# Revit family: QMXVP_with_1X2_Mixing_Box_Ends
name_source: partatom
category: Mechanical Equipment
units: mm (PartAtom-declared; Revit-internal decimal feet)

## family parameters
Always vertical = Yes
Cut with Voids When Loaded = No
Part Type = Normal
Room Calculation Point = No
Round Connector Dimension = Use Diameter
Shared = No
Work Plane-Based = No

## types (224) — shared parameters
0 = 0"
1" = 1"
1.5 = 1 1/2"
1/4 = 1/4"
135 = 135.00°
2" = 2"
2' = 24"
3" = 3"
3.125" = 3 1/8"
4" = 4"
5" = 5"
6" = 6"
Manufacturer = Loren Cook Company
ONE EIGTH = 1/8"
URL = www.lorencook.com

## per-type parameters (varying)
- 90_QMXVP-9L-1X2_Mixing_Box_Ends: (A/2)+.25"=14 1/4"; (A/2)+.5"=-14 1/2"; (A/2)-.5"=-13 1/2"; (A/2)-2"=12"; (NOZZLE_HEIGHT-(NOZZLE_HEIGHT/8*2))/2=10 1/2"; (NOZZLE_WB_OD-NOZZLE_TOP_OD)/2=2 3/8"; -A=-28"; A=28"; A+.5=28 1/2"; A/2=14"; B=65"; B/2=32 1/2"; C=30"; C/2=15"; DUAL_F=64"; DUAL_F+1"=65"; DUAL_G=63 5/16"; E=27 3/16"; GA=3/32"; LONG_RO=57 1/16"; LONG_RO/2=28 17/32"; MB_A=34"; MB_HT=29 3/16"; MB_HT+.25"=29 7/16"; MB_HT-2.75"=26 7/16"; MB_HT/2=14 19/32"; Model=QMXVP-1X2_Mixing Box_Sides; NOZZLE_BOTTOM_ID=12 13/16"; NOZZLE_BOTTOM_RAD=6 13/32"; NOZZLE_HEIGHT=28"; NOZZLE_HEIGHT/7*2=7"; NOZZLE_SIZE=108"; NOZZLE_TOP_OD=13 1/2"; NOZZLE_TOP_RAD=6 3/4"; NOZZLE_WB/4=4 19/32"; NOZZLE_WB_OD=23"; NOZZLE_WB_RAD=11 1/2"; NOZZLE_WB_RAD-2"=9 1/2"; RO=21"; RO/2=10 1/2"; RO2/2=10 1/2"; TRANSITION_TOP=37 1/16"; TYPE=0"; Type Comments=Vari-Plume Laboratory Exhaust Mixed-Flow Inline Belt Drive With 1X2 Mixing Box With Weather Hoods On Sides; UNIT_HEIGHT=19 7/8"; UNIT_HEIGHT*.75=14 29/32"; UNIT_OD=12 13/16"; UNIT_RAD+((A/2)+.25")=20 21/32"; UNIT_RAD+((A/2)+.25")+4"=24 21/32"; UNIT_RADIUS=6 13/32"; UNIT_RADIUS*.6=5 25/32"; UNIT_RADIUS+4"=10 13/32"
- 490_QMXVP-49H-1X2_Mixing_Box_Ends: (A/2)+.25"=40 1/4"; (A/2)+.5"=-40 1/2"; (A/2)-.5"=-39 1/2"; (A/2)-2"=38"; (NOZZLE_HEIGHT-(NOZZLE_HEIGHT/8*2))/2=41 1/4"; (NOZZLE_WB_OD-NOZZLE_TOP_OD)/2=6 1/4"; -A=-80"; A=80"; A+.5=80 1/2"; A/2=40"; B=219"; B/2=109 1/2"; C=103"; C/2=51 1/2"; DUAL_F=192"; DUAL_F+1"=193"; DUAL_G=191"; E=78 1/2"; GA=1/8"; LONG_RO=184 3/4"; LONG_RO/2=92 3/8"; MB_A=113"; MB_HT=86 15/16"; MB_HT+.25"=87 3/16"; MB_HT-2.75"=84 3/16"; MB_HT/2=43 15/32"; Model=QMXVP-1X2_Mixing Box_Sides; NOZZLE_BOTTOM_ID=69 3/8"; NOZZLE_BOTTOM_RAD=34 11/16"; NOZZLE_HEIGHT=110"; NOZZLE_HEIGHT/7*2=27 1/2"; NOZZLE_SIZE=588"; NOZZLE_TOP_OD=76"; NOZZLE_TOP_RAD=38"; NOZZLE_WB/4=20 3/16"; NOZZLE_WB_OD=101"; NOZZLE_WB_RAD=50 1/2"; NOZZLE_WB_RAD-2"=48 1/2"; RO=72 1/4"; RO/2=36 1/8"; RO2/2=36 1/8"; TRANSITION_TOP=96 3/4"; TYPE=0"; Type Comments=Vari-Plume Laboratory Exhaust Mixed-Flow Inline Belt Drive With 1X2 Mixing Box With Weather Hoods On Sides; UNIT_HEIGHT=80 1/2"; UNIT_HEIGHT*.75=60 3/8"; UNIT_OD=69 3/8"; UNIT_RAD+((A/2)+.25")=74 15/16"; UNIT_RAD+((A/2)+.25")+4"=78 15/16"; UNIT_RADIUS=34 11/16"; UNIT_RADIUS*.6=31 7/32"; UNIT_RADIUS+4"=38 11/16"
- 90_QMXVP-9H-1X2_Mixing_Box_Ends: (A/2)+.25"=14 1/4"; (A/2)+.5"=-14 1/2"; (A/2)-.5"=-13 1/2"; (A/2)-2"=12"; (NOZZLE_HEIGHT-(NOZZLE_HEIGHT/8*2))/2=10 1/2"; (NOZZLE_WB_OD-NOZZLE_TOP_OD)/2=2 3/8"; -A=-28"; A=28"; A+.5=28 1/2"; A/2=14"; B=65"; B/2=32 1/2"; C=30"; C/2=15"; DUAL_F=64"; DUAL_F+1"=65"; DUAL_G=63 5/16"; E=27 3/16"; GA=3/32"; LONG_RO=57 1/16"; LONG_RO/2=28 17/32"; MB_A=34"; MB_HT=29 3/16"; MB_HT+.25"=29 7/16"; MB_HT-2.75"=26 7/16"; MB_HT/2=14 19/32"; Model=QMXVP-1X2_Mixing Box_Sides; NOZZLE_BOTTOM_ID=12 13/16"; NOZZLE_BOTTOM_RAD=6 13/32"; NOZZLE_HEIGHT=28"; NOZZLE_HEIGHT/7*2=7"; NOZZLE_SIZE=108"; NOZZLE_TOP_OD=13 1/2"; NOZZLE_TOP_RAD=6 3/4"; NOZZLE_WB/4=4 19/32"; NOZZLE_WB_OD=23"; NOZZLE_WB_RAD=11 1/2"; NOZZLE_WB_RAD-2"=9 1/2"; RO=21"; RO/2=10 1/2"; RO2/2=10 1/2"; TRANSITION_TOP=37 1/16"; TYPE=0"; Type Comments=Vari-Plume Laboratory Exhaust Mixed-Flow Inline Belt Drive With 1X2 Mixing Box With Weather Hoods On Sides; UNIT_HEIGHT=19 7/8"; UNIT_HEIGHT*.75=14 29/32"; UNIT_OD=12 13/16"; UNIT_RAD+((A/2)+.25")=20 21/32"; UNIT_RAD+((A/2)+.25")+4"=24 21/32"; UNIT_RADIUS=6 13/32"; UNIT_RADIUS*.6=5 25/32"; UNIT_RADIUS+4"=10 13/32"
- 120_QMXVP-9L-1X2_Mixing_Box_Ends: (A/2)+.25"=14 1/4"; (A/2)+.5"=-14 1/2"; (A/2)-.5"=-13 1/2"; (A/2)-2"=12"; (NOZZLE_HEIGHT-(NOZZLE_HEIGHT/8*2))/2=10 1/2"; (NOZZLE_WB_OD-NOZZLE_TOP_OD)/2=2 3/8"; -A=-28"; A=28"; A+.5=28 1/2"; A/2=14"; B=71"; B/2=35 1/2"; C=37"; C/2=18 1/2"; DUAL_F=64"; DUAL_F+1"=65"; DUAL_G=63 5/16"; E=27 3/16"; GA=3/32"; LONG_RO=57 1/16"; LONG_RO/2=28 17/32"; MB_A=35"; MB_HT=31 7/16"; MB_HT+.25"=31 11/16"; MB_HT-2.75"=28 11/16"; MB_HT/2=15 23/32"; Model=QMXVP-1X2_Mixing Box_Sides; NOZZLE_BOTTOM_ID=12 13/16"; NOZZLE_BOTTOM_RAD=6 13/32"; NOZZLE_HEIGHT=28"; NOZZLE_HEIGHT/7*2=7"; NOZZLE_SIZE=108"; NOZZLE_TOP_OD=13 1/2"; NOZZLE_TOP_RAD=6 3/4"; NOZZLE_WB/4=4 19/32"; NOZZLE_WB_OD=23"; NOZZLE_WB_RAD=11 1/2"; NOZZLE_WB_RAD-2"=9 1/2"; RO=21"; RO/2=10 1/2"; RO2/2=10 1/2"; TRANSITION_TOP=43 3/16"; TYPE=0"; Type Comments=Vari-Plume Laboratory Exhaust Mixed-Flow Inline Belt Drive With 1X2 Mixing Box With Weather Hoods On Sides; UNIT_HEIGHT=19 7/8"; UNIT_HEIGHT*.75=14 29/32"; UNIT_OD=17 1/16"; UNIT_RAD+((A/2)+.25")=22 25/32"; UNIT_RAD+((A/2)+.25")+4"=26 25/32"; UNIT_RADIUS=8 17/32"; UNIT_RADIUS*.6=7 11/16"; UNIT_RADIUS+4"=12 17/32"
- 120_QMXVP-9H-1X2_Mixing_Box_Ends: (A/2)+.25"=14 1/4"; (A/2)+.5"=-14 1/2"; (A/2)-.5"=-13 1/2"; (A/2)-2"=12"; (NOZZLE_HEIGHT-(NOZZLE_HEIGHT/8*2))/2=10 1/2"; (NOZZLE_WB_OD-NOZZLE_TOP_OD)/2=2 3/8"; -A=-28"; A=28"; A+.5=28 1/2"; A/2=14"; B=71"; B/2=35 1/2"; C=37"; C/2=18 1/2"; DUAL_F=64"; DUAL_F+1"=65"; DUAL_G=63 5/16"; E=27 3/16"; GA=3/32"; LONG_RO=57 1/16"; LONG_RO/2=28 17/32"; MB_A=35"; MB_HT=31 7/16"; MB_HT+.25"=31 11/16"; MB_HT-2.75"=28 11/16"; MB_HT/2=15 23/32"; Model=QMXVP-1X2_Mixing Box_Sides; NOZZLE_BOTTOM_ID=12 13/16"; NOZZLE_BOTTOM_RAD=6 13/32"; NOZZLE_HEIGHT=28"; NOZZLE_HEIGHT/7*2=7"; NOZZLE_SIZE=108"; NOZZLE_TOP_OD=13 1/2"; NOZZLE_TOP_RAD=6 3/4"; NOZZLE_WB/4=4 19/32"; NOZZLE_WB_OD=23"; NOZZLE_WB_RAD=11 1/2"; NOZZLE_WB_RAD-2"=9 1/2"; RO=21"; RO/2=10 1/2"; RO2/2=10 1/2"; TRANSITION_TOP=43 3/16"; TYPE=0"; Type Comments=Vari-Plume Laboratory Exhaust Mixed-Flow Inline Belt Drive With 1X2 Mixing Box With Weather Hoods On Sides; UNIT_HEIGHT=19 7/8"; UNIT_HEIGHT*.75=14 29/32"; UNIT_OD=17 1/16"; UNIT_RAD+((A/2)+.25")=22 25/32"; UNIT_RAD+((A/2)+.25")+4"=26 25/32"; UNIT_RADIUS=8 17/32"; UNIT_RADIUS*.6=7 11/16"; UNIT_RADIUS+4"=12 17/32"
- 120_QMXVP-12L-1X2_Mixing_Box_Ends: (A/2)+.25"=14 1/4"; (A/2)+.5"=-14 1/2"; (A/2)-.5"=-13 1/2"; (A/2)-2"=12"; (NOZZLE_HEIGHT-(NOZZLE_HEIGHT/8*2))/2=12"; (NOZZLE_WB_OD-NOZZLE_TOP_OD)/2=2 1/8"; -A=-28"; A=28"; A+.5=28 1/2"; A/2=14"; B=71"; B/2=35 1/2"; C=37"; C/2=18 1/2"; DUAL_F=64"; DUAL_F+1"=65"; DUAL_G=63 5/16"; E=27 3/16"; GA=3/32"; LONG_RO=57 1/16"; LONG_RO/2=28 17/32"; MB_A=35"; MB_HT=31 7/16"; MB_HT+.25"=31 11/16"; MB_HT-2.75"=28 11/16"; MB_HT/2=15 23/32"; Model=QMXVP-1X2_Mixing Box_Sides; NOZZLE_BOTTOM_ID=17 1/16"; NOZZLE_BOTTOM_RAD=8 17/32"; NOZZLE_HEIGHT=32"; NOZZLE_HEIGHT/7*2=8"; NOZZLE_SIZE=144"; NOZZLE_TOP_OD=19 1/2"; NOZZLE_TOP_RAD=9 3/4"; NOZZLE_WB/4=5 19/32"; NOZZLE_WB_OD=28"; NOZZLE_WB_RAD=14"; NOZZLE_WB_RAD-2"=12"; RO=21"; RO/2=10 1/2"; RO2/2=10 1/2"; TRANSITION_TOP=39 7/16"; TYPE=0"; Type Comments=Vari-Plume Laboratory Exhaust Mixed-Flow Inline Belt Drive With 1X2 Mixing Box With Weather Hoods On Sides; UNIT_HEIGHT=19 7/8"; UNIT_HEIGHT*.75=14 29/32"; UNIT_OD=17 1/16"; UNIT_RAD+((A/2)+.25")=22 25/32"; UNIT_RAD+((A/2)+.25")+4"=26 25/32"; UNIT_RADIUS=8 17/32"; UNIT_RADIUS*.6=7 11/16"; UNIT_RADIUS+4"=12 17/32"
- 120_QMXVP-12H-1X2_Mixing_Box_Ends: (A/2)+.25"=14 1/4"; (A/2)+.5"=-14 1/2"; (A/2)-.5"=-13 1/2"; (A/2)-2"=12"; (NOZZLE_HEIGHT-(NOZZLE_HEIGHT/8*2))/2=12"; (NOZZLE_WB_OD-NOZZLE_TOP_OD)/2=2 1/8"; -A=-28"; A=28"; A+.5=28 1/2"; A/2=14"; B=71"; B/2=35 1/2"; C=37"; C/2=18 1/2"; DUAL_F=64"; DUAL_F+1"=65"; DUAL_G=63 5/16"; E=27 3/16"; GA=3/32"; LONG_RO=57 1/16"; LONG_RO/2=28 17/32"; MB_A=35"; MB_HT=31 7/16"; MB_HT+.25"=31 11/16"; MB_HT-2.75"=28 11/16"; MB_HT/2=15 23/32"; Model=QMXVP-1X2_Mixing Box_Sides; NOZZLE_BOTTOM_ID=17 1/16"; NOZZLE_BOTTOM_RAD=8 17/32"; NOZZLE_HEIGHT=32"; NOZZLE_HEIGHT/7*2=8"; NOZZLE_SIZE=144"; NOZZLE_TOP_OD=19 1/2"; NOZZLE_TOP_RAD=9 3/4"; NOZZLE_WB/4=5 19/32"; NOZZLE_WB_OD=28"; NOZZLE_WB_RAD=14"; NOZZLE_WB_RAD-2"=12"; RO=21"; RO/2=10 1/2"; RO2/2=10 1/2"; TRANSITION_TOP=39 7/16"; TYPE=0"; Type Comments=Vari-Plume Laboratory Exhaust Mixed-Flow Inline Belt Drive With 1X2 Mixing Box With Weather Hoods On Sides; UNIT_HEIGHT=19 7/8"; UNIT_HEIGHT*.75=14 29/32"; UNIT_OD=17 1/16"; UNIT_RAD+((A/2)+.25")=22 25/32"; UNIT_RAD+((A/2)+.25")+4"=26 25/32"; UNIT_RADIUS=8 17/32"; UNIT_RADIUS*.6=7 11/16"; UNIT_RADIUS+4"=12 17/32"
- 135_QMXVP-9L-1X2_Mixing_Box_Ends: (A/2)+.25"=14 1/4"; (A/2)+.5"=-14 1/2"; (A/2)-.5"=-13 1/2"; (A/2)-2"=12"; (NOZZLE_HEIGHT-(NOZZLE_HEIGHT/8*2))/2=10 1/2"; (NOZZLE_WB_OD-NOZZLE_TOP_OD)/2=2 3/8"; -A=-28"; A=28"; A+.5=28 1/2"; A/2=14"; B=77"; B/2=38 1/2"; C=39"; C/2=19 1/2"; DUAL_F=64"; DUAL_F+1"=65"; DUAL_G=63 5/16"; E=27 1/8"; GA=3/32"; LONG_RO=57 1/16"; LONG_RO/2=28 17/32"; MB_A=36"; MB_HT=33 7/16"; MB_HT+.25"=33 11/16"; MB_HT-2.75"=30 11/16"; MB_HT/2=16 23/32"; Model=QMXVP-1X2_Mixing Box_Sides; NOZZLE_BOTTOM_ID=12 13/16"; NOZZLE_BOTTOM_RAD=6 13/32"; NOZZLE_HEIGHT=28"; NOZZLE_HEIGHT/7*2=7"; NOZZLE_SIZE=108"; NOZZLE_TOP_OD=13 1/2"; NOZZLE_TOP_RAD=6 3/4"; NOZZLE_WB/4=4 19/32"; NOZZLE_WB_OD=23"; NOZZLE_WB_RAD=11 1/2"; NOZZLE_WB_RAD-2"=9 1/2"; RO=20 15/16"; RO/2=10 15/32"; RO2/2=10 15/32"; TRANSITION_TOP=48 11/16"; TYPE=0"; Type Comments=Vari-Plume Laboratory Exhaust Mixed-Flow Inline Belt Drive With 1X2 Mixing Box With Weather Hoods On Sides; UNIT_HEIGHT=27"; UNIT_HEIGHT*.75=20 1/4"; UNIT_OD=19 1/4"; UNIT_RAD+((A/2)+.25")=23 7/8"; UNIT_RAD+((A/2)+.25")+4"=27 7/8"; UNIT_RADIUS=9 5/8"; UNIT_RADIUS*.6=8 21/32"; UNIT_RADIUS+4"=13 5/8"
- 135_QMXVP-9H-1X2_Mixing_Box_Ends: (A/2)+.25"=14 1/4"; (A/2)+.5"=-14 1/2"; (A/2)-.5"=-13 1/2"; (A/2)-2"=12"; (NOZZLE_HEIGHT-(NOZZLE_HEIGHT/8*2))/2=10 1/2"; (NOZZLE_WB_OD-NOZZLE_TOP_OD)/2=2 3/8"; -A=-28"; A=28"; A+.5=28 1/2"; A/2=14"; B=77"; B/2=38 1/2"; C=39"; C/2=19 1/2"; DUAL_F=64"; DUAL_F+1"=65"; DUAL_G=63 5/16"; E=27 1/8"; GA=3/32"; LONG_RO=57 1/16"; LONG_RO/2=28 17/32"; MB_A=36"; MB_HT=33 7/16"; MB_HT+.25"=33 11/16"; MB_HT-2.75"=30 11/16"; MB_HT/2=16 23/32"; Model=QMXVP-1X2_Mixing Box_Sides; NOZZLE_BOTTOM_ID=12 13/16"; NOZZLE_BOTTOM_RAD=6 13/32"; NOZZLE_HEIGHT=28"; NOZZLE_HEIGHT/7*2=7"; NOZZLE_SIZE=108"; NOZZLE_TOP_OD=13 1/2"; NOZZLE_TOP_RAD=6 3/4"; NOZZLE_WB/4=4 19/32"; NOZZLE_WB_OD=23"; NOZZLE_WB_RAD=11 1/2"; NOZZLE_WB_RAD-2"=9 1/2"; RO=20 15/16"; RO/2=10 15/32"; RO2/2=10 15/32"; TRANSITION_TOP=48 11/16"; TYPE=0"; Type Comments=Vari-Plume Laboratory Exhaust Mixed-Flow Inline Belt Drive With 1X2 Mixing Box With Weather Hoods On Sides; UNIT_HEIGHT=27"; UNIT_HEIGHT*.75=20 1/4"; UNIT_OD=19 1/4"; UNIT_RAD+((A/2)+.25")=23 7/8"; UNIT_RAD+((A/2)+.25")+4"=27 7/8"; UNIT_RADIUS=9 5/8"; UNIT_RADIUS*.6=8 21/32"; UNIT_RADIUS+4"=13 5/8"
- 150_QMXVP-9L-1X2_Mixing_Box_Ends: (A/2)+.25"=15 1/4"; (A/2)+.5"=-15 1/2"; (A/2)-.5"=-14 1/2"; (A/2)-2"=13"; (NOZZLE_HEIGHT-(NOZZLE_HEIGHT/8*2))/2=10 1/2"; (NOZZLE_WB_OD-NOZZLE_TOP_OD)/2=2 3/8"; -A=-30"; A=30"; A+.5=30 1/2"; A/2=15"; B=87"; B/2=43 1/2"; C=42"; C/2=21"; DUAL_F=68"; DUAL_F+1"=69"; DUAL_G=67 5/16"; E=29 1/8"; GA=3/32"; LONG_RO=61 1/16"; LONG_RO/2=30 17/32"; MB_A=38"; MB_HT=35 3/16"; MB_HT+.25"=35 7/16"; MB_HT-2.75"=32 7/16"; MB_HT/2=17 19/32"; Model=QMXVP-1X2_Mixing Box_Sides; NOZZLE_BOTTOM_ID=12 13/16"; NOZZLE_BOTTOM_RAD=6 13/32"; NOZZLE_HEIGHT=28"; NOZZLE_HEIGHT/7*2=7"; NOZZLE_SIZE=108"; NOZZLE_TOP_OD=13 1/2"; NOZZLE_TOP_RAD=6 3/4"; NOZZLE_WB/4=4 19/32"; NOZZLE_WB_OD=23"; NOZZLE_WB_RAD=11 1/2"; NOZZLE_WB_RAD-2"=9 1/2"; RO=22 15/16"; RO/2=11 15/32"; RO2/2=11 15/32"; TRANSITION_TOP=54 1/4"; TYPE=0"; Type Comments=Vari-Plume Laboratory Exhaust Mixed-Flow Inline Belt Drive With 1X2 Mixing Box With Weather Hoods On Sides; UNIT_HEIGHT=30"; UNIT_HEIGHT*.75=22 1/2"; UNIT_OD=21 3/8"; UNIT_RAD+((A/2)+.25")=25 15/16"; UNIT_RAD+((A/2)+.25")+4"=29 15/16"; UNIT_RADIUS=10 11/16"; UNIT_RADIUS*.6=9 5/8"; UNIT_RADIUS+4"=14 11/16"
- 135_QMXVP-12L-1X2_Mixing_Box_Ends: (A/2)+.25"=14 1/4"; (A/2)+.5"=-14 1/2"; (A/2)-.5"=-13 1/2"; (A/2)-2"=12"; (NOZZLE_HEIGHT-(NOZZLE_HEIGHT/8*2))/2=12"; (NOZZLE_WB_OD-NOZZLE_TOP_OD)/2=2 1/8"; -A=-28"; A=28"; A+.5=28 1/2"; A/2=14"; B=77"; B/2=38 1/2"; C=39"; C/2=19 1/2"; DUAL_F=64"; DUAL_F+1"=65"; DUAL_G=63 5/16"; E=27 1/8"; GA=3/32"; LONG_RO=57 1/16"; LONG_RO/2=28 17/32"; MB_A=36"; MB_HT=33 7/16"; MB_HT+.25"=33 11/16"; MB_HT-2.75"=30 11/16"; MB_HT/2=16 23/32"; Model=QMXVP-1X2_Mixing Box_Sides; NOZZLE_BOTTOM_ID=17 1/16"; NOZZLE_BOTTOM_RAD=8 17/32"; NOZZLE_HEIGHT=32"; NOZZLE_HEIGHT/7*2=8"; NOZZLE_SIZE=144"; NOZZLE_TOP_OD=19 1/2"; NOZZLE_TOP_RAD=9 3/4"; NOZZLE_WB/4=5 19/32"; NOZZLE_WB_OD=28"; NOZZLE_WB_RAD=14"; NOZZLE_WB_RAD-2"=12"; RO=20 15/16"; RO/2=10 15/32"; RO2/2=10 15/32"; TRANSITION_TOP=40 11/16"; TYPE=0"; Type Comments=Vari-Plume Laboratory Exhaust Mixed-Flow Inline Belt Drive With 1X2 Mixing Box With Weather Hoods On Sides; UNIT_HEIGHT=27"; UNIT_HEIGHT*.75=20 1/4"; UNIT_OD=19 1/4"; UNIT_RAD+((A/2)+.25")=23 7/8"; UNIT_RAD+((A/2)+.25")+4"=27 7/8"; UNIT_RADIUS=9 5/8"; UNIT_RADIUS*.6=8 21/32"; UNIT_RADIUS+4"=13 5/8"
- 135_QMXVP-12H-1X2_Mixing_Box_Ends: (A/2)+.25"=14 1/4"; (A/2)+.5"=-14 1/2"; (A/2)-.5"=-13 1/2"; (A/2)-2"=12"; (NOZZLE_HEIGHT-(NOZZLE_HEIGHT/8*2))/2=12"; (NOZZLE_WB_OD-NOZZLE_TOP_OD)/2=2 1/8"; -A=-28"; A=28"; A+.5=28 1/2"; A/2=14"; B=77"; B/2=38 1/2"; C=39"; C/2=19 1/2"; DUAL_F=64"; DUAL_F+1"=65"; DUAL_G=63 5/16"; E=27 1/8"; GA=3/32"; LONG_RO=57 1/16"; LONG_RO/2=28 17/32"; MB_A=36"; MB_HT=33 7/16"; MB_HT+.25"=33 11/16"; MB_HT-2.75"=30 11/16"; MB_HT/2=16 23/32"; Model=QMXVP-1X2_Mixing Box_Sides; NOZZLE_BOTTOM_ID=17 1/16"; NOZZLE_BOTTOM_RAD=8 17/32"; NOZZLE_HEIGHT=32"; NOZZLE_HEIGHT/7*2=8"; NOZZLE_SIZE=144"; NOZZLE_TOP_OD=19 1/2"; NOZZLE_TOP_RAD=9 3/4"; NOZZLE_WB/4=5 19/32"; NOZZLE_WB_OD=28"; NOZZLE_WB_RAD=14"; NOZZLE_WB_RAD-2"=12"; RO=20 15/16"; RO/2=10 15/32"; RO2/2=10 15/32"; TRANSITION_TOP=40 11/16"; TYPE=0"; Type Comments=Vari-Plume Laboratory Exhaust Mixed-Flow Inline Belt Drive With 1X2 Mixing Box With Weather Hoods On Sides; UNIT_HEIGHT=27"; UNIT_HEIGHT*.75=20 1/4"; UNIT_OD=19 1/4"; UNIT_RAD+((A/2)+.25")=23 7/8"; UNIT_RAD+((A/2)+.25")+4"=27 7/8"; UNIT_RADIUS=9 5/8"; UNIT_RADIUS*.6=8 21/32"; UNIT_RADIUS+4"=13 5/8"
- 150_QMXVP-9H-1X2_Mixing_Box_Ends: (A/2)+.25"=15 1/4"; (A/2)+.5"=-15 1/2"; (A/2)-.5"=-14 1/2"; (A/2)-2"=13"; (NOZZLE_HEIGHT-(NOZZLE_HEIGHT/8*2))/2=10 1/2"; (NOZZLE_WB_OD-NOZZLE_TOP_OD)/2=2 3/8"; -A=-30"; A=30"; A+.5=30 1/2"; A/2=15"; B=87"; B/2=43 1/2"; C=42"; C/2=21"; DUAL_F=68"; DUAL_F+1"=69"; DUAL_G=67 5/16"; E=29 1/8"; GA=3/32"; LONG_RO=61 1/16"; LONG_RO/2=30 17/32"; MB_A=38"; MB_HT=35 3/16"; MB_HT+.25"=35 7/16"; MB_HT-2.75"=32 7/16"; MB_HT/2=17 19/32"; Model=QMXVP-1X2_Mixing Box_Sides; NOZZLE_BOTTOM_ID=12 13/16"; NOZZLE_BOTTOM_RAD=6 13/32"; NOZZLE_HEIGHT=28"; NOZZLE_HEIGHT/7*2=7"; NOZZLE_SIZE=108"; NOZZLE_TOP_OD=13 1/2"; NOZZLE_TOP_RAD=6 3/4"; NOZZLE_WB/4=4 19/32"; NOZZLE_WB_OD=23"; NOZZLE_WB_RAD=11 1/2"; NOZZLE_WB_RAD-2"=9 1/2"; RO=22 15/16"; RO/2=11 15/32"; RO2/2=11 15/32"; TRANSITION_TOP=54 1/4"; TYPE=0"; Type Comments=Vari-Plume Laboratory Exhaust Mixed-Flow Inline Belt Drive With 1X2 Mixing Box With Weather Hoods On Sides; UNIT_HEIGHT=30"; UNIT_HEIGHT*.75=22 1/2"; UNIT_OD=21 3/8"; UNIT_RAD+((A/2)+.25")=25 15/16"; UNIT_RAD+((A/2)+.25")+4"=29 15/16"; UNIT_RADIUS=10 11/16"; UNIT_RADIUS*.6=9 5/8"; UNIT_RADIUS+4"=14 11/16"
- 150_QMXVP-12L-1X2_Mixing_Box_Ends: (A/2)+.25"=15 1/4"; (A/2)+.5"=-15 1/2"; (A/2)-.5"=-14 1/2"; (A/2)-2"=13"; (NOZZLE_HEIGHT-(NOZZLE_HEIGHT/8*2))/2=12"; (NOZZLE_WB_OD-NOZZLE_TOP_OD)/2=2 1/8"; -A=-30"; A=30"; A+.5=30 1/2"; A/2=15"; B=87"; B/2=43 1/2"; C=42"; C/2=21"; DUAL_F=68"; DUAL_F+1"=69"; DUAL_G=67 5/16"; E=29 1/8"; GA=3/32"; LONG_RO=61 1/16"; LONG_RO/2=30 17/32"; MB_A=38"; MB_HT=35 3/16"; MB_HT+.25"=35 7/16"; MB_HT-2.75"=32 7/16"; MB_HT/2=17 19/32"; Model=QMXVP-1X2_Mixing Box_Sides; NOZZLE_BOTTOM_ID=17 1/16"; NOZZLE_BOTTOM_RAD=8 17/32"; NOZZLE_HEIGHT=32"; NOZZLE_HEIGHT/7*2=8"; NOZZLE_SIZE=144"; NOZZLE_TOP_OD=19 1/2"; NOZZLE_TOP_RAD=9 3/4"; NOZZLE_WB/4=5 19/32"; NOZZLE_WB_OD=28"; NOZZLE_WB_RAD=14"; NOZZLE_WB_RAD-2"=12"; RO=22 15/16"; RO/2=11 15/32"; RO2/2=11 15/32"; TRANSITION_TOP=46 1/4"; TYPE=0"; Type Comments=Vari-Plume Laboratory Exhaust Mixed-Flow Inline Belt Drive With 1X2 Mixing Box With Weather Hoods On Sides; UNIT_HEIGHT=30"; UNIT_HEIGHT*.75=22 1/2"; UNIT_OD=21 3/8"; UNIT_RAD+((A/2)+.25")=25 15/16"; UNIT_RAD+((A/2)+.25")+4"=29 15/16"; UNIT_RADIUS=10 11/16"; UNIT_RADIUS*.6=9 5/8"; UNIT_RADIUS+4"=14 11/16"
- 150_QMXVP-12H-1X2_Mixing_Box_Ends: (A/2)+.25"=15 1/4"; (A/2)+.5"=-15 1/2"; (A/2)-.5"=-14 1/2"; (A/2)-2"=13"; (NOZZLE_HEIGHT-(NOZZLE_HEIGHT/8*2))/2=12"; (NOZZLE_WB_OD-NOZZLE_TOP_OD)/2=2 1/8"; -A=-30"; A=30"; A+.5=30 1/2"; A/2=15"; B=87"; B/2=43 1/2"; C=42"; C/2=21"; DUAL_F=68"; DUAL_F+1"=69"; DUAL_G=67 5/16"; E=29 1/8"; GA=3/32"; LONG_RO=61 1/16"; LONG_RO/2=30 17/32"; MB_A=38"; MB_HT=35 3/16"; MB_HT+.25"=35 7/16"; MB_HT-2.75"=32 7/16"; MB_HT/2=17 19/32"; Model=QMXVP-1X2_Mixing Box_Sides; NOZZLE_BOTTOM_ID=17 1/16"; NOZZLE_BOTTOM_RAD=8 17/32"; NOZZLE_HEIGHT=32"; NOZZLE_HEIGHT/7*2=8"; NOZZLE_SIZE=144"; NOZZLE_TOP_OD=19 1/2"; NOZZLE_TOP_RAD=9 3/4"; NOZZLE_WB/4=5 19/32"; NOZZLE_WB_OD=28"; NOZZLE_WB_RAD=14"; NOZZLE_WB_RAD-2"=12"; RO=22 15/16"; RO/2=11 15/32"; RO2/2=11 15/32"; TRANSITION_TOP=46 1/4"; TYPE=0"; Type Comments=Vari-Plume Laboratory Exhaust Mixed-Flow Inline Belt Drive With 1X2 Mixing Box With Weather Hoods On Sides; UNIT_HEIGHT=30"; UNIT_HEIGHT*.75=22 1/2"; UNIT_OD=21 3/8"; UNIT_RAD+((A/2)+.25")=25 15/16"; UNIT_RAD+((A/2)+.25")+4"=29 15/16"; UNIT_RADIUS=10 11/16"; UNIT_RADIUS*.6=9 5/8"; UNIT_RADIUS+4"=14 11/16"
- 150_QMXVP-15L-1X2_Mixing_Box_Ends: (A/2)+.25"=15 1/4"; (A/2)+.5"=-15 1/2"; (A/2)-.5"=-14 1/2"; (A/2)-2"=13"; (NOZZLE_HEIGHT-(NOZZLE_HEIGHT/8*2))/2=16 1/8"; (NOZZLE_WB_OD-NOZZLE_TOP_OD)/2=3 1/4"; -A=-30"; A=30"; A+.5=30 1/2"; A/2=15"; B=87"; B/2=43 1/2"; C=42"; C/2=21"; DUAL_F=68"; DUAL_F+1"=69"; DUAL_G=67 5/16"; E=29 1/8"; GA=3/32"; LONG_RO=61 1/16"; LONG_RO/2=30 17/32"; MB_A=38"; MB_HT=35 3/16"; MB_HT+.25"=35 7/16"; MB_HT-2.75"=32 7/16"; MB_HT/2=17 19/32"; Model=QMXVP-1X2_Mixing Box_Sides; NOZZLE_BOTTOM_ID=21 3/8"; NOZZLE_BOTTOM_RAD=10 11/16"; NOZZLE_HEIGHT=43"; NOZZLE_HEIGHT/7*2=10 3/4"; NOZZLE_SIZE=180"; NOZZLE_TOP_OD=23"; NOZZLE_TOP_RAD=11 1/2"; NOZZLE_WB/4=7 3/16"; NOZZLE_WB_OD=36"; NOZZLE_WB_RAD=18"; NOZZLE_WB_RAD-2"=16"; RO=22 15/16"; RO/2=11 15/32"; RO2/2=11 15/32"; TRANSITION_TOP=43 5/16"; TYPE=0"; Type Comments=Vari-Plume Laboratory Exhaust Mixed-Flow Inline Belt Drive With 1X2 Mixing Box With Weather Hoods On Sides; UNIT_HEIGHT=30"; UNIT_HEIGHT*.75=22 1/2"; UNIT_OD=21 3/8"; UNIT_RAD+((A/2)+.25")=25 15/16"; UNIT_RAD+((A/2)+.25")+4"=29 15/16"; UNIT_RADIUS=10 11/16"; UNIT_RADIUS*.6=9 5/8"; UNIT_RADIUS+4"=14 11/16"
- 150_QMXVP-15H-1X2_Mixing_Box_Ends: (A/2)+.25"=15 1/4"; (A/2)+.5"=-15 1/2"; (A/2)-.5"=-14 1/2"; (A/2)-2"=13"; (NOZZLE_HEIGHT-(NOZZLE_HEIGHT/8*2))/2=16 1/8"; (NOZZLE_WB_OD-NOZZLE_TOP_OD)/2=3 1/4"; -A=-30"; A=30"; A+.5=30 1/2"; A/2=15"; B=87"; B/2=43 1/2"; C=42"; C/2=21"; DUAL_F=68"; DUAL_F+1"=69"; DUAL_G=67 5/16"; E=29 1/8"; GA=3/32"; LONG_RO=61 1/16"; LONG_RO/2=30 17/32"; MB_A=38"; MB_HT=35 3/16"; MB_HT+.25"=35 7/16"; MB_HT-2.75"=32 7/16"; MB_HT/2=17 19/32"; Model=QMXVP-1X2_Mixing Box_Sides; NOZZLE_BOTTOM_ID=21 3/8"; NOZZLE_BOTTOM_RAD=10 11/16"; NOZZLE_HEIGHT=43"; NOZZLE_HEIGHT/7*2=10 3/4"; NOZZLE_SIZE=180"; NOZZLE_TOP_OD=23"; NOZZLE_TOP_RAD=11 1/2"; NOZZLE_WB/4=7 3/16"; NOZZLE_WB_OD=36"; NOZZLE_WB_RAD=18"; NOZZLE_WB_RAD-2"=16"; RO=22 15/16"; RO/2=11 15/32"; RO2/2=11 15/32"; TRANSITION_TOP=43 5/16"; TYPE=0"; Type Comments=Vari-Plume Laboratory Exhaust Mixed-Flow Inline Belt Drive With 1X2 Mixing Box With Weather Hoods On Sides; UNIT_HEIGHT=30"; UNIT_HEIGHT*.75=22 1/2"; UNIT_OD=21 3/8"; UNIT_RAD+((A/2)+.25")=25 15/16"; UNIT_RAD+((A/2)+.25")+4"=29 15/16"; UNIT_RADIUS=10 11/16"; UNIT_RADIUS*.6=9 5/8"; UNIT_RADIUS+4"=14 11/16"
- 165_QMXVP-9L-1X2_Mixing_Box_Ends: (A/2)+.25"=16 1/4"; (A/2)+.5"=-16 1/2"; (A/2)-.5"=-15 1/2"; (A/2)-2"=14"; (NOZZLE_HEIGHT-(NOZZLE_HEIGHT/8*2))/2=10 1/2"; (NOZZLE_WB_OD-NOZZLE_TOP_OD)/2=2 3/8"; -A=-32"; A=32"; A+.5=32 1/2"; A/2=16"; B=89"; B/2=44 1/2"; C=44"; C/2=22"; DUAL_F=72"; DUAL_F+1"=73"; DUAL_G=71 5/16"; E=31 1/8"; GA=3/32"; LONG_RO=65 1/16"; LONG_RO/2=32 17/32"; MB_A=41"; MB_HT=36 15/16"; MB_HT+.25"=37 3/16"; MB_HT-2.75"=34 3/16"; MB_HT/2=18 15/32"; Model=QMXVP-1X2_Mixing Box_Sides; NOZZLE_BOTTOM_ID=12 13/16"; NOZZLE_BOTTOM_RAD=6 13/32"; NOZZLE_HEIGHT=28"; NOZZLE_HEIGHT/7*2=7"; NOZZLE_SIZE=108"; NOZZLE_TOP_OD=13 1/2"; NOZZLE_TOP_RAD=6 3/4"; NOZZLE_WB/4=4 19/32"; NOZZLE_WB_OD=23"; NOZZLE_WB_RAD=11 1/2"; NOZZLE_WB_RAD-2"=9 1/2"; RO=24 15/16"; RO/2=12 15/32"; RO2/2=12 15/32"; TRANSITION_TOP=61 1/4"; TYPE=0"; Type Comments=Vari-Plume Laboratory Exhaust Mixed-Flow Inline Belt Drive With 1X2 Mixing Box With Weather Hoods On Sides; UNIT_HEIGHT=33"; UNIT_HEIGHT*.75=24 3/4"; UNIT_OD=23 1/2"; UNIT_RAD+((A/2)+.25")=28"; UNIT_RAD+((A/2)+.25")+4"=32"; UNIT_RADIUS=11 3/4"; UNIT_RADIUS*.6=10 9/16"; UNIT_RADIUS+4"=15 3/4"
- 165_QMXVP-9H-1X2_Mixing_Box_Ends: (A/2)+.25"=16 1/4"; (A/2)+.5"=-16 1/2"; (A/2)-.5"=-15 1/2"; (A/2)-2"=14"; (NOZZLE_HEIGHT-(NOZZLE_HEIGHT/8*2))/2=10 1/2"; (NOZZLE_WB_OD-NOZZLE_TOP_OD)/2=2 3/8"; -A=-32"; A=32"; A+.5=32 1/2"; A/2=16"; B=89"; B/2=44 1/2"; C=44"; C/2=22"; DUAL_F=72"; DUAL_F+1"=73"; DUAL_G=71 5/16"; E=31 1/8"; GA=3/32"; LONG_RO=65 1/16"; LONG_RO/2=32 17/32"; MB_A=41"; MB_HT=36 15/16"; MB_HT+.25"=37 3/16"; MB_HT-2.75"=34 3/16"; MB_HT/2=18 15/32"; Model=QMXVP-1X2_Mixing Box_Sides; NOZZLE_BOTTOM_ID=12 13/16"; NOZZLE_BOTTOM_RAD=6 13/32"; NOZZLE_HEIGHT=28"; NOZZLE_HEIGHT/7*2=7"; NOZZLE_SIZE=108"; NOZZLE_TOP_OD=13 1/2"; NOZZLE_TOP_RAD=6 3/4"; NOZZLE_WB/4=4 19/32"; NOZZLE_WB_OD=23"; NOZZLE_WB_RAD=11 1/2"; NOZZLE_WB_RAD-2"=9 1/2"; RO=24 15/16"; RO/2=12 15/32"; RO2/2=12 15/32"; TRANSITION_TOP=61 1/4"; TYPE=0"; Type Comments=Vari-Plume Laboratory Exhaust Mixed-Flow Inline Belt Drive With 1X2 Mixing Box With Weather Hoods On Sides; UNIT_HEIGHT=33"; UNIT_HEIGHT*.75=24 3/4"; UNIT_OD=23 1/2"; UNIT_RAD+((A/2)+.25")=28"; UNIT_RAD+((A/2)+.25")+4"=32"; UNIT_RADIUS=11 3/4"; UNIT_RADIUS*.6=10 9/16"; UNIT_RADIUS+4"=15 3/4"
- 165_QMXVP-12L-1X2_Mixing_Box_Ends: (A/2)+.25"=16 1/4"; (A/2)+.5"=-16 1/2"; (A/2)-.5"=-15 1/2"; (A/2)-2"=14"; (NOZZLE_HEIGHT-(NOZZLE_HEIGHT/8*2))/2=12"; (NOZZLE_WB_OD-NOZZLE_TOP_OD)/2=2 1/8"; -A=-32"; A=32"; A+.5=32 1/2"; A/2=16"; B=89"; B/2=44 1/2"; C=44"; C/2=22"; DUAL_F=72"; DUAL_F+1"=73"; DUAL_G=71 5/16"; E=31 1/8"; GA=3/32"; LONG_RO=65 1/16"; LONG_RO/2=32 17/32"; MB_A=41"; MB_HT=36 15/16"; MB_HT+.25"=37 3/16"; MB_HT-2.75"=34 3/16"; MB_HT/2=18 15/32"; Model=QMXVP-1X2_Mixing Box_Sides; NOZZLE_BOTTOM_ID=17 1/16"; NOZZLE_BOTTOM_RAD=8 17/32"; NOZZLE_HEIGHT=32"; NOZZLE_HEIGHT/7*2=8"; NOZZLE_SIZE=144"; NOZZLE_TOP_OD=19 1/2"; NOZZLE_TOP_RAD=9 3/4"; NOZZLE_WB/4=5 19/32"; NOZZLE_WB_OD=28"; NOZZLE_WB_RAD=14"; NOZZLE_WB_RAD-2"=12"; RO=24 15/16"; RO/2=12 15/32"; RO2/2=12 15/32"; TRANSITION_TOP=53 1/4"; TYPE=0"; Type Comments=Vari-Plume Laboratory Exhaust Mixed-Flow Inline Belt Drive With 1X2 Mixing Box With Weather Hoods On Sides; UNIT_HEIGHT=33"; UNIT_HEIGHT*.75=24 3/4"; UNIT_OD=23 1/2"; UNIT_RAD+((A/2)+.25")=28"; UNIT_RAD+((A/2)+.25")+4"=32"; UNIT_RADIUS=11 3/4"; UNIT_RADIUS*.6=10 9/16"; UNIT_RADIUS+4"=15 3/4"
- 165_QMXVP-12H-1X2_Mixing_Box_Ends: (A/2)+.25"=16 1/4"; (A/2)+.5"=-16 1/2"; (A/2)-.5"=-15 1/2"; (A/2)-2"=14"; (NOZZLE_HEIGHT-(NOZZLE_HEIGHT/8*2))/2=12"; (NOZZLE_WB_OD-NOZZLE_TOP_OD)/2=2 1/8"; -A=-32"; A=32"; A+.5=32 1/2"; A/2=16"; B=89"; B/2=44 1/2"; C=44"; C/2=22"; DUAL_F=72"; DUAL_F+1"=73"; DUAL_G=71 5/16"; E=31 1/8"; GA=3/32"; LONG_RO=65 1/16"; LONG_RO/2=32 17/32"; MB_A=41"; MB_HT=36 15/16"; MB_HT+.25"=37 3/16"; MB_HT-2.75"=34 3/16"; MB_HT/2=18 15/32"; Model=QMXVP-1X2_Mixing Box_Sides; NOZZLE_BOTTOM_ID=17 1/16"; NOZZLE_BOTTOM_RAD=8 17/32"; NOZZLE_HEIGHT=32"; NOZZLE_HEIGHT/7*2=8"; NOZZLE_SIZE=144"; NOZZLE_TOP_OD=19 1/2"; NOZZLE_TOP_RAD=9 3/4"; NOZZLE_WB/4=5 19/32"; NOZZLE_WB_OD=28"; NOZZLE_WB_RAD=14"; NOZZLE_WB_RAD-2"=12"; RO=24 15/16"; RO/2=12 15/32"; RO2/2=12 15/32"; TRANSITION_TOP=53 1/4"; TYPE=0"; Type Comments=Vari-Plume Laboratory Exhaust Mixed-Flow Inline Belt Drive With 1X2 Mixing Box With Weather Hoods On Sides; UNIT_HEIGHT=33"; UNIT_HEIGHT*.75=24 3/4"; UNIT_OD=23 1/2"; UNIT_RAD+((A/2)+.25")=28"; UNIT_RAD+((A/2)+.25")+4"=32"; UNIT_RADIUS=11 3/4"; UNIT_RADIUS*.6=10 9/16"; UNIT_RADIUS+4"=15 3/4"
- 165_QMXVP-15L-1X2_Mixing_Box_Ends: (A/2)+.25"=16 1/4"; (A/2)+.5"=-16 1/2"; (A/2)-.5"=-15 1/2"; (A/2)-2"=14"; (NOZZLE_HEIGHT-(NOZZLE_HEIGHT/8*2))/2=16 1/8"; (NOZZLE_WB_OD-NOZZLE_TOP_OD)/2=3 1/4"; -A=-32"; A=32"; A+.5=32 1/2"; A/2=16"; B=89"; B/2=44 1/2"; C=44"; C/2=22"; DUAL_F=72"; DUAL_F+1"=73"; DUAL_G=71 5/16"; E=31 1/8"; GA=3/32"; LONG_RO=65 1/16"; LONG_RO/2=32 17/32"; MB_A=41"; MB_HT=36 15/16"; MB_HT+.25"=37 3/16"; MB_HT-2.75"=34 3/16"; MB_HT/2=18 15/32"; Model=QMXVP-1X2_Mixing Box_Sides; NOZZLE_BOTTOM_ID=21 3/8"; NOZZLE_BOTTOM_RAD=10 11/16"; NOZZLE_HEIGHT=43"; NOZZLE_HEIGHT/7*2=10 3/4"; NOZZLE_SIZE=180"; NOZZLE_TOP_OD=23"; NOZZLE_TOP_RAD=11 1/2"; NOZZLE_WB/4=7 3/16"; NOZZLE_WB_OD=36"; NOZZLE_WB_RAD=18"; NOZZLE_WB_RAD-2"=16"; RO=24 15/16"; RO/2=12 15/32"; RO2/2=12 15/32"; TRANSITION_TOP=45 5/16"; TYPE=0"; Type Comments=Vari-Plume Laboratory Exhaust Mixed-Flow Inline Belt Drive With 1X2 Mixing Box With Weather Hoods On Sides; UNIT_HEIGHT=33"; UNIT_HEIGHT*.75=24 3/4"; UNIT_OD=23 1/2"; UNIT_RAD+((A/2)+.25")=28"; UNIT_RAD+((A/2)+.25")+4"=32"; UNIT_RADIUS=11 3/4"; UNIT_RADIUS*.6=10 9/16"; UNIT_RADIUS+4"=15 3/4"
- 165_QMXVP-15H-1X2_Mixing_Box_Ends: (A/2)+.25"=16 1/4"; (A/2)+.5"=-16 1/2"; (A/2)-.5"=-15 1/2"; (A/2)-2"=14"; (NOZZLE_HEIGHT-(NOZZLE_HEIGHT/8*2))/2=16 1/8"; (NOZZLE_WB_OD-NOZZLE_TOP_OD)/2=3 1/4"; -A=-32"; A=32"; A+.5=32 1/2"; A/2=16"; B=89"; B/2=44 1/2"; C=44"; C/2=22"; DUAL_F=72"; DUAL_F+1"=73"; DUAL_G=71 5/16"; E=31 1/8"; GA=3/32"; LONG_RO=65 1/16"; LONG_RO/2=32 17/32"; MB_A=41"; MB_HT=36 15/16"; MB_HT+.25"=37 3/16"; MB_HT-2.75"=34 3/16"; MB_HT/2=18 15/32"; Model=QMXVP-1X2_Mixing Box_Sides; NOZZLE_BOTTOM_ID=21 3/8"; NOZZLE_BOTTOM_RAD=10 11/16"; NOZZLE_HEIGHT=43"; NOZZLE_HEIGHT/7*2=10 3/4"; NOZZLE_SIZE=180"; NOZZLE_TOP_OD=23"; NOZZLE_TOP_RAD=11 1/2"; NOZZLE_WB/4=7 3/16"; NOZZLE_WB_OD=36"; NOZZLE_WB_RAD=18"; NOZZLE_WB_RAD-2"=16"; RO=24 15/16"; RO/2=12 15/32"; RO2/2=12 15/32"; TRANSITION_TOP=45 5/16"; TYPE=0"; Type Comments=Vari-Plume Laboratory Exhaust Mixed-Flow Inline Belt Drive With 1X2 Mixing Box With Weather Hoods On Sides; UNIT_HEIGHT=33"; UNIT_HEIGHT*.75=24 3/4"; UNIT_OD=23 1/2"; UNIT_RAD+((A/2)+.25")=28"; UNIT_RAD+((A/2)+.25")+4"=32"; UNIT_RADIUS=11 3/4"; UNIT_RADIUS*.6=10 9/16"; UNIT_RADIUS+4"=15 3/4"
- 180_QMXVP-12L-1X2_Mixing_Box_Ends: (A/2)+.25"=17 1/4"; (A/2)+.5"=-17 1/2"; (A/2)-.5"=-16 1/2"; (A/2)-2"=15"; (NOZZLE_HEIGHT-(NOZZLE_HEIGHT/8*2))/2=12"; (NOZZLE_WB_OD-NOZZLE_TOP_OD)/2=2 1/8"; -A=-34"; A=34"; A+.5=34 1/2"; A/2=17"; B=98"; B/2=49"; C=46"; C/2=23"; DUAL_F=84"; DUAL_F+1"=85"; DUAL_G=83 5/16"; E=33 1/8"; GA=3/32"; LONG_RO=77 1/16"; LONG_RO/2=38 17/32"; MB_A=44"; MB_HT=37 11/16"; MB_HT+.25"=37 15/16"; MB_HT-2.75"=34 15/16"; MB_HT/2=18 27/32"; Model=QMXVP-1X2_Mixing Box_Sides; NOZZLE_BOTTOM_ID=17 1/16"; NOZZLE_BOTTOM_RAD=8 17/32"; NOZZLE_HEIGHT=32"; NOZZLE_HEIGHT/7*2=8"; NOZZLE_SIZE=144"; NOZZLE_TOP_OD=19 1/2"; NOZZLE_TOP_RAD=9 3/4"; NOZZLE_WB/4=5 19/32"; NOZZLE_WB_OD=28"; NOZZLE_WB_RAD=14"; NOZZLE_WB_RAD-2"=12"; RO=26 15/16"; RO/2=13 15/32"; RO2/2=13 15/32"; TRANSITION_TOP=59 1/16"; TYPE=0"; Type Comments=Vari-Plume Laboratory Exhaust Mixed-Flow Inline Belt Drive With 1X2 Mixing Box With Weather Hoods On Sides; UNIT_HEIGHT=35"; UNIT_HEIGHT*.75=26 1/4"; UNIT_OD=25 5/8"; UNIT_RAD+((A/2)+.25")=30 1/16"; UNIT_RAD+((A/2)+.25")+4"=34 1/16"; UNIT_RADIUS=12 13/16"; UNIT_RADIUS*.6=11 17/32"; UNIT_RADIUS+4"=16 13/16"
- 180_QMXVP-12H-1X2_Mixing_Box_Ends: (A/2)+.25"=17 1/4"; (A/2)+.5"=-17 1/2"; (A/2)-.5"=-16 1/2"; (A/2)-2"=15"; (NOZZLE_HEIGHT-(NOZZLE_HEIGHT/8*2))/2=12"; (NOZZLE_WB_OD-NOZZLE_TOP_OD)/2=2 1/8"; -A=-34"; A=34"; A+.5=34 1/2"; A/2=17"; B=98"; B/2=49"; C=46"; C/2=23"; DUAL_F=84"; DUAL_F+1"=85"; DUAL_G=83 5/16"; E=33 1/8"; GA=3/32"; LONG_RO=77 1/16"; LONG_RO/2=38 17/32"; MB_A=44"; MB_HT=37 11/16"; MB_HT+.25"=37 15/16"; MB_HT-2.75"=34 15/16"; MB_HT/2=18 27/32"; Model=QMXVP-1X2_Mixing Box_Sides; NOZZLE_BOTTOM_ID=17 1/16"; NOZZLE_BOTTOM_RAD=8 17/32"; NOZZLE_HEIGHT=32"; NOZZLE_HEIGHT/7*2=8"; NOZZLE_SIZE=144"; NOZZLE_TOP_OD=19 1/2"; NOZZLE_TOP_RAD=9 3/4"; NOZZLE_WB/4=5 19/32"; NOZZLE_WB_OD=28"; NOZZLE_WB_RAD=14"; NOZZLE_WB_RAD-2"=12"; RO=26 15/16"; RO/2=13 15/32"; RO2/2=13 15/32"; TRANSITION_TOP=59 1/16"; TYPE=0"; Type Comments=Vari-Plume Laboratory Exhaust Mixed-Flow Inline Belt Drive With 1X2 Mixing Box With Weather Hoods On Sides; UNIT_HEIGHT=35"; UNIT_HEIGHT*.75=26 1/4"; UNIT_OD=25 5/8"; UNIT_RAD+((A/2)+.25")=30 1/16"; UNIT_RAD+((A/2)+.25")+4"=34 1/16"; UNIT_RADIUS=12 13/16"; UNIT_RADIUS*.6=11 17/32"; UNIT_RADIUS+4"=16 13/16"
- 180_QMXVP-15L-1X2_Mixing_Box_Ends: (A/2)+.25"=17 1/4"; (A/2)+.5"=-17 1/2"; (A/2)-.5"=-16 1/2"; (A/2)-2"=15"; (NOZZLE_HEIGHT-(NOZZLE_HEIGHT/8*2))/2=16 1/8"; (NOZZLE_WB_OD-NOZZLE_TOP_OD)/2=3 1/4"; -A=-34"; A=34"; A+.5=34 1/2"; A/2=17"; B=98"; B/2=49"; C=46"; C/2=23"; DUAL_F=84"; DUAL_F+1"=85"; DUAL_G=83 5/16"; E=33 1/8"; GA=3/32"; LONG_RO=77 1/16"; LONG_RO/2=38 17/32"; MB_A=44"; MB_HT=37 11/16"; MB_HT+.25"=37 15/16"; MB_HT-2.75"=34 15/16"; MB_HT/2=18 27/32"; Model=QMXVP-1X2_Mixing Box_Sides; NOZZLE_BOTTOM_ID=21 3/8"; NOZZLE_BOTTOM_RAD=10 11/16"; NOZZLE_HEIGHT=43"; NOZZLE_HEIGHT/7*2=10 3/4"; NOZZLE_SIZE=180"; NOZZLE_TOP_OD=23"; NOZZLE_TOP_RAD=11 1/2"; NOZZLE_WB/4=7 3/16"; NOZZLE_WB_OD=36"; NOZZLE_WB_RAD=18"; NOZZLE_WB_RAD-2"=16"; RO=26 15/16"; RO/2=13 15/32"; RO2/2=13 15/32"; TRANSITION_TOP=51 1/8"; TYPE=0"; Type Comments=Vari-Plume Laboratory Exhaust Mixed-Flow Inline Belt Drive With 1X2 Mixing Box With Weather Hoods On Sides; UNIT_HEIGHT=35"; UNIT_HEIGHT*.75=26 1/4"; UNIT_OD=25 5/8"; UNIT_RAD+((A/2)+.25")=30 1/16"; UNIT_RAD+((A/2)+.25")+4"=34 1/16"; UNIT_RADIUS=12 13/16"; UNIT_RADIUS*.6=11 17/32"; UNIT_RADIUS+4"=16 13/16"
- 180_QMXVP-15H-1X2_Mixing_Box_Ends: (A/2)+.25"=17 1/4"; (A/2)+.5"=-17 1/2"; (A/2)-.5"=-16 1/2"; (A/2)-2"=15"; (NOZZLE_HEIGHT-(NOZZLE_HEIGHT/8*2))/2=16 1/8"; (NOZZLE_WB_OD-NOZZLE_TOP_OD)/2=3 1/4"; -A=-34"; A=34"; A+.5=34 1/2"; A/2=17"; B=98"; B/2=49"; C=46"; C/2=23"; DUAL_F=84"; DUAL_F+1"=85"; DUAL_G=83 5/16"; E=33 1/8"; GA=3/32"; LONG_RO=77 1/16"; LONG_RO/2=38 17/32"; MB_A=44"; MB_HT=37 11/16"; MB_HT+.25"=37 15/16"; MB_HT-2.75"=34 15/16"; MB_HT/2=18 27/32"; Model=QMXVP-1X2_Mixing Box_Sides; NOZZLE_BOTTOM_ID=21 3/8"; NOZZLE_BOTTOM_RAD=10 11/16"; NOZZLE_HEIGHT=43"; NOZZLE_HEIGHT/7*2=10 3/4"; NOZZLE_SIZE=180"; NOZZLE_TOP_OD=23"; NOZZLE_TOP_RAD=11 1/2"; NOZZLE_WB/4=7 3/16"; NOZZLE_WB_OD=36"; NOZZLE_WB_RAD=18"; NOZZLE_WB_RAD-2"=16"; RO=26 15/16"; RO/2=13 15/32"; RO2/2=13 15/32"; TRANSITION_TOP=51 1/8"; TYPE=0"; Type Comments=Vari-Plume Laboratory Exhaust Mixed-Flow Inline Belt Drive With 1X2 Mixing Box With Weather Hoods On Sides; UNIT_HEIGHT=35"; UNIT_HEIGHT*.75=26 1/4"; UNIT_OD=25 5/8"; UNIT_RAD+((A/2)+.25")=30 1/16"; UNIT_RAD+((A/2)+.25")+4"=34 1/16"; UNIT_RADIUS=12 13/16"; UNIT_RADIUS*.6=11 17/32"; UNIT_RADIUS+4"=16 13/16"
- 180_QMXVP-18L-1X2_Mixing_Box_Ends: (A/2)+.25"=17 1/4"; (A/2)+.5"=-17 1/2"; (A/2)-.5"=-16 1/2"; (A/2)-2"=15"; (NOZZLE_HEIGHT-(NOZZLE_HEIGHT/8*2))/2=18"; (NOZZLE_WB_OD-NOZZLE_TOP_OD)/2=3 7/8"; -A=-34"; A=34"; A+.5=34 1/2"; A/2=17"; B=98"; B/2=49"; C=46"; C/2=23"; DUAL_F=84"; DUAL_F+1"=85"; DUAL_G=83 5/16"; E=33 1/8"; GA=3/32"; LONG_RO=77 1/16"; LONG_RO/2=38 17/32"; MB_A=44"; MB_HT=37 11/16"; MB_HT+.25"=37 15/16"; MB_HT-2.75"=34 15/16"; MB_HT/2=18 27/32"; Model=QMXVP-1X2_Mixing Box_Sides; NOZZLE_BOTTOM_ID=25 5/8"; NOZZLE_BOTTOM_RAD=12 13/16"; NOZZLE_HEIGHT=48"; NOZZLE_HEIGHT/7*2=12"; NOZZLE_SIZE=216"; NOZZLE_TOP_OD=27 1/2"; NOZZLE_TOP_RAD=13 3/4"; NOZZLE_WB/4=8 19/32"; NOZZLE_WB_OD=43"; NOZZLE_WB_RAD=21 1/2"; NOZZLE_WB_RAD-2"=19 1/2"; RO=26 15/16"; RO/2=13 15/32"; RO2/2=13 15/32"; TRANSITION_TOP=48 1/2"; TYPE=0"; Type Comments=Vari-Plume Laboratory Exhaust Mixed-Flow Inline Belt Drive With 1X2 Mixing Box With Weather Hoods On Sides; UNIT_HEIGHT=35"; UNIT_HEIGHT*.75=26 1/4"; UNIT_OD=25 5/8"; UNIT_RAD+((A/2)+.25")=30 1/16"; UNIT_RAD+((A/2)+.25")+4"=34 1/16"; UNIT_RADIUS=12 13/16"; UNIT_RADIUS*.6=11 17/32"; UNIT_RADIUS+4"=16 13/16"
- 180_QMXVP-18H-1X2_Mixing_Box_Ends: (A/2)+.25"=17 1/4"; (A/2)+.5"=-17 1/2"; (A/2)-.5"=-16 1/2"; (A/2)-2"=15"; (NOZZLE_HEIGHT-(NOZZLE_HEIGHT/8*2))/2=18"; (NOZZLE_WB_OD-NOZZLE_TOP_OD)/2=3 7/8"; -A=-34"; A=34"; A+.5=34 1/2"; A/2=17"; B=98"; B/2=49"; C=46"; C/2=23"; DUAL_F=84"; DUAL_F+1"=85"; DUAL_G=83 5/16"; E=33 1/8"; GA=3/32"; LONG_RO=77 1/16"; LONG_RO/2=38 17/32"; MB_A=44"; MB_HT=37 11/16"; MB_HT+.25"=37 15/16"; MB_HT-2.75"=34 15/16"; MB_HT/2=18 27/32"; Model=QMXVP-1X2_Mixing Box_Sides; NOZZLE_BOTTOM_ID=25 5/8"; NOZZLE_BOTTOM_RAD=12 13/16"; NOZZLE_HEIGHT=48"; NOZZLE_HEIGHT/7*2=12"; NOZZLE_SIZE=216"; NOZZLE_TOP_OD=27 1/2"; NOZZLE_TOP_RAD=13 3/4"; NOZZLE_WB/4=8 19/32"; NOZZLE_WB_OD=43"; NOZZLE_WB_RAD=21 1/2"; NOZZLE_WB_RAD-2"=19 1/2"; RO=26 15/16"; RO/2=13 15/32"; RO2/2=13 15/32"; TRANSITION_TOP=48 1/2"; TYPE=0"; Type Comments=Vari-Plume Laboratory Exhaust Mixed-Flow Inline Belt Drive With 1X2 Mixing Box With Weather Hoods On Sides; UNIT_HEIGHT=35"; UNIT_HEIGHT*.75=26 1/4"; UNIT_OD=25 5/8"; UNIT_RAD+((A/2)+.25")=30 1/16"; UNIT_RAD+((A/2)+.25")+4"=34 1/16"; UNIT_RADIUS=12 13/16"; UNIT_RADIUS*.6=11 17/32"; UNIT_RADIUS+4"=16 13/16"
- 202_QMXVP-12L-1X2_Mixing_Box_Ends: (A/2)+.25"=19 1/4"; (A/2)+.5"=-19 1/2"; (A/2)-.5"=-18 1/2"; (A/2)-2"=17"; (NOZZLE_HEIGHT-(NOZZLE_HEIGHT/8*2))/2=12"; (NOZZLE_WB_OD-NOZZLE_TOP_OD)/2=2 1/8"; -A=-38"; A=38"; A+.5=38 1/2"; A/2=19"; B=104"; B/2=52"; C=50"; C/2=25"; DUAL_F=90"; DUAL_F+1"=91"; DUAL_G=89 1/8"; E=36 15/16"; GA=3/32"; LONG_RO=82 7/8"; LONG_RO/2=41 7/16"; MB_A=49"; MB_HT=41 3/16"; MB_HT+.25"=41 7/16"; MB_HT-2.75"=38 7/16"; MB_HT/2=20 19/32"; Model=QMXVP-1X2_Mixing Box_Sides; NOZZLE_BOTTOM_ID=17 1/16"; NOZZLE_BOTTOM_RAD=8 17/32"; NOZZLE_HEIGHT=32"; NOZZLE_HEIGHT/7*2=8"; NOZZLE_SIZE=144"; NOZZLE_TOP_OD=19 1/2"; NOZZLE_TOP_RAD=9 3/4"; NOZZLE_WB/4=5 19/32"; NOZZLE_WB_OD=28"; NOZZLE_WB_RAD=14"; NOZZLE_WB_RAD-2"=12"; RO=30 3/4"; RO/2=15 3/8"; RO2/2=15 3/8"; TRANSITION_TOP=67 9/16"; TYPE=0"; Type Comments=Vari-Plume Laboratory Exhaust Mixed-Flow Inline Belt Drive With 1X2 Mixing Box With Weather Hoods On Sides; UNIT_HEIGHT=37 1/2"; UNIT_HEIGHT*.75=28 1/8"; UNIT_OD=28 3/4"; UNIT_RAD+((A/2)+.25")=33 5/8"; UNIT_RAD+((A/2)+.25")+4"=37 5/8"; UNIT_RADIUS=14 3/8"; UNIT_RADIUS*.6=12 15/16"; UNIT_RADIUS+4"=18 3/8"
- 202_QMXVP-12H-1X2_Mixing_Box_Ends: (A/2)+.25"=19 1/4"; (A/2)+.5"=-19 1/2"; (A/2)-.5"=-18 1/2"; (A/2)-2"=17"; (NOZZLE_HEIGHT-(NOZZLE_HEIGHT/8*2))/2=12"; (NOZZLE_WB_OD-NOZZLE_TOP_OD)/2=2 1/8"; -A=-38"; A=38"; A+.5=38 1/2"; A/2=19"; B=104"; B/2=52"; C=50"; C/2=25"; DUAL_F=90"; DUAL_F+1"=91"; DUAL_G=89 1/8"; E=36 15/16"; GA=3/32"; LONG_RO=82 7/8"; LONG_RO/2=41 7/16"; MB_A=49"; MB_HT=41 3/16"; MB_HT+.25"=41 7/16"; MB_HT-2.75"=38 7/16"; MB_HT/2=20 19/32"; Model=QMXVP-1X2_Mixing Box_Sides; NOZZLE_BOTTOM_ID=17 1/16"; NOZZLE_BOTTOM_RAD=8 17/32"; NOZZLE_HEIGHT=32"; NOZZLE_HEIGHT/7*2=8"; NOZZLE_SIZE=144"; NOZZLE_TOP_OD=19 1/2"; NOZZLE_TOP_RAD=9 3/4"; NOZZLE_WB/4=5 19/32"; NOZZLE_WB_OD=28"; NOZZLE_WB_RAD=14"; NOZZLE_WB_RAD-2"=12"; RO=30 3/4"; RO/2=15 3/8"; RO2/2=15 3/8"; TRANSITION_TOP=67 9/16"; TYPE=0"; Type Comments=Vari-Plume Laboratory Exhaust Mixed-Flow Inline Belt Drive With 1X2 Mixing Box With Weather Hoods On Sides; UNIT_HEIGHT=37 1/2"; UNIT_HEIGHT*.75=28 1/8"; UNIT_OD=28 3/4"; UNIT_RAD+((A/2)+.25")=33 5/8"; UNIT_RAD+((A/2)+.25")+4"=37 5/8"; UNIT_RADIUS=14 3/8"; UNIT_RADIUS*.6=12 15/16"; UNIT_RADIUS+4"=18 3/8"
- 202_QMXVP-15L-1X2_Mixing_Box_Ends: (A/2)+.25"=19 1/4"; (A/2)+.5"=-19 1/2"; (A/2)-.5"=-18 1/2"; (A/2)-2"=17"; (NOZZLE_HEIGHT-(NOZZLE_HEIGHT/8*2))/2=16 1/8"; (NOZZLE_WB_OD-NOZZLE_TOP_OD)/2=3 1/4"; -A=-38"; A=38"; A+.5=38 1/2"; A/2=19"; B=104"; B/2=52"; C=50"; C/2=25"; DUAL_F=90"; DUAL_F+1"=91"; DUAL_G=89 1/8"; E=36 15/16"; GA=3/32"; LONG_RO=82 7/8"; LONG_RO/2=41 7/16"; MB_A=49"; MB_HT=41 3/16"; MB_HT+.25"=41 7/16"; MB_HT-2.75"=38 7/16"; MB_HT/2=20 19/32"; Model=QMXVP-1X2_Mixing Box_Sides; NOZZLE_BOTTOM_ID=21 3/8"; NOZZLE_BOTTOM_RAD=10 11/16"; NOZZLE_HEIGHT=43"; NOZZLE_HEIGHT/7*2=10 3/4"; NOZZLE_SIZE=180"; NOZZLE_TOP_OD=23"; NOZZLE_TOP_RAD=11 1/2"; NOZZLE_WB/4=7 3/16"; NOZZLE_WB_OD=36"; NOZZLE_WB_RAD=18"; NOZZLE_WB_RAD-2"=16"; RO=30 3/4"; RO/2=15 3/8"; RO2/2=15 3/8"; TRANSITION_TOP=59 5/8"; TYPE=0"; Type Comments=Vari-Plume Laboratory Exhaust Mixed-Flow Inline Belt Drive With 1X2 Mixing Box With Weather Hoods On Sides; UNIT_HEIGHT=37 1/2"; UNIT_HEIGHT*.75=28 1/8"; UNIT_OD=28 3/4"; UNIT_RAD+((A/2)+.25")=33 5/8"; UNIT_RAD+((A/2)+.25")+4"=37 5/8"; UNIT_RADIUS=14 3/8"; UNIT_RADIUS*.6=12 15/16"; UNIT_RADIUS+4"=18 3/8"
- 202_QMXVP-15H-1X2_Mixing_Box_Ends: (A/2)+.25"=19 1/4"; (A/2)+.5"=-19 1/2"; (A/2)-.5"=-18 1/2"; (A/2)-2"=17"; (NOZZLE_HEIGHT-(NOZZLE_HEIGHT/8*2))/2=16 1/8"; (NOZZLE_WB_OD-NOZZLE_TOP_OD)/2=3 1/4"; -A=-38"; A=38"; A+.5=38 1/2"; A/2=19"; B=104"; B/2=52"; C=50"; C/2=25"; DUAL_F=90"; DUAL_F+1"=91"; DUAL_G=89 1/8"; E=36 15/16"; GA=3/32"; LONG_RO=82 7/8"; LONG_RO/2=41 7/16"; MB_A=49"; MB_HT=41 3/16"; MB_HT+.25"=41 7/16"; MB_HT-2.75"=38 7/16"; MB_HT/2=20 19/32"; Model=QMXVP-1X2_Mixing Box_Sides; NOZZLE_BOTTOM_ID=21 3/8"; NOZZLE_BOTTOM_RAD=10 11/16"; NOZZLE_HEIGHT=43"; NOZZLE_HEIGHT/7*2=10 3/4"; NOZZLE_SIZE=180"; NOZZLE_TOP_OD=23"; NOZZLE_TOP_RAD=11 1/2"; NOZZLE_WB/4=7 3/16"; NOZZLE_WB_OD=36"; NOZZLE_WB_RAD=18"; NOZZLE_WB_RAD-2"=16"; RO=30 3/4"; RO/2=15 3/8"; RO2/2=15 3/8"; TRANSITION_TOP=59 5/8"; TYPE=0"; Type Comments=Vari-Plume Laboratory Exhaust Mixed-Flow Inline Belt Drive With 1X2 Mixing Box With Weather Hoods On Sides; UNIT_HEIGHT=37 1/2"; UNIT_HEIGHT*.75=28 1/8"; UNIT_OD=28 3/4"; UNIT_RAD+((A/2)+.25")=33 5/8"; UNIT_RAD+((A/2)+.25")+4"=37 5/8"; UNIT_RADIUS=14 3/8"; UNIT_RADIUS*.6=12 15/16"; UNIT_RADIUS+4"=18 3/8"
- 202_QMXVP-18L-1X2_Mixing_Box_Ends: (A/2)+.25"=19 1/4"; (A/2)+.5"=-19 1/2"; (A/2)-.5"=-18 1/2"; (A/2)-2"=17"; (NOZZLE_HEIGHT-(NOZZLE_HEIGHT/8*2))/2=18"; (NOZZLE_WB_OD-NOZZLE_TOP_OD)/2=3 7/8"; -A=-38"; A=38"; A+.5=38 1/2"; A/2=19"; B=104"; B/2=52"; C=50"; C/2=25"; DUAL_F=90"; DUAL_F+1"=91"; DUAL_G=89 1/8"; E=36 15/16"; GA=3/32"; LONG_RO=82 7/8"; LONG_RO/2=41 7/16"; MB_A=49"; MB_HT=41 3/16"; MB_HT+.25"=41 7/16"; MB_HT-2.75"=38 7/16"; MB_HT/2=20 19/32"; Model=QMXVP-1X2_Mixing Box_Sides; NOZZLE_BOTTOM_ID=25 5/8"; NOZZLE_BOTTOM_RAD=12 13/16"; NOZZLE_HEIGHT=48"; NOZZLE_HEIGHT/7*2=12"; NOZZLE_SIZE=216"; NOZZLE_TOP_OD=27 1/2"; NOZZLE_TOP_RAD=13 3/4"; NOZZLE_WB/4=8 19/32"; NOZZLE_WB_OD=43"; NOZZLE_WB_RAD=21 1/2"; NOZZLE_WB_RAD-2"=19 1/2"; RO=30 3/4"; RO/2=15 3/8"; RO2/2=15 3/8"; TRANSITION_TOP=51 5/8"; TYPE=0"; Type Comments=Vari-Plume Laboratory Exhaust Mixed-Flow Inline Belt Drive With 1X2 Mixing Box With Weather Hoods On Sides; UNIT_HEIGHT=37 1/2"; UNIT_HEIGHT*.75=28 1/8"; UNIT_OD=28 3/4"; UNIT_RAD+((A/2)+.25")=33 5/8"; UNIT_RAD+((A/2)+.25")+4"=37 5/8"; UNIT_RADIUS=14 3/8"; UNIT_RADIUS*.6=12 15/16"; UNIT_RADIUS+4"=18 3/8"
- 202_QMXVP-18H-1X2_Mixing_Box_Ends: (A/2)+.25"=19 1/4"; (A/2)+.5"=-19 1/2"; (A/2)-.5"=-18 1/2"; (A/2)-2"=17"; (NOZZLE_HEIGHT-(NOZZLE_HEIGHT/8*2))/2=18"; (NOZZLE_WB_OD-NOZZLE_TOP_OD)/2=3 7/8"; -A=-38"; A=38"; A+.5=38 1/2"; A/2=19"; B=104"; B/2=52"; C=50"; C/2=25"; DUAL_F=90"; DUAL_F+1"=91"; DUAL_G=89 1/8"; E=36 15/16"; GA=3/32"; LONG_RO=82 7/8"; LONG_RO/2=41 7/16"; MB_A=49"; MB_HT=41 3/16"; MB_HT+.25"=41 7/16"; MB_HT-2.75"=38 7/16"; MB_HT/2=20 19/32"; Model=QMXVP-1X2_Mixing Box_Sides; NOZZLE_BOTTOM_ID=25 5/8"; NOZZLE_BOTTOM_RAD=12 13/16"; NOZZLE_HEIGHT=48"; NOZZLE_HEIGHT/7*2=12"; NOZZLE_SIZE=216"; NOZZLE_TOP_OD=27 1/2"; NOZZLE_TOP_RAD=13 3/4"; NOZZLE_WB/4=8 19/32"; NOZZLE_WB_OD=43"; NOZZLE_WB_RAD=21 1/2"; NOZZLE_WB_RAD-2"=19 1/2"; RO=30 3/4"; RO/2=15 3/8"; RO2/2=15 3/8"; TRANSITION_TOP=51 5/8"; TYPE=0"; Type Comments=Vari-Plume Laboratory Exhaust Mixed-Flow Inline Belt Drive With 1X2 Mixing Box With Weather Hoods On Sides; UNIT_HEIGHT=37 1/2"; UNIT_HEIGHT*.75=28 1/8"; UNIT_OD=28 3/4"; UNIT_RAD+((A/2)+.25")=33 5/8"; UNIT_RAD+((A/2)+.25")+4"=37 5/8"; UNIT_RADIUS=14 3/8"; UNIT_RADIUS*.6=12 15/16"; UNIT_RADIUS+4"=18 3/8"
- 225_QMXVP-12L-1X2_Mixing_Box_Ends: (A/2)+.25"=21 1/4"; (A/2)+.5"=-21 1/2"; (A/2)-.5"=-20 1/2"; (A/2)-2"=19"; (NOZZLE_HEIGHT-(NOZZLE_HEIGHT/8*2))/2=12"; (NOZZLE_WB_OD-NOZZLE_TOP_OD)/2=2 1/8"; -A=-42"; A=42"; A+.5=42 1/2"; A/2=21"; B=113"; B/2=56 1/2"; C=56"; C/2=28"; DUAL_F=93"; DUAL_F+1"=94"; DUAL_G=92 1/8"; E=40 15/16"; GA=3/32"; LONG_RO=85 7/8"; LONG_RO/2=42 15/16"; MB_A=54"; MB_HT=43 3/16"; MB_HT+.25"=43 7/16"; MB_HT-2.75"=40 7/16"; MB_HT/2=21 19/32"; Model=QMXVP-1X2_Mixing Box_Sides; NOZZLE_BOTTOM_ID=17 1/16"; NOZZLE_BOTTOM_RAD=8 17/32"; NOZZLE_HEIGHT=32"; NOZZLE_HEIGHT/7*2=8"; NOZZLE_SIZE=144"; NOZZLE_TOP_OD=19 1/2"; NOZZLE_TOP_RAD=9 3/4"; NOZZLE_WB/4=5 19/32"; NOZZLE_WB_OD=28"; NOZZLE_WB_RAD=14"; NOZZLE_WB_RAD-2"=12"; RO=34 3/4"; RO/2=17 3/8"; RO2/2=17 3/8"; TRANSITION_TOP=77 1/16"; TYPE=0"; Type Comments=Vari-Plume Laboratory Exhaust Mixed-Flow Inline Belt Drive With 1X2 Mixing Box With Weather Hoods On Sides; UNIT_HEIGHT=41"; UNIT_HEIGHT*.75=30 3/4"; UNIT_OD=31 15/16"; UNIT_RAD+((A/2)+.25")=37 7/32"; UNIT_RAD+((A/2)+.25")+4"=41 7/32"; UNIT_RADIUS=15 31/32"; UNIT_RADIUS*.6=14 3/8"; UNIT_RADIUS+4"=19 31/32"
- 225_QMXVP-12H-1X2_Mixing_Box_Ends: (A/2)+.25"=21 1/4"; (A/2)+.5"=-21 1/2"; (A/2)-.5"=-20 1/2"; (A/2)-2"=19"; (NOZZLE_HEIGHT-(NOZZLE_HEIGHT/8*2))/2=12"; (NOZZLE_WB_OD-NOZZLE_TOP_OD)/2=2 1/8"; -A=-42"; A=42"; A+.5=42 1/2"; A/2=21"; B=113"; B/2=56 1/2"; C=56"; C/2=28"; DUAL_F=93"; DUAL_F+1"=94"; DUAL_G=92 1/8"; E=40 15/16"; GA=3/32"; LONG_RO=85 7/8"; LONG_RO/2=42 15/16"; MB_A=54"; MB_HT=43 3/16"; MB_HT+.25"=43 7/16"; MB_HT-2.75"=40 7/16"; MB_HT/2=21 19/32"; Model=QMXVP-1X2_Mixing Box_Sides; NOZZLE_BOTTOM_ID=17 1/16"; NOZZLE_BOTTOM_RAD=8 17/32"; NOZZLE_HEIGHT=32"; NOZZLE_HEIGHT/7*2=8"; NOZZLE_SIZE=144"; NOZZLE_TOP_OD=19 1/2"; NOZZLE_TOP_RAD=9 3/4"; NOZZLE_WB/4=5 19/32"; NOZZLE_WB_OD=28"; NOZZLE_WB_RAD=14"; NOZZLE_WB_RAD-2"=12"; RO=34 3/4"; RO/2=17 3/8"; RO2/2=17 3/8"; TRANSITION_TOP=77 1/16"; TYPE=0"; Type Comments=Vari-Plume Laboratory Exhaust Mixed-Flow Inline Belt Drive With 1X2 Mixing Box With Weather Hoods On Sides; UNIT_HEIGHT=41"; UNIT_HEIGHT*.75=30 3/4"; UNIT_OD=31 15/16"; UNIT_RAD+((A/2)+.25")=37 7/32"; UNIT_RAD+((A/2)+.25")+4"=41 7/32"; UNIT_RADIUS=15 31/32"; UNIT_RADIUS*.6=14 3/8"; UNIT_RADIUS+4"=19 31/32"
- 225_QMXVP-15L-1X2_Mixing_Box_Ends: (A/2)+.25"=21 1/4"; (A/2)+.5"=-21 1/2"; (A/2)-.5"=-20 1/2"; (A/2)-2"=19"; (NOZZLE_HEIGHT-(NOZZLE_HEIGHT/8*2))/2=16 1/8"; (NOZZLE_WB_OD-NOZZLE_TOP_OD)/2=3 1/4"; -A=-42"; A=42"; A+.5=42 1/2"; A/2=21"; B=113"; B/2=56 1/2"; C=56"; C/2=28"; DUAL_F=93"; DUAL_F+1"=94"; DUAL_G=92 1/8"; E=40 15/16"; GA=3/32"; LONG_RO=85 7/8"; LONG_RO/2=42 15/16"; MB_A=54"; MB_HT=43 3/16"; MB_HT+.25"=43 7/16"; MB_HT-2.75"=40 7/16"; MB_HT/2=21 19/32"; Model=QMXVP-1X2_Mixing Box_Sides; NOZZLE_BOTTOM_ID=21 3/8"; NOZZLE_BOTTOM_RAD=10 11/16"; NOZZLE_HEIGHT=43"; NOZZLE_HEIGHT/7*2=10 3/4"; NOZZLE_SIZE=180"; NOZZLE_TOP_OD=23"; NOZZLE_TOP_RAD=11 1/2"; NOZZLE_WB/4=7 3/16"; NOZZLE_WB_OD=36"; NOZZLE_WB_RAD=18"; NOZZLE_WB_RAD-2"=16"; RO=34 3/4"; RO/2=17 3/8"; RO2/2=17 3/8"; TRANSITION_TOP=69 1/8"; TYPE=0"; Type Comments=Vari-Plume Laboratory Exhaust Mixed-Flow Inline Belt Drive With 1X2 Mixing Box With Weather Hoods On Sides; UNIT_HEIGHT=41"; UNIT_HEIGHT*.75=30 3/4"; UNIT_OD=31 15/16"; UNIT_RAD+((A/2)+.25")=37 7/32"; UNIT_RAD+((A/2)+.25")+4"=41 7/32"; UNIT_RADIUS=15 31/32"; UNIT_RADIUS*.6=14 3/8"; UNIT_RADIUS+4"=19 31/32"
- 225_QMXVP-15H-1X2_Mixing_Box_Ends: (A/2)+.25"=21 1/4"; (A/2)+.5"=-21 1/2"; (A/2)-.5"=-20 1/2"; (A/2)-2"=19"; (NOZZLE_HEIGHT-(NOZZLE_HEIGHT/8*2))/2=16 1/8"; (NOZZLE_WB_OD-NOZZLE_TOP_OD)/2=3 1/4"; -A=-42"; A=42"; A+.5=42 1/2"; A/2=21"; B=113"; B/2=56 1/2"; C=56"; C/2=28"; DUAL_F=93"; DUAL_F+1"=94"; DUAL_G=92 1/8"; E=40 15/16"; GA=3/32"; LONG_RO=85 7/8"; LONG_RO/2=42 15/16"; MB_A=54"; MB_HT=43 3/16"; MB_HT+.25"=43 7/16"; MB_HT-2.75"=40 7/16"; MB_HT/2=21 19/32"; Model=QMXVP-1X2_Mixing Box_Sides; NOZZLE_BOTTOM_ID=21 3/8"; NOZZLE_BOTTOM_RAD=10 11/16"; NOZZLE_HEIGHT=43"; NOZZLE_HEIGHT/7*2=10 3/4"; NOZZLE_SIZE=180"; NOZZLE_TOP_OD=23"; NOZZLE_TOP_RAD=11 1/2"; NOZZLE_WB/4=7 3/16"; NOZZLE_WB_OD=36"; NOZZLE_WB_RAD=18"; NOZZLE_WB_RAD-2"=16"; RO=34 3/4"; RO/2=17 3/8"; RO2/2=17 3/8"; TRANSITION_TOP=69 1/8"; TYPE=0"; Type Comments=Vari-Plume Laboratory Exhaust Mixed-Flow Inline Belt Drive With 1X2 Mixing Box With Weather Hoods On Sides; UNIT_HEIGHT=41"; UNIT_HEIGHT*.75=30 3/4"; UNIT_OD=31 15/16"; UNIT_RAD+((A/2)+.25")=37 7/32"; UNIT_RAD+((A/2)+.25")+4"=41 7/32"; UNIT_RADIUS=15 31/32"; UNIT_RADIUS*.6=14 3/8"; UNIT_RADIUS+4"=19 31/32"
- 225_QMXVP-18L-1X2_Mixing_Box_Ends: (A/2)+.25"=21 1/4"; (A/2)+.5"=-21 1/2"; (A/2)-.5"=-20 1/2"; (A/2)-2"=19"; (NOZZLE_HEIGHT-(NOZZLE_HEIGHT/8*2))/2=18"; (NOZZLE_WB_OD-NOZZLE_TOP_OD)/2=3 7/8"; -A=-42"; A=42"; A+.5=42 1/2"; A/2=21"; B=113"; B/2=56 1/2"; C=56"; C/2=28"; DUAL_F=93"; DUAL_F+1"=94"; DUAL_G=92 1/8"; E=40 15/16"; GA=3/32"; LONG_RO=85 7/8"; LONG_RO/2=42 15/16"; MB_A=54"; MB_HT=43 3/16"; MB_HT+.25"=43 7/16"; MB_HT-2.75"=40 7/16"; MB_HT/2=21 19/32"; Model=QMXVP-1X2_Mixing Box_Sides; NOZZLE_BOTTOM_ID=25 5/8"; NOZZLE_BOTTOM_RAD=12 13/16"; NOZZLE_HEIGHT=48"; NOZZLE_HEIGHT/7*2=12"; NOZZLE_SIZE=216"; NOZZLE_TOP_OD=27 1/2"; NOZZLE_TOP_RAD=13 3/4"; NOZZLE_WB/4=8 19/32"; NOZZLE_WB_OD=43"; NOZZLE_WB_RAD=21 1/2"; NOZZLE_WB_RAD-2"=19 1/2"; RO=34 3/4"; RO/2=17 3/8"; RO2/2=17 3/8"; TRANSITION_TOP=61 1/8"; TYPE=0"; Type Comments=Vari-Plume Laboratory Exhaust Mixed-Flow Inline Belt Drive With 1X2 Mixing Box With Weather Hoods On Sides; UNIT_HEIGHT=41"; UNIT_HEIGHT*.75=30 3/4"; UNIT_OD=31 15/16"; UNIT_RAD+((A/2)+.25")=37 7/32"; UNIT_RAD+((A/2)+.25")+4"=41 7/32"; UNIT_RADIUS=15 31/32"; UNIT_RADIUS*.6=14 3/8"; UNIT_RADIUS+4"=19 31/32"
- 245_QMXVP-15L-1X2_Mixing_Box_Ends: (A/2)+.25"=22 1/4"; (A/2)+.5"=-22 1/2"; (A/2)-.5"=-21 1/2"; (A/2)-2"=20"; (NOZZLE_HEIGHT-(NOZZLE_HEIGHT/8*2))/2=16 1/8"; (NOZZLE_WB_OD-NOZZLE_TOP_OD)/2=3 1/4"; -A=-44"; A=44"; A+.5=44 1/2"; A/2=22"; B=121"; B/2=60 1/2"; C=59"; C/2=29 1/2"; DUAL_F=108"; DUAL_F+1"=109"; DUAL_G=107 1/8"; E=42 15/16"; GA=3/32"; LONG_RO=100 7/8"; LONG_RO/2=50 7/16"; MB_A=57"; MB_HT=45 7/16"; MB_HT+.25"=45 11/16"; MB_HT-2.75"=42 11/16"; MB_HT/2=22 23/32"; Model=QMXVP-1X2_Mixing Box_Sides; NOZZLE_BOTTOM_ID=21 3/8"; NOZZLE_BOTTOM_RAD=10 11/16"; NOZZLE_HEIGHT=43"; NOZZLE_HEIGHT/7*2=10 3/4"; NOZZLE_SIZE=180"; NOZZLE_TOP_OD=23"; NOZZLE_TOP_RAD=11 1/2"; NOZZLE_WB/4=7 3/16"; NOZZLE_WB_OD=36"; NOZZLE_WB_RAD=18"; NOZZLE_WB_RAD-2"=16"; RO=36 3/4"; RO/2=18 3/8"; RO2/2=18 3/8"; TRANSITION_TOP=77 11/16"; TYPE=0"; Type Comments=Vari-Plume Laboratory Exhaust Mixed-Flow Inline Belt Drive With 1X2 Mixing Box With Weather Hoods On Sides; UNIT_HEIGHT=44 1/2"; UNIT_HEIGHT*.75=33 3/8"; UNIT_OD=34 3/4"; UNIT_RAD+((A/2)+.25")=39 5/8"; UNIT_RAD+((A/2)+.25")+4"=43 5/8"; UNIT_RADIUS=17 3/8"; UNIT_RADIUS*.6=15 5/8"; UNIT_RADIUS+4"=21 3/8"
- 245_QMXVP-15H-1X2_Mixing_Box_Ends: (A/2)+.25"=22 1/4"; (A/2)+.5"=-22 1/2"; (A/2)-.5"=-21 1/2"; (A/2)-2"=20"; (NOZZLE_HEIGHT-(NOZZLE_HEIGHT/8*2))/2=16 1/8"; (NOZZLE_WB_OD-NOZZLE_TOP_OD)/2=3 1/4"; -A=-44"; A=44"; A+.5=44 1/2"; A/2=22"; B=121"; B/2=60 1/2"; C=59"; C/2=29 1/2"; DUAL_F=108"; DUAL_F+1"=109"; DUAL_G=107 1/8"; E=42 15/16"; GA=3/32"; LONG_RO=100 7/8"; LONG_RO/2=50 7/16"; MB_A=57"; MB_HT=45 7/16"; MB_HT+.25"=45 11/16"; MB_HT-2.75"=42 11/16"; MB_HT/2=22 23/32"; Model=QMXVP-1X2_Mixing Box_Sides; NOZZLE_BOTTOM_ID=21 3/8"; NOZZLE_BOTTOM_RAD=10 11/16"; NOZZLE_HEIGHT=43"; NOZZLE_HEIGHT/7*2=10 3/4"; NOZZLE_SIZE=180"; NOZZLE_TOP_OD=23"; NOZZLE_TOP_RAD=11 1/2"; NOZZLE_WB/4=7 3/16"; NOZZLE_WB_OD=36"; NOZZLE_WB_RAD=18"; NOZZLE_WB_RAD-2"=16"; RO=36 3/4"; RO/2=18 3/8"; RO2/2=18 3/8"; TRANSITION_TOP=77 11/16"; TYPE=0"; Type Comments=Vari-Plume Laboratory Exhaust Mixed-Flow Inline Belt Drive With 1X2 Mixing Box With Weather Hoods On Sides; UNIT_HEIGHT=44 1/2"; UNIT_HEIGHT*.75=33 3/8"; UNIT_OD=34 3/4"; UNIT_RAD+((A/2)+.25")=39 5/8"; UNIT_RAD+((A/2)+.25")+4"=43 5/8"; UNIT_RADIUS=17 3/8"; UNIT_RADIUS*.6=15 5/8"; UNIT_RADIUS+4"=21 3/8"
- 245_QMXVP-18L-1X2_Mixing_Box_Ends: (A/2)+.25"=22 1/4"; (A/2)+.5"=-22 1/2"; (A/2)-.5"=-21 1/2"; (A/2)-2"=20"; (NOZZLE_HEIGHT-(NOZZLE_HEIGHT/8*2))/2=18"; (NOZZLE_WB_OD-NOZZLE_TOP_OD)/2=3 7/8"; -A=-44"; A=44"; A+.5=44 1/2"; A/2=22"; B=121"; B/2=60 1/2"; C=59"; C/2=29 1/2"; DUAL_F=108"; DUAL_F+1"=109"; DUAL_G=107 1/8"; E=42 15/16"; GA=3/32"; LONG_RO=100 7/8"; LONG_RO/2=50 7/16"; MB_A=57"; MB_HT=45 7/16"; MB_HT+.25"=45 11/16"; MB_HT-2.75"=42 11/16"; MB_HT/2=22 23/32"; Model=QMXVP-1X2_Mixing Box_Sides; NOZZLE_BOTTOM_ID=25 5/8"; NOZZLE_BOTTOM_RAD=12 13/16"; NOZZLE_HEIGHT=48"; NOZZLE_HEIGHT/7*2=12"; NOZZLE_SIZE=216"; NOZZLE_TOP_OD=27 1/2"; NOZZLE_TOP_RAD=13 3/4"; NOZZLE_WB/4=8 19/32"; NOZZLE_WB_OD=43"; NOZZLE_WB_RAD=21 1/2"; NOZZLE_WB_RAD-2"=19 1/2"; RO=36 3/4"; RO/2=18 3/8"; RO2/2=18 3/8"; TRANSITION_TOP=69 11/16"; TYPE=0"; Type Comments=Vari-Plume Laboratory Exhaust Mixed-Flow Inline Belt Drive With 1X2 Mixing Box With Weather Hoods On Sides; UNIT_HEIGHT=44 1/2"; UNIT_HEIGHT*.75=33 3/8"; UNIT_OD=34 3/4"; UNIT_RAD+((A/2)+.25")=39 5/8"; UNIT_RAD+((A/2)+.25")+4"=43 5/8"; UNIT_RADIUS=17 3/8"; UNIT_RADIUS*.6=15 5/8"; UNIT_RADIUS+4"=21 3/8"
- 245_QMXVP-18H-1X2_Mixing_Box_Ends: (A/2)+.25"=22 1/4"; (A/2)+.5"=-22 1/2"; (A/2)-.5"=-21 1/2"; (A/2)-2"=20"; (NOZZLE_HEIGHT-(NOZZLE_HEIGHT/8*2))/2=18"; (NOZZLE_WB_OD-NOZZLE_TOP_OD)/2=3 7/8"; -A=-44"; A=44"; A+.5=44 1/2"; A/2=22"; B=121"; B/2=60 1/2"; C=59"; C/2=29 1/2"; DUAL_F=108"; DUAL_F+1"=109"; DUAL_G=107 1/8"; E=42 15/16"; GA=3/32"; LONG_RO=100 7/8"; LONG_RO/2=50 7/16"; MB_A=57"; MB_HT=45 7/16"; MB_HT+.25"=45 11/16"; MB_HT-2.75"=42 11/16"; MB_HT/2=22 23/32"; Model=QMXVP-1X2_Mixing Box_Sides; NOZZLE_BOTTOM_ID=25 5/8"; NOZZLE_BOTTOM_RAD=12 13/16"; NOZZLE_HEIGHT=48"; NOZZLE_HEIGHT/7*2=12"; NOZZLE_SIZE=216"; NOZZLE_TOP_OD=27 1/2"; NOZZLE_TOP_RAD=13 3/4"; NOZZLE_WB/4=8 19/32"; NOZZLE_WB_OD=43"; NOZZLE_WB_RAD=21 1/2"; NOZZLE_WB_RAD-2"=19 1/2"; RO=36 3/4"; RO/2=18 3/8"; RO2/2=18 3/8"; TRANSITION_TOP=69 11/16"; TYPE=0"; Type Comments=Vari-Plume Laboratory Exhaust Mixed-Flow Inline Belt Drive With 1X2 Mixing Box With Weather Hoods On Sides; UNIT_HEIGHT=44 1/2"; UNIT_HEIGHT*.75=33 3/8"; UNIT_OD=34 3/4"; UNIT_RAD+((A/2)+.25")=39 5/8"; UNIT_RAD+((A/2)+.25")+4"=43 5/8"; UNIT_RADIUS=17 3/8"; UNIT_RADIUS*.6=15 5/8"; UNIT_RADIUS+4"=21 3/8"
- 245_QMXVP-24L-1X2_Mixing_Box_Ends: (A/2)+.25"=22 1/4"; (A/2)+.5"=-22 1/2"; (A/2)-.5"=-21 1/2"; (A/2)-2"=20"; (NOZZLE_HEIGHT-(NOZZLE_HEIGHT/8*2))/2=23 1/4"; (NOZZLE_WB_OD-NOZZLE_TOP_OD)/2=6 1/8"; -A=-44"; A=44"; A+.5=44 1/2"; A/2=22"; B=121"; B/2=60 1/2"; C=59"; C/2=29 1/2"; DUAL_F=108"; DUAL_F+1"=109"; DUAL_G=107 1/8"; E=42 15/16"; GA=3/32"; LONG_RO=100 7/8"; LONG_RO/2=50 7/16"; MB_A=57"; MB_HT=45 7/16"; MB_HT+.25"=45 11/16"; MB_HT-2.75"=42 11/16"; MB_HT/2=22 23/32"; Model=QMXVP-1X2_Mixing Box_Sides; NOZZLE_BOTTOM_ID=34 3/4"; NOZZLE_BOTTOM_RAD=17 3/8"; NOZZLE_HEIGHT=62"; NOZZLE_HEIGHT/7*2=15 1/2"; NOZZLE_SIZE=288"; NOZZLE_TOP_OD=36 1/2"; NOZZLE_TOP_RAD=18 1/4"; NOZZLE_WB/4=12 3/16"; NOZZLE_WB_OD=61"; NOZZLE_WB_RAD=30 1/2"; NOZZLE_WB_RAD-2"=28 1/2"; RO=36 3/4"; RO/2=18 3/8"; RO2/2=18 3/8"; TRANSITION_TOP=57 3/4"; TYPE=0"; Type Comments=Vari-Plume Laboratory Exhaust Mixed-Flow Inline Belt Drive With 1X2 Mixing Box With Weather Hoods On Sides; UNIT_HEIGHT=44 1/2"; UNIT_HEIGHT*.75=33 3/8"; UNIT_OD=34 3/4"; UNIT_RAD+((A/2)+.25")=39 5/8"; UNIT_RAD+((A/2)+.25")+4"=43 5/8"; UNIT_RADIUS=17 3/8"; UNIT_RADIUS*.6=15 5/8"; UNIT_RADIUS+4"=21 3/8"
- 245_QMXVP-24H-1X2_Mixing_Box_Ends: (A/2)+.25"=22 1/4"; (A/2)+.5"=-22 1/2"; (A/2)-.5"=-21 1/2"; (A/2)-2"=20"; (NOZZLE_HEIGHT-(NOZZLE_HEIGHT/8*2))/2=23 1/4"; (NOZZLE_WB_OD-NOZZLE_TOP_OD)/2=6 1/8"; -A=-44"; A=44"; A+.5=44 1/2"; A/2=22"; B=121"; B/2=60 1/2"; C=59"; C/2=29 1/2"; DUAL_F=108"; DUAL_F+1"=109"; DUAL_G=107 1/8"; E=42 15/16"; GA=3/32"; LONG_RO=100 7/8"; LONG_RO/2=50 7/16"; MB_A=57"; MB_HT=45 7/16"; MB_HT+.25"=45 11/16"; MB_HT-2.75"=42 11/16"; MB_HT/2=22 23/32"; Model=QMXVP-1X2_Mixing Box_Sides; NOZZLE_BOTTOM_ID=34 3/4"; NOZZLE_BOTTOM_RAD=17 3/8"; NOZZLE_HEIGHT=62"; NOZZLE_HEIGHT/7*2=15 1/2"; NOZZLE_SIZE=288"; NOZZLE_TOP_OD=36 1/2"; NOZZLE_TOP_RAD=18 1/4"; NOZZLE_WB/4=12 3/16"; NOZZLE_WB_OD=61"; NOZZLE_WB_RAD=30 1/2"; NOZZLE_WB_RAD-2"=28 1/2"; RO=36 3/4"; RO/2=18 3/8"; RO2/2=18 3/8"; TRANSITION_TOP=57 3/4"; TYPE=0"; Type Comments=Vari-Plume Laboratory Exhaust Mixed-Flow Inline Belt Drive With 1X2 Mixing Box With Weather Hoods On Sides; UNIT_HEIGHT=44 1/2"; UNIT_HEIGHT*.75=33 3/8"; UNIT_OD=34 3/4"; UNIT_RAD+((A/2)+.25")=39 5/8"; UNIT_RAD+((A/2)+.25")+4"=43 5/8"; UNIT_RADIUS=17 3/8"; UNIT_RADIUS*.6=15 5/8"; UNIT_RADIUS+4"=21 3/8"
- 270_QMXVP-15L-1X2_Mixing_Box_Ends: (A/2)+.25"=24 1/4"; (A/2)+.5"=-24 1/2"; (A/2)-.5"=-23 1/2"; (A/2)-2"=22"; (NOZZLE_HEIGHT-(NOZZLE_HEIGHT/8*2))/2=16 1/8"; (NOZZLE_WB_OD-NOZZLE_TOP_OD)/2=3 1/4"; -A=-48"; A=48"; A+.5=48 1/2"; A/2=24"; B=128"; B/2=64"; C=63"; C/2=31 1/2"; DUAL_F=112"; DUAL_F+1"=113"; DUAL_G=111 1/8"; E=46 15/16"; GA=3/32"; LONG_RO=104 7/8"; LONG_RO/2=52 7/16"; MB_A=62"; MB_HT=47 3/16"; MB_HT+.25"=47 7/16"; MB_HT-2.75"=44 7/16"; MB_HT/2=23 19/32"; Model=QMXVP-1X2_Mixing Box_Sides; NOZZLE_BOTTOM_ID=21 3/8"; NOZZLE_BOTTOM_RAD=10 11/16"; NOZZLE_HEIGHT=43"; NOZZLE_HEIGHT/7*2=10 3/4"; NOZZLE_SIZE=180"; NOZZLE_TOP_OD=23"; NOZZLE_TOP_RAD=11 1/2"; NOZZLE_WB/4=7 3/16"; NOZZLE_WB_OD=36"; NOZZLE_WB_RAD=18"; NOZZLE_WB_RAD-2"=16"; RO=40 3/4"; RO/2=20 3/8"; RO2/2=20 3/8"; TRANSITION_TOP=86 3/16"; TYPE=0"; Type Comments=Vari-Plume Laboratory Exhaust Mixed-Flow Inline Belt Drive With 1X2 Mixing Box With Weather Hoods On Sides; UNIT_HEIGHT=47"; UNIT_HEIGHT*.75=35 1/4"; UNIT_OD=38 5/16"; UNIT_RAD+((A/2)+.25")=43 13/32"; UNIT_RAD+((A/2)+.25")+4"=47 13/32"; UNIT_RADIUS=19 5/32"; UNIT_RADIUS*.6=17 1/4"; UNIT_RADIUS+4"=23 5/32"
- 270_QMXVP-15H-1X2_Mixing_Box_Ends: (A/2)+.25"=24 1/4"; (A/2)+.5"=-24 1/2"; (A/2)-.5"=-23 1/2"; (A/2)-2"=22"; (NOZZLE_HEIGHT-(NOZZLE_HEIGHT/8*2))/2=16 1/8"; (NOZZLE_WB_OD-NOZZLE_TOP_OD)/2=3 1/4"; -A=-48"; A=48"; A+.5=48 1/2"; A/2=24"; B=128"; B/2=64"; C=63"; C/2=31 1/2"; DUAL_F=112"; DUAL_F+1"=113"; DUAL_G=111 1/8"; E=46 15/16"; GA=3/32"; LONG_RO=104 7/8"; LONG_RO/2=52 7/16"; MB_A=62"; MB_HT=47 3/16"; MB_HT+.25"=47 7/16"; MB_HT-2.75"=44 7/16"; MB_HT/2=23 19/32"; Model=QMXVP-1X2_Mixing Box_Sides; NOZZLE_BOTTOM_ID=21 3/8"; NOZZLE_BOTTOM_RAD=10 11/16"; NOZZLE_HEIGHT=43"; NOZZLE_HEIGHT/7*2=10 3/4"; NOZZLE_SIZE=180"; NOZZLE_TOP_OD=23"; NOZZLE_TOP_RAD=11 1/2"; NOZZLE_WB/4=7 3/16"; NOZZLE_WB_OD=36"; NOZZLE_WB_RAD=18"; NOZZLE_WB_RAD-2"=16"; RO=40 3/4"; RO/2=20 3/8"; RO2/2=20 3/8"; TRANSITION_TOP=86 3/16"; TYPE=0"; Type Comments=Vari-Plume Laboratory Exhaust Mixed-Flow Inline Belt Drive With 1X2 Mixing Box With Weather Hoods On Sides; UNIT_HEIGHT=47"; UNIT_HEIGHT*.75=35 1/4"; UNIT_OD=38 5/16"; UNIT_RAD+((A/2)+.25")=43 13/32"; UNIT_RAD+((A/2)+.25")+4"=47 13/32"; UNIT_RADIUS=19 5/32"; UNIT_RADIUS*.6=17 1/4"; UNIT_RADIUS+4"=23 5/32"
- 270_QMXVP-18L-1X2_Mixing_Box_Ends: (A/2)+.25"=24 1/4"; (A/2)+.5"=-24 1/2"; (A/2)-.5"=-23 1/2"; (A/2)-2"=22"; (NOZZLE_HEIGHT-(NOZZLE_HEIGHT/8*2))/2=18"; (NOZZLE_WB_OD-NOZZLE_TOP_OD)/2=3 7/8"; -A=-48"; A=48"; A+.5=48 1/2"; A/2=24"; B=128"; B/2=64"; C=63"; C/2=31 1/2"; DUAL_F=112"; DUAL_F+1"=113"; DUAL_G=111 1/8"; E=46 15/16"; GA=3/32"; LONG_RO=104 7/8"; LONG_RO/2=52 7/16"; MB_A=62"; MB_HT=47 3/16"; MB_HT+.25"=47 7/16"; MB_HT-2.75"=44 7/16"; MB_HT/2=23 19/32"; Model=QMXVP-1X2_Mixing Box_Sides; NOZZLE_BOTTOM_ID=25 5/8"; NOZZLE_BOTTOM_RAD=12 13/16"; NOZZLE_HEIGHT=48"; NOZZLE_HEIGHT/7*2=12"; NOZZLE_SIZE=216"; NOZZLE_TOP_OD=27 1/2"; NOZZLE_TOP_RAD=13 3/4"; NOZZLE_WB/4=8 19/32"; NOZZLE_WB_OD=43"; NOZZLE_WB_RAD=21 1/2"; NOZZLE_WB_RAD-2"=19 1/2"; RO=40 3/4"; RO/2=20 3/8"; RO2/2=20 3/8"; TRANSITION_TOP=79 3/16"; TYPE=0"; Type Comments=Vari-Plume Laboratory Exhaust Mixed-Flow Inline Belt Drive With 1X2 Mixing Box With Weather Hoods On Sides; UNIT_HEIGHT=47"; UNIT_HEIGHT*.75=35 1/4"; UNIT_OD=38 5/16"; UNIT_RAD+((A/2)+.25")=43 13/32"; UNIT_RAD+((A/2)+.25")+4"=47 13/32"; UNIT_RADIUS=19 5/32"; UNIT_RADIUS*.6=17 1/4"; UNIT_RADIUS+4"=23 5/32"
- 270_QMXVP-18H-1X2_Mixing_Box_Ends: (A/2)+.25"=24 1/4"; (A/2)+.5"=-24 1/2"; (A/2)-.5"=-23 1/2"; (A/2)-2"=22"; (NOZZLE_HEIGHT-(NOZZLE_HEIGHT/8*2))/2=18"; (NOZZLE_WB_OD-NOZZLE_TOP_OD)/2=3 7/8"; -A=-48"; A=48"; A+.5=48 1/2"; A/2=24"; B=128"; B/2=64"; C=63"; C/2=31 1/2"; DUAL_F=112"; DUAL_F+1"=113"; DUAL_G=111 1/8"; E=46 15/16"; GA=3/32"; LONG_RO=104 7/8"; LONG_RO/2=52 7/16"; MB_A=62"; MB_HT=47 3/16"; MB_HT+.25"=47 7/16"; MB_HT-2.75"=44 7/16"; MB_HT/2=23 19/32"; Model=QMXVP-1X2_Mixing Box_Sides; NOZZLE_BOTTOM_ID=25 5/8"; NOZZLE_BOTTOM_RAD=12 13/16"; NOZZLE_HEIGHT=48"; NOZZLE_HEIGHT/7*2=12"; NOZZLE_SIZE=216"; NOZZLE_TOP_OD=27 1/2"; NOZZLE_TOP_RAD=13 3/4"; NOZZLE_WB/4=8 19/32"; NOZZLE_WB_OD=43"; NOZZLE_WB_RAD=21 1/2"; NOZZLE_WB_RAD-2"=19 1/2"; RO=40 3/4"; RO/2=20 3/8"; RO2/2=20 3/8"; TRANSITION_TOP=79 3/16"; TYPE=0"; Type Comments=Vari-Plume Laboratory Exhaust Mixed-Flow Inline Belt Drive With 1X2 Mixing Box With Weather Hoods On Sides; UNIT_HEIGHT=47"; UNIT_HEIGHT*.75=35 1/4"; UNIT_OD=38 5/16"; UNIT_RAD+((A/2)+.25")=43 13/32"; UNIT_RAD+((A/2)+.25")+4"=47 13/32"; UNIT_RADIUS=19 5/32"; UNIT_RADIUS*.6=17 1/4"; UNIT_RADIUS+4"=23 5/32"
- 270_QMXVP-24L-1X2_Mixing_Box_Ends: (A/2)+.25"=24 1/4"; (A/2)+.5"=-24 1/2"; (A/2)-.5"=-23 1/2"; (A/2)-2"=22"; (NOZZLE_HEIGHT-(NOZZLE_HEIGHT/8*2))/2=23 1/4"; (NOZZLE_WB_OD-NOZZLE_TOP_OD)/2=6 1/8"; -A=-48"; A=48"; A+.5=48 1/2"; A/2=24"; B=128"; B/2=64"; C=63"; C/2=31 1/2"; DUAL_F=112"; DUAL_F+1"=113"; DUAL_G=111 1/8"; E=46 15/16"; GA=3/32"; LONG_RO=104 7/8"; LONG_RO/2=52 7/16"; MB_A=62"; MB_HT=47 3/16"; MB_HT+.25"=47 7/16"; MB_HT-2.75"=44 7/16"; MB_HT/2=23 19/32"; Model=QMXVP-1X2_Mixing Box_Sides; NOZZLE_BOTTOM_ID=34 3/4"; NOZZLE_BOTTOM_RAD=17 3/8"; NOZZLE_HEIGHT=62"; NOZZLE_HEIGHT/7*2=15 1/2"; NOZZLE_SIZE=288"; NOZZLE_TOP_OD=36 1/2"; NOZZLE_TOP_RAD=18 1/4"; NOZZLE_WB/4=12 3/16"; NOZZLE_WB_OD=61"; NOZZLE_WB_RAD=30 1/2"; NOZZLE_WB_RAD-2"=28 1/2"; RO=40 3/4"; RO/2=20 3/8"; RO2/2=20 3/8"; TRANSITION_TOP=62 1/4"; TYPE=0"; Type Comments=Vari-Plume Laboratory Exhaust Mixed-Flow Inline Belt Drive With 1X2 Mixing Box With Weather Hoods On Sides; UNIT_HEIGHT=47"; UNIT_HEIGHT*.75=35 1/4"; UNIT_OD=38 5/16"; UNIT_RAD+((A/2)+.25")=43 13/32"; UNIT_RAD+((A/2)+.25")+4"=47 13/32"; UNIT_RADIUS=19 5/32"; UNIT_RADIUS*.6=17 1/4"; UNIT_RADIUS+4"=23 5/32"
- 270_QMXVP-24H-1X2_Mixing_Box_Ends: (A/2)+.25"=24 1/4"; (A/2)+.5"=-24 1/2"; (A/2)-.5"=-23 1/2"; (A/2)-2"=22"; (NOZZLE_HEIGHT-(NOZZLE_HEIGHT/8*2))/2=23 1/4"; (NOZZLE_WB_OD-NOZZLE_TOP_OD)/2=6 1/8"; -A=-48"; A=48"; A+.5=48 1/2"; A/2=24"; B=128"; B/2=64"; C=63"; C/2=31 1/2"; DUAL_F=112"; DUAL_F+1"=113"; DUAL_G=111 1/8"; E=46 15/16"; GA=3/32"; LONG_RO=104 7/8"; LONG_RO/2=52 7/16"; MB_A=62"; MB_HT=47 3/16"; MB_HT+.25"=47 7/16"; MB_HT-2.75"=44 7/16"; MB_HT/2=23 19/32"; Model=QMXVP-1X2_Mixing Box_Sides; NOZZLE_BOTTOM_ID=34 3/4"; NOZZLE_BOTTOM_RAD=17 3/8"; NOZZLE_HEIGHT=62"; NOZZLE_HEIGHT/7*2=15 1/2"; NOZZLE_SIZE=288"; NOZZLE_TOP_OD=36 1/2"; NOZZLE_TOP_RAD=18 1/4"; NOZZLE_WB/4=12 3/16"; NOZZLE_WB_OD=61"; NOZZLE_WB_RAD=30 1/2"; NOZZLE_WB_RAD-2"=28 1/2"; RO=40 3/4"; RO/2=20 3/8"; RO2/2=20 3/8"; TRANSITION_TOP=62 1/4"; TYPE=0"; Type Comments=Vari-Plume Laboratory Exhaust Mixed-Flow Inline Belt Drive With 1X2 Mixing Box With Weather Hoods On Sides; UNIT_HEIGHT=47"; UNIT_HEIGHT*.75=35 1/4"; UNIT_OD=38 5/16"; UNIT_RAD+((A/2)+.25")=43 13/32"; UNIT_RAD+((A/2)+.25")+4"=47 13/32"; UNIT_RADIUS=19 5/32"; UNIT_RADIUS*.6=17 1/4"; UNIT_RADIUS+4"=23 5/32"
- 300_QMXVP-18L-1X2_Mixing_Box_Ends: (A/2)+.25"=26 1/4"; (A/2)+.5"=-26 1/2"; (A/2)-.5"=-25 1/2"; (A/2)-2"=24"; (NOZZLE_HEIGHT-(NOZZLE_HEIGHT/8*2))/2=18"; (NOZZLE_WB_OD-NOZZLE_TOP_OD)/2=3 7/8"; -A=-52"; A=52"; A+.5=52 1/2"; A/2=26"; B=148"; B/2=74"; C=67"; C/2=33 1/2"; DUAL_F=132"; DUAL_F+1"=133"; DUAL_G=131 1/8"; E=50 15/16"; GA=3/32"; LONG_RO=124 7/8"; LONG_RO/2=62 7/16"; MB_A=68"; MB_HT=50 7/16"; MB_HT+.25"=50 11/16"; MB_HT-2.75"=47 11/16"; MB_HT/2=25 7/32"; Model=QMXVP-1X2_Mixing Box_Sides; NOZZLE_BOTTOM_ID=25 5/8"; NOZZLE_BOTTOM_RAD=12 13/16"; NOZZLE_HEIGHT=48"; NOZZLE_HEIGHT/7*2=12"; NOZZLE_SIZE=216"; NOZZLE_TOP_OD=27 1/2"; NOZZLE_TOP_RAD=13 3/4"; NOZZLE_WB/4=8 19/32"; NOZZLE_WB_OD=43"; NOZZLE_WB_RAD=21 1/2"; NOZZLE_WB_RAD-2"=19 1/2"; RO=44 3/4"; RO/2=22 3/8"; RO2/2=22 3/8"; TRANSITION_TOP=94 3/16"; TYPE=0"; Type Comments=Vari-Plume Laboratory Exhaust Mixed-Flow Inline Belt Drive With 1X2 Mixing Box With Weather Hoods On Sides; UNIT_HEIGHT=54"; UNIT_HEIGHT*.75=40 1/2"; UNIT_OD=42 1/2"; UNIT_RAD+((A/2)+.25")=47 1/2"; UNIT_RAD+((A/2)+.25")+4"=51 1/2"; UNIT_RADIUS=21 1/4"; UNIT_RADIUS*.6=19 1/8"; UNIT_RADIUS+4"=25 1/4"
- 300_QMXVP-18H-1X2_Mixing_Box_Ends: (A/2)+.25"=26 1/4"; (A/2)+.5"=-26 1/2"; (A/2)-.5"=-25 1/2"; (A/2)-2"=24"; (NOZZLE_HEIGHT-(NOZZLE_HEIGHT/8*2))/2=18"; (NOZZLE_WB_OD-NOZZLE_TOP_OD)/2=3 7/8"; -A=-52"; A=52"; A+.5=52 1/2"; A/2=26"; B=148"; B/2=74"; C=67"; C/2=33 1/2"; DUAL_F=132"; DUAL_F+1"=133"; DUAL_G=131 1/8"; E=50 15/16"; GA=3/32"; LONG_RO=124 7/8"; LONG_RO/2=62 7/16"; MB_A=68"; MB_HT=50 7/16"; MB_HT+.25"=50 11/16"; MB_HT-2.75"=47 11/16"; MB_HT/2=25 7/32"; Model=QMXVP-1X2_Mixing Box_Sides; NOZZLE_BOTTOM_ID=25 5/8"; NOZZLE_BOTTOM_RAD=12 13/16"; NOZZLE_HEIGHT=48"; NOZZLE_HEIGHT/7*2=12"; NOZZLE_SIZE=216"; NOZZLE_TOP_OD=27 1/2"; NOZZLE_TOP_RAD=13 3/4"; NOZZLE_WB/4=8 19/32"; NOZZLE_WB_OD=43"; NOZZLE_WB_RAD=21 1/2"; NOZZLE_WB_RAD-2"=19 1/2"; RO=44 3/4"; RO/2=22 3/8"; RO2/2=22 3/8"; TRANSITION_TOP=94 3/16"; TYPE=0"; Type Comments=Vari-Plume Laboratory Exhaust Mixed-Flow Inline Belt Drive With 1X2 Mixing Box With Weather Hoods On Sides; UNIT_HEIGHT=54"; UNIT_HEIGHT*.75=40 1/2"; UNIT_OD=42 1/2"; UNIT_RAD+((A/2)+.25")=47 1/2"; UNIT_RAD+((A/2)+.25")+4"=51 1/2"; UNIT_RADIUS=21 1/4"; UNIT_RADIUS*.6=19 1/8"; UNIT_RADIUS+4"=25 1/4"
- 300_QMXVP-24L-1X2_Mixing_Box_Ends: (A/2)+.25"=26 1/4"; (A/2)+.5"=-26 1/2"; (A/2)-.5"=-25 1/2"; (A/2)-2"=24"; (NOZZLE_HEIGHT-(NOZZLE_HEIGHT/8*2))/2=23 1/4"; (NOZZLE_WB_OD-NOZZLE_TOP_OD)/2=6 1/8"; -A=-52"; A=52"; A+.5=52 1/2"; A/2=26"; B=148"; B/2=74"; C=67"; C/2=33 1/2"; DUAL_F=132"; DUAL_F+1"=133"; DUAL_G=131 1/8"; E=50 15/16"; GA=3/32"; LONG_RO=124 7/8"; LONG_RO/2=62 7/16"; MB_A=68"; MB_HT=50 7/16"; MB_HT+.25"=50 11/16"; MB_HT-2.75"=47 11/16"; MB_HT/2=25 7/32"; Model=QMXVP-1X2_Mixing Box_Sides; NOZZLE_BOTTOM_ID=34 3/4"; NOZZLE_BOTTOM_RAD=17 3/8"; NOZZLE_HEIGHT=62"; NOZZLE_HEIGHT/7*2=15 1/2"; NOZZLE_SIZE=288"; NOZZLE_TOP_OD=36 1/2"; NOZZLE_TOP_RAD=18 1/4"; NOZZLE_WB/4=12 3/16"; NOZZLE_WB_OD=61"; NOZZLE_WB_RAD=30 1/2"; NOZZLE_WB_RAD-2"=28 1/2"; RO=44 3/4"; RO/2=22 3/8"; RO2/2=22 3/8"; TRANSITION_TOP=77 1/4"; TYPE=0"; Type Comments=Vari-Plume Laboratory Exhaust Mixed-Flow Inline Belt Drive With 1X2 Mixing Box With Weather Hoods On Sides; UNIT_HEIGHT=54"; UNIT_HEIGHT*.75=40 1/2"; UNIT_OD=42 1/2"; UNIT_RAD+((A/2)+.25")=47 1/2"; UNIT_RAD+((A/2)+.25")+4"=51 1/2"; UNIT_RADIUS=21 1/4"; UNIT_RADIUS*.6=19 1/8"; UNIT_RADIUS+4"=25 1/4"
- 300_QMXVP-24H-1X2_Mixing_Box_Ends: (A/2)+.25"=26 1/4"; (A/2)+.5"=-26 1/2"; (A/2)-.5"=-25 1/2"; (A/2)-2"=24"; (NOZZLE_HEIGHT-(NOZZLE_HEIGHT/8*2))/2=23 1/4"; (NOZZLE_WB_OD-NOZZLE_TOP_OD)/2=6 1/8"; -A=-52"; A=52"; A+.5=52 1/2"; A/2=26"; B=148"; B/2=74"; C=67"; C/2=33 1/2"; DUAL_F=132"; DUAL_F+1"=133"; DUAL_G=131 1/8"; E=50 15/16"; GA=3/32"; LONG_RO=124 7/8"; LONG_RO/2=62 7/16"; MB_A=68"; MB_HT=50 7/16"; MB_HT+.25"=50 11/16"; MB_HT-2.75"=47 11/16"; MB_HT/2=25 7/32"; Model=QMXVP-1X2_Mixing Box_Sides; NOZZLE_BOTTOM_ID=34 3/4"; NOZZLE_BOTTOM_RAD=17 3/8"; NOZZLE_HEIGHT=62"; NOZZLE_HEIGHT/7*2=15 1/2"; NOZZLE_SIZE=288"; NOZZLE_TOP_OD=36 1/2"; NOZZLE_TOP_RAD=18 1/4"; NOZZLE_WB/4=12 3/16"; NOZZLE_WB_OD=61"; NOZZLE_WB_RAD=30 1/2"; NOZZLE_WB_RAD-2"=28 1/2"; RO=44 3/4"; RO/2=22 3/8"; RO2/2=22 3/8"; TRANSITION_TOP=77 1/4"; TYPE=0"; Type Comments=Vari-Plume Laboratory Exhaust Mixed-Flow Inline Belt Drive With 1X2 Mixing Box With Weather Hoods On Sides; UNIT_HEIGHT=54"; UNIT_HEIGHT*.75=40 1/2"; UNIT_OD=42 1/2"; UNIT_RAD+((A/2)+.25")=47 1/2"; UNIT_RAD+((A/2)+.25")+4"=51 1/2"; UNIT_RADIUS=21 1/4"; UNIT_RADIUS*.6=19 1/8"; UNIT_RADIUS+4"=25 1/4"
- 300_QMXVP-30L-1X2_Mixing_Box_Ends: (A/2)+.25"=26 1/4"; (A/2)+.5"=-26 1/2"; (A/2)-.5"=-25 1/2"; (A/2)-2"=24"; (NOZZLE_HEIGHT-(NOZZLE_HEIGHT/8*2))/2=29 1/4"; (NOZZLE_WB_OD-NOZZLE_TOP_OD)/2=7 1/8"; -A=-52"; A=52"; A+.5=52 1/2"; A/2=26"; B=148"; B/2=74"; C=67"; C/2=33 1/2"; DUAL_F=132"; DUAL_F+1"=133"; DUAL_G=131 1/8"; E=50 15/16"; GA=3/32"; LONG_RO=124 7/8"; LONG_RO/2=62 7/16"; MB_A=68"; MB_HT=50 7/16"; MB_HT+.25"=50 11/16"; MB_HT-2.75"=47 11/16"; MB_HT/2=25 7/32"; Model=QMXVP-1X2_Mixing Box_Sides; NOZZLE_BOTTOM_ID=42 1/2"; NOZZLE_BOTTOM_RAD=21 1/4"; NOZZLE_HEIGHT=78"; NOZZLE_HEIGHT/7*2=19 1/2"; NOZZLE_SIZE=360"; NOZZLE_TOP_OD=45 1/2"; NOZZLE_TOP_RAD=22 3/4"; NOZZLE_WB/4=14 13/16"; NOZZLE_WB_OD=74"; NOZZLE_WB_RAD=37"; NOZZLE_WB_RAD-2"=35"; RO=44 3/4"; RO/2=22 3/8"; RO2/2=22 3/8"; TRANSITION_TOP=68 1/4"; TYPE=0"; Type Comments=Vari-Plume Laboratory Exhaust Mixed-Flow Inline Belt Drive With 1X2 Mixing Box With Weather Hoods On Sides; UNIT_HEIGHT=54"; UNIT_HEIGHT*.75=40 1/2"; UNIT_OD=42 1/2"; UNIT_RAD+((A/2)+.25")=47 1/2"; UNIT_RAD+((A/2)+.25")+4"=51 1/2"; UNIT_RADIUS=21 1/4"; UNIT_RADIUS*.6=19 1/8"; UNIT_RADIUS+4"=25 1/4"
- 300_QMXVP-30H-1X2_Mixing_Box_Ends: (A/2)+.25"=26 1/4"; (A/2)+.5"=-26 1/2"; (A/2)-.5"=-25 1/2"; (A/2)-2"=24"; (NOZZLE_HEIGHT-(NOZZLE_HEIGHT/8*2))/2=29 1/4"; (NOZZLE_WB_OD-NOZZLE_TOP_OD)/2=7 1/8"; -A=-52"; A=52"; A+.5=52 1/2"; A/2=26"; B=148"; B/2=74"; C=67"; C/2=33 1/2"; DUAL_F=132"; DUAL_F+1"=133"; DUAL_G=131 1/8"; E=50 15/16"; GA=3/32"; LONG_RO=124 7/8"; LONG_RO/2=62 7/16"; MB_A=68"; MB_HT=50 7/16"; MB_HT+.25"=50 11/16"; MB_HT-2.75"=47 11/16"; MB_HT/2=25 7/32"; Model=QMXVP-1X2_Mixing Box_Sides; NOZZLE_BOTTOM_ID=42 1/2"; NOZZLE_BOTTOM_RAD=21 1/4"; NOZZLE_HEIGHT=78"; NOZZLE_HEIGHT/7*2=19 1/2"; NOZZLE_SIZE=360"; NOZZLE_TOP_OD=45 1/2"; NOZZLE_TOP_RAD=22 3/4"; NOZZLE_WB/4=14 13/16"; NOZZLE_WB_OD=74"; NOZZLE_WB_RAD=37"; NOZZLE_WB_RAD-2"=35"; RO=44 3/4"; RO/2=22 3/8"; RO2/2=22 3/8"; TRANSITION_TOP=68 1/4"; TYPE=0"; Type Comments=Vari-Plume Laboratory Exhaust Mixed-Flow Inline Belt Drive With 1X2 Mixing Box With Weather Hoods On Sides; UNIT_HEIGHT=54"; UNIT_HEIGHT*.75=40 1/2"; UNIT_OD=42 1/2"; UNIT_RAD+((A/2)+.25")=47 1/2"; UNIT_RAD+((A/2)+.25")+4"=51 1/2"; UNIT_RADIUS=21 1/4"; UNIT_RADIUS*.6=19 1/8"; UNIT_RADIUS+4"=25 1/4"
- 330_QMXVP-24L-1X2_Mixing_Box_Ends: (A/2)+.25"=28 1/4"; (A/2)+.5"=-28 1/2"; (A/2)-.5"=-27 1/2"; (A/2)-2"=26"; (NOZZLE_HEIGHT-(NOZZLE_HEIGHT/8*2))/2=23 1/4"; (NOZZLE_WB_OD-NOZZLE_TOP_OD)/2=6 1/8"; -A=-56"; A=56"; A+.5=56 1/2"; A/2=28"; B=154"; B/2=77"; C=73"; C/2=36 1/2"; DUAL_F=136"; DUAL_F+1"=137"; DUAL_G=135 1/8"; E=54 13/16"; GA=3/32"; LONG_RO=128 7/8"; LONG_RO/2=64 7/16"; MB_A=73"; MB_HT=53 11/16"; MB_HT+.25"=53 15/16"; MB_HT-2.75"=50 15/16"; MB_HT/2=26 27/32"; Model=QMXVP-1X2_Mixing Box_Sides; NOZZLE_BOTTOM_ID=34 3/4"; NOZZLE_BOTTOM_RAD=17 3/8"; NOZZLE_HEIGHT=62"; NOZZLE_HEIGHT/7*2=15 1/2"; NOZZLE_SIZE=288"; NOZZLE_TOP_OD=36 1/2"; NOZZLE_TOP_RAD=18 1/4"; NOZZLE_WB/4=12 3/16"; NOZZLE_WB_OD=61"; NOZZLE_WB_RAD=30 1/2"; NOZZLE_WB_RAD-2"=28 1/2"; RO=48 5/8"; RO/2=24 5/16"; RO2/2=24 5/16"; TRANSITION_TOP=89 3/4"; TYPE=0"; Type Comments=Vari-Plume Laboratory Exhaust Mixed-Flow Inline Belt Drive With 1X2 Mixing Box With Weather Hoods On Sides; UNIT_HEIGHT=58 1/2"; UNIT_HEIGHT*.75=43 7/8"; UNIT_OD=46 3/4"; UNIT_RAD+((A/2)+.25")=51 5/8"; UNIT_RAD+((A/2)+.25")+4"=55 5/8"; UNIT_RADIUS=23 3/8"; UNIT_RADIUS*.6=21 1/32"; UNIT_RADIUS+4"=27 3/8"
- 330_QMXVP-24H-1X2_Mixing_Box_Ends: (A/2)+.25"=28 1/4"; (A/2)+.5"=-28 1/2"; (A/2)-.5"=-27 1/2"; (A/2)-2"=26"; (NOZZLE_HEIGHT-(NOZZLE_HEIGHT/8*2))/2=23 1/4"; (NOZZLE_WB_OD-NOZZLE_TOP_OD)/2=6 1/8"; -A=-56"; A=56"; A+.5=56 1/2"; A/2=28"; B=154"; B/2=77"; C=73"; C/2=36 1/2"; DUAL_F=136"; DUAL_F+1"=137"; DUAL_G=135 1/8"; E=54 13/16"; GA=3/32"; LONG_RO=128 7/8"; LONG_RO/2=64 7/16"; MB_A=73"; MB_HT=53 11/16"; MB_HT+.25"=53 15/16"; MB_HT-2.75"=50 15/16"; MB_HT/2=26 27/32"; Model=QMXVP-1X2_Mixing Box_Sides; NOZZLE_BOTTOM_ID=34 3/4"; NOZZLE_BOTTOM_RAD=17 3/8"; NOZZLE_HEIGHT=62"; NOZZLE_HEIGHT/7*2=15 1/2"; NOZZLE_SIZE=288"; NOZZLE_TOP_OD=36 1/2"; NOZZLE_TOP_RAD=18 1/4"; NOZZLE_WB/4=12 3/16"; NOZZLE_WB_OD=61"; NOZZLE_WB_RAD=30 1/2"; NOZZLE_WB_RAD-2"=28 1/2"; RO=48 5/8"; RO/2=24 5/16"; RO2/2=24 5/16"; TRANSITION_TOP=89 3/4"; TYPE=0"; Type Comments=Vari-Plume Laboratory Exhaust Mixed-Flow Inline Belt Drive With 1X2 Mixing Box With Weather Hoods On Sides; UNIT_HEIGHT=58 1/2"; UNIT_HEIGHT*.75=43 7/8"; UNIT_OD=46 3/4"; UNIT_RAD+((A/2)+.25")=51 5/8"; UNIT_RAD+((A/2)+.25")+4"=55 5/8"; UNIT_RADIUS=23 3/8"; UNIT_RADIUS*.6=21 1/32"; UNIT_RADIUS+4"=27 3/8"
- 330_QMXVP-30L-1X2_Mixing_Box_Ends: (A/2)+.25"=28 1/4"; (A/2)+.5"=-28 1/2"; (A/2)-.5"=-27 1/2"; (A/2)-2"=26"; (NOZZLE_HEIGHT-(NOZZLE_HEIGHT/8*2))/2=29 1/4"; (NOZZLE_WB_OD-NOZZLE_TOP_OD)/2=7 1/8"; -A=-56"; A=56"; A+.5=56 1/2"; A/2=28"; B=154"; B/2=77"; C=73"; C/2=36 1/2"; DUAL_F=136"; DUAL_F+1"=137"; DUAL_G=135 1/8"; E=54 13/16"; GA=3/32"; LONG_RO=128 7/8"; LONG_RO/2=64 7/16"; MB_A=73"; MB_HT=53 11/16"; MB_HT+.25"=53 15/16"; MB_HT-2.75"=50 15/16"; MB_HT/2=26 27/32"; Model=QMXVP-1X2_Mixing Box_Sides; NOZZLE_BOTTOM_ID=42 1/2"; NOZZLE_BOTTOM_RAD=21 1/4"; NOZZLE_HEIGHT=78"; NOZZLE_HEIGHT/7*2=19 1/2"; NOZZLE_SIZE=360"; NOZZLE_TOP_OD=45 1/2"; NOZZLE_TOP_RAD=22 3/4"; NOZZLE_WB/4=14 13/16"; NOZZLE_WB_OD=74"; NOZZLE_WB_RAD=37"; NOZZLE_WB_RAD-2"=35"; RO=48 5/8"; RO/2=24 5/16"; RO2/2=24 5/16"; TRANSITION_TOP=74 3/4"; TYPE=0"; Type Comments=Vari-Plume Laboratory Exhaust Mixed-Flow Inline Belt Drive With 1X2 Mixing Box With Weather Hoods On Sides; UNIT_HEIGHT=58 1/2"; UNIT_HEIGHT*.75=43 7/8"; UNIT_OD=46 3/4"; UNIT_RAD+((A/2)+.25")=51 5/8"; UNIT_RAD+((A/2)+.25")+4"=55 5/8"; UNIT_RADIUS=23 3/8"; UNIT_RADIUS*.6=21 1/32"; UNIT_RADIUS+4"=27 3/8"
- 330_QMXVP-30H-1X2_Mixing_Box_Ends: (A/2)+.25"=28 1/4"; (A/2)+.5"=-28 1/2"; (A/2)-.5"=-27 1/2"; (A/2)-2"=26"; (NOZZLE_HEIGHT-(NOZZLE_HEIGHT/8*2))/2=29 1/4"; (NOZZLE_WB_OD-NOZZLE_TOP_OD)/2=7 1/8"; -A=-56"; A=56"; A+.5=56 1/2"; A/2=28"; B=154"; B/2=77"; C=73"; C/2=36 1/2"; DUAL_F=136"; DUAL_F+1"=137"; DUAL_G=135 1/8"; E=54 13/16"; GA=3/32"; LONG_RO=128 7/8"; LONG_RO/2=64 7/16"; MB_A=73"; MB_HT=53 11/16"; MB_HT+.25"=53 15/16"; MB_HT-2.75"=50 15/16"; MB_HT/2=26 27/32"; Model=QMXVP-1X2_Mixing Box_Sides; NOZZLE_BOTTOM_ID=42 1/2"; NOZZLE_BOTTOM_RAD=21 1/4"; NOZZLE_HEIGHT=78"; NOZZLE_HEIGHT/7*2=19 1/2"; NOZZLE_SIZE=360"; NOZZLE_TOP_OD=45 1/2"; NOZZLE_TOP_RAD=22 3/4"; NOZZLE_WB/4=14 13/16"; NOZZLE_WB_OD=74"; NOZZLE_WB_RAD=37"; NOZZLE_WB_RAD-2"=35"; RO=48 5/8"; RO/2=24 5/16"; RO2/2=24 5/16"; TRANSITION_TOP=74 3/4"; TYPE=0"; Type Comments=Vari-Plume Laboratory Exhaust Mixed-Flow Inline Belt Drive With 1X2 Mixing Box With Weather Hoods On Sides; UNIT_HEIGHT=58 1/2"; UNIT_HEIGHT*.75=43 7/8"; UNIT_OD=46 3/4"; UNIT_RAD+((A/2)+.25")=51 5/8"; UNIT_RAD+((A/2)+.25")+4"=55 5/8"; UNIT_RADIUS=23 3/8"; UNIT_RADIUS*.6=21 1/32"; UNIT_RADIUS+4"=27 3/8"
- 365_QMXVP-24L-1X2_Mixing_Box_Ends: (A/2)+.25"=31 1/4"; (A/2)+.5"=-31 1/2"; (A/2)-.5"=-30 1/2"; (A/2)-2"=29"; (NOZZLE_HEIGHT-(NOZZLE_HEIGHT/8*2))/2=23 1/4"; (NOZZLE_WB_OD-NOZZLE_TOP_OD)/2=6 1/8"; -A=-62"; A=62"; A+.5=62 1/2"; A/2=31"; B=175"; B/2=87 1/2"; C=79"; C/2=39 1/2"; DUAL_F=159"; DUAL_F+1"=160"; DUAL_G=158"; E=60 3/4"; GA=3/32"; LONG_RO=151 3/4"; LONG_RO/2=75 7/8"; MB_A=82"; MB_HT=59 11/16"; MB_HT+.25"=59 15/16"; MB_HT-2.75"=56 15/16"; MB_HT/2=29 27/32"; Model=QMXVP-1X2_Mixing Box_Sides; NOZZLE_BOTTOM_ID=34 3/4"; NOZZLE_BOTTOM_RAD=17 3/8"; NOZZLE_HEIGHT=62"; NOZZLE_HEIGHT/7*2=15 1/2"; NOZZLE_SIZE=288"; NOZZLE_TOP_OD=36 1/2"; NOZZLE_TOP_RAD=18 1/4"; NOZZLE_WB/4=12 3/16"; NOZZLE_WB_OD=61"; NOZZLE_WB_RAD=30 1/2"; NOZZLE_WB_RAD-2"=28 1/2"; RO=54 1/2"; RO/2=27 1/4"; RO2/2=27 1/4"; TRANSITION_TOP=104 1/4"; TYPE=0"; Type Comments=Vari-Plume Laboratory Exhaust Mixed-Flow Inline Belt Drive With 1X2 Mixing Box With Weather Hoods On Sides; UNIT_HEIGHT=64"; UNIT_HEIGHT*.75=48"; UNIT_OD=51 3/4"; UNIT_RAD+((A/2)+.25")=57 1/8"; UNIT_RAD+((A/2)+.25")+4"=61 1/8"; UNIT_RADIUS=25 7/8"; UNIT_RADIUS*.6=23 9/32"; UNIT_RADIUS+4"=29 7/8"
- 365_QMXVP-24H-1X2_Mixing_Box_Ends: (A/2)+.25"=31 1/4"; (A/2)+.5"=-31 1/2"; (A/2)-.5"=-30 1/2"; (A/2)-2"=29"; (NOZZLE_HEIGHT-(NOZZLE_HEIGHT/8*2))/2=23 1/4"; (NOZZLE_WB_OD-NOZZLE_TOP_OD)/2=6 1/8"; -A=-62"; A=62"; A+.5=62 1/2"; A/2=31"; B=175"; B/2=87 1/2"; C=79"; C/2=39 1/2"; DUAL_F=159"; DUAL_F+1"=160"; DUAL_G=158"; E=60 3/4"; GA=3/32"; LONG_RO=151 3/4"; LONG_RO/2=75 7/8"; MB_A=82"; MB_HT=59 11/16"; MB_HT+.25"=59 15/16"; MB_HT-2.75"=56 15/16"; MB_HT/2=29 27/32"; Model=QMXVP-1X2_Mixing Box_Sides; NOZZLE_BOTTOM_ID=34 3/4"; NOZZLE_BOTTOM_RAD=17 3/8"; NOZZLE_HEIGHT=62"; NOZZLE_HEIGHT/7*2=15 1/2"; NOZZLE_SIZE=288"; NOZZLE_TOP_OD=36 1/2"; NOZZLE_TOP_RAD=18 1/4"; NOZZLE_WB/4=12 3/16"; NOZZLE_WB_OD=61"; NOZZLE_WB_RAD=30 1/2"; NOZZLE_WB_RAD-2"=28 1/2"; RO=54 1/2"; RO/2=27 1/4"; RO2/2=27 1/4"; TRANSITION_TOP=104 1/4"; TYPE=0"; Type Comments=Vari-Plume Laboratory Exhaust Mixed-Flow Inline Belt Drive With 1X2 Mixing Box With Weather Hoods On Sides; UNIT_HEIGHT=64"; UNIT_HEIGHT*.75=48"; UNIT_OD=51 3/4"; UNIT_RAD+((A/2)+.25")=57 1/8"; UNIT_RAD+((A/2)+.25")+4"=61 1/8"; UNIT_RADIUS=25 7/8"; UNIT_RADIUS*.6=23 9/32"; UNIT_RADIUS+4"=29 7/8"
- 365_QMXVP-30L-1X2_Mixing_Box_Ends: (A/2)+.25"=31 1/4"; (A/2)+.5"=-31 1/2"; (A/2)-.5"=-30 1/2"; (A/2)-2"=29"; (NOZZLE_HEIGHT-(NOZZLE_HEIGHT/8*2))/2=29 1/4"; (NOZZLE_WB_OD-NOZZLE_TOP_OD)/2=7 1/8"; -A=-62"; A=62"; A+.5=62 1/2"; A/2=31"; B=175"; B/2=87 1/2"; C=79"; C/2=39 1/2"; DUAL_F=159"; DUAL_F+1"=160"; DUAL_G=158"; E=60 3/4"; GA=3/32"; LONG_RO=151 3/4"; LONG_RO/2=75 7/8"; MB_A=82"; MB_HT=59 11/16"; MB_HT+.25"=59 15/16"; MB_HT-2.75"=56 15/16"; MB_HT/2=29 27/32"; Model=QMXVP-1X2_Mixing Box_Sides; NOZZLE_BOTTOM_ID=42 1/2"; NOZZLE_BOTTOM_RAD=21 1/4"; NOZZLE_HEIGHT=78"; NOZZLE_HEIGHT/7*2=19 1/2"; NOZZLE_SIZE=360"; NOZZLE_TOP_OD=45 1/2"; NOZZLE_TOP_RAD=22 3/4"; NOZZLE_WB/4=14 13/16"; NOZZLE_WB_OD=74"; NOZZLE_WB_RAD=37"; NOZZLE_WB_RAD-2"=35"; RO=54 1/2"; RO/2=27 1/4"; RO2/2=27 1/4"; TRANSITION_TOP=89 1/2"; TYPE=0"; Type Comments=Vari-Plume Laboratory Exhaust Mixed-Flow Inline Belt Drive With 1X2 Mixing Box With Weather Hoods On Sides; UNIT_HEIGHT=64"; UNIT_HEIGHT*.75=48"; UNIT_OD=51 3/4"; UNIT_RAD+((A/2)+.25")=57 1/8"; UNIT_RAD+((A/2)+.25")+4"=61 1/8"; UNIT_RADIUS=25 7/8"; UNIT_RADIUS*.6=23 9/32"; UNIT_RADIUS+4"=29 7/8"
- 365_QMXVP-30H-1X2_Mixing_Box_Ends: (A/2)+.25"=31 1/4"; (A/2)+.5"=-31 1/2"; (A/2)-.5"=-30 1/2"; (A/2)-2"=29"; (NOZZLE_HEIGHT-(NOZZLE_HEIGHT/8*2))/2=29 1/4"; (NOZZLE_WB_OD-NOZZLE_TOP_OD)/2=7 1/8"; -A=-62"; A=62"; A+.5=62 1/2"; A/2=31"; B=175"; B/2=87 1/2"; C=79"; C/2=39 1/2"; DUAL_F=159"; DUAL_F+1"=160"; DUAL_G=158"; E=60 3/4"; GA=3/32"; LONG_RO=151 3/4"; LONG_RO/2=75 7/8"; MB_A=82"; MB_HT=59 11/16"; MB_HT+.25"=59 15/16"; MB_HT-2.75"=56 15/16"; MB_HT/2=29 27/32"; Model=QMXVP-1X2_Mixing Box_Sides; NOZZLE_BOTTOM_ID=42 1/2"; NOZZLE_BOTTOM_RAD=21 1/4"; NOZZLE_HEIGHT=78"; NOZZLE_HEIGHT/7*2=19 1/2"; NOZZLE_SIZE=360"; NOZZLE_TOP_OD=45 1/2"; NOZZLE_TOP_RAD=22 3/4"; NOZZLE_WB/4=14 13/16"; NOZZLE_WB_OD=74"; NOZZLE_WB_RAD=37"; NOZZLE_WB_RAD-2"=35"; RO=54 1/2"; RO/2=27 1/4"; RO2/2=27 1/4"; TRANSITION_TOP=89 1/2"; TYPE=0"; Type Comments=Vari-Plume Laboratory Exhaust Mixed-Flow Inline Belt Drive With 1X2 Mixing Box With Weather Hoods On Sides; UNIT_HEIGHT=64"; UNIT_HEIGHT*.75=48"; UNIT_OD=51 3/4"; UNIT_RAD+((A/2)+.25")=57 1/8"; UNIT_RAD+((A/2)+.25")+4"=61 1/8"; UNIT_RADIUS=25 7/8"; UNIT_RADIUS*.6=23 9/32"; UNIT_RADIUS+4"=29 7/8"
- 365_QMXVP-36L-1X2_Mixing_Box_Ends: (A/2)+.25"=31 1/4"; (A/2)+.5"=-31 1/2"; (A/2)-.5"=-30 1/2"; (A/2)-2"=29"; (NOZZLE_HEIGHT-(NOZZLE_HEIGHT/8*2))/2=35 5/8"; (NOZZLE_WB_OD-NOZZLE_TOP_OD)/2=8"; -A=-62"; A=62"; A+.5=62 1/2"; A/2=31"; B=175"; B/2=87 1/2"; C=79"; C/2=39 1/2"; DUAL_F=159"; DUAL_F+1"=160"; DUAL_G=158"; E=60 3/4"; GA=3/32"; LONG_RO=151 3/4"; LONG_RO/2=75 7/8"; MB_A=82"; MB_HT=59 11/16"; MB_HT+.25"=59 15/16"; MB_HT-2.75"=56 15/16"; MB_HT/2=29 27/32"; Model=QMXVP-1X2_Mixing Box_Sides; NOZZLE_BOTTOM_ID=51 3/4"; NOZZLE_BOTTOM_RAD=25 7/8"; NOZZLE_HEIGHT=95"; NOZZLE_HEIGHT/7*2=23 3/4"; NOZZLE_SIZE=432"; NOZZLE_TOP_OD=58"; NOZZLE_TOP_RAD=29"; NOZZLE_WB/4=18"; NOZZLE_WB_OD=90"; NOZZLE_WB_RAD=45"; NOZZLE_WB_RAD-2"=43"; RO=54 1/2"; RO/2=27 1/4"; RO2/2=27 1/4"; TRANSITION_TOP=78 1/4"; TYPE=0"; Type Comments=Vari-Plume Laboratory Exhaust Mixed-Flow Inline Belt Drive With 1X2 Mixing Box With Weather Hoods On Sides; UNIT_HEIGHT=64"; UNIT_HEIGHT*.75=48"; UNIT_OD=51 3/4"; UNIT_RAD+((A/2)+.25")=57 1/8"; UNIT_RAD+((A/2)+.25")+4"=61 1/8"; UNIT_RADIUS=25 7/8"; UNIT_RADIUS*.6=23 9/32"; UNIT_RADIUS+4"=29 7/8"
- 402_QMXVP-24L-1X2_Mixing_Box_Ends: (A/2)+.25"=33 3/4"; (A/2)+.5"=-34"; (A/2)-.5"=-33"; (A/2)-2"=31 1/2"; (NOZZLE_HEIGHT-(NOZZLE_HEIGHT/8*2))/2=23 1/4"; (NOZZLE_WB_OD-NOZZLE_TOP_OD)/2=6 1/8"; -A=-67"; A=67"; A+.5=67 1/2"; A/2=33 1/2"; B=183"; B/2=91 1/2"; C=88"; C/2=44"; DUAL_F=164"; DUAL_F+1"=165"; DUAL_G=163"; E=65 3/4"; GA=3/32"; LONG_RO=156 3/4"; LONG_RO/2=78 3/8"; MB_A=90"; MB_HT=65 15/16"; MB_HT+.25"=66 3/16"; MB_HT-2.75"=63 3/16"; MB_HT/2=32 31/32"; Model=QMXVP-1X2_Mixing Box_Sides; NOZZLE_BOTTOM_ID=34 3/4"; NOZZLE_BOTTOM_RAD=17 3/8"; NOZZLE_HEIGHT=62"; NOZZLE_HEIGHT/7*2=15 1/2"; NOZZLE_SIZE=288"; NOZZLE_TOP_OD=36 1/2"; NOZZLE_TOP_RAD=18 1/4"; NOZZLE_WB/4=12 3/16"; NOZZLE_WB_OD=61"; NOZZLE_WB_RAD=30 1/2"; NOZZLE_WB_RAD-2"=28 1/2"; RO=59 7/16"; RO/2=29 23/32"; RO2/2=29 23/32"; TRANSITION_TOP=118 3/4"; TYPE=0"; Type Comments=Vari-Plume Laboratory Exhaust Mixed-Flow Inline Belt Drive With 1X2 Mixing Box With Weather Hoods On Sides; UNIT_HEIGHT=68 1/2"; UNIT_HEIGHT*.75=51 3/8"; UNIT_OD=56 15/16"; UNIT_RAD+((A/2)+.25")=62 7/32"; UNIT_RAD+((A/2)+.25")+4"=66 7/32"; UNIT_RADIUS=28 15/32"; UNIT_RADIUS*.6=25 5/8"; UNIT_RADIUS+4"=32 15/32"
- 402_QMXVP-24H-1X2_Mixing_Box_Ends: (A/2)+.25"=33 3/4"; (A/2)+.5"=-34"; (A/2)-.5"=-33"; (A/2)-2"=31 1/2"; (NOZZLE_HEIGHT-(NOZZLE_HEIGHT/8*2))/2=23 1/4"; (NOZZLE_WB_OD-NOZZLE_TOP_OD)/2=6 1/8"; -A=-67"; A=67"; A+.5=67 1/2"; A/2=33 1/2"; B=183"; B/2=91 1/2"; C=88"; C/2=44"; DUAL_F=164"; DUAL_F+1"=165"; DUAL_G=163"; E=65 3/4"; GA=3/32"; LONG_RO=156 3/4"; LONG_RO/2=78 3/8"; MB_A=90"; MB_HT=65 15/16"; MB_HT+.25"=66 3/16"; MB_HT-2.75"=63 3/16"; MB_HT/2=32 31/32"; Model=QMXVP-1X2_Mixing Box_Sides; NOZZLE_BOTTOM_ID=34 3/4"; NOZZLE_BOTTOM_RAD=17 3/8"; NOZZLE_HEIGHT=62"; NOZZLE_HEIGHT/7*2=15 1/2"; NOZZLE_SIZE=288"; NOZZLE_TOP_OD=36 1/2"; NOZZLE_TOP_RAD=18 1/4"; NOZZLE_WB/4=12 3/16"; NOZZLE_WB_OD=61"; NOZZLE_WB_RAD=30 1/2"; NOZZLE_WB_RAD-2"=28 1/2"; RO=59 7/16"; RO/2=29 23/32"; RO2/2=29 23/32"; TRANSITION_TOP=118 3/4"; TYPE=0"; Type Comments=Vari-Plume Laboratory Exhaust Mixed-Flow Inline Belt Drive With 1X2 Mixing Box With Weather Hoods On Sides; UNIT_HEIGHT=68 1/2"; UNIT_HEIGHT*.75=51 3/8"; UNIT_OD=56 15/16"; UNIT_RAD+((A/2)+.25")=62 7/32"; UNIT_RAD+((A/2)+.25")+4"=66 7/32"; UNIT_RADIUS=28 15/32"; UNIT_RADIUS*.6=25 5/8"; UNIT_RADIUS+4"=32 15/32"
- 402_QMXVP-30L-1X2_Mixing_Box_Ends: (A/2)+.25"=33 3/4"; (A/2)+.5"=-34"; (A/2)-.5"=-33"; (A/2)-2"=31 1/2"; (NOZZLE_HEIGHT-(NOZZLE_HEIGHT/8*2))/2=29 1/4"; (NOZZLE_WB_OD-NOZZLE_TOP_OD)/2=7 1/8"; -A=-67"; A=67"; A+.5=67 1/2"; A/2=33 1/2"; B=183"; B/2=91 1/2"; C=88"; C/2=44"; DUAL_F=164"; DUAL_F+1"=165"; DUAL_G=163"; E=65 3/4"; GA=3/32"; LONG_RO=156 3/4"; LONG_RO/2=78 3/8"; MB_A=90"; MB_HT=65 15/16"; MB_HT+.25"=66 3/16"; MB_HT-2.75"=63 3/16"; MB_HT/2=32 31/32"; Model=QMXVP-1X2_Mixing Box_Sides; NOZZLE_BOTTOM_ID=42 1/2"; NOZZLE_BOTTOM_RAD=21 1/4"; NOZZLE_HEIGHT=78"; NOZZLE_HEIGHT/7*2=19 1/2"; NOZZLE_SIZE=360"; NOZZLE_TOP_OD=45 1/2"; NOZZLE_TOP_RAD=22 3/4"; NOZZLE_WB/4=14 13/16"; NOZZLE_WB_OD=74"; NOZZLE_WB_RAD=37"; NOZZLE_WB_RAD-2"=35"; RO=59 7/16"; RO/2=29 23/32"; RO2/2=29 23/32"; TRANSITION_TOP=103 3/4"; TYPE=0"; Type Comments=Vari-Plume Laboratory Exhaust Mixed-Flow Inline Belt Drive With 1X2 Mixing Box With Weather Hoods On Sides; UNIT_HEIGHT=68 1/2"; UNIT_HEIGHT*.75=51 3/8"; UNIT_OD=56 15/16"; UNIT_RAD+((A/2)+.25")=62 7/32"; UNIT_RAD+((A/2)+.25")+4"=66 7/32"; UNIT_RADIUS=28 15/32"; UNIT_RADIUS*.6=25 5/8"; UNIT_RADIUS+4"=32 15/32"
- 402_QMXVP-30H-1X2_Mixing_Box_Ends: (A/2)+.25"=33 3/4"; (A/2)+.5"=-34"; (A/2)-.5"=-33"; (A/2)-2"=31 1/2"; (NOZZLE_HEIGHT-(NOZZLE_HEIGHT/8*2))/2=29 1/4"; (NOZZLE_WB_OD-NOZZLE_TOP_OD)/2=7 1/8"; -A=-67"; A=67"; A+.5=67 1/2"; A/2=33 1/2"; B=183"; B/2=91 1/2"; C=88"; C/2=44"; DUAL_F=164"; DUAL_F+1"=165"; DUAL_G=163"; E=65 3/4"; GA=3/32"; LONG_RO=156 3/4"; LONG_RO/2=78 3/8"; MB_A=90"; MB_HT=65 15/16"; MB_HT+.25"=66 3/16"; MB_HT-2.75"=63 3/16"; MB_HT/2=32 31/32"; Model=QMXVP-1X2_Mixing Box_Sides; NOZZLE_BOTTOM_ID=42 1/2"; NOZZLE_BOTTOM_RAD=21 1/4"; NOZZLE_HEIGHT=78"; NOZZLE_HEIGHT/7*2=19 1/2"; NOZZLE_SIZE=360"; NOZZLE_TOP_OD=45 1/2"; NOZZLE_TOP_RAD=22 3/4"; NOZZLE_WB/4=14 13/16"; NOZZLE_WB_OD=74"; NOZZLE_WB_RAD=37"; NOZZLE_WB_RAD-2"=35"; RO=59 7/16"; RO/2=29 23/32"; RO2/2=29 23/32"; TRANSITION_TOP=103 3/4"; TYPE=0"; Type Comments=Vari-Plume Laboratory Exhaust Mixed-Flow Inline Belt Drive With 1X2 Mixing Box With Weather Hoods On Sides; UNIT_HEIGHT=68 1/2"; UNIT_HEIGHT*.75=51 3/8"; UNIT_OD=56 15/16"; UNIT_RAD+((A/2)+.25")=62 7/32"; UNIT_RAD+((A/2)+.25")+4"=66 7/32"; UNIT_RADIUS=28 15/32"; UNIT_RADIUS*.6=25 5/8"; UNIT_RADIUS+4"=32 15/32"
- 402_QMXVP-36L-1X2_Mixing_Box_Ends: (A/2)+.25"=33 3/4"; (A/2)+.5"=-34"; (A/2)-.5"=-33"; (A/2)-2"=31 1/2"; (NOZZLE_HEIGHT-(NOZZLE_HEIGHT/8*2))/2=35 5/8"; (NOZZLE_WB_OD-NOZZLE_TOP_OD)/2=8"; -A=-67"; A=67"; A+.5=67 1/2"; A/2=33 1/2"; B=183"; B/2=91 1/2"; C=88"; C/2=44"; DUAL_F=164"; DUAL_F+1"=165"; DUAL_G=163"; E=65 3/4"; GA=3/32"; LONG_RO=156 3/4"; LONG_RO/2=78 3/8"; MB_A=90"; MB_HT=65 15/16"; MB_HT+.25"=66 3/16"; MB_HT-2.75"=63 3/16"; MB_HT/2=32 31/32"; Model=QMXVP-1X2_Mixing Box_Sides; NOZZLE_BOTTOM_ID=51 3/4"; NOZZLE_BOTTOM_RAD=25 7/8"; NOZZLE_HEIGHT=95"; NOZZLE_HEIGHT/7*2=23 3/4"; NOZZLE_SIZE=432"; NOZZLE_TOP_OD=58"; NOZZLE_TOP_RAD=29"; NOZZLE_WB/4=18"; NOZZLE_WB_OD=90"; NOZZLE_WB_RAD=45"; NOZZLE_WB_RAD-2"=43"; RO=59 7/16"; RO/2=29 23/32"; RO2/2=29 23/32"; TRANSITION_TOP=86 3/4"; TYPE=0"; Type Comments=Vari-Plume Laboratory Exhaust Mixed-Flow Inline Belt Drive With 1X2 Mixing Box With Weather Hoods On Sides; UNIT_HEIGHT=68 1/2"; UNIT_HEIGHT*.75=51 3/8"; UNIT_OD=56 15/16"; UNIT_RAD+((A/2)+.25")=62 7/32"; UNIT_RAD+((A/2)+.25")+4"=66 7/32"; UNIT_RADIUS=28 15/32"; UNIT_RADIUS*.6=25 5/8"; UNIT_RADIUS+4"=32 15/32"
- 402_QMXVP-36H-1X2_Mixing_Box_Ends: (A/2)+.25"=33 3/4"; (A/2)+.5"=-34"; (A/2)-.5"=-33"; (A/2)-2"=31 1/2"; (NOZZLE_HEIGHT-(NOZZLE_HEIGHT/8*2))/2=35 5/8"; (NOZZLE_WB_OD-NOZZLE_TOP_OD)/2=8"; -A=-67"; A=67"; A+.5=67 1/2"; A/2=33 1/2"; B=183"; B/2=91 1/2"; C=88"; C/2=44"; DUAL_F=164"; DUAL_F+1"=165"; DUAL_G=163"; E=65 3/4"; GA=3/32"; LONG_RO=156 3/4"; LONG_RO/2=78 3/8"; MB_A=90"; MB_HT=65 15/16"; MB_HT+.25"=66 3/16"; MB_HT-2.75"=63 3/16"; MB_HT/2=32 31/32"; Model=QMXVP-1X2_Mixing Box_Sides; NOZZLE_BOTTOM_ID=51 3/4"; NOZZLE_BOTTOM_RAD=25 7/8"; NOZZLE_HEIGHT=95"; NOZZLE_HEIGHT/7*2=23 3/4"; NOZZLE_SIZE=432"; NOZZLE_TOP_OD=58"; NOZZLE_TOP_RAD=29"; NOZZLE_WB/4=18"; NOZZLE_WB_OD=90"; NOZZLE_WB_RAD=45"; NOZZLE_WB_RAD-2"=43"; RO=59 7/16"; RO/2=29 23/32"; RO2/2=29 23/32"; TRANSITION_TOP=86 3/4"; TYPE=0"; Type Comments=Vari-Plume Laboratory Exhaust Mixed-Flow Inline Belt Drive With 1X2 Mixing Box With Weather Hoods On Sides; UNIT_HEIGHT=68 1/2"; UNIT_HEIGHT*.75=51 3/8"; UNIT_OD=56 15/16"; UNIT_RAD+((A/2)+.25")=62 7/32"; UNIT_RAD+((A/2)+.25")+4"=66 7/32"; UNIT_RADIUS=28 15/32"; UNIT_RADIUS*.6=25 5/8"; UNIT_RADIUS+4"=32 15/32"
- 445_QMXVP-30L-1X2_Mixing_Box_Ends: (A/2)+.25"=37 1/4"; (A/2)+.5"=-37 1/2"; (A/2)-.5"=-36 1/2"; (A/2)-2"=35"; (NOZZLE_HEIGHT-(NOZZLE_HEIGHT/8*2))/2=29 1/4"; (NOZZLE_WB_OD-NOZZLE_TOP_OD)/2=7 1/8"; -A=-74"; A=74"; A+.5=74 1/2"; A/2=37"; B=201"; B/2=100 1/2"; C=95"; C/2=47 1/2"; DUAL_F=171"; DUAL_F+1"=172"; DUAL_G=170"; E=72 5/8"; GA=3/32"; LONG_RO=163 3/4"; LONG_RO/2=81 7/8"; MB_A=102"; MB_HT=75 11/16"; MB_HT+.25"=75 15/16"; MB_HT-2.75"=72 15/16"; MB_HT/2=37 27/32"; Model=QMXVP-1X2_Mixing Box_Sides; NOZZLE_BOTTOM_ID=42 1/2"; NOZZLE_BOTTOM_RAD=21 1/4"; NOZZLE_HEIGHT=78"; NOZZLE_HEIGHT/7*2=19 1/2"; NOZZLE_SIZE=360"; NOZZLE_TOP_OD=45 1/2"; NOZZLE_TOP_RAD=22 3/4"; NOZZLE_WB/4=14 13/16"; NOZZLE_WB_OD=74"; NOZZLE_WB_RAD=37"; NOZZLE_WB_RAD-2"=35"; RO=66 7/16"; RO/2=33 7/32"; RO2/2=33 7/32"; TRANSITION_TOP=121 1/4"; TYPE=0"; Type Comments=Vari-Plume Laboratory Exhaust Mixed-Flow Inline Belt Drive With 1X2 Mixing Box With Weather Hoods On Sides; UNIT_HEIGHT=74"; UNIT_HEIGHT*.75=55 1/2"; UNIT_OD=63 1/16"; UNIT_RAD+((A/2)+.25")=68 25/32"; UNIT_RAD+((A/2)+.25")+4"=72 25/32"; UNIT_RADIUS=31 17/32"; UNIT_RADIUS*.6=28 3/8"; UNIT_RADIUS+4"=35 17/32"
- 445_QMXVP-30H-1X2_Mixing_Box_Ends: (A/2)+.25"=37 1/4"; (A/2)+.5"=-37 1/2"; (A/2)-.5"=-36 1/2"; (A/2)-2"=35"; (NOZZLE_HEIGHT-(NOZZLE_HEIGHT/8*2))/2=29 1/4"; (NOZZLE_WB_OD-NOZZLE_TOP_OD)/2=7 1/8"; -A=-74"; A=74"; A+.5=74 1/2"; A/2=37"; B=201"; B/2=100 1/2"; C=95"; C/2=47 1/2"; DUAL_F=171"; DUAL_F+1"=172"; DUAL_G=170"; E=72 5/8"; GA=3/32"; LONG_RO=163 3/4"; LONG_RO/2=81 7/8"; MB_A=102"; MB_HT=75 11/16"; MB_HT+.25"=75 15/16"; MB_HT-2.75"=72 15/16"; MB_HT/2=37 27/32"; Model=QMXVP-1X2_Mixing Box_Sides; NOZZLE_BOTTOM_ID=42 1/2"; NOZZLE_BOTTOM_RAD=21 1/4"; NOZZLE_HEIGHT=78"; NOZZLE_HEIGHT/7*2=19 1/2"; NOZZLE_SIZE=360"; NOZZLE_TOP_OD=45 1/2"; NOZZLE_TOP_RAD=22 3/4"; NOZZLE_WB/4=14 13/16"; NOZZLE_WB_OD=74"; NOZZLE_WB_RAD=37"; NOZZLE_WB_RAD-2"=35"; RO=66 7/16"; RO/2=33 7/32"; RO2/2=33 7/32"; TRANSITION_TOP=121 1/4"; TYPE=0"; Type Comments=Vari-Plume Laboratory Exhaust Mixed-Flow Inline Belt Drive With 1X2 Mixing Box With Weather Hoods On Sides; UNIT_HEIGHT=74"; UNIT_HEIGHT*.75=55 1/2"; UNIT_OD=63 1/16"; UNIT_RAD+((A/2)+.25")=68 25/32"; UNIT_RAD+((A/2)+.25")+4"=72 25/32"; UNIT_RADIUS=31 17/32"; UNIT_RADIUS*.6=28 3/8"; UNIT_RADIUS+4"=35 17/32"
- 445_QMXVP-36L-1X2_Mixing_Box_Ends: (A/2)+.25"=37 1/4"; (A/2)+.5"=-37 1/2"; (A/2)-.5"=-36 1/2"; (A/2)-2"=35"; (NOZZLE_HEIGHT-(NOZZLE_HEIGHT/8*2))/2=35 5/8"; (NOZZLE_WB_OD-NOZZLE_TOP_OD)/2=8"; -A=-74"; A=74"; A+.5=74 1/2"; A/2=37"; B=201"; B/2=100 1/2"; C=95"; C/2=47 1/2"; DUAL_F=171"; DUAL_F+1"=172"; DUAL_G=170"; E=72 5/8"; GA=3/32"; LONG_RO=163 3/4"; LONG_RO/2=81 7/8"; MB_A=102"; MB_HT=75 11/16"; MB_HT+.25"=75 15/16"; MB_HT-2.75"=72 15/16"; MB_HT/2=37 27/32"; Model=QMXVP-1X2_Mixing Box_Sides; NOZZLE_BOTTOM_ID=51 3/4"; NOZZLE_BOTTOM_RAD=25 7/8"; NOZZLE_HEIGHT=95"; NOZZLE_HEIGHT/7*2=23 3/4"; NOZZLE_SIZE=432"; NOZZLE_TOP_OD=58"; NOZZLE_TOP_RAD=29"; NOZZLE_WB/4=18"; NOZZLE_WB_OD=90"; NOZZLE_WB_RAD=45"; NOZZLE_WB_RAD-2"=43"; RO=66 7/16"; RO/2=33 7/32"; RO2/2=33 7/32"; TRANSITION_TOP=103 1/4"; TYPE=0"; Type Comments=Vari-Plume Laboratory Exhaust Mixed-Flow Inline Belt Drive With 1X2 Mixing Box With Weather Hoods On Sides; UNIT_HEIGHT=74"; UNIT_HEIGHT*.75=55 1/2"; UNIT_OD=63 1/16"; UNIT_RAD+((A/2)+.25")=68 25/32"; UNIT_RAD+((A/2)+.25")+4"=72 25/32"; UNIT_RADIUS=31 17/32"; UNIT_RADIUS*.6=28 3/8"; UNIT_RADIUS+4"=35 17/32"
- 445_QMXVP-36H-1X2_Mixing_Box_Ends: (A/2)+.25"=37 1/4"; (A/2)+.5"=-37 1/2"; (A/2)-.5"=-36 1/2"; (A/2)-2"=35"; (NOZZLE_HEIGHT-(NOZZLE_HEIGHT/8*2))/2=35 5/8"; (NOZZLE_WB_OD-NOZZLE_TOP_OD)/2=8"; -A=-74"; A=74"; A+.5=74 1/2"; A/2=37"; B=201"; B/2=100 1/2"; C=95"; C/2=47 1/2"; DUAL_F=171"; DUAL_F+1"=172"; DUAL_G=170"; E=72 5/8"; GA=3/32"; LONG_RO=163 3/4"; LONG_RO/2=81 7/8"; MB_A=102"; MB_HT=75 11/16"; MB_HT+.25"=75 15/16"; MB_HT-2.75"=72 15/16"; MB_HT/2=37 27/32"; Model=QMXVP-1X2_Mixing Box_Sides; NOZZLE_BOTTOM_ID=51 3/4"; NOZZLE_BOTTOM_RAD=25 7/8"; NOZZLE_HEIGHT=95"; NOZZLE_HEIGHT/7*2=23 3/4"; NOZZLE_SIZE=432"; NOZZLE_TOP_OD=58"; NOZZLE_TOP_RAD=29"; NOZZLE_WB/4=18"; NOZZLE_WB_OD=90"; NOZZLE_WB_RAD=45"; NOZZLE_WB_RAD-2"=43"; RO=66 7/16"; RO/2=33 7/32"; RO2/2=33 7/32"; TRANSITION_TOP=103 1/4"; TYPE=0"; Type Comments=Vari-Plume Laboratory Exhaust Mixed-Flow Inline Belt Drive With 1X2 Mixing Box With Weather Hoods On Sides; UNIT_HEIGHT=74"; UNIT_HEIGHT*.75=55 1/2"; UNIT_OD=63 1/16"; UNIT_RAD+((A/2)+.25")=68 25/32"; UNIT_RAD+((A/2)+.25")+4"=72 25/32"; UNIT_RADIUS=31 17/32"; UNIT_RADIUS*.6=28 3/8"; UNIT_RADIUS+4"=35 17/32"
- 490_QMXVP-30L-1X2_Mixing_Box_Ends: (A/2)+.25"=40 1/4"; (A/2)+.5"=-40 1/2"; (A/2)-.5"=-39 1/2"; (A/2)-2"=38"; (NOZZLE_HEIGHT-(NOZZLE_HEIGHT/8*2))/2=29 1/4"; (NOZZLE_WB_OD-NOZZLE_TOP_OD)/2=7 1/8"; -A=-80"; A=80"; A+.5=80 1/2"; A/2=40"; B=219"; B/2=109 1/2"; C=103"; C/2=51 1/2"; DUAL_F=192"; DUAL_F+1"=193"; DUAL_G=191"; E=78 1/2"; GA=1/8"; LONG_RO=184 3/4"; LONG_RO/2=92 3/8"; MB_A=113"; MB_HT=86 15/16"; MB_HT+.25"=87 3/16"; MB_HT-2.75"=84 3/16"; MB_HT/2=43 15/32"; Model=QMXVP-1X2_Mixing Box_Sides; NOZZLE_BOTTOM_ID=42 1/2"; NOZZLE_BOTTOM_RAD=21 1/4"; NOZZLE_HEIGHT=78"; NOZZLE_HEIGHT/7*2=19 1/2"; NOZZLE_SIZE=360"; NOZZLE_TOP_OD=45 1/2"; NOZZLE_TOP_RAD=22 3/4"; NOZZLE_WB/4=14 13/16"; NOZZLE_WB_OD=74"; NOZZLE_WB_RAD=37"; NOZZLE_WB_RAD-2"=35"; RO=72 1/4"; RO/2=36 1/8"; RO2/2=36 1/8"; TRANSITION_TOP=139 3/4"; TYPE=0"; Type Comments=Vari-Plume Laboratory Exhaust Mixed-Flow Inline Belt Drive With 1X2 Mixing Box With Weather Hoods On Sides; UNIT_HEIGHT=80 1/2"; UNIT_HEIGHT*.75=60 3/8"; UNIT_OD=69 3/8"; UNIT_RAD+((A/2)+.25")=74 15/16"; UNIT_RAD+((A/2)+.25")+4"=78 15/16"; UNIT_RADIUS=34 11/16"; UNIT_RADIUS*.6=31 7/32"; UNIT_RADIUS+4"=38 11/16"
- 490_QMXVP-30H-1X2_Mixing_Box_Ends: (A/2)+.25"=40 1/4"; (A/2)+.5"=-40 1/2"; (A/2)-.5"=-39 1/2"; (A/2)-2"=38"; (NOZZLE_HEIGHT-(NOZZLE_HEIGHT/8*2))/2=29 1/4"; (NOZZLE_WB_OD-NOZZLE_TOP_OD)/2=7 1/8"; -A=-80"; A=80"; A+.5=80 1/2"; A/2=40"; B=219"; B/2=109 1/2"; C=103"; C/2=51 1/2"; DUAL_F=192"; DUAL_F+1"=193"; DUAL_G=191"; E=78 1/2"; GA=1/8"; LONG_RO=184 3/4"; LONG_RO/2=92 3/8"; MB_A=113"; MB_HT=86 15/16"; MB_HT+.25"=87 3/16"; MB_HT-2.75"=84 3/16"; MB_HT/2=43 15/32"; Model=QMXVP-1X2_Mixing Box_Sides; NOZZLE_BOTTOM_ID=42 1/2"; NOZZLE_BOTTOM_RAD=21 1/4"; NOZZLE_HEIGHT=78"; NOZZLE_HEIGHT/7*2=19 1/2"; NOZZLE_SIZE=360"; NOZZLE_TOP_OD=45 1/2"; NOZZLE_TOP_RAD=22 3/4"; NOZZLE_WB/4=14 13/16"; NOZZLE_WB_OD=74"; NOZZLE_WB_RAD=37"; NOZZLE_WB_RAD-2"=35"; RO=72 1/4"; RO/2=36 1/8"; RO2/2=36 1/8"; TRANSITION_TOP=139 3/4"; TYPE=0"; Type Comments=Vari-Plume Laboratory Exhaust Mixed-Flow Inline Belt Drive With 1X2 Mixing Box With Weather Hoods On Sides; UNIT_HEIGHT=80 1/2"; UNIT_HEIGHT*.75=60 3/8"; UNIT_OD=69 3/8"; UNIT_RAD+((A/2)+.25")=74 15/16"; UNIT_RAD+((A/2)+.25")+4"=78 15/16"; UNIT_RADIUS=34 11/16"; UNIT_RADIUS*.6=31 7/32"; UNIT_RADIUS+4"=38 11/16"
- 490_QMXVP-36L-1X2_Mixing_Box_Ends: (A/2)+.25"=40 1/4"; (A/2)+.5"=-40 1/2"; (A/2)-.5"=-39 1/2"; (A/2)-2"=38"; (NOZZLE_HEIGHT-(NOZZLE_HEIGHT/8*2))/2=35 5/8"; (NOZZLE_WB_OD-NOZZLE_TOP_OD)/2=8"; -A=-80"; A=80"; A+.5=80 1/2"; A/2=40"; B=219"; B/2=109 1/2"; C=103"; C/2=51 1/2"; DUAL_F=192"; DUAL_F+1"=193"; DUAL_G=191"; E=78 1/2"; GA=1/8"; LONG_RO=184 3/4"; LONG_RO/2=92 3/8"; MB_A=113"; MB_HT=86 15/16"; MB_HT+.25"=87 3/16"; MB_HT-2.75"=84 3/16"; MB_HT/2=43 15/32"; Model=QMXVP-1X2_Mixing Box_Sides; NOZZLE_BOTTOM_ID=51 3/4"; NOZZLE_BOTTOM_RAD=25 7/8"; NOZZLE_HEIGHT=95"; NOZZLE_HEIGHT/7*2=23 3/4"; NOZZLE_SIZE=432"; NOZZLE_TOP_OD=58"; NOZZLE_TOP_RAD=29"; NOZZLE_WB/4=18"; NOZZLE_WB_OD=90"; NOZZLE_WB_RAD=45"; NOZZLE_WB_RAD-2"=43"; RO=72 1/4"; RO/2=36 1/8"; RO2/2=36 1/8"; TRANSITION_TOP=122 3/4"; TYPE=0"; Type Comments=Vari-Plume Laboratory Exhaust Mixed-Flow Inline Belt Drive With 1X2 Mixing Box With Weather Hoods On Sides; UNIT_HEIGHT=80 1/2"; UNIT_HEIGHT*.75=60 3/8"; UNIT_OD=69 3/8"; UNIT_RAD+((A/2)+.25")=74 15/16"; UNIT_RAD+((A/2)+.25")+4"=78 15/16"; UNIT_RADIUS=34 11/16"; UNIT_RADIUS*.6=31 7/32"; UNIT_RADIUS+4"=38 11/16"
- 490_QMXVP-36H-1X2_Mixing_Box_Ends: (A/2)+.25"=40 1/4"; (A/2)+.5"=-40 1/2"; (A/2)-.5"=-39 1/2"; (A/2)-2"=38"; (NOZZLE_HEIGHT-(NOZZLE_HEIGHT/8*2))/2=35 5/8"; (NOZZLE_WB_OD-NOZZLE_TOP_OD)/2=8"; -A=-80"; A=80"; A+.5=80 1/2"; A/2=40"; B=219"; B/2=109 1/2"; C=103"; C/2=51 1/2"; DUAL_F=192"; DUAL_F+1"=193"; DUAL_G=191"; E=78 1/2"; GA=1/8"; LONG_RO=184 3/4"; LONG_RO/2=92 3/8"; MB_A=113"; MB_HT=86 15/16"; MB_HT+.25"=87 3/16"; MB_HT-2.75"=84 3/16"; MB_HT/2=43 15/32"; Model=QMXVP-1X2_Mixing Box_Sides; NOZZLE_BOTTOM_ID=51 3/4"; NOZZLE_BOTTOM_RAD=25 7/8"; NOZZLE_HEIGHT=95"; NOZZLE_HEIGHT/7*2=23 3/4"; NOZZLE_SIZE=432"; NOZZLE_TOP_OD=58"; NOZZLE_TOP_RAD=29"; NOZZLE_WB/4=18"; NOZZLE_WB_OD=90"; NOZZLE_WB_RAD=45"; NOZZLE_WB_RAD-2"=43"; RO=72 1/4"; RO/2=36 1/8"; RO2/2=36 1/8"; TRANSITION_TOP=122 3/4"; TYPE=0"; Type Comments=Vari-Plume Laboratory Exhaust Mixed-Flow Inline Belt Drive With 1X2 Mixing Box With Weather Hoods On Sides; UNIT_HEIGHT=80 1/2"; UNIT_HEIGHT*.75=60 3/8"; UNIT_OD=69 3/8"; UNIT_RAD+((A/2)+.25")=74 15/16"; UNIT_RAD+((A/2)+.25")+4"=78 15/16"; UNIT_RADIUS=34 11/16"; UNIT_RADIUS*.6=31 7/32"; UNIT_RADIUS+4"=38 11/16"
- 540_QMXVP-36L-1X2_Mixing_Box_Ends: (A/2)+.25"=45 1/4"; (A/2)+.5"=-45 1/2"; (A/2)-.5"=-44 1/2"; (A/2)-2"=43"; (NOZZLE_HEIGHT-(NOZZLE_HEIGHT/8*2))/2=35 5/8"; (NOZZLE_WB_OD-NOZZLE_TOP_OD)/2=8"; -A=-90"; A=90"; A+.5=90 1/2"; A/2=45"; B=239"; B/2=119 1/2"; C=111"; C/2=55 1/2"; DUAL_F=202"; DUAL_F+1"=203"; DUAL_G=200 7/8"; E=85 3/8"; GA=1/8"; LONG_RO=194 5/8"; LONG_RO/2=97 5/16"; MB_A=126"; MB_HT=99 11/16"; MB_HT+.25"=99 15/16"; MB_HT-2.75"=96 15/16"; MB_HT/2=49 27/32"; Model=QMXVP-1X2_Mixing Box_Sides; NOZZLE_BOTTOM_ID=51 3/4"; NOZZLE_BOTTOM_RAD=25 7/8"; NOZZLE_HEIGHT=95"; NOZZLE_HEIGHT/7*2=23 3/4"; NOZZLE_SIZE=432"; NOZZLE_TOP_OD=58"; NOZZLE_TOP_RAD=29"; NOZZLE_WB/4=18"; NOZZLE_WB_OD=90"; NOZZLE_WB_RAD=45"; NOZZLE_WB_RAD-2"=43"; RO=79 1/8"; RO/2=39 9/16"; RO2/2=41"; TRANSITION_TOP=142 1/4"; TYPE=0"; Type Comments=Vari-Plume Laboratory Exhaust Mixed-Flow Inline Belt Drive With 1X2 Mixing Box With Weather Hoods On Sides; UNIT_HEIGHT=87"; UNIT_HEIGHT*.75=65 1/4"; UNIT_OD=76 7/16"; UNIT_RAD+((A/2)+.25")=83 15/32"; UNIT_RAD+((A/2)+.25")+4"=87 15/32"; UNIT_RADIUS=38 7/32"; UNIT_RADIUS*.6=34 13/32"; UNIT_RADIUS+4"=42 7/32"
- 540_QMXVP-36H-1X2_Mixing_Box_Ends: (A/2)+.25"=45 1/4"; (A/2)+.5"=-45 1/2"; (A/2)-.5"=-44 1/2"; (A/2)-2"=43"; (NOZZLE_HEIGHT-(NOZZLE_HEIGHT/8*2))/2=35 5/8"; (NOZZLE_WB_OD-NOZZLE_TOP_OD)/2=8"; -A=-90"; A=90"; A+.5=90 1/2"; A/2=45"; B=239"; B/2=119 1/2"; C=111"; C/2=55 1/2"; DUAL_F=202"; DUAL_F+1"=203"; DUAL_G=200 7/8"; E=85 3/8"; GA=1/8"; LONG_RO=194 5/8"; LONG_RO/2=97 5/16"; MB_A=126"; MB_HT=99 11/16"; MB_HT+.25"=99 15/16"; MB_HT-2.75"=96 15/16"; MB_HT/2=49 27/32"; Model=QMXVP-1X2_Mixing Box_Sides; NOZZLE_BOTTOM_ID=51 3/4"; NOZZLE_BOTTOM_RAD=25 7/8"; NOZZLE_HEIGHT=95"; NOZZLE_HEIGHT/7*2=23 3/4"; NOZZLE_SIZE=432"; NOZZLE_TOP_OD=58"; NOZZLE_TOP_RAD=29"; NOZZLE_WB/4=18"; NOZZLE_WB_OD=90"; NOZZLE_WB_RAD=45"; NOZZLE_WB_RAD-2"=43"; RO=79 1/8"; RO/2=39 9/16"; RO2/2=41"; TRANSITION_TOP=142 1/4"; TYPE=0"; Type Comments=Vari-Plume Laboratory Exhaust Mixed-Flow Inline Belt Drive With 1X2 Mixing Box With Weather Hoods On Sides; UNIT_HEIGHT=87"; UNIT_HEIGHT*.75=65 1/4"; UNIT_OD=76 7/16"; UNIT_RAD+((A/2)+.25")=83 15/32"; UNIT_RAD+((A/2)+.25")+4"=87 15/32"; UNIT_RADIUS=38 7/32"; UNIT_RADIUS*.6=34 13/32"; UNIT_RADIUS+4"=42 7/32"
- 540_QMXVP-49L-1X2_Mixing_Box_Ends: (A/2)+.25"=45 1/4"; (A/2)+.5"=-45 1/2"; (A/2)-.5"=-44 1/2"; (A/2)-2"=43"; (NOZZLE_HEIGHT-(NOZZLE_HEIGHT/8*2))/2=41 1/4"; (NOZZLE_WB_OD-NOZZLE_TOP_OD)/2=6 1/4"; -A=-90"; A=90"; A+.5=90 1/2"; A/2=45"; B=239"; B/2=119 1/2"; C=111"; C/2=55 1/2"; DUAL_F=202"; DUAL_F+1"=203"; DUAL_G=200 7/8"; E=85 3/8"; GA=1/8"; LONG_RO=194 5/8"; LONG_RO/2=97 5/16"; MB_A=126"; MB_HT=99 11/16"; MB_HT+.25"=99 15/16"; MB_HT-2.75"=96 15/16"; MB_HT/2=49 27/32"; Model=QMXVP-1X2_Mixing Box_Sides; NOZZLE_BOTTOM_ID=69 3/8"; NOZZLE_BOTTOM_RAD=34 11/16"; NOZZLE_HEIGHT=110"; NOZZLE_HEIGHT/7*2=27 1/2"; NOZZLE_SIZE=588"; NOZZLE_TOP_OD=76"; NOZZLE_TOP_RAD=38"; NOZZLE_WB/4=20 3/16"; NOZZLE_WB_OD=101"; NOZZLE_WB_RAD=50 1/2"; NOZZLE_WB_RAD-2"=48 1/2"; RO=79 1/8"; RO/2=39 9/16"; RO2/2=41"; TRANSITION_TOP=121 1/4"; TYPE=0"; Type Comments=Vari-Plume Laboratory Exhaust Mixed-Flow Inline Belt Drive With 1X2 Mixing Box With Weather Hoods On Sides; UNIT_HEIGHT=87"; UNIT_HEIGHT*.75=65 1/4"; UNIT_OD=76 7/16"; UNIT_RAD+((A/2)+.25")=83 15/32"; UNIT_RAD+((A/2)+.25")+4"=87 15/32"; UNIT_RADIUS=38 7/32"; UNIT_RADIUS*.6=34 13/32"; UNIT_RADIUS+4"=42 7/32"
- 540_QMXVP-49H-1X2_Mixing_Box_Ends: (A/2)+.25"=45 1/4"; (A/2)+.5"=-45 1/2"; (A/2)-.5"=-44 1/2"; (A/2)-2"=43"; (NOZZLE_HEIGHT-(NOZZLE_HEIGHT/8*2))/2=41 1/4"; (NOZZLE_WB_OD-NOZZLE_TOP_OD)/2=6 1/4"; -A=-90"; A=90"; A+.5=90 1/2"; A/2=45"; B=239"; B/2=119 1/2"; C=111"; C/2=55 1/2"; DUAL_F=202"; DUAL_F+1"=203"; DUAL_G=200 7/8"; E=85 3/8"; GA=1/8"; LONG_RO=194 5/8"; LONG_RO/2=97 5/16"; MB_A=126"; MB_HT=99 11/16"; MB_HT+.25"=99 15/16"; MB_HT-2.75"=96 15/16"; MB_HT/2=49 27/32"; Model=QMXVP-1X2_Mixing Box_Sides; NOZZLE_BOTTOM_ID=69 3/8"; NOZZLE_BOTTOM_RAD=34 11/16"; NOZZLE_HEIGHT=110"; NOZZLE_HEIGHT/7*2=27 1/2"; NOZZLE_SIZE=588"; NOZZLE_TOP_OD=76"; NOZZLE_TOP_RAD=38"; NOZZLE_WB/4=20 3/16"; NOZZLE_WB_OD=101"; NOZZLE_WB_RAD=50 1/2"; NOZZLE_WB_RAD-2"=48 1/2"; RO=79 1/8"; RO/2=39 9/16"; RO2/2=41"; TRANSITION_TOP=121 1/4"; TYPE=0"; Type Comments=Vari-Plume Laboratory Exhaust Mixed-Flow Inline Belt Drive With 1X2 Mixing Box With Weather Hoods On Sides; UNIT_HEIGHT=87"; UNIT_HEIGHT*.75=65 1/4"; UNIT_OD=76 7/16"; UNIT_RAD+((A/2)+.25")=83 15/32"; UNIT_RAD+((A/2)+.25")+4"=87 15/32"; UNIT_RADIUS=38 7/32"; UNIT_RADIUS*.6=34 13/32"; UNIT_RADIUS+4"=42 7/32"
- 600_QMXVP-36L-1X2_Mixing_Box_Ends: (A/2)+.25"=50 3/4"; (A/2)+.5"=-51"; (A/2)-.5"=-50"; (A/2)-2"=48 1/2"; (NOZZLE_HEIGHT-(NOZZLE_HEIGHT/8*2))/2=35 5/8"; (NOZZLE_WB_OD-NOZZLE_TOP_OD)/2=8"; -A=-101"; A=101"; A+.5=101 1/2"; A/2=50 1/2"; B=263"; B/2=131 1/2"; C=122"; C/2=61"; DUAL_F=213"; DUAL_F+1"=214"; DUAL_G=211 7/8"; E=94 3/8"; GA=3/16"; LONG_RO=205 5/8"; LONG_RO/2=102 13/16"; MB_A=144"; MB_HT=117 3/16"; MB_HT+.25"=117 7/16"; MB_HT-2.75"=114 7/16"; MB_HT/2=58 19/32"; Model=QMXVP-1X2_Mixing Box_Sides; NOZZLE_BOTTOM_ID=51 3/4"; NOZZLE_BOTTOM_RAD=25 7/8"; NOZZLE_HEIGHT=95"; NOZZLE_HEIGHT/7*2=23 3/4"; NOZZLE_SIZE=432"; NOZZLE_TOP_OD=58"; NOZZLE_TOP_RAD=29"; NOZZLE_WB/4=18"; NOZZLE_WB_OD=90"; NOZZLE_WB_RAD=45"; NOZZLE_WB_RAD-2"=43"; RO=88 1/16"; RO/2=44 1/32"; RO2/2=46 1/32"; TRANSITION_TOP=170 3/4"; TYPE=0"; Type Comments=Vari-Plume Laboratory Exhaust Mixed-Flow Inline Belt Drive With 1X2 Mixing Box With Weather Hoods On Sides; UNIT_HEIGHT=95 1/2"; UNIT_HEIGHT*.75=71 5/8"; UNIT_OD=84 7/8"; UNIT_RAD+((A/2)+.25")=93 3/16"; UNIT_RAD+((A/2)+.25")+4"=97 3/16"; UNIT_RADIUS=42 7/16"; UNIT_RADIUS*.6=38 3/16"; UNIT_RADIUS+4"=46 7/16"
- 600_QMXVP-36H-1X2_Mixing_Box_Ends: (A/2)+.25"=50 3/4"; (A/2)+.5"=-51"; (A/2)-.5"=-50"; (A/2)-2"=48 1/2"; (NOZZLE_HEIGHT-(NOZZLE_HEIGHT/8*2))/2=35 5/8"; (NOZZLE_WB_OD-NOZZLE_TOP_OD)/2=8"; -A=-101"; A=101"; A+.5=101 1/2"; A/2=50 1/2"; B=263"; B/2=131 1/2"; C=122"; C/2=61"; DUAL_F=213"; DUAL_F+1"=214"; DUAL_G=211 7/8"; E=94 3/8"; GA=3/16"; LONG_RO=205 5/8"; LONG_RO/2=102 13/16"; MB_A=144"; MB_HT=117 3/16"; MB_HT+.25"=117 7/16"; MB_HT-2.75"=114 7/16"; MB_HT/2=58 19/32"; Model=QMXVP-1X2_Mixing Box_Sides; NOZZLE_BOTTOM_ID=51 3/4"; NOZZLE_BOTTOM_RAD=25 7/8"; NOZZLE_HEIGHT=95"; NOZZLE_HEIGHT/7*2=23 3/4"; NOZZLE_SIZE=432"; NOZZLE_TOP_OD=58"; NOZZLE_TOP_RAD=29"; NOZZLE_WB/4=18"; NOZZLE_WB_OD=90"; NOZZLE_WB_RAD=45"; NOZZLE_WB_RAD-2"=43"; RO=88 1/16"; RO/2=44 1/32"; RO2/2=46 1/32"; TRANSITION_TOP=170 3/4"; TYPE=0"; Type Comments=Vari-Plume Laboratory Exhaust Mixed-Flow Inline Belt Drive With 1X2 Mixing Box With Weather Hoods On Sides; UNIT_HEIGHT=95 1/2"; UNIT_HEIGHT*.75=71 5/8"; UNIT_OD=84 7/8"; UNIT_RAD+((A/2)+.25")=93 3/16"; UNIT_RAD+((A/2)+.25")+4"=97 3/16"; UNIT_RADIUS=42 7/16"; UNIT_RADIUS*.6=38 3/16"; UNIT_RADIUS+4"=46 7/16"
- 600_QMXVP-49L-1X2_Mixing_Box_Ends: (A/2)+.25"=50 3/4"; (A/2)+.5"=-51"; (A/2)-.5"=-50"; (A/2)-2"=48 1/2"; (NOZZLE_HEIGHT-(NOZZLE_HEIGHT/8*2))/2=41 1/4"; (NOZZLE_WB_OD-NOZZLE_TOP_OD)/2=6 1/4"; -A=-101"; A=101"; A+.5=101 1/2"; A/2=50 1/2"; B=263"; B/2=131 1/2"; C=122"; C/2=61"; DUAL_F=213"; DUAL_F+1"=214"; DUAL_G=211 7/8"; E=94 3/8"; GA=3/16"; LONG_RO=205 5/8"; LONG_RO/2=102 13/16"; MB_A=144"; MB_HT=117 3/16"; MB_HT+.25"=117 7/16"; MB_HT-2.75"=114 7/16"; MB_HT/2=58 19/32"; Model=QMXVP-1X2_Mixing Box_Sides; NOZZLE_BOTTOM_ID=69 3/8"; NOZZLE_BOTTOM_RAD=34 11/16"; NOZZLE_HEIGHT=110"; NOZZLE_HEIGHT/7*2=27 1/2"; NOZZLE_SIZE=588"; NOZZLE_TOP_OD=76"; NOZZLE_TOP_RAD=38"; NOZZLE_WB/4=20 3/16"; NOZZLE_WB_OD=101"; NOZZLE_WB_RAD=50 1/2"; NOZZLE_WB_RAD-2"=48 1/2"; RO=88 1/16"; RO/2=44 1/32"; RO2/2=46 1/32"; TRANSITION_TOP=148 3/4"; TYPE=0"; Type Comments=Vari-Plume Laboratory Exhaust Mixed-Flow Inline Belt Drive With 1X2 Mixing Box With Weather Hoods On Sides; UNIT_HEIGHT=95 1/2"; UNIT_HEIGHT*.75=71 5/8"; UNIT_OD=84 7/8"; UNIT_RAD+((A/2)+.25")=93 3/16"; UNIT_RAD+((A/2)+.25")+4"=97 3/16"; UNIT_RADIUS=42 7/16"; UNIT_RADIUS*.6=38 3/16"; UNIT_RADIUS+4"=46 7/16"
- 600_QMXVP-49H-1X2_Mixing_Box_Ends: (A/2)+.25"=50 3/4"; (A/2)+.5"=-51"; (A/2)-.5"=-50"; (A/2)-2"=48 1/2"; (NOZZLE_HEIGHT-(NOZZLE_HEIGHT/8*2))/2=41 1/4"; (NOZZLE_WB_OD-NOZZLE_TOP_OD)/2=6 1/4"; -A=-101"; A=101"; A+.5=101 1/2"; A/2=50 1/2"; B=263"; B/2=131 1/2"; C=122"; C/2=61"; DUAL_F=213"; DUAL_F+1"=214"; DUAL_G=211 7/8"; E=94 3/8"; GA=3/16"; LONG_RO=205 5/8"; LONG_RO/2=102 13/16"; MB_A=144"; MB_HT=117 3/16"; MB_HT+.25"=117 7/16"; MB_HT-2.75"=114 7/16"; MB_HT/2=58 19/32"; Model=QMXVP-1X2_Mixing Box_Sides; NOZZLE_BOTTOM_ID=69 3/8"; NOZZLE_BOTTOM_RAD=34 11/16"; NOZZLE_HEIGHT=110"; NOZZLE_HEIGHT/7*2=27 1/2"; NOZZLE_SIZE=588"; NOZZLE_TOP_OD=76"; NOZZLE_TOP_RAD=38"; NOZZLE_WB/4=20 3/16"; NOZZLE_WB_OD=101"; NOZZLE_WB_RAD=50 1/2"; NOZZLE_WB_RAD-2"=48 1/2"; RO=88 1/16"; RO/2=44 1/32"; RO2/2=46 1/32"; TRANSITION_TOP=148 3/4"; TYPE=0"; Type Comments=Vari-Plume Laboratory Exhaust Mixed-Flow Inline Belt Drive With 1X2 Mixing Box With Weather Hoods On Sides; UNIT_HEIGHT=95 1/2"; UNIT_HEIGHT*.75=71 5/8"; UNIT_OD=84 7/8"; UNIT_RAD+((A/2)+.25")=93 3/16"; UNIT_RAD+((A/2)+.25")+4"=97 3/16"; UNIT_RADIUS=42 7/16"; UNIT_RADIUS*.6=38 3/16"; UNIT_RADIUS+4"=46 7/16"
- 120_QMXHPVP-12H-1X2_Mixing_Box_Ends: (A/2)+.25"=14 1/4"; (A/2)+.5"=-14 1/2"; (A/2)-.5"=-13 1/2"; (A/2)-2"=12"; (NOZZLE_HEIGHT-(NOZZLE_HEIGHT/8*2))/2=12"; (NOZZLE_WB_OD-NOZZLE_TOP_OD)/2=2 1/8"; -A=-28"; A=28"; A+.5=28 1/2"; A/2=14"; B=71"; B/2=35 1/2"; C=37"; C/2=18 1/2"; DUAL_F=64"; DUAL_F+1"=65"; DUAL_G=63 5/16"; E=27 3/16"; GA=3/32"; LONG_RO=57 1/16"; LONG_RO/2=28 17/32"; MB_A=35"; MB_HT=31 7/16"; MB_HT+.25"=31 11/16"; MB_HT-2.75"=28 11/16"; MB_HT/2=15 23/32"; Model=QMXHPVP-1X2_Mixing Box_Sides; NOZZLE_BOTTOM_ID=17 1/16"; NOZZLE_BOTTOM_RAD=8 17/32"; NOZZLE_HEIGHT=32"; NOZZLE_HEIGHT/7*2=8"; NOZZLE_SIZE=144"; NOZZLE_TOP_OD=19 1/2"; NOZZLE_TOP_RAD=9 3/4"; NOZZLE_WB/4=5 19/32"; NOZZLE_WB_OD=28"; NOZZLE_WB_RAD=14"; NOZZLE_WB_RAD-2"=12"; RO=21"; RO/2=10 1/2"; RO2/2=10 1/2"; TRANSITION_TOP=39 7/16"; TYPE=12"; Type Comments=Vari-Plume Laboratory Exhaust Mixed-Flow High Pressure Inline Belt Drive With 1X2 Mixing Box With Weather Hoods On Sides; UNIT_HEIGHT=19 7/8"; UNIT_HEIGHT*.75=14 29/32"; UNIT_OD=17 1/16"; UNIT_RAD+((A/2)+.25")=22 25/32"; UNIT_RAD+((A/2)+.25")+4"=26 25/32"; UNIT_RADIUS=8 17/32"; UNIT_RADIUS*.6=7 11/16"; UNIT_RADIUS+4"=12 17/32"
- 120_QMXHPVP-12L-1X2_Mixing_Box_Ends: (A/2)+.25"=14 1/4"; (A/2)+.5"=-14 1/2"; (A/2)-.5"=-13 1/2"; (A/2)-2"=12"; (NOZZLE_HEIGHT-(NOZZLE_HEIGHT/8*2))/2=12"; (NOZZLE_WB_OD-NOZZLE_TOP_OD)/2=2 1/8"; -A=-28"; A=28"; A+.5=28 1/2"; A/2=14"; B=71"; B/2=35 1/2"; C=37"; C/2=18 1/2"; DUAL_F=64"; DUAL_F+1"=65"; DUAL_G=63 5/16"; E=27 3/16"; GA=3/32"; LONG_RO=57 1/16"; LONG_RO/2=28 17/32"; MB_A=35"; MB_HT=31 7/16"; MB_HT+.25"=31 11/16"; MB_HT-2.75"=28 11/16"; MB_HT/2=15 23/32"; Model=QMXHPVP-1X2_Mixing Box_Sides; NOZZLE_BOTTOM_ID=17 1/16"; NOZZLE_BOTTOM_RAD=8 17/32"; NOZZLE_HEIGHT=32"; NOZZLE_HEIGHT/7*2=8"; NOZZLE_SIZE=144"; NOZZLE_TOP_OD=19 1/2"; NOZZLE_TOP_RAD=9 3/4"; NOZZLE_WB/4=5 19/32"; NOZZLE_WB_OD=28"; NOZZLE_WB_RAD=14"; NOZZLE_WB_RAD-2"=12"; RO=21"; RO/2=10 1/2"; RO2/2=10 1/2"; TRANSITION_TOP=39 7/16"; TYPE=12"; Type Comments=Vari-Plume Laboratory Exhaust Mixed-Flow High Pressure Inline Belt Drive With 1X2 Mixing Box With Weather Hoods On Sides; UNIT_HEIGHT=19 7/8"; UNIT_HEIGHT*.75=14 29/32"; UNIT_OD=17 1/16"; UNIT_RAD+((A/2)+.25")=22 25/32"; UNIT_RAD+((A/2)+.25")+4"=26 25/32"; UNIT_RADIUS=8 17/32"; UNIT_RADIUS*.6=7 11/16"; UNIT_RADIUS+4"=12 17/32"
- 120_QMXHPVP-9H-1X2_Mixing_Box_Ends: (A/2)+.25"=14 1/4"; (A/2)+.5"=-14 1/2"; (A/2)-.5"=-13 1/2"; (A/2)-2"=12"; (NOZZLE_HEIGHT-(NOZZLE_HEIGHT/8*2))/2=10 1/2"; (NOZZLE_WB_OD-NOZZLE_TOP_OD)/2=2 3/8"; -A=-28"; A=28"; A+.5=28 1/2"; A/2=14"; B=71"; B/2=35 1/2"; C=37"; C/2=18 1/2"; DUAL_F=64"; DUAL_F+1"=65"; DUAL_G=63 5/16"; E=27 3/16"; GA=3/32"; LONG_RO=57 1/16"; LONG_RO/2=28 17/32"; MB_A=35"; MB_HT=31 7/16"; MB_HT+.25"=31 11/16"; MB_HT-2.75"=28 11/16"; MB_HT/2=15 23/32"; Model=QMXHPVP-1X2_Mixing Box_Sides; NOZZLE_BOTTOM_ID=12 13/16"; NOZZLE_BOTTOM_RAD=6 13/32"; NOZZLE_HEIGHT=28"; NOZZLE_HEIGHT/7*2=7"; NOZZLE_SIZE=108"; NOZZLE_TOP_OD=13 1/2"; NOZZLE_TOP_RAD=6 3/4"; NOZZLE_WB/4=4 19/32"; NOZZLE_WB_OD=23"; NOZZLE_WB_RAD=11 1/2"; NOZZLE_WB_RAD-2"=9 1/2"; RO=21"; RO/2=10 1/2"; RO2/2=10 1/2"; TRANSITION_TOP=43 3/16"; TYPE=12"; Type Comments=Vari-Plume Laboratory Exhaust Mixed-Flow High Pressure Inline Belt Drive With 1X2 Mixing Box With Weather Hoods On Sides; UNIT_HEIGHT=19 7/8"; UNIT_HEIGHT*.75=14 29/32"; UNIT_OD=17 1/16"; UNIT_RAD+((A/2)+.25")=22 25/32"; UNIT_RAD+((A/2)+.25")+4"=26 25/32"; UNIT_RADIUS=8 17/32"; UNIT_RADIUS*.6=7 11/16"; UNIT_RADIUS+4"=12 17/32"
- 120_QMXHPVP-9L-1X2_Mixing_Box_Ends: (A/2)+.25"=14 1/4"; (A/2)+.5"=-14 1/2"; (A/2)-.5"=-13 1/2"; (A/2)-2"=12"; (NOZZLE_HEIGHT-(NOZZLE_HEIGHT/8*2))/2=10 1/2"; (NOZZLE_WB_OD-NOZZLE_TOP_OD)/2=2 3/8"; -A=-28"; A=28"; A+.5=28 1/2"; A/2=14"; B=71"; B/2=35 1/2"; C=37"; C/2=18 1/2"; DUAL_F=64"; DUAL_F+1"=65"; DUAL_G=63 5/16"; E=27 3/16"; GA=3/32"; LONG_RO=57 1/16"; LONG_RO/2=28 17/32"; MB_A=35"; MB_HT=31 7/16"; MB_HT+.25"=31 11/16"; MB_HT-2.75"=28 11/16"; MB_HT/2=15 23/32"; Model=QMXHPVP-1X2_Mixing Box_Sides; NOZZLE_BOTTOM_ID=12 13/16"; NOZZLE_BOTTOM_RAD=6 13/32"; NOZZLE_HEIGHT=28"; NOZZLE_HEIGHT/7*2=7"; NOZZLE_SIZE=108"; NOZZLE_TOP_OD=13 1/2"; NOZZLE_TOP_RAD=6 3/4"; NOZZLE_WB/4=4 19/32"; NOZZLE_WB_OD=23"; NOZZLE_WB_RAD=11 1/2"; NOZZLE_WB_RAD-2"=9 1/2"; RO=21"; RO/2=10 1/2"; RO2/2=10 1/2"; TRANSITION_TOP=43 3/16"; TYPE=12"; Type Comments=Vari-Plume Laboratory Exhaust Mixed-Flow High Pressure Inline Belt Drive With 1X2 Mixing Box With Weather Hoods On Sides; UNIT_HEIGHT=19 7/8"; UNIT_HEIGHT*.75=14 29/32"; UNIT_OD=17 1/16"; UNIT_RAD+((A/2)+.25")=22 25/32"; UNIT_RAD+((A/2)+.25")+4"=26 25/32"; UNIT_RADIUS=8 17/32"; UNIT_RADIUS*.6=7 11/16"; UNIT_RADIUS+4"=12 17/32"
- 135_QMXHPVP-12H-1X2_Mixing_Box_Ends: (A/2)+.25"=14 1/4"; (A/2)+.5"=-14 1/2"; (A/2)-.5"=-13 1/2"; (A/2)-2"=12"; (NOZZLE_HEIGHT-(NOZZLE_HEIGHT/8*2))/2=12"; (NOZZLE_WB_OD-NOZZLE_TOP_OD)/2=2 1/8"; -A=-28"; A=28"; A+.5=28 1/2"; A/2=14"; B=77"; B/2=38 1/2"; C=39"; C/2=19 1/2"; DUAL_F=64"; DUAL_F+1"=65"; DUAL_G=63 5/16"; E=27 1/8"; GA=3/32"; LONG_RO=57 1/16"; LONG_RO/2=28 17/32"; MB_A=36"; MB_HT=33 7/16"; MB_HT+.25"=33 11/16"; MB_HT-2.75"=30 11/16"; MB_HT/2=16 23/32"; Model=QMXHPVP-1X2_Mixing Box_Sides; NOZZLE_BOTTOM_ID=17 1/16"; NOZZLE_BOTTOM_RAD=8 17/32"; NOZZLE_HEIGHT=32"; NOZZLE_HEIGHT/7*2=8"; NOZZLE_SIZE=144"; NOZZLE_TOP_OD=19 1/2"; NOZZLE_TOP_RAD=9 3/4"; NOZZLE_WB/4=5 19/32"; NOZZLE_WB_OD=28"; NOZZLE_WB_RAD=14"; NOZZLE_WB_RAD-2"=12"; RO=20 15/16"; RO/2=10 15/32"; RO2/2=10 15/32"; TRANSITION_TOP=40 11/16"; TYPE=12"; Type Comments=Vari-Plume Laboratory Exhaust Mixed-Flow High Pressure Inline Belt Drive With 1X2 Mixing Box With Weather Hoods On Sides; UNIT_HEIGHT=27"; UNIT_HEIGHT*.75=20 1/4"; UNIT_OD=19 1/4"; UNIT_RAD+((A/2)+.25")=23 7/8"; UNIT_RAD+((A/2)+.25")+4"=27 7/8"; UNIT_RADIUS=9 5/8"; UNIT_RADIUS*.6=8 21/32"; UNIT_RADIUS+4"=13 5/8"
- 135_QMXHPVP-12L-1X2_Mixing_Box_Ends: (A/2)+.25"=14 1/4"; (A/2)+.5"=-14 1/2"; (A/2)-.5"=-13 1/2"; (A/2)-2"=12"; (NOZZLE_HEIGHT-(NOZZLE_HEIGHT/8*2))/2=12"; (NOZZLE_WB_OD-NOZZLE_TOP_OD)/2=2 1/8"; -A=-28"; A=28"; A+.5=28 1/2"; A/2=14"; B=77"; B/2=38 1/2"; C=39"; C/2=19 1/2"; DUAL_F=64"; DUAL_F+1"=65"; DUAL_G=63 5/16"; E=27 1/8"; GA=3/32"; LONG_RO=57 1/16"; LONG_RO/2=28 17/32"; MB_A=36"; MB_HT=33 7/16"; MB_HT+.25"=33 11/16"; MB_HT-2.75"=30 11/16"; MB_HT/2=16 23/32"; Model=QMXHPVP-1X2_Mixing Box_Sides; NOZZLE_BOTTOM_ID=17 1/16"; NOZZLE_BOTTOM_RAD=8 17/32"; NOZZLE_HEIGHT=32"; NOZZLE_HEIGHT/7*2=8"; NOZZLE_SIZE=144"; NOZZLE_TOP_OD=19 1/2"; NOZZLE_TOP_RAD=9 3/4"; NOZZLE_WB/4=5 19/32"; NOZZLE_WB_OD=28"; NOZZLE_WB_RAD=14"; NOZZLE_WB_RAD-2"=12"; RO=20 15/16"; RO/2=10 15/32"; RO2/2=10 15/32"; TRANSITION_TOP=40 11/16"; TYPE=12"; Type Comments=Vari-Plume Laboratory Exhaust Mixed-Flow High Pressure Inline Belt Drive With 1X2 Mixing Box With Weather Hoods On Sides; UNIT_HEIGHT=27"; UNIT_HEIGHT*.75=20 1/4"; UNIT_OD=19 1/4"; UNIT_RAD+((A/2)+.25")=23 7/8"; UNIT_RAD+((A/2)+.25")+4"=27 7/8"; UNIT_RADIUS=9 5/8"; UNIT_RADIUS*.6=8 21/32"; UNIT_RADIUS+4"=13 5/8"
- 135_QMXHPVP-9H-1X2_Mixing_Box_Ends: (A/2)+.25"=14 1/4"; (A/2)+.5"=-14 1/2"; (A/2)-.5"=-13 1/2"; (A/2)-2"=12"; (NOZZLE_HEIGHT-(NOZZLE_HEIGHT/8*2))/2=10 1/2"; (NOZZLE_WB_OD-NOZZLE_TOP_OD)/2=2 3/8"; -A=-28"; A=28"; A+.5=28 1/2"; A/2=14"; B=77"; B/2=38 1/2"; C=39"; C/2=19 1/2"; DUAL_F=64"; DUAL_F+1"=65"; DUAL_G=63 5/16"; E=27 1/8"; GA=3/32"; LONG_RO=57 1/16"; LONG_RO/2=28 17/32"; MB_A=36"; MB_HT=33 7/16"; MB_HT+.25"=33 11/16"; MB_HT-2.75"=30 11/16"; MB_HT/2=16 23/32"; Model=QMXHPVP-1X2_Mixing Box_Sides; NOZZLE_BOTTOM_ID=12 13/16"; NOZZLE_BOTTOM_RAD=6 13/32"; NOZZLE_HEIGHT=28"; NOZZLE_HEIGHT/7*2=7"; NOZZLE_SIZE=108"; NOZZLE_TOP_OD=13 1/2"; NOZZLE_TOP_RAD=6 3/4"; NOZZLE_WB/4=4 19/32"; NOZZLE_WB_OD=23"; NOZZLE_WB_RAD=11 1/2"; NOZZLE_WB_RAD-2"=9 1/2"; RO=20 15/16"; RO/2=10 15/32"; RO2/2=10 15/32"; TRANSITION_TOP=48 11/16"; TYPE=12"; Type Comments=Vari-Plume Laboratory Exhaust Mixed-Flow High Pressure Inline Belt Drive With 1X2 Mixing Box With Weather Hoods On Sides; UNIT_HEIGHT=27"; UNIT_HEIGHT*.75=20 1/4"; UNIT_OD=19 1/4"; UNIT_RAD+((A/2)+.25")=23 7/8"; UNIT_RAD+((A/2)+.25")+4"=27 7/8"; UNIT_RADIUS=9 5/8"; UNIT_RADIUS*.6=8 21/32"; UNIT_RADIUS+4"=13 5/8"
- 135_QMXHPVP-9L-1X2_Mixing_Box_Ends: (A/2)+.25"=14 1/4"; (A/2)+.5"=-14 1/2"; (A/2)-.5"=-13 1/2"; (A/2)-2"=12"; (NOZZLE_HEIGHT-(NOZZLE_HEIGHT/8*2))/2=10 1/2"; (NOZZLE_WB_OD-NOZZLE_TOP_OD)/2=2 3/8"; -A=-28"; A=28"; A+.5=28 1/2"; A/2=14"; B=77"; B/2=38 1/2"; C=39"; C/2=19 1/2"; DUAL_F=64"; DUAL_F+1"=65"; DUAL_G=63 5/16"; E=27 1/8"; GA=3/32"; LONG_RO=57 1/16"; LONG_RO/2=28 17/32"; MB_A=36"; MB_HT=33 7/16"; MB_HT+.25"=33 11/16"; MB_HT-2.75"=30 11/16"; MB_HT/2=16 23/32"; Model=QMXHPVP-1X2_Mixing Box_Sides; NOZZLE_BOTTOM_ID=12 13/16"; NOZZLE_BOTTOM_RAD=6 13/32"; NOZZLE_HEIGHT=28"; NOZZLE_HEIGHT/7*2=7"; NOZZLE_SIZE=108"; NOZZLE_TOP_OD=13 1/2"; NOZZLE_TOP_RAD=6 3/4"; NOZZLE_WB/4=4 19/32"; NOZZLE_WB_OD=23"; NOZZLE_WB_RAD=11 1/2"; NOZZLE_WB_RAD-2"=9 1/2"; RO=20 15/16"; RO/2=10 15/32"; RO2/2=10 15/32"; TRANSITION_TOP=48 11/16"; TYPE=12"; Type Comments=Vari-Plume Laboratory Exhaust Mixed-Flow High Pressure Inline Belt Drive With 1X2 Mixing Box With Weather Hoods On Sides; UNIT_HEIGHT=27"; UNIT_HEIGHT*.75=20 1/4"; UNIT_OD=19 1/4"; UNIT_RAD+((A/2)+.25")=23 7/8"; UNIT_RAD+((A/2)+.25")+4"=27 7/8"; UNIT_RADIUS=9 5/8"; UNIT_RADIUS*.6=8 21/32"; UNIT_RADIUS+4"=13 5/8"
- 150_QMXHPVP-12H-1X2_Mixing_Box_Ends: (A/2)+.25"=15 1/4"; (A/2)+.5"=-15 1/2"; (A/2)-.5"=-14 1/2"; (A/2)-2"=13"; (NOZZLE_HEIGHT-(NOZZLE_HEIGHT/8*2))/2=12"; (NOZZLE_WB_OD-NOZZLE_TOP_OD)/2=2 1/8"; -A=-30"; A=30"; A+.5=30 1/2"; A/2=15"; B=87"; B/2=43 1/2"; C=42"; C/2=21"; DUAL_F=68"; DUAL_F+1"=69"; DUAL_G=67 5/16"; E=29 1/8"; GA=3/32"; LONG_RO=61 1/16"; LONG_RO/2=30 17/32"; MB_A=38"; MB_HT=35 3/16"; MB_HT+.25"=35 7/16"; MB_HT-2.75"=32 7/16"; MB_HT/2=17 19/32"; Model=QMXHPVP-1X2_Mixing Box_Sides; NOZZLE_BOTTOM_ID=17 1/16"; NOZZLE_BOTTOM_RAD=8 17/32"; NOZZLE_HEIGHT=32"; NOZZLE_HEIGHT/7*2=8"; NOZZLE_SIZE=144"; NOZZLE_TOP_OD=19 1/2"; NOZZLE_TOP_RAD=9 3/4"; NOZZLE_WB/4=5 19/32"; NOZZLE_WB_OD=28"; NOZZLE_WB_RAD=14"; NOZZLE_WB_RAD-2"=12"; RO=22 15/16"; RO/2=11 15/32"; RO2/2=11 15/32"; TRANSITION_TOP=46 1/4"; TYPE=12"; Type Comments=Vari-Plume Laboratory Exhaust Mixed-Flow High Pressure Inline Belt Drive With 1X2 Mixing Box With Weather Hoods On Sides; UNIT_HEIGHT=30"; UNIT_HEIGHT*.75=22 1/2"; UNIT_OD=21 3/8"; UNIT_RAD+((A/2)+.25")=25 15/16"; UNIT_RAD+((A/2)+.25")+4"=29 15/16"; UNIT_RADIUS=10 11/16"; UNIT_RADIUS*.6=9 5/8"; UNIT_RADIUS+4"=14 11/16"
- 150_QMXHPVP-12L-1X2_Mixing_Box_Ends: (A/2)+.25"=15 1/4"; (A/2)+.5"=-15 1/2"; (A/2)-.5"=-14 1/2"; (A/2)-2"=13"; (NOZZLE_HEIGHT-(NOZZLE_HEIGHT/8*2))/2=12"; (NOZZLE_WB_OD-NOZZLE_TOP_OD)/2=2 1/8"; -A=-30"; A=30"; A+.5=30 1/2"; A/2=15"; B=87"; B/2=43 1/2"; C=42"; C/2=21"; DUAL_F=68"; DUAL_F+1"=69"; DUAL_G=67 5/16"; E=29 1/8"; GA=3/32"; LONG_RO=61 1/16"; LONG_RO/2=30 17/32"; MB_A=38"; MB_HT=35 3/16"; MB_HT+.25"=35 7/16"; MB_HT-2.75"=32 7/16"; MB_HT/2=17 19/32"; Model=QMXHPVP-1X2_Mixing Box_Sides; NOZZLE_BOTTOM_ID=17 1/16"; NOZZLE_BOTTOM_RAD=8 17/32"; NOZZLE_HEIGHT=32"; NOZZLE_HEIGHT/7*2=8"; NOZZLE_SIZE=144"; NOZZLE_TOP_OD=19 1/2"; NOZZLE_TOP_RAD=9 3/4"; NOZZLE_WB/4=5 19/32"; NOZZLE_WB_OD=28"; NOZZLE_WB_RAD=14"; NOZZLE_WB_RAD-2"=12"; RO=22 15/16"; RO/2=11 15/32"; RO2/2=11 15/32"; TRANSITION_TOP=46 1/4"; TYPE=12"; Type Comments=Vari-Plume Laboratory Exhaust Mixed-Flow High Pressure Inline Belt Drive With 1X2 Mixing Box With Weather Hoods On Sides; UNIT_HEIGHT=30"; UNIT_HEIGHT*.75=22 1/2"; UNIT_OD=21 3/8"; UNIT_RAD+((A/2)+.25")=25 15/16"; UNIT_RAD+((A/2)+.25")+4"=29 15/16"; UNIT_RADIUS=10 11/16"; UNIT_RADIUS*.6=9 5/8"; UNIT_RADIUS+4"=14 11/16"
- 150_QMXHPVP-15H-1X2_Mixing_Box_Ends: (A/2)+.25"=15 1/4"; (A/2)+.5"=-15 1/2"; (A/2)-.5"=-14 1/2"; (A/2)-2"=13"; (NOZZLE_HEIGHT-(NOZZLE_HEIGHT/8*2))/2=16 1/8"; (NOZZLE_WB_OD-NOZZLE_TOP_OD)/2=3 1/4"; -A=-30"; A=30"; A+.5=30 1/2"; A/2=15"; B=87"; B/2=43 1/2"; C=42"; C/2=21"; DUAL_F=68"; DUAL_F+1"=69"; DUAL_G=67 5/16"; E=29 1/8"; GA=3/32"; LONG_RO=61 1/16"; LONG_RO/2=30 17/32"; MB_A=38"; MB_HT=35 3/16"; MB_HT+.25"=35 7/16"; MB_HT-2.75"=32 7/16"; MB_HT/2=17 19/32"; Model=QMXHPVP-1X2_Mixing Box_Sides; NOZZLE_BOTTOM_ID=21 3/8"; NOZZLE_BOTTOM_RAD=10 11/16"; NOZZLE_HEIGHT=43"; NOZZLE_HEIGHT/7*2=10 3/4"; NOZZLE_SIZE=180"; NOZZLE_TOP_OD=23"; NOZZLE_TOP_RAD=11 1/2"; NOZZLE_WB/4=7 3/16"; NOZZLE_WB_OD=36"; NOZZLE_WB_RAD=18"; NOZZLE_WB_RAD-2"=16"; RO=22 15/16"; RO/2=11 15/32"; RO2/2=11 15/32"; TRANSITION_TOP=43 5/16"; TYPE=12"; Type Comments=Vari-Plume Laboratory Exhaust Mixed-Flow High Pressure Inline Belt Drive With 1X2 Mixing Box With Weather Hoods On Sides; UNIT_HEIGHT=30"; UNIT_HEIGHT*.75=22 1/2"; UNIT_OD=21 3/8"; UNIT_RAD+((A/2)+.25")=25 15/16"; UNIT_RAD+((A/2)+.25")+4"=29 15/16"; UNIT_RADIUS=10 11/16"; UNIT_RADIUS*.6=9 5/8"; UNIT_RADIUS+4"=14 11/16"
- 150_QMXHPVP-15L-1X2_Mixing_Box_Ends: (A/2)+.25"=15 1/4"; (A/2)+.5"=-15 1/2"; (A/2)-.5"=-14 1/2"; (A/2)-2"=13"; (NOZZLE_HEIGHT-(NOZZLE_HEIGHT/8*2))/2=16 1/8"; (NOZZLE_WB_OD-NOZZLE_TOP_OD)/2=3 1/4"; -A=-30"; A=30"; A+.5=30 1/2"; A/2=15"; B=87"; B/2=43 1/2"; C=42"; C/2=21"; DUAL_F=68"; DUAL_F+1"=69"; DUAL_G=67 5/16"; E=29 1/8"; GA=3/32"; LONG_RO=61 1/16"; LONG_RO/2=30 17/32"; MB_A=38"; MB_HT=35 3/16"; MB_HT+.25"=35 7/16"; MB_HT-2.75"=32 7/16"; MB_HT/2=17 19/32"; Model=QMXHPVP-1X2_Mixing Box_Sides; NOZZLE_BOTTOM_ID=21 3/8"; NOZZLE_BOTTOM_RAD=10 11/16"; NOZZLE_HEIGHT=43"; NOZZLE_HEIGHT/7*2=10 3/4"; NOZZLE_SIZE=180"; NOZZLE_TOP_OD=23"; NOZZLE_TOP_RAD=11 1/2"; NOZZLE_WB/4=7 3/16"; NOZZLE_WB_OD=36"; NOZZLE_WB_RAD=18"; NOZZLE_WB_RAD-2"=16"; RO=22 15/16"; RO/2=11 15/32"; RO2/2=11 15/32"; TRANSITION_TOP=43 5/16"; TYPE=12"; Type Comments=Vari-Plume Laboratory Exhaust Mixed-Flow High Pressure Inline Belt Drive With 1X2 Mixing Box With Weather Hoods On Sides; UNIT_HEIGHT=30"; UNIT_HEIGHT*.75=22 1/2"; UNIT_OD=21 3/8"; UNIT_RAD+((A/2)+.25")=25 15/16"; UNIT_RAD+((A/2)+.25")+4"=29 15/16"; UNIT_RADIUS=10 11/16"; UNIT_RADIUS*.6=9 5/8"; UNIT_RADIUS+4"=14 11/16"
- 150_QMXHPVP-9H-1X2_Mixing_Box_Ends: (A/2)+.25"=15 1/4"; (A/2)+.5"=-15 1/2"; (A/2)-.5"=-14 1/2"; (A/2)-2"=13"; (NOZZLE_HEIGHT-(NOZZLE_HEIGHT/8*2))/2=10 1/2"; (NOZZLE_WB_OD-NOZZLE_TOP_OD)/2=2 3/8"; -A=-30"; A=30"; A+.5=30 1/2"; A/2=15"; B=87"; B/2=43 1/2"; C=42"; C/2=21"; DUAL_F=68"; DUAL_F+1"=69"; DUAL_G=67 5/16"; E=29 1/8"; GA=3/32"; LONG_RO=61 1/16"; LONG_RO/2=30 17/32"; MB_A=38"; MB_HT=35 3/16"; MB_HT+.25"=35 7/16"; MB_HT-2.75"=32 7/16"; MB_HT/2=17 19/32"; Model=QMXHPVP-1X2_Mixing Box_Sides; NOZZLE_BOTTOM_ID=12 13/16"; NOZZLE_BOTTOM_RAD=6 13/32"; NOZZLE_HEIGHT=28"; NOZZLE_HEIGHT/7*2=7"; NOZZLE_SIZE=108"; NOZZLE_TOP_OD=13 1/2"; NOZZLE_TOP_RAD=6 3/4"; NOZZLE_WB/4=4 19/32"; NOZZLE_WB_OD=23"; NOZZLE_WB_RAD=11 1/2"; NOZZLE_WB_RAD-2"=9 1/2"; RO=22 15/16"; RO/2=11 15/32"; RO2/2=11 15/32"; TRANSITION_TOP=54 1/4"; TYPE=12"; Type Comments=Vari-Plume Laboratory Exhaust Mixed-Flow High Pressure Inline Belt Drive With 1X2 Mixing Box With Weather Hoods On Sides; UNIT_HEIGHT=30"; UNIT_HEIGHT*.75=22 1/2"; UNIT_OD=21 3/8"; UNIT_RAD+((A/2)+.25")=25 15/16"; UNIT_RAD+((A/2)+.25")+4"=29 15/16"; UNIT_RADIUS=10 11/16"; UNIT_RADIUS*.6=9 5/8"; UNIT_RADIUS+4"=14 11/16"
- 150_QMXHPVP-9L-1X2_Mixing_Box_Ends: (A/2)+.25"=15 1/4"; (A/2)+.5"=-15 1/2"; (A/2)-.5"=-14 1/2"; (A/2)-2"=13"; (NOZZLE_HEIGHT-(NOZZLE_HEIGHT/8*2))/2=10 1/2"; (NOZZLE_WB_OD-NOZZLE_TOP_OD)/2=2 3/8"; -A=-30"; A=30"; A+.5=30 1/2"; A/2=15"; B=87"; B/2=43 1/2"; C=42"; C/2=21"; DUAL_F=68"; DUAL_F+1"=69"; DUAL_G=67 5/16"; E=29 1/8"; GA=3/32"; LONG_RO=61 1/16"; LONG_RO/2=30 17/32"; MB_A=38"; MB_HT=35 3/16"; MB_HT+.25"=35 7/16"; MB_HT-2.75"=32 7/16"; MB_HT/2=17 19/32"; Model=QMXHPVP-1X2_Mixing Box_Sides; NOZZLE_BOTTOM_ID=12 13/16"; NOZZLE_BOTTOM_RAD=6 13/32"; NOZZLE_HEIGHT=28"; NOZZLE_HEIGHT/7*2=7"; NOZZLE_SIZE=108"; NOZZLE_TOP_OD=13 1/2"; NOZZLE_TOP_RAD=6 3/4"; NOZZLE_WB/4=4 19/32"; NOZZLE_WB_OD=23"; NOZZLE_WB_RAD=11 1/2"; NOZZLE_WB_RAD-2"=9 1/2"; RO=22 15/16"; RO/2=11 15/32"; RO2/2=11 15/32"; TRANSITION_TOP=54 1/4"; TYPE=12"; Type Comments=Vari-Plume Laboratory Exhaust Mixed-Flow High Pressure Inline Belt Drive With 1X2 Mixing Box With Weather Hoods On Sides; UNIT_HEIGHT=30"; UNIT_HEIGHT*.75=22 1/2"; UNIT_OD=21 3/8"; UNIT_RAD+((A/2)+.25")=25 15/16"; UNIT_RAD+((A/2)+.25")+4"=29 15/16"; UNIT_RADIUS=10 11/16"; UNIT_RADIUS*.6=9 5/8"; UNIT_RADIUS+4"=14 11/16"
- 165_QMXHPVP-12H-1X2_Mixing_Box_Ends: (A/2)+.25"=16 1/4"; (A/2)+.5"=-16 1/2"; (A/2)-.5"=-15 1/2"; (A/2)-2"=14"; (NOZZLE_HEIGHT-(NOZZLE_HEIGHT/8*2))/2=12"; (NOZZLE_WB_OD-NOZZLE_TOP_OD)/2=2 1/8"; -A=-32"; A=32"; A+.5=32 1/2"; A/2=16"; B=89"; B/2=44 1/2"; C=44"; C/2=22"; DUAL_F=72"; DUAL_F+1"=73"; DUAL_G=71 5/16"; E=31 1/8"; GA=3/32"; LONG_RO=65 1/16"; LONG_RO/2=32 17/32"; MB_A=41"; MB_HT=36 15/16"; MB_HT+.25"=37 3/16"; MB_HT-2.75"=34 3/16"; MB_HT/2=18 15/32"; Model=QMXHPVP-1X2_Mixing Box_Sides; NOZZLE_BOTTOM_ID=17 1/16"; NOZZLE_BOTTOM_RAD=8 17/32"; NOZZLE_HEIGHT=32"; NOZZLE_HEIGHT/7*2=8"; NOZZLE_SIZE=144"; NOZZLE_TOP_OD=19 1/2"; NOZZLE_TOP_RAD=9 3/4"; NOZZLE_WB/4=5 19/32"; NOZZLE_WB_OD=28"; NOZZLE_WB_RAD=14"; NOZZLE_WB_RAD-2"=12"; RO=24 15/16"; RO/2=12 15/32"; RO2/2=12 15/32"; TRANSITION_TOP=53 1/4"; TYPE=12"; Type Comments=Vari-Plume Laboratory Exhaust Mixed-Flow High Pressure Inline Belt Drive With 1X2 Mixing Box With Weather Hoods On Sides; UNIT_HEIGHT=33"; UNIT_HEIGHT*.75=24 3/4"; UNIT_OD=23 1/2"; UNIT_RAD+((A/2)+.25")=28"; UNIT_RAD+((A/2)+.25")+4"=32"; UNIT_RADIUS=11 3/4"; UNIT_RADIUS*.6=10 9/16"; UNIT_RADIUS+4"=15 3/4"
- 165_QMXHPVP-12L-1X2_Mixing_Box_Ends: (A/2)+.25"=16 1/4"; (A/2)+.5"=-16 1/2"; (A/2)-.5"=-15 1/2"; (A/2)-2"=14"; (NOZZLE_HEIGHT-(NOZZLE_HEIGHT/8*2))/2=12"; (NOZZLE_WB_OD-NOZZLE_TOP_OD)/2=2 1/8"; -A=-32"; A=32"; A+.5=32 1/2"; A/2=16"; B=89"; B/2=44 1/2"; C=44"; C/2=22"; DUAL_F=72"; DUAL_F+1"=73"; DUAL_G=71 5/16"; E=31 1/8"; GA=3/32"; LONG_RO=65 1/16"; LONG_RO/2=32 17/32"; MB_A=41"; MB_HT=36 15/16"; MB_HT+.25"=37 3/16"; MB_HT-2.75"=34 3/16"; MB_HT/2=18 15/32"; Model=QMXHPVP-1X2_Mixing Box_Sides; NOZZLE_BOTTOM_ID=17 1/16"; NOZZLE_BOTTOM_RAD=8 17/32"; NOZZLE_HEIGHT=32"; NOZZLE_HEIGHT/7*2=8"; NOZZLE_SIZE=144"; NOZZLE_TOP_OD=19 1/2"; NOZZLE_TOP_RAD=9 3/4"; NOZZLE_WB/4=5 19/32"; NOZZLE_WB_OD=28"; NOZZLE_WB_RAD=14"; NOZZLE_WB_RAD-2"=12"; RO=24 15/16"; RO/2=12 15/32"; RO2/2=12 15/32"; TRANSITION_TOP=53 1/4"; TYPE=12"; Type Comments=Vari-Plume Laboratory Exhaust Mixed-Flow High Pressure Inline Belt Drive With 1X2 Mixing Box With Weather Hoods On Sides; UNIT_HEIGHT=33"; UNIT_HEIGHT*.75=24 3/4"; UNIT_OD=23 1/2"; UNIT_RAD+((A/2)+.25")=28"; UNIT_RAD+((A/2)+.25")+4"=32"; UNIT_RADIUS=11 3/4"; UNIT_RADIUS*.6=10 9/16"; UNIT_RADIUS+4"=15 3/4"
- 165_QMXHPVP-15H-1X2_Mixing_Box_Ends: (A/2)+.25"=16 1/4"; (A/2)+.5"=-16 1/2"; (A/2)-.5"=-15 1/2"; (A/2)-2"=14"; (NOZZLE_HEIGHT-(NOZZLE_HEIGHT/8*2))/2=16 1/8"; (NOZZLE_WB_OD-NOZZLE_TOP_OD)/2=3 1/4"; -A=-32"; A=32"; A+.5=32 1/2"; A/2=16"; B=89"; B/2=44 1/2"; C=44"; C/2=22"; DUAL_F=72"; DUAL_F+1"=73"; DUAL_G=71 5/16"; E=31 1/8"; GA=3/32"; LONG_RO=65 1/16"; LONG_RO/2=32 17/32"; MB_A=41"; MB_HT=36 15/16"; MB_HT+.25"=37 3/16"; MB_HT-2.75"=34 3/16"; MB_HT/2=18 15/32"; Model=QMXHPVP-1X2_Mixing Box_Sides; NOZZLE_BOTTOM_ID=21 3/8"; NOZZLE_BOTTOM_RAD=10 11/16"; NOZZLE_HEIGHT=43"; NOZZLE_HEIGHT/7*2=10 3/4"; NOZZLE_SIZE=180"; NOZZLE_TOP_OD=23"; NOZZLE_TOP_RAD=11 1/2"; NOZZLE_WB/4=7 3/16"; NOZZLE_WB_OD=36"; NOZZLE_WB_RAD=18"; NOZZLE_WB_RAD-2"=16"; RO=24 15/16"; RO/2=12 15/32"; RO2/2=12 15/32"; TRANSITION_TOP=45 5/16"; TYPE=12"; Type Comments=Vari-Plume Laboratory Exhaust Mixed-Flow High Pressure Inline Belt Drive With 1X2 Mixing Box With Weather Hoods On Sides; UNIT_HEIGHT=33"; UNIT_HEIGHT*.75=24 3/4"; UNIT_OD=23 1/2"; UNIT_RAD+((A/2)+.25")=28"; UNIT_RAD+((A/2)+.25")+4"=32"; UNIT_RADIUS=11 3/4"; UNIT_RADIUS*.6=10 9/16"; UNIT_RADIUS+4"=15 3/4"
- 165_QMXHPVP-15L-1X2_Mixing_Box_Ends: (A/2)+.25"=16 1/4"; (A/2)+.5"=-16 1/2"; (A/2)-.5"=-15 1/2"; (A/2)-2"=14"; (NOZZLE_HEIGHT-(NOZZLE_HEIGHT/8*2))/2=16 1/8"; (NOZZLE_WB_OD-NOZZLE_TOP_OD)/2=3 1/4"; -A=-32"; A=32"; A+.5=32 1/2"; A/2=16"; B=89"; B/2=44 1/2"; C=44"; C/2=22"; DUAL_F=72"; DUAL_F+1"=73"; DUAL_G=71 5/16"; E=31 1/8"; GA=3/32"; LONG_RO=65 1/16"; LONG_RO/2=32 17/32"; MB_A=41"; MB_HT=36 15/16"; MB_HT+.25"=37 3/16"; MB_HT-2.75"=34 3/16"; MB_HT/2=18 15/32"; Model=QMXHPVP-1X2_Mixing Box_Sides; NOZZLE_BOTTOM_ID=21 3/8"; NOZZLE_BOTTOM_RAD=10 11/16"; NOZZLE_HEIGHT=43"; NOZZLE_HEIGHT/7*2=10 3/4"; NOZZLE_SIZE=180"; NOZZLE_TOP_OD=23"; NOZZLE_TOP_RAD=11 1/2"; NOZZLE_WB/4=7 3/16"; NOZZLE_WB_OD=36"; NOZZLE_WB_RAD=18"; NOZZLE_WB_RAD-2"=16"; RO=24 15/16"; RO/2=12 15/32"; RO2/2=12 15/32"; TRANSITION_TOP=45 5/16"; TYPE=12"; Type Comments=Vari-Plume Laboratory Exhaust Mixed-Flow High Pressure Inline Belt Drive With 1X2 Mixing Box With Weather Hoods On Sides; UNIT_HEIGHT=33"; UNIT_HEIGHT*.75=24 3/4"; UNIT_OD=23 1/2"; UNIT_RAD+((A/2)+.25")=28"; UNIT_RAD+((A/2)+.25")+4"=32"; UNIT_RADIUS=11 3/4"; UNIT_RADIUS*.6=10 9/16"; UNIT_RADIUS+4"=15 3/4"
- 165_QMXHPVP-9H-1X2_Mixing_Box_Ends: (A/2)+.25"=16 1/4"; (A/2)+.5"=-16 1/2"; (A/2)-.5"=-15 1/2"; (A/2)-2"=14"; (NOZZLE_HEIGHT-(NOZZLE_HEIGHT/8*2))/2=10 1/2"; (NOZZLE_WB_OD-NOZZLE_TOP_OD)/2=2 3/8"; -A=-32"; A=32"; A+.5=32 1/2"; A/2=16"; B=89"; B/2=44 1/2"; C=44"; C/2=22"; DUAL_F=72"; DUAL_F+1"=73"; DUAL_G=71 5/16"; E=31 1/8"; GA=3/32"; LONG_RO=65 1/16"; LONG_RO/2=32 17/32"; MB_A=41"; MB_HT=36 15/16"; MB_HT+.25"=37 3/16"; MB_HT-2.75"=34 3/16"; MB_HT/2=18 15/32"; Model=QMXHPVP-1X2_Mixing Box_Sides; NOZZLE_BOTTOM_ID=12 13/16"; NOZZLE_BOTTOM_RAD=6 13/32"; NOZZLE_HEIGHT=28"; NOZZLE_HEIGHT/7*2=7"; NOZZLE_SIZE=108"; NOZZLE_TOP_OD=13 1/2"; NOZZLE_TOP_RAD=6 3/4"; NOZZLE_WB/4=4 19/32"; NOZZLE_WB_OD=23"; NOZZLE_WB_RAD=11 1/2"; NOZZLE_WB_RAD-2"=9 1/2"; RO=24 15/16"; RO/2=12 15/32"; RO2/2=12 15/32"; TRANSITION_TOP=61 1/4"; TYPE=12"; Type Comments=Vari-Plume Laboratory Exhaust Mixed-Flow High Pressure Inline Belt Drive With 1X2 Mixing Box With Weather Hoods On Sides; UNIT_HEIGHT=33"; UNIT_HEIGHT*.75=24 3/4"; UNIT_OD=23 1/2"; UNIT_RAD+((A/2)+.25")=28"; UNIT_RAD+((A/2)+.25")+4"=32"; UNIT_RADIUS=11 3/4"; UNIT_RADIUS*.6=10 9/16"; UNIT_RADIUS+4"=15 3/4"
- 165_QMXHPVP-9L-1X2_Mixing_Box_Ends: (A/2)+.25"=16 1/4"; (A/2)+.5"=-16 1/2"; (A/2)-.5"=-15 1/2"; (A/2)-2"=14"; (NOZZLE_HEIGHT-(NOZZLE_HEIGHT/8*2))/2=10 1/2"; (NOZZLE_WB_OD-NOZZLE_TOP_OD)/2=2 3/8"; -A=-32"; A=32"; A+.5=32 1/2"; A/2=16"; B=89"; B/2=44 1/2"; C=44"; C/2=22"; DUAL_F=72"; DUAL_F+1"=73"; DUAL_G=71 5/16"; E=31 1/8"; GA=3/32"; LONG_RO=65 1/16"; LONG_RO/2=32 17/32"; MB_A=41"; MB_HT=36 15/16"; MB_HT+.25"=37 3/16"; MB_HT-2.75"=34 3/16"; MB_HT/2=18 15/32"; Model=QMXHPVP-1X2_Mixing Box_Sides; NOZZLE_BOTTOM_ID=12 13/16"; NOZZLE_BOTTOM_RAD=6 13/32"; NOZZLE_HEIGHT=28"; NOZZLE_HEIGHT/7*2=7"; NOZZLE_SIZE=108"; NOZZLE_TOP_OD=13 1/2"; NOZZLE_TOP_RAD=6 3/4"; NOZZLE_WB/4=4 19/32"; NOZZLE_WB_OD=23"; NOZZLE_WB_RAD=11 1/2"; NOZZLE_WB_RAD-2"=9 1/2"; RO=24 15/16"; RO/2=12 15/32"; RO2/2=12 15/32"; TRANSITION_TOP=61 1/4"; TYPE=12"; Type Comments=Vari-Plume Laboratory Exhaust Mixed-Flow High Pressure Inline Belt Drive With 1X2 Mixing Box With Weather Hoods On Sides; UNIT_HEIGHT=33"; UNIT_HEIGHT*.75=24 3/4"; UNIT_OD=23 1/2"; UNIT_RAD+((A/2)+.25")=28"; UNIT_RAD+((A/2)+.25")+4"=32"; UNIT_RADIUS=11 3/4"; UNIT_RADIUS*.6=10 9/16"; UNIT_RADIUS+4"=15 3/4"
- 180_QMXHPVP-12H-1X2_Mixing_Box_Ends: (A/2)+.25"=17 1/4"; (A/2)+.5"=-17 1/2"; (A/2)-.5"=-16 1/2"; (A/2)-2"=15"; (NOZZLE_HEIGHT-(NOZZLE_HEIGHT/8*2))/2=12"; (NOZZLE_WB_OD-NOZZLE_TOP_OD)/2=2 1/8"; -A=-34"; A=34"; A+.5=34 1/2"; A/2=17"; B=98"; B/2=49"; C=46"; C/2=23"; DUAL_F=84"; DUAL_F+1"=85"; DUAL_G=83 5/16"; E=33 1/8"; GA=3/32"; LONG_RO=77 1/16"; LONG_RO/2=38 17/32"; MB_A=44"; MB_HT=37 11/16"; MB_HT+.25"=37 15/16"; MB_HT-2.75"=34 15/16"; MB_HT/2=18 27/32"; Model=QMXHPVP-1X2_Mixing Box_Sides; NOZZLE_BOTTOM_ID=17 1/16"; NOZZLE_BOTTOM_RAD=8 17/32"; NOZZLE_HEIGHT=32"; NOZZLE_HEIGHT/7*2=8"; NOZZLE_SIZE=144"; NOZZLE_TOP_OD=19 1/2"; NOZZLE_TOP_RAD=9 3/4"; NOZZLE_WB/4=5 19/32"; NOZZLE_WB_OD=28"; NOZZLE_WB_RAD=14"; NOZZLE_WB_RAD-2"=12"; RO=26 15/16"; RO/2=13 15/32"; RO2/2=13 15/32"; TRANSITION_TOP=59 1/16"; TYPE=12"; Type Comments=Vari-Plume Laboratory Exhaust Mixed-Flow High Pressure Inline Belt Drive With 1X2 Mixing Box With Weather Hoods On Sides; UNIT_HEIGHT=35"; UNIT_HEIGHT*.75=26 1/4"; UNIT_OD=25 5/8"; UNIT_RAD+((A/2)+.25")=30 1/16"; UNIT_RAD+((A/2)+.25")+4"=34 1/16"; UNIT_RADIUS=12 13/16"; UNIT_RADIUS*.6=11 17/32"; UNIT_RADIUS+4"=16 13/16"
- 180_QMXHPVP-12L-1X2_Mixing_Box_Ends: (A/2)+.25"=17 1/4"; (A/2)+.5"=-17 1/2"; (A/2)-.5"=-16 1/2"; (A/2)-2"=15"; (NOZZLE_HEIGHT-(NOZZLE_HEIGHT/8*2))/2=12"; (NOZZLE_WB_OD-NOZZLE_TOP_OD)/2=2 1/8"; -A=-34"; A=34"; A+.5=34 1/2"; A/2=17"; B=98"; B/2=49"; C=46"; C/2=23"; DUAL_F=84"; DUAL_F+1"=85"; DUAL_G=83 5/16"; E=33 1/8"; GA=3/32"; LONG_RO=77 1/16"; LONG_RO/2=38 17/32"; MB_A=44"; MB_HT=37 11/16"; MB_HT+.25"=37 15/16"; MB_HT-2.75"=34 15/16"; MB_HT/2=18 27/32"; Model=QMXHPVP-1X2_Mixing Box_Sides; NOZZLE_BOTTOM_ID=17 1/16"; NOZZLE_BOTTOM_RAD=8 17/32"; NOZZLE_HEIGHT=32"; NOZZLE_HEIGHT/7*2=8"; NOZZLE_SIZE=144"; NOZZLE_TOP_OD=19 1/2"; NOZZLE_TOP_RAD=9 3/4"; NOZZLE_WB/4=5 19/32"; NOZZLE_WB_OD=28"; NOZZLE_WB_RAD=14"; NOZZLE_WB_RAD-2"=12"; RO=26 15/16"; RO/2=13 15/32"; RO2/2=13 15/32"; TRANSITION_TOP=59 1/16"; TYPE=12"; Type Comments=Vari-Plume Laboratory Exhaust Mixed-Flow High Pressure Inline Belt Drive With 1X2 Mixing Box With Weather Hoods On Sides; UNIT_HEIGHT=35"; UNIT_HEIGHT*.75=26 1/4"; UNIT_OD=25 5/8"; UNIT_RAD+((A/2)+.25")=30 1/16"; UNIT_RAD+((A/2)+.25")+4"=34 1/16"; UNIT_RADIUS=12 13/16"; UNIT_RADIUS*.6=11 17/32"; UNIT_RADIUS+4"=16 13/16"
- 180_QMXHPVP-15H-1X2_Mixing_Box_Ends: (A/2)+.25"=17 1/4"; (A/2)+.5"=-17 1/2"; (A/2)-.5"=-16 1/2"; (A/2)-2"=15"; (NOZZLE_HEIGHT-(NOZZLE_HEIGHT/8*2))/2=16 1/8"; (NOZZLE_WB_OD-NOZZLE_TOP_OD)/2=3 1/4"; -A=-34"; A=34"; A+.5=34 1/2"; A/2=17"; B=98"; B/2=49"; C=46"; C/2=23"; DUAL_F=84"; DUAL_F+1"=85"; DUAL_G=83 5/16"; E=33 1/8"; GA=3/32"; LONG_RO=77 1/16"; LONG_RO/2=38 17/32"; MB_A=44"; MB_HT=37 11/16"; MB_HT+.25"=37 15/16"; MB_HT-2.75"=34 15/16"; MB_HT/2=18 27/32"; Model=QMXHPVP-1X2_Mixing Box_Sides; NOZZLE_BOTTOM_ID=21 3/8"; NOZZLE_BOTTOM_RAD=10 11/16"; NOZZLE_HEIGHT=43"; NOZZLE_HEIGHT/7*2=10 3/4"; NOZZLE_SIZE=180"; NOZZLE_TOP_OD=23"; NOZZLE_TOP_RAD=11 1/2"; NOZZLE_WB/4=7 3/16"; NOZZLE_WB_OD=36"; NOZZLE_WB_RAD=18"; NOZZLE_WB_RAD-2"=16"; RO=26 15/16"; RO/2=13 15/32"; RO2/2=13 15/32"; TRANSITION_TOP=51 1/8"; TYPE=12"; Type Comments=Vari-Plume Laboratory Exhaust Mixed-Flow High Pressure Inline Belt Drive With 1X2 Mixing Box With Weather Hoods On Sides; UNIT_HEIGHT=35"; UNIT_HEIGHT*.75=26 1/4"; UNIT_OD=25 5/8"; UNIT_RAD+((A/2)+.25")=30 1/16"; UNIT_RAD+((A/2)+.25")+4"=34 1/16"; UNIT_RADIUS=12 13/16"; UNIT_RADIUS*.6=11 17/32"; UNIT_RADIUS+4"=16 13/16"
- 180_QMXHPVP-15L-1X2_Mixing_Box_Ends: (A/2)+.25"=17 1/4"; (A/2)+.5"=-17 1/2"; (A/2)-.5"=-16 1/2"; (A/2)-2"=15"; (NOZZLE_HEIGHT-(NOZZLE_HEIGHT/8*2))/2=16 1/8"; (NOZZLE_WB_OD-NOZZLE_TOP_OD)/2=3 1/4"; -A=-34"; A=34"; A+.5=34 1/2"; A/2=17"; B=98"; B/2=49"; C=46"; C/2=23"; DUAL_F=84"; DUAL_F+1"=85"; DUAL_G=83 5/16"; E=33 1/8"; GA=3/32"; LONG_RO=77 1/16"; LONG_RO/2=38 17/32"; MB_A=44"; MB_HT=37 11/16"; MB_HT+.25"=37 15/16"; MB_HT-2.75"=34 15/16"; MB_HT/2=18 27/32"; Model=QMXHPVP-1X2_Mixing Box_Sides; NOZZLE_BOTTOM_ID=21 3/8"; NOZZLE_BOTTOM_RAD=10 11/16"; NOZZLE_HEIGHT=43"; NOZZLE_HEIGHT/7*2=10 3/4"; NOZZLE_SIZE=180"; NOZZLE_TOP_OD=23"; NOZZLE_TOP_RAD=11 1/2"; NOZZLE_WB/4=7 3/16"; NOZZLE_WB_OD=36"; NOZZLE_WB_RAD=18"; NOZZLE_WB_RAD-2"=16"; RO=26 15/16"; RO/2=13 15/32"; RO2/2=13 15/32"; TRANSITION_TOP=51 1/8"; TYPE=12"; Type Comments=Vari-Plume Laboratory Exhaust Mixed-Flow High Pressure Inline Belt Drive With 1X2 Mixing Box With Weather Hoods On Sides; UNIT_HEIGHT=35"; UNIT_HEIGHT*.75=26 1/4"; UNIT_OD=25 5/8"; UNIT_RAD+((A/2)+.25")=30 1/16"; UNIT_RAD+((A/2)+.25")+4"=34 1/16"; UNIT_RADIUS=12 13/16"; UNIT_RADIUS*.6=11 17/32"; UNIT_RADIUS+4"=16 13/16"
- 180_QMXHPVP-18H-1X2_Mixing_Box_Ends: (A/2)+.25"=17 1/4"; (A/2)+.5"=-17 1/2"; (A/2)-.5"=-16 1/2"; (A/2)-2"=15"; (NOZZLE_HEIGHT-(NOZZLE_HEIGHT/8*2))/2=18"; (NOZZLE_WB_OD-NOZZLE_TOP_OD)/2=3 7/8"; -A=-34"; A=34"; A+.5=34 1/2"; A/2=17"; B=98"; B/2=49"; C=46"; C/2=23"; DUAL_F=84"; DUAL_F+1"=85"; DUAL_G=83 5/16"; E=33 1/8"; GA=3/32"; LONG_RO=77 1/16"; LONG_RO/2=38 17/32"; MB_A=44"; MB_HT=37 11/16"; MB_HT+.25"=37 15/16"; MB_HT-2.75"=34 15/16"; MB_HT/2=18 27/32"; Model=QMXHPVP-1X2_Mixing Box_Sides; NOZZLE_BOTTOM_ID=25 5/8"; NOZZLE_BOTTOM_RAD=12 13/16"; NOZZLE_HEIGHT=48"; NOZZLE_HEIGHT/7*2=12"; NOZZLE_SIZE=216"; NOZZLE_TOP_OD=27 1/2"; NOZZLE_TOP_RAD=13 3/4"; NOZZLE_WB/4=8 19/32"; NOZZLE_WB_OD=43"; NOZZLE_WB_RAD=21 1/2"; NOZZLE_WB_RAD-2"=19 1/2"; RO=26 15/16"; RO/2=13 15/32"; RO2/2=13 15/32"; TRANSITION_TOP=48 1/2"; TYPE=12"; Type Comments=Vari-Plume Laboratory Exhaust Mixed-Flow High Pressure Inline Belt Drive With 1X2 Mixing Box With Weather Hoods On Sides; UNIT_HEIGHT=35"; UNIT_HEIGHT*.75=26 1/4"; UNIT_OD=25 5/8"; UNIT_RAD+((A/2)+.25")=30 1/16"; UNIT_RAD+((A/2)+.25")+4"=34 1/16"; UNIT_RADIUS=12 13/16"; UNIT_RADIUS*.6=11 17/32"; UNIT_RADIUS+4"=16 13/16"
- 180_QMXHPVP-18L-1X2_Mixing_Box_Ends: (A/2)+.25"=17 1/4"; (A/2)+.5"=-17 1/2"; (A/2)-.5"=-16 1/2"; (A/2)-2"=15"; (NOZZLE_HEIGHT-(NOZZLE_HEIGHT/8*2))/2=18"; (NOZZLE_WB_OD-NOZZLE_TOP_OD)/2=3 7/8"; -A=-34"; A=34"; A+.5=34 1/2"; A/2=17"; B=98"; B/2=49"; C=46"; C/2=23"; DUAL_F=84"; DUAL_F+1"=85"; DUAL_G=83 5/16"; E=33 1/8"; GA=3/32"; LONG_RO=77 1/16"; LONG_RO/2=38 17/32"; MB_A=44"; MB_HT=37 11/16"; MB_HT+.25"=37 15/16"; MB_HT-2.75"=34 15/16"; MB_HT/2=18 27/32"; Model=QMXHPVP-1X2_Mixing Box_Sides; NOZZLE_BOTTOM_ID=25 5/8"; NOZZLE_BOTTOM_RAD=12 13/16"; NOZZLE_HEIGHT=48"; NOZZLE_HEIGHT/7*2=12"; NOZZLE_SIZE=216"; NOZZLE_TOP_OD=27 1/2"; NOZZLE_TOP_RAD=13 3/4"; NOZZLE_WB/4=8 19/32"; NOZZLE_WB_OD=43"; NOZZLE_WB_RAD=21 1/2"; NOZZLE_WB_RAD-2"=19 1/2"; RO=26 15/16"; RO/2=13 15/32"; RO2/2=13 15/32"; TRANSITION_TOP=48 1/2"; TYPE=12"; Type Comments=Vari-Plume Laboratory Exhaust Mixed-Flow High Pressure Inline Belt Drive With 1X2 Mixing Box With Weather Hoods On Sides; UNIT_HEIGHT=35"; UNIT_HEIGHT*.75=26 1/4"; UNIT_OD=25 5/8"; UNIT_RAD+((A/2)+.25")=30 1/16"; UNIT_RAD+((A/2)+.25")+4"=34 1/16"; UNIT_RADIUS=12 13/16"; UNIT_RADIUS*.6=11 17/32"; UNIT_RADIUS+4"=16 13/16"
- 202_QMXHPVP-12H-1X2_Mixing_Box_Ends: (A/2)+.25"=19 1/4"; (A/2)+.5"=-19 1/2"; (A/2)-.5"=-18 1/2"; (A/2)-2"=17"; (NOZZLE_HEIGHT-(NOZZLE_HEIGHT/8*2))/2=12"; (NOZZLE_WB_OD-NOZZLE_TOP_OD)/2=2 1/8"; -A=-38"; A=38"; A+.5=38 1/2"; A/2=19"; B=104"; B/2=52"; C=50"; C/2=25"; DUAL_F=90"; DUAL_F+1"=91"; DUAL_G=89 1/8"; E=36 15/16"; GA=3/32"; LONG_RO=82 7/8"; LONG_RO/2=41 7/16"; MB_A=49"; MB_HT=41 3/16"; MB_HT+.25"=41 7/16"; MB_HT-2.75"=38 7/16"; MB_HT/2=20 19/32"; Model=QMXHPVP-1X2_Mixing Box_Sides; NOZZLE_BOTTOM_ID=17 1/16"; NOZZLE_BOTTOM_RAD=8 17/32"; NOZZLE_HEIGHT=32"; NOZZLE_HEIGHT/7*2=8"; NOZZLE_SIZE=144"; NOZZLE_TOP_OD=19 1/2"; NOZZLE_TOP_RAD=9 3/4"; NOZZLE_WB/4=5 19/32"; NOZZLE_WB_OD=28"; NOZZLE_WB_RAD=14"; NOZZLE_WB_RAD-2"=12"; RO=30 3/4"; RO/2=15 3/8"; RO2/2=15 3/8"; TRANSITION_TOP=67 9/16"; TYPE=12"; Type Comments=Vari-Plume Laboratory Exhaust Mixed-Flow High Pressure Inline Belt Drive With 1X2 Mixing Box With Weather Hoods On Sides; UNIT_HEIGHT=37 1/2"; UNIT_HEIGHT*.75=28 1/8"; UNIT_OD=28 3/4"; UNIT_RAD+((A/2)+.25")=33 5/8"; UNIT_RAD+((A/2)+.25")+4"=37 5/8"; UNIT_RADIUS=14 3/8"; UNIT_RADIUS*.6=12 15/16"; UNIT_RADIUS+4"=18 3/8"
- 202_QMXHPVP-12L-1X2_Mixing_Box_Ends: (A/2)+.25"=19 1/4"; (A/2)+.5"=-19 1/2"; (A/2)-.5"=-18 1/2"; (A/2)-2"=17"; (NOZZLE_HEIGHT-(NOZZLE_HEIGHT/8*2))/2=12"; (NOZZLE_WB_OD-NOZZLE_TOP_OD)/2=2 1/8"; -A=-38"; A=38"; A+.5=38 1/2"; A/2=19"; B=104"; B/2=52"; C=50"; C/2=25"; DUAL_F=90"; DUAL_F+1"=91"; DUAL_G=89 1/8"; E=36 15/16"; GA=3/32"; LONG_RO=82 7/8"; LONG_RO/2=41 7/16"; MB_A=49"; MB_HT=41 3/16"; MB_HT+.25"=41 7/16"; MB_HT-2.75"=38 7/16"; MB_HT/2=20 19/32"; Model=QMXHPVP-1X2_Mixing Box_Sides; NOZZLE_BOTTOM_ID=17 1/16"; NOZZLE_BOTTOM_RAD=8 17/32"; NOZZLE_HEIGHT=32"; NOZZLE_HEIGHT/7*2=8"; NOZZLE_SIZE=144"; NOZZLE_TOP_OD=19 1/2"; NOZZLE_TOP_RAD=9 3/4"; NOZZLE_WB/4=5 19/32"; NOZZLE_WB_OD=28"; NOZZLE_WB_RAD=14"; NOZZLE_WB_RAD-2"=12"; RO=30 3/4"; RO/2=15 3/8"; RO2/2=15 3/8"; TRANSITION_TOP=67 9/16"; TYPE=12"; Type Comments=Vari-Plume Laboratory Exhaust Mixed-Flow High Pressure Inline Belt Drive With 1X2 Mixing Box With Weather Hoods On Sides; UNIT_HEIGHT=37 1/2"; UNIT_HEIGHT*.75=28 1/8"; UNIT_OD=28 3/4"; UNIT_RAD+((A/2)+.25")=33 5/8"; UNIT_RAD+((A/2)+.25")+4"=37 5/8"; UNIT_RADIUS=14 3/8"; UNIT_RADIUS*.6=12 15/16"; UNIT_RADIUS+4"=18 3/8"
- 202_QMXHPVP-15H-1X2_Mixing_Box_Ends: (A/2)+.25"=19 1/4"; (A/2)+.5"=-19 1/2"; (A/2)-.5"=-18 1/2"; (A/2)-2"=17"; (NOZZLE_HEIGHT-(NOZZLE_HEIGHT/8*2))/2=16 1/8"; (NOZZLE_WB_OD-NOZZLE_TOP_OD)/2=3 1/4"; -A=-38"; A=38"; A+.5=38 1/2"; A/2=19"; B=104"; B/2=52"; C=50"; C/2=25"; DUAL_F=90"; DUAL_F+1"=91"; DUAL_G=89 1/8"; E=36 15/16"; GA=3/32"; LONG_RO=82 7/8"; LONG_RO/2=41 7/16"; MB_A=49"; MB_HT=41 3/16"; MB_HT+.25"=41 7/16"; MB_HT-2.75"=38 7/16"; MB_HT/2=20 19/32"; Model=QMXHPVP-1X2_Mixing Box_Sides; NOZZLE_BOTTOM_ID=21 3/8"; NOZZLE_BOTTOM_RAD=10 11/16"; NOZZLE_HEIGHT=43"; NOZZLE_HEIGHT/7*2=10 3/4"; NOZZLE_SIZE=180"; NOZZLE_TOP_OD=23"; NOZZLE_TOP_RAD=11 1/2"; NOZZLE_WB/4=7 3/16"; NOZZLE_WB_OD=36"; NOZZLE_WB_RAD=18"; NOZZLE_WB_RAD-2"=16"; RO=30 3/4"; RO/2=15 3/8"; RO2/2=15 3/8"; TRANSITION_TOP=59 5/8"; TYPE=12"; Type Comments=Vari-Plume Laboratory Exhaust Mixed-Flow High Pressure Inline Belt Drive With 1X2 Mixing Box With Weather Hoods On Sides; UNIT_HEIGHT=37 1/2"; UNIT_HEIGHT*.75=28 1/8"; UNIT_OD=28 3/4"; UNIT_RAD+((A/2)+.25")=33 5/8"; UNIT_RAD+((A/2)+.25")+4"=37 5/8"; UNIT_RADIUS=14 3/8"; UNIT_RADIUS*.6=12 15/16"; UNIT_RADIUS+4"=18 3/8"
- 202_QMXHPVP-15L-1X2_Mixing_Box_Ends: (A/2)+.25"=19 1/4"; (A/2)+.5"=-19 1/2"; (A/2)-.5"=-18 1/2"; (A/2)-2"=17"; (NOZZLE_HEIGHT-(NOZZLE_HEIGHT/8*2))/2=16 1/8"; (NOZZLE_WB_OD-NOZZLE_TOP_OD)/2=3 1/4"; -A=-38"; A=38"; A+.5=38 1/2"; A/2=19"; B=104"; B/2=52"; C=50"; C/2=25"; DUAL_F=90"; DUAL_F+1"=91"; DUAL_G=89 1/8"; E=36 15/16"; GA=3/32"; LONG_RO=82 7/8"; LONG_RO/2=41 7/16"; MB_A=49"; MB_HT=41 3/16"; MB_HT+.25"=41 7/16"; MB_HT-2.75"=38 7/16"; MB_HT/2=20 19/32"; Model=QMXHPVP-1X2_Mixing Box_Sides; NOZZLE_BOTTOM_ID=21 3/8"; NOZZLE_BOTTOM_RAD=10 11/16"; NOZZLE_HEIGHT=43"; NOZZLE_HEIGHT/7*2=10 3/4"; NOZZLE_SIZE=180"; NOZZLE_TOP_OD=23"; NOZZLE_TOP_RAD=11 1/2"; NOZZLE_WB/4=7 3/16"; NOZZLE_WB_OD=36"; NOZZLE_WB_RAD=18"; NOZZLE_WB_RAD-2"=16"; RO=30 3/4"; RO/2=15 3/8"; RO2/2=15 3/8"; TRANSITION_TOP=59 5/8"; TYPE=12"; Type Comments=Vari-Plume Laboratory Exhaust Mixed-Flow High Pressure Inline Belt Drive With 1X2 Mixing Box With Weather Hoods On Sides; UNIT_HEIGHT=37 1/2"; UNIT_HEIGHT*.75=28 1/8"; UNIT_OD=28 3/4"; UNIT_RAD+((A/2)+.25")=33 5/8"; UNIT_RAD+((A/2)+.25")+4"=37 5/8"; UNIT_RADIUS=14 3/8"; UNIT_RADIUS*.6=12 15/16"; UNIT_RADIUS+4"=18 3/8"
- 202_QMXHPVP-18H-1X2_Mixing_Box_Ends: (A/2)+.25"=19 1/4"; (A/2)+.5"=-19 1/2"; (A/2)-.5"=-18 1/2"; (A/2)-2"=17"; (NOZZLE_HEIGHT-(NOZZLE_HEIGHT/8*2))/2=18"; (NOZZLE_WB_OD-NOZZLE_TOP_OD)/2=3 7/8"; -A=-38"; A=38"; A+.5=38 1/2"; A/2=19"; B=104"; B/2=52"; C=50"; C/2=25"; DUAL_F=90"; DUAL_F+1"=91"; DUAL_G=89 1/8"; E=36 15/16"; GA=3/32"; LONG_RO=82 7/8"; LONG_RO/2=41 7/16"; MB_A=49"; MB_HT=41 3/16"; MB_HT+.25"=41 7/16"; MB_HT-2.75"=38 7/16"; MB_HT/2=20 19/32"; Model=QMXHPVP-1X2_Mixing Box_Sides; NOZZLE_BOTTOM_ID=25 5/8"; NOZZLE_BOTTOM_RAD=12 13/16"; NOZZLE_HEIGHT=48"; NOZZLE_HEIGHT/7*2=12"; NOZZLE_SIZE=216"; NOZZLE_TOP_OD=27 1/2"; NOZZLE_TOP_RAD=13 3/4"; NOZZLE_WB/4=8 19/32"; NOZZLE_WB_OD=43"; NOZZLE_WB_RAD=21 1/2"; NOZZLE_WB_RAD-2"=19 1/2"; RO=30 3/4"; RO/2=15 3/8"; RO2/2=15 3/8"; TRANSITION_TOP=51 5/8"; TYPE=12"; Type Comments=Vari-Plume Laboratory Exhaust Mixed-Flow High Pressure Inline Belt Drive With 1X2 Mixing Box With Weather Hoods On Sides; UNIT_HEIGHT=37 1/2"; UNIT_HEIGHT*.75=28 1/8"; UNIT_OD=28 3/4"; UNIT_RAD+((A/2)+.25")=33 5/8"; UNIT_RAD+((A/2)+.25")+4"=37 5/8"; UNIT_RADIUS=14 3/8"; UNIT_RADIUS*.6=12 15/16"; UNIT_RADIUS+4"=18 3/8"
- 202_QMXHPVP-18L-1X2_Mixing_Box_Ends: (A/2)+.25"=19 1/4"; (A/2)+.5"=-19 1/2"; (A/2)-.5"=-18 1/2"; (A/2)-2"=17"; (NOZZLE_HEIGHT-(NOZZLE_HEIGHT/8*2))/2=18"; (NOZZLE_WB_OD-NOZZLE_TOP_OD)/2=3 7/8"; -A=-38"; A=38"; A+.5=38 1/2"; A/2=19"; B=104"; B/2=52"; C=50"; C/2=25"; DUAL_F=90"; DUAL_F+1"=91"; DUAL_G=89 1/8"; E=36 15/16"; GA=3/32"; LONG_RO=82 7/8"; LONG_RO/2=41 7/16"; MB_A=49"; MB_HT=41 3/16"; MB_HT+.25"=41 7/16"; MB_HT-2.75"=38 7/16"; MB_HT/2=20 19/32"; Model=QMXHPVP-1X2_Mixing Box_Sides; NOZZLE_BOTTOM_ID=25 5/8"; NOZZLE_BOTTOM_RAD=12 13/16"; NOZZLE_HEIGHT=48"; NOZZLE_HEIGHT/7*2=12"; NOZZLE_SIZE=216"; NOZZLE_TOP_OD=27 1/2"; NOZZLE_TOP_RAD=13 3/4"; NOZZLE_WB/4=8 19/32"; NOZZLE_WB_OD=43"; NOZZLE_WB_RAD=21 1/2"; NOZZLE_WB_RAD-2"=19 1/2"; RO=30 3/4"; RO/2=15 3/8"; RO2/2=15 3/8"; TRANSITION_TOP=51 5/8"; TYPE=12"; Type Comments=Vari-Plume Laboratory Exhaust Mixed-Flow High Pressure Inline Belt Drive With 1X2 Mixing Box With Weather Hoods On Sides; UNIT_HEIGHT=37 1/2"; UNIT_HEIGHT*.75=28 1/8"; UNIT_OD=28 3/4"; UNIT_RAD+((A/2)+.25")=33 5/8"; UNIT_RAD+((A/2)+.25")+4"=37 5/8"; UNIT_RADIUS=14 3/8"; UNIT_RADIUS*.6=12 15/16"; UNIT_RADIUS+4"=18 3/8"
- 225_QMXHPVP-12H-1X2_Mixing_Box_Ends: (A/2)+.25"=21 1/4"; (A/2)+.5"=-21 1/2"; (A/2)-.5"=-20 1/2"; (A/2)-2"=19"; (NOZZLE_HEIGHT-(NOZZLE_HEIGHT/8*2))/2=12"; (NOZZLE_WB_OD-NOZZLE_TOP_OD)/2=2 1/8"; -A=-42"; A=42"; A+.5=42 1/2"; A/2=21"; B=113"; B/2=56 1/2"; C=56"; C/2=28"; DUAL_F=93"; DUAL_F+1"=94"; DUAL_G=92 1/8"; E=40 15/16"; GA=3/32"; LONG_RO=85 7/8"; LONG_RO/2=42 15/16"; MB_A=54"; MB_HT=43 3/16"; MB_HT+.25"=43 7/16"; MB_HT-2.75"=40 7/16"; MB_HT/2=21 19/32"; Model=QMXHPVP-1X2_Mixing Box_Sides; NOZZLE_BOTTOM_ID=17 1/16"; NOZZLE_BOTTOM_RAD=8 17/32"; NOZZLE_HEIGHT=32"; NOZZLE_HEIGHT/7*2=8"; NOZZLE_SIZE=144"; NOZZLE_TOP_OD=19 1/2"; NOZZLE_TOP_RAD=9 3/4"; NOZZLE_WB/4=5 19/32"; NOZZLE_WB_OD=28"; NOZZLE_WB_RAD=14"; NOZZLE_WB_RAD-2"=12"; RO=34 3/4"; RO/2=17 3/8"; RO2/2=17 3/8"; TRANSITION_TOP=77 1/16"; TYPE=12"; Type Comments=Vari-Plume Laboratory Exhaust Mixed-Flow High Pressure Inline Belt Drive With 1X2 Mixing Box With Weather Hoods On Sides; UNIT_HEIGHT=41"; UNIT_HEIGHT*.75=30 3/4"; UNIT_OD=31 15/16"; UNIT_RAD+((A/2)+.25")=37 7/32"; UNIT_RAD+((A/2)+.25")+4"=41 7/32"; UNIT_RADIUS=15 31/32"; UNIT_RADIUS*.6=14 3/8"; UNIT_RADIUS+4"=19 31/32"
- 225_QMXHPVP-12L-1X2_Mixing_Box_Ends: (A/2)+.25"=21 1/4"; (A/2)+.5"=-21 1/2"; (A/2)-.5"=-20 1/2"; (A/2)-2"=19"; (NOZZLE_HEIGHT-(NOZZLE_HEIGHT/8*2))/2=12"; (NOZZLE_WB_OD-NOZZLE_TOP_OD)/2=2 1/8"; -A=-42"; A=42"; A+.5=42 1/2"; A/2=21"; B=113"; B/2=56 1/2"; C=56"; C/2=28"; DUAL_F=93"; DUAL_F+1"=94"; DUAL_G=92 1/8"; E=40 15/16"; GA=3/32"; LONG_RO=85 7/8"; LONG_RO/2=42 15/16"; MB_A=54"; MB_HT=43 3/16"; MB_HT+.25"=43 7/16"; MB_HT-2.75"=40 7/16"; MB_HT/2=21 19/32"; Model=QMXHPVP-1X2_Mixing Box_Sides; NOZZLE_BOTTOM_ID=17 1/16"; NOZZLE_BOTTOM_RAD=8 17/32"; NOZZLE_HEIGHT=32"; NOZZLE_HEIGHT/7*2=8"; NOZZLE_SIZE=144"; NOZZLE_TOP_OD=19 1/2"; NOZZLE_TOP_RAD=9 3/4"; NOZZLE_WB/4=5 19/32"; NOZZLE_WB_OD=28"; NOZZLE_WB_RAD=14"; NOZZLE_WB_RAD-2"=12"; RO=34 3/4"; RO/2=17 3/8"; RO2/2=17 3/8"; TRANSITION_TOP=77 1/16"; TYPE=12"; Type Comments=Vari-Plume Laboratory Exhaust Mixed-Flow High Pressure Inline Belt Drive With 1X2 Mixing Box With Weather Hoods On Sides; UNIT_HEIGHT=41"; UNIT_HEIGHT*.75=30 3/4"; UNIT_OD=31 15/16"; UNIT_RAD+((A/2)+.25")=37 7/32"; UNIT_RAD+((A/2)+.25")+4"=41 7/32"; UNIT_RADIUS=15 31/32"; UNIT_RADIUS*.6=14 3/8"; UNIT_RADIUS+4"=19 31/32"
- 225_QMXHPVP-15H-1X2_Mixing_Box_Ends: (A/2)+.25"=21 1/4"; (A/2)+.5"=-21 1/2"; (A/2)-.5"=-20 1/2"; (A/2)-2"=19"; (NOZZLE_HEIGHT-(NOZZLE_HEIGHT/8*2))/2=16 1/8"; (NOZZLE_WB_OD-NOZZLE_TOP_OD)/2=3 1/4"; -A=-42"; A=42"; A+.5=42 1/2"; A/2=21"; B=113"; B/2=56 1/2"; C=56"; C/2=28"; DUAL_F=93"; DUAL_F+1"=94"; DUAL_G=92 1/8"; E=40 15/16"; GA=3/32"; LONG_RO=85 7/8"; LONG_RO/2=42 15/16"; MB_A=54"; MB_HT=43 3/16"; MB_HT+.25"=43 7/16"; MB_HT-2.75"=40 7/16"; MB_HT/2=21 19/32"; Model=QMXHPVP-1X2_Mixing Box_Sides; NOZZLE_BOTTOM_ID=21 3/8"; NOZZLE_BOTTOM_RAD=10 11/16"; NOZZLE_HEIGHT=43"; NOZZLE_HEIGHT/7*2=10 3/4"; NOZZLE_SIZE=180"; NOZZLE_TOP_OD=23"; NOZZLE_TOP_RAD=11 1/2"; NOZZLE_WB/4=7 3/16"; NOZZLE_WB_OD=36"; NOZZLE_WB_RAD=18"; NOZZLE_WB_RAD-2"=16"; RO=34 3/4"; RO/2=17 3/8"; RO2/2=17 3/8"; TRANSITION_TOP=69 1/8"; TYPE=12"; Type Comments=Vari-Plume Laboratory Exhaust Mixed-Flow High Pressure Inline Belt Drive With 1X2 Mixing Box With Weather Hoods On Sides; UNIT_HEIGHT=41"; UNIT_HEIGHT*.75=30 3/4"; UNIT_OD=31 15/16"; UNIT_RAD+((A/2)+.25")=37 7/32"; UNIT_RAD+((A/2)+.25")+4"=41 7/32"; UNIT_RADIUS=15 31/32"; UNIT_RADIUS*.6=14 3/8"; UNIT_RADIUS+4"=19 31/32"
- 225_QMXHPVP-15L-1X2_Mixing_Box_Ends: (A/2)+.25"=21 1/4"; (A/2)+.5"=-21 1/2"; (A/2)-.5"=-20 1/2"; (A/2)-2"=19"; (NOZZLE_HEIGHT-(NOZZLE_HEIGHT/8*2))/2=16 1/8"; (NOZZLE_WB_OD-NOZZLE_TOP_OD)/2=3 1/4"; -A=-42"; A=42"; A+.5=42 1/2"; A/2=21"; B=113"; B/2=56 1/2"; C=56"; C/2=28"; DUAL_F=93"; DUAL_F+1"=94"; DUAL_G=92 1/8"; E=40 15/16"; GA=3/32"; LONG_RO=85 7/8"; LONG_RO/2=42 15/16"; MB_A=54"; MB_HT=43 3/16"; MB_HT+.25"=43 7/16"; MB_HT-2.75"=40 7/16"; MB_HT/2=21 19/32"; Model=QMXHPVP-1X2_Mixing Box_Sides; NOZZLE_BOTTOM_ID=21 3/8"; NOZZLE_BOTTOM_RAD=10 11/16"; NOZZLE_HEIGHT=43"; NOZZLE_HEIGHT/7*2=10 3/4"; NOZZLE_SIZE=180"; NOZZLE_TOP_OD=23"; NOZZLE_TOP_RAD=11 1/2"; NOZZLE_WB/4=7 3/16"; NOZZLE_WB_OD=36"; NOZZLE_WB_RAD=18"; NOZZLE_WB_RAD-2"=16"; RO=34 3/4"; RO/2=17 3/8"; RO2/2=17 3/8"; TRANSITION_TOP=69 1/8"; TYPE=12"; Type Comments=Vari-Plume Laboratory Exhaust Mixed-Flow High Pressure Inline Belt Drive With 1X2 Mixing Box With Weather Hoods On Sides; UNIT_HEIGHT=41"; UNIT_HEIGHT*.75=30 3/4"; UNIT_OD=31 15/16"; UNIT_RAD+((A/2)+.25")=37 7/32"; UNIT_RAD+((A/2)+.25")+4"=41 7/32"; UNIT_RADIUS=15 31/32"; UNIT_RADIUS*.6=14 3/8"; UNIT_RADIUS+4"=19 31/32"
- 225_QMXVP-18H-1X2_Mixing_Box_Ends: (A/2)+.25"=21 1/4"; (A/2)+.5"=-21 1/2"; (A/2)-.5"=-20 1/2"; (A/2)-2"=19"; (NOZZLE_HEIGHT-(NOZZLE_HEIGHT/8*2))/2=18"; (NOZZLE_WB_OD-NOZZLE_TOP_OD)/2=3 7/8"; -A=-42"; A=42"; A+.5=42 1/2"; A/2=21"; B=113"; B/2=56 1/2"; C=56"; C/2=28"; DUAL_F=93"; DUAL_F+1"=94"; DUAL_G=92 1/8"; E=40 15/16"; GA=3/32"; LONG_RO=85 7/8"; LONG_RO/2=42 15/16"; MB_A=54"; MB_HT=43 3/16"; MB_HT+.25"=43 7/16"; MB_HT-2.75"=40 7/16"; MB_HT/2=21 19/32"; Model=QMXVP-1X2_Mixing Box_Sides; NOZZLE_BOTTOM_ID=25 5/8"; NOZZLE_BOTTOM_RAD=12 13/16"; NOZZLE_HEIGHT=48"; NOZZLE_HEIGHT/7*2=12"; NOZZLE_SIZE=216"; NOZZLE_TOP_OD=27 1/2"; NOZZLE_TOP_RAD=13 3/4"; NOZZLE_WB/4=8 19/32"; NOZZLE_WB_OD=43"; NOZZLE_WB_RAD=21 1/2"; NOZZLE_WB_RAD-2"=19 1/2"; RO=34 3/4"; RO/2=17 3/8"; RO2/2=17 3/8"; TRANSITION_TOP=61 1/8"; TYPE=0"; Type Comments=Vari-Plume Laboratory Exhaust Mixed-Flow Inline Belt Drive With 1X2 Mixing Box With Weather Hoods On Sides; UNIT_HEIGHT=41"; UNIT_HEIGHT*.75=30 3/4"; UNIT_OD=31 15/16"; UNIT_RAD+((A/2)+.25")=37 7/32"; UNIT_RAD+((A/2)+.25")+4"=41 7/32"; UNIT_RADIUS=15 31/32"; UNIT_RADIUS*.6=14 3/8"; UNIT_RADIUS+4"=19 31/32"
- 225_QMXHPVP-18L-1X2_Mixing_Box_Ends: (A/2)+.25"=21 1/4"; (A/2)+.5"=-21 1/2"; (A/2)-.5"=-20 1/2"; (A/2)-2"=19"; (NOZZLE_HEIGHT-(NOZZLE_HEIGHT/8*2))/2=18"; (NOZZLE_WB_OD-NOZZLE_TOP_OD)/2=3 7/8"; -A=-42"; A=42"; A+.5=42 1/2"; A/2=21"; B=113"; B/2=56 1/2"; C=56"; C/2=28"; DUAL_F=93"; DUAL_F+1"=94"; DUAL_G=92 1/8"; E=40 15/16"; GA=3/32"; LONG_RO=85 7/8"; LONG_RO/2=42 15/16"; MB_A=54"; MB_HT=43 3/16"; MB_HT+.25"=43 7/16"; MB_HT-2.75"=40 7/16"; MB_HT/2=21 19/32"; Model=QMXHPVP-1X2_Mixing Box_Sides; NOZZLE_BOTTOM_ID=25 5/8"; NOZZLE_BOTTOM_RAD=12 13/16"; NOZZLE_HEIGHT=48"; NOZZLE_HEIGHT/7*2=12"; NOZZLE_SIZE=216"; NOZZLE_TOP_OD=27 1/2"; NOZZLE_TOP_RAD=13 3/4"; NOZZLE_WB/4=8 19/32"; NOZZLE_WB_OD=43"; NOZZLE_WB_RAD=21 1/2"; NOZZLE_WB_RAD-2"=19 1/2"; RO=34 3/4"; RO/2=17 3/8"; RO2/2=17 3/8"; TRANSITION_TOP=61 1/8"; TYPE=12"; Type Comments=Vari-Plume Laboratory Exhaust Mixed-Flow High Pressure Inline Belt Drive With 1X2 Mixing Box With Weather Hoods On Sides; UNIT_HEIGHT=41"; UNIT_HEIGHT*.75=30 3/4"; UNIT_OD=31 15/16"; UNIT_RAD+((A/2)+.25")=37 7/32"; UNIT_RAD+((A/2)+.25")+4"=41 7/32"; UNIT_RADIUS=15 31/32"; UNIT_RADIUS*.6=14 3/8"; UNIT_RADIUS+4"=19 31/32"
- 225_QMXHPVP-18H-1X2_Mixing_Box_Ends: (A/2)+.25"=21 1/4"; (A/2)+.5"=-21 1/2"; (A/2)-.5"=-20 1/2"; (A/2)-2"=19"; (NOZZLE_HEIGHT-(NOZZLE_HEIGHT/8*2))/2=18"; (NOZZLE_WB_OD-NOZZLE_TOP_OD)/2=3 7/8"; -A=-42"; A=42"; A+.5=42 1/2"; A/2=21"; B=113"; B/2=56 1/2"; C=56"; C/2=28"; DUAL_F=93"; DUAL_F+1"=94"; DUAL_G=92 1/8"; E=40 15/16"; GA=3/32"; LONG_RO=85 7/8"; LONG_RO/2=42 15/16"; MB_A=54"; MB_HT=43 3/16"; MB_HT+.25"=43 7/16"; MB_HT-2.75"=40 7/16"; MB_HT/2=21 19/32"; Model=QMXHPVP-1X2_Mixing Box_Sides; NOZZLE_BOTTOM_ID=25 5/8"; NOZZLE_BOTTOM_RAD=12 13/16"; NOZZLE_HEIGHT=48"; NOZZLE_HEIGHT/7*2=12"; NOZZLE_SIZE=216"; NOZZLE_TOP_OD=27 1/2"; NOZZLE_TOP_RAD=13 3/4"; NOZZLE_WB/4=8 19/32"; NOZZLE_WB_OD=43"; NOZZLE_WB_RAD=21 1/2"; NOZZLE_WB_RAD-2"=19 1/2"; RO=34 3/4"; RO/2=17 3/8"; RO2/2=17 3/8"; TRANSITION_TOP=61 1/8"; TYPE=12"; Type Comments=Vari-Plume Laboratory Exhaust Mixed-Flow High Pressure Inline Belt Drive With 1X2 Mixing Box With Weather Hoods On Sides; UNIT_HEIGHT=41"; UNIT_HEIGHT*.75=30 3/4"; UNIT_OD=31 15/16"; UNIT_RAD+((A/2)+.25")=37 7/32"; UNIT_RAD+((A/2)+.25")+4"=41 7/32"; UNIT_RADIUS=15 31/32"; UNIT_RADIUS*.6=14 3/8"; UNIT_RADIUS+4"=19 31/32"
- 245_QMXHPVP-15H-1X2_Mixing_Box_Ends: (A/2)+.25"=22 1/4"; (A/2)+.5"=-22 1/2"; (A/2)-.5"=-21 1/2"; (A/2)-2"=20"; (NOZZLE_HEIGHT-(NOZZLE_HEIGHT/8*2))/2=16 1/8"; (NOZZLE_WB_OD-NOZZLE_TOP_OD)/2=3 1/4"; -A=-44"; A=44"; A+.5=44 1/2"; A/2=22"; B=121"; B/2=60 1/2"; C=59"; C/2=29 1/2"; DUAL_F=108"; DUAL_F+1"=109"; DUAL_G=107 1/8"; E=42 15/16"; GA=3/32"; LONG_RO=100 7/8"; LONG_RO/2=50 7/16"; MB_A=57"; MB_HT=45 7/16"; MB_HT+.25"=45 11/16"; MB_HT-2.75"=42 11/16"; MB_HT/2=22 23/32"; Model=QMXHPVP-1X2_Mixing Box_Sides; NOZZLE_BOTTOM_ID=21 3/8"; NOZZLE_BOTTOM_RAD=10 11/16"; NOZZLE_HEIGHT=43"; NOZZLE_HEIGHT/7*2=10 3/4"; NOZZLE_SIZE=180"; NOZZLE_TOP_OD=23"; NOZZLE_TOP_RAD=11 1/2"; NOZZLE_WB/4=7 3/16"; NOZZLE_WB_OD=36"; NOZZLE_WB_RAD=18"; NOZZLE_WB_RAD-2"=16"; RO=36 3/4"; RO/2=18 3/8"; RO2/2=18 3/8"; TRANSITION_TOP=77 11/16"; TYPE=12"; Type Comments=Vari-Plume Laboratory Exhaust Mixed-Flow High Pressure Inline Belt Drive With 1X2 Mixing Box With Weather Hoods On Sides; UNIT_HEIGHT=44 1/2"; UNIT_HEIGHT*.75=33 3/8"; UNIT_OD=34 3/4"; UNIT_RAD+((A/2)+.25")=39 5/8"; UNIT_RAD+((A/2)+.25")+4"=43 5/8"; UNIT_RADIUS=17 3/8"; UNIT_RADIUS*.6=15 5/8"; UNIT_RADIUS+4"=21 3/8"
- 245_QMXHPVP-15L-1X2_Mixing_Box_Ends: (A/2)+.25"=22 1/4"; (A/2)+.5"=-22 1/2"; (A/2)-.5"=-21 1/2"; (A/2)-2"=20"; (NOZZLE_HEIGHT-(NOZZLE_HEIGHT/8*2))/2=16 1/8"; (NOZZLE_WB_OD-NOZZLE_TOP_OD)/2=3 1/4"; -A=-44"; A=44"; A+.5=44 1/2"; A/2=22"; B=121"; B/2=60 1/2"; C=59"; C/2=29 1/2"; DUAL_F=108"; DUAL_F+1"=109"; DUAL_G=107 1/8"; E=42 15/16"; GA=3/32"; LONG_RO=100 7/8"; LONG_RO/2=50 7/16"; MB_A=57"; MB_HT=45 7/16"; MB_HT+.25"=45 11/16"; MB_HT-2.75"=42 11/16"; MB_HT/2=22 23/32"; Model=QMXHPVP-1X2_Mixing Box_Sides; NOZZLE_BOTTOM_ID=21 3/8"; NOZZLE_BOTTOM_RAD=10 11/16"; NOZZLE_HEIGHT=43"; NOZZLE_HEIGHT/7*2=10 3/4"; NOZZLE_SIZE=180"; NOZZLE_TOP_OD=23"; NOZZLE_TOP_RAD=11 1/2"; NOZZLE_WB/4=7 3/16"; NOZZLE_WB_OD=36"; NOZZLE_WB_RAD=18"; NOZZLE_WB_RAD-2"=16"; RO=36 3/4"; RO/2=18 3/8"; RO2/2=18 3/8"; TRANSITION_TOP=77 11/16"; TYPE=12"; Type Comments=Vari-Plume Laboratory Exhaust Mixed-Flow High Pressure Inline Belt Drive With 1X2 Mixing Box With Weather Hoods On Sides; UNIT_HEIGHT=44 1/2"; UNIT_HEIGHT*.75=33 3/8"; UNIT_OD=34 3/4"; UNIT_RAD+((A/2)+.25")=39 5/8"; UNIT_RAD+((A/2)+.25")+4"=43 5/8"; UNIT_RADIUS=17 3/8"; UNIT_RADIUS*.6=15 5/8"; UNIT_RADIUS+4"=21 3/8"
- 245_QMXHPVP-18H-1X2_Mixing_Box_Ends: (A/2)+.25"=22 1/4"; (A/2)+.5"=-22 1/2"; (A/2)-.5"=-21 1/2"; (A/2)-2"=20"; (NOZZLE_HEIGHT-(NOZZLE_HEIGHT/8*2))/2=18"; (NOZZLE_WB_OD-NOZZLE_TOP_OD)/2=3 7/8"; -A=-44"; A=44"; A+.5=44 1/2"; A/2=22"; B=121"; B/2=60 1/2"; C=59"; C/2=29 1/2"; DUAL_F=108"; DUAL_F+1"=109"; DUAL_G=107 1/8"; E=42 15/16"; GA=3/32"; LONG_RO=100 7/8"; LONG_RO/2=50 7/16"; MB_A=57"; MB_HT=45 7/16"; MB_HT+.25"=45 11/16"; MB_HT-2.75"=42 11/16"; MB_HT/2=22 23/32"; Model=QMXHPVP-1X2_Mixing Box_Sides; NOZZLE_BOTTOM_ID=25 5/8"; NOZZLE_BOTTOM_RAD=12 13/16"; NOZZLE_HEIGHT=48"; NOZZLE_HEIGHT/7*2=12"; NOZZLE_SIZE=216"; NOZZLE_TOP_OD=27 1/2"; NOZZLE_TOP_RAD=13 3/4"; NOZZLE_WB/4=8 19/32"; NOZZLE_WB_OD=43"; NOZZLE_WB_RAD=21 1/2"; NOZZLE_WB_RAD-2"=19 1/2"; RO=36 3/4"; RO/2=18 3/8"; RO2/2=18 3/8"; TRANSITION_TOP=69 11/16"; TYPE=12"; Type Comments=Vari-Plume Laboratory Exhaust Mixed-Flow High Pressure Inline Belt Drive With 1X2 Mixing Box With Weather Hoods On Sides; UNIT_HEIGHT=44 1/2"; UNIT_HEIGHT*.75=33 3/8"; UNIT_OD=34 3/4"; UNIT_RAD+((A/2)+.25")=39 5/8"; UNIT_RAD+((A/2)+.25")+4"=43 5/8"; UNIT_RADIUS=17 3/8"; UNIT_RADIUS*.6=15 5/8"; UNIT_RADIUS+4"=21 3/8"
- 245_QMXHPVP-18L-1X2_Mixing_Box_Ends: (A/2)+.25"=22 1/4"; (A/2)+.5"=-22 1/2"; (A/2)-.5"=-21 1/2"; (A/2)-2"=20"; (NOZZLE_HEIGHT-(NOZZLE_HEIGHT/8*2))/2=18"; (NOZZLE_WB_OD-NOZZLE_TOP_OD)/2=3 7/8"; -A=-44"; A=44"; A+.5=44 1/2"; A/2=22"; B=121"; B/2=60 1/2"; C=59"; C/2=29 1/2"; DUAL_F=108"; DUAL_F+1"=109"; DUAL_G=107 1/8"; E=42 15/16"; GA=3/32"; LONG_RO=100 7/8"; LONG_RO/2=50 7/16"; MB_A=57"; MB_HT=45 7/16"; MB_HT+.25"=45 11/16"; MB_HT-2.75"=42 11/16"; MB_HT/2=22 23/32"; Model=QMXHPVP-1X2_Mixing Box_Sides; NOZZLE_BOTTOM_ID=25 5/8"; NOZZLE_BOTTOM_RAD=12 13/16"; NOZZLE_HEIGHT=48"; NOZZLE_HEIGHT/7*2=12"; NOZZLE_SIZE=216"; NOZZLE_TOP_OD=27 1/2"; NOZZLE_TOP_RAD=13 3/4"; NOZZLE_WB/4=8 19/32"; NOZZLE_WB_OD=43"; NOZZLE_WB_RAD=21 1/2"; NOZZLE_WB_RAD-2"=19 1/2"; RO=36 3/4"; RO/2=18 3/8"; RO2/2=18 3/8"; TRANSITION_TOP=69 11/16"; TYPE=12"; Type Comments=Vari-Plume Laboratory Exhaust Mixed-Flow High Pressure Inline Belt Drive With 1X2 Mixing Box With Weather Hoods On Sides; UNIT_HEIGHT=44 1/2"; UNIT_HEIGHT*.75=33 3/8"; UNIT_OD=34 3/4"; UNIT_RAD+((A/2)+.25")=39 5/8"; UNIT_RAD+((A/2)+.25")+4"=43 5/8"; UNIT_RADIUS=17 3/8"; UNIT_RADIUS*.6=15 5/8"; UNIT_RADIUS+4"=21 3/8"
- 245_QMXHPVP-24H-1X2_Mixing_Box_Ends: (A/2)+.25"=22 1/4"; (A/2)+.5"=-22 1/2"; (A/2)-.5"=-21 1/2"; (A/2)-2"=20"; (NOZZLE_HEIGHT-(NOZZLE_HEIGHT/8*2))/2=23 1/4"; (NOZZLE_WB_OD-NOZZLE_TOP_OD)/2=6 1/8"; -A=-44"; A=44"; A+.5=44 1/2"; A/2=22"; B=121"; B/2=60 1/2"; C=59"; C/2=29 1/2"; DUAL_F=108"; DUAL_F+1"=109"; DUAL_G=107 1/8"; E=42 15/16"; GA=3/32"; LONG_RO=100 7/8"; LONG_RO/2=50 7/16"; MB_A=57"; MB_HT=45 7/16"; MB_HT+.25"=45 11/16"; MB_HT-2.75"=42 11/16"; MB_HT/2=22 23/32"; Model=QMXHPVP-1X2_Mixing Box_Sides; NOZZLE_BOTTOM_ID=34 3/4"; NOZZLE_BOTTOM_RAD=17 3/8"; NOZZLE_HEIGHT=62"; NOZZLE_HEIGHT/7*2=15 1/2"; NOZZLE_SIZE=288"; NOZZLE_TOP_OD=36 1/2"; NOZZLE_TOP_RAD=18 1/4"; NOZZLE_WB/4=12 3/16"; NOZZLE_WB_OD=61"; NOZZLE_WB_RAD=30 1/2"; NOZZLE_WB_RAD-2"=28 1/2"; RO=36 3/4"; RO/2=18 3/8"; RO2/2=18 3/8"; TRANSITION_TOP=57 3/4"; TYPE=12"; Type Comments=Vari-Plume Laboratory Exhaust Mixed-Flow High Pressure Inline Belt Drive With 1X2 Mixing Box With Weather Hoods On Sides; UNIT_HEIGHT=44 1/2"; UNIT_HEIGHT*.75=33 3/8"; UNIT_OD=34 3/4"; UNIT_RAD+((A/2)+.25")=39 5/8"; UNIT_RAD+((A/2)+.25")+4"=43 5/8"; UNIT_RADIUS=17 3/8"; UNIT_RADIUS*.6=15 5/8"; UNIT_RADIUS+4"=21 3/8"
- 245_QMXHPVP-24L-1X2_Mixing_Box_Ends: (A/2)+.25"=22 1/4"; (A/2)+.5"=-22 1/2"; (A/2)-.5"=-21 1/2"; (A/2)-2"=20"; (NOZZLE_HEIGHT-(NOZZLE_HEIGHT/8*2))/2=23 1/4"; (NOZZLE_WB_OD-NOZZLE_TOP_OD)/2=6 1/8"; -A=-44"; A=44"; A+.5=44 1/2"; A/2=22"; B=121"; B/2=60 1/2"; C=59"; C/2=29 1/2"; DUAL_F=108"; DUAL_F+1"=109"; DUAL_G=107 1/8"; E=42 15/16"; GA=3/32"; LONG_RO=100 7/8"; LONG_RO/2=50 7/16"; MB_A=57"; MB_HT=45 7/16"; MB_HT+.25"=45 11/16"; MB_HT-2.75"=42 11/16"; MB_HT/2=22 23/32"; Model=QMXHPVP-1X2_Mixing Box_Sides; NOZZLE_BOTTOM_ID=34 3/4"; NOZZLE_BOTTOM_RAD=17 3/8"; NOZZLE_HEIGHT=62"; NOZZLE_HEIGHT/7*2=15 1/2"; NOZZLE_SIZE=288"; NOZZLE_TOP_OD=36 1/2"; NOZZLE_TOP_RAD=18 1/4"; NOZZLE_WB/4=12 3/16"; NOZZLE_WB_OD=61"; NOZZLE_WB_RAD=30 1/2"; NOZZLE_WB_RAD-2"=28 1/2"; RO=36 3/4"; RO/2=18 3/8"; RO2/2=18 3/8"; TRANSITION_TOP=57 3/4"; TYPE=12"; Type Comments=Vari-Plume Laboratory Exhaust Mixed-Flow High Pressure Inline Belt Drive With 1X2 Mixing Box With Weather Hoods On Sides; UNIT_HEIGHT=44 1/2"; UNIT_HEIGHT*.75=33 3/8"; UNIT_OD=34 3/4"; UNIT_RAD+((A/2)+.25")=39 5/8"; UNIT_RAD+((A/2)+.25")+4"=43 5/8"; UNIT_RADIUS=17 3/8"; UNIT_RADIUS*.6=15 5/8"; UNIT_RADIUS+4"=21 3/8"
- 270_QMXHPVP-15H-1X2_Mixing_Box_Ends: (A/2)+.25"=24 1/4"; (A/2)+.5"=-24 1/2"; (A/2)-.5"=-23 1/2"; (A/2)-2"=22"; (NOZZLE_HEIGHT-(NOZZLE_HEIGHT/8*2))/2=16 1/8"; (NOZZLE_WB_OD-NOZZLE_TOP_OD)/2=3 1/4"; -A=-48"; A=48"; A+.5=48 1/2"; A/2=24"; B=128"; B/2=64"; C=63"; C/2=31 1/2"; DUAL_F=112"; DUAL_F+1"=113"; DUAL_G=111 1/8"; E=46 15/16"; GA=3/32"; LONG_RO=104 7/8"; LONG_RO/2=52 7/16"; MB_A=62"; MB_HT=47 3/16"; MB_HT+.25"=47 7/16"; MB_HT-2.75"=44 7/16"; MB_HT/2=23 19/32"; Model=QMXHPVP-1X2_Mixing Box_Sides; NOZZLE_BOTTOM_ID=21 3/8"; NOZZLE_BOTTOM_RAD=10 11/16"; NOZZLE_HEIGHT=43"; NOZZLE_HEIGHT/7*2=10 3/4"; NOZZLE_SIZE=180"; NOZZLE_TOP_OD=23"; NOZZLE_TOP_RAD=11 1/2"; NOZZLE_WB/4=7 3/16"; NOZZLE_WB_OD=36"; NOZZLE_WB_RAD=18"; NOZZLE_WB_RAD-2"=16"; RO=40 3/4"; RO/2=20 3/8"; RO2/2=20 3/8"; TRANSITION_TOP=86 3/16"; TYPE=12"; Type Comments=Vari-Plume Laboratory Exhaust Mixed-Flow High Pressure Inline Belt Drive With 1X2 Mixing Box With Weather Hoods On Sides; UNIT_HEIGHT=47"; UNIT_HEIGHT*.75=35 1/4"; UNIT_OD=38 5/16"; UNIT_RAD+((A/2)+.25")=43 13/32"; UNIT_RAD+((A/2)+.25")+4"=47 13/32"; UNIT_RADIUS=19 5/32"; UNIT_RADIUS*.6=17 1/4"; UNIT_RADIUS+4"=23 5/32"
- 270_QMXHPVP-15L-1X2_Mixing_Box_Ends: (A/2)+.25"=24 1/4"; (A/2)+.5"=-24 1/2"; (A/2)-.5"=-23 1/2"; (A/2)-2"=22"; (NOZZLE_HEIGHT-(NOZZLE_HEIGHT/8*2))/2=16 1/8"; (NOZZLE_WB_OD-NOZZLE_TOP_OD)/2=3 1/4"; -A=-48"; A=48"; A+.5=48 1/2"; A/2=24"; B=128"; B/2=64"; C=63"; C/2=31 1/2"; DUAL_F=112"; DUAL_F+1"=113"; DUAL_G=111 1/8"; E=46 15/16"; GA=3/32"; LONG_RO=104 7/8"; LONG_RO/2=52 7/16"; MB_A=62"; MB_HT=47 3/16"; MB_HT+.25"=47 7/16"; MB_HT-2.75"=44 7/16"; MB_HT/2=23 19/32"; Model=QMXHPVP-1X2_Mixing Box_Sides; NOZZLE_BOTTOM_ID=21 3/8"; NOZZLE_BOTTOM_RAD=10 11/16"; NOZZLE_HEIGHT=43"; NOZZLE_HEIGHT/7*2=10 3/4"; NOZZLE_SIZE=180"; NOZZLE_TOP_OD=23"; NOZZLE_TOP_RAD=11 1/2"; NOZZLE_WB/4=7 3/16"; NOZZLE_WB_OD=36"; NOZZLE_WB_RAD=18"; NOZZLE_WB_RAD-2"=16"; RO=40 3/4"; RO/2=20 3/8"; RO2/2=20 3/8"; TRANSITION_TOP=86 3/16"; TYPE=12"; Type Comments=Vari-Plume Laboratory Exhaust Mixed-Flow High Pressure Inline Belt Drive With 1X2 Mixing Box With Weather Hoods On Sides; UNIT_HEIGHT=47"; UNIT_HEIGHT*.75=35 1/4"; UNIT_OD=38 5/16"; UNIT_RAD+((A/2)+.25")=43 13/32"; UNIT_RAD+((A/2)+.25")+4"=47 13/32"; UNIT_RADIUS=19 5/32"; UNIT_RADIUS*.6=17 1/4"; UNIT_RADIUS+4"=23 5/32"
- 270_QMXHPVP-18H-1X2_Mixing_Box_Ends: (A/2)+.25"=24 1/4"; (A/2)+.5"=-24 1/2"; (A/2)-.5"=-23 1/2"; (A/2)-2"=22"; (NOZZLE_HEIGHT-(NOZZLE_HEIGHT/8*2))/2=18"; (NOZZLE_WB_OD-NOZZLE_TOP_OD)/2=3 7/8"; -A=-48"; A=48"; A+.5=48 1/2"; A/2=24"; B=128"; B/2=64"; C=63"; C/2=31 1/2"; DUAL_F=112"; DUAL_F+1"=113"; DUAL_G=111 1/8"; E=46 15/16"; GA=3/32"; LONG_RO=104 7/8"; LONG_RO/2=52 7/16"; MB_A=62"; MB_HT=47 3/16"; MB_HT+.25"=47 7/16"; MB_HT-2.75"=44 7/16"; MB_HT/2=23 19/32"; Model=QMXHPVP-1X2_Mixing Box_Sides; NOZZLE_BOTTOM_ID=25 5/8"; NOZZLE_BOTTOM_RAD=12 13/16"; NOZZLE_HEIGHT=48"; NOZZLE_HEIGHT/7*2=12"; NOZZLE_SIZE=216"; NOZZLE_TOP_OD=27 1/2"; NOZZLE_TOP_RAD=13 3/4"; NOZZLE_WB/4=8 19/32"; NOZZLE_WB_OD=43"; NOZZLE_WB_RAD=21 1/2"; NOZZLE_WB_RAD-2"=19 1/2"; RO=40 3/4"; RO/2=20 3/8"; RO2/2=20 3/8"; TRANSITION_TOP=79 3/16"; TYPE=12"; Type Comments=Vari-Plume Laboratory Exhaust Mixed-Flow High Pressure Inline Belt Drive With 1X2 Mixing Box With Weather Hoods On Sides; UNIT_HEIGHT=47"; UNIT_HEIGHT*.75=35 1/4"; UNIT_OD=38 5/16"; UNIT_RAD+((A/2)+.25")=43 13/32"; UNIT_RAD+((A/2)+.25")+4"=47 13/32"; UNIT_RADIUS=19 5/32"; UNIT_RADIUS*.6=17 1/4"; UNIT_RADIUS+4"=23 5/32"
- 270_QMXHPVP-18L-1X2_Mixing_Box_Ends: (A/2)+.25"=24 1/4"; (A/2)+.5"=-24 1/2"; (A/2)-.5"=-23 1/2"; (A/2)-2"=22"; (NOZZLE_HEIGHT-(NOZZLE_HEIGHT/8*2))/2=18"; (NOZZLE_WB_OD-NOZZLE_TOP_OD)/2=3 7/8"; -A=-48"; A=48"; A+.5=48 1/2"; A/2=24"; B=128"; B/2=64"; C=63"; C/2=31 1/2"; DUAL_F=112"; DUAL_F+1"=113"; DUAL_G=111 1/8"; E=46 15/16"; GA=3/32"; LONG_RO=104 7/8"; LONG_RO/2=52 7/16"; MB_A=62"; MB_HT=47 3/16"; MB_HT+.25"=47 7/16"; MB_HT-2.75"=44 7/16"; MB_HT/2=23 19/32"; Model=QMXHPVP-1X2_Mixing Box_Sides; NOZZLE_BOTTOM_ID=25 5/8"; NOZZLE_BOTTOM_RAD=12 13/16"; NOZZLE_HEIGHT=48"; NOZZLE_HEIGHT/7*2=12"; NOZZLE_SIZE=216"; NOZZLE_TOP_OD=27 1/2"; NOZZLE_TOP_RAD=13 3/4"; NOZZLE_WB/4=8 19/32"; NOZZLE_WB_OD=43"; NOZZLE_WB_RAD=21 1/2"; NOZZLE_WB_RAD-2"=19 1/2"; RO=40 3/4"; RO/2=20 3/8"; RO2/2=20 3/8"; TRANSITION_TOP=79 3/16"; TYPE=12"; Type Comments=Vari-Plume Laboratory Exhaust Mixed-Flow High Pressure Inline Belt Drive With 1X2 Mixing Box With Weather Hoods On Sides; UNIT_HEIGHT=47"; UNIT_HEIGHT*.75=35 1/4"; UNIT_OD=38 5/16"; UNIT_RAD+((A/2)+.25")=43 13/32"; UNIT_RAD+((A/2)+.25")+4"=47 13/32"; UNIT_RADIUS=19 5/32"; UNIT_RADIUS*.6=17 1/4"; UNIT_RADIUS+4"=23 5/32"
- 270_QMXHPVP-24H-1X2_Mixing_Box_Ends: (A/2)+.25"=24 1/4"; (A/2)+.5"=-24 1/2"; (A/2)-.5"=-23 1/2"; (A/2)-2"=22"; (NOZZLE_HEIGHT-(NOZZLE_HEIGHT/8*2))/2=23 1/4"; (NOZZLE_WB_OD-NOZZLE_TOP_OD)/2=6 1/8"; -A=-48"; A=48"; A+.5=48 1/2"; A/2=24"; B=128"; B/2=64"; C=63"; C/2=31 1/2"; DUAL_F=112"; DUAL_F+1"=113"; DUAL_G=111 1/8"; E=46 15/16"; GA=3/32"; LONG_RO=104 7/8"; LONG_RO/2=52 7/16"; MB_A=62"; MB_HT=47 3/16"; MB_HT+.25"=47 7/16"; MB_HT-2.75"=44 7/16"; MB_HT/2=23 19/32"; Model=QMXHPVP-1X2_Mixing Box_Sides; NOZZLE_BOTTOM_ID=34 3/4"; NOZZLE_BOTTOM_RAD=17 3/8"; NOZZLE_HEIGHT=62"; NOZZLE_HEIGHT/7*2=15 1/2"; NOZZLE_SIZE=288"; NOZZLE_TOP_OD=36 1/2"; NOZZLE_TOP_RAD=18 1/4"; NOZZLE_WB/4=12 3/16"; NOZZLE_WB_OD=61"; NOZZLE_WB_RAD=30 1/2"; NOZZLE_WB_RAD-2"=28 1/2"; RO=40 3/4"; RO/2=20 3/8"; RO2/2=20 3/8"; TRANSITION_TOP=62 1/4"; TYPE=12"; Type Comments=Vari-Plume Laboratory Exhaust Mixed-Flow High Pressure Inline Belt Drive With 1X2 Mixing Box With Weather Hoods On Sides; UNIT_HEIGHT=47"; UNIT_HEIGHT*.75=35 1/4"; UNIT_OD=38 5/16"; UNIT_RAD+((A/2)+.25")=43 13/32"; UNIT_RAD+((A/2)+.25")+4"=47 13/32"; UNIT_RADIUS=19 5/32"; UNIT_RADIUS*.6=17 1/4"; UNIT_RADIUS+4"=23 5/32"
- 270_QMXHPVP-24L-1X2_Mixing_Box_Ends: (A/2)+.25"=24 1/4"; (A/2)+.5"=-24 1/2"; (A/2)-.5"=-23 1/2"; (A/2)-2"=22"; (NOZZLE_HEIGHT-(NOZZLE_HEIGHT/8*2))/2=23 1/4"; (NOZZLE_WB_OD-NOZZLE_TOP_OD)/2=6 1/8"; -A=-48"; A=48"; A+.5=48 1/2"; A/2=24"; B=128"; B/2=64"; C=63"; C/2=31 1/2"; DUAL_F=112"; DUAL_F+1"=113"; DUAL_G=111 1/8"; E=46 15/16"; GA=3/32"; LONG_RO=104 7/8"; LONG_RO/2=52 7/16"; MB_A=62"; MB_HT=47 3/16"; MB_HT+.25"=47 7/16"; MB_HT-2.75"=44 7/16"; MB_HT/2=23 19/32"; Model=QMXHPVP-1X2_Mixing Box_Sides; NOZZLE_BOTTOM_ID=34 3/4"; NOZZLE_BOTTOM_RAD=17 3/8"; NOZZLE_HEIGHT=62"; NOZZLE_HEIGHT/7*2=15 1/2"; NOZZLE_SIZE=288"; NOZZLE_TOP_OD=36 1/2"; NOZZLE_TOP_RAD=18 1/4"; NOZZLE_WB/4=12 3/16"; NOZZLE_WB_OD=61"; NOZZLE_WB_RAD=30 1/2"; NOZZLE_WB_RAD-2"=28 1/2"; RO=40 3/4"; RO/2=20 3/8"; RO2/2=20 3/8"; TRANSITION_TOP=62 1/4"; TYPE=12"; Type Comments=Vari-Plume Laboratory Exhaust Mixed-Flow High Pressure Inline Belt Drive With 1X2 Mixing Box With Weather Hoods On Sides; UNIT_HEIGHT=47"; UNIT_HEIGHT*.75=35 1/4"; UNIT_OD=38 5/16"; UNIT_RAD+((A/2)+.25")=43 13/32"; UNIT_RAD+((A/2)+.25")+4"=47 13/32"; UNIT_RADIUS=19 5/32"; UNIT_RADIUS*.6=17 1/4"; UNIT_RADIUS+4"=23 5/32"
- 300_QMXHPVP-18H-1X2_Mixing_Box_Ends: (A/2)+.25"=26 1/4"; (A/2)+.5"=-26 1/2"; (A/2)-.5"=-25 1/2"; (A/2)-2"=24"; (NOZZLE_HEIGHT-(NOZZLE_HEIGHT/8*2))/2=18"; (NOZZLE_WB_OD-NOZZLE_TOP_OD)/2=3 7/8"; -A=-52"; A=52"; A+.5=52 1/2"; A/2=26"; B=148"; B/2=74"; C=67"; C/2=33 1/2"; DUAL_F=132"; DUAL_F+1"=133"; DUAL_G=131 1/8"; E=50 15/16"; GA=3/32"; LONG_RO=124 7/8"; LONG_RO/2=62 7/16"; MB_A=68"; MB_HT=50 7/16"; MB_HT+.25"=50 11/16"; MB_HT-2.75"=47 11/16"; MB_HT/2=25 7/32"; Model=QMXHPVP-1X2_Mixing Box_Sides; NOZZLE_BOTTOM_ID=25 5/8"; NOZZLE_BOTTOM_RAD=12 13/16"; NOZZLE_HEIGHT=48"; NOZZLE_HEIGHT/7*2=12"; NOZZLE_SIZE=216"; NOZZLE_TOP_OD=27 1/2"; NOZZLE_TOP_RAD=13 3/4"; NOZZLE_WB/4=8 19/32"; NOZZLE_WB_OD=43"; NOZZLE_WB_RAD=21 1/2"; NOZZLE_WB_RAD-2"=19 1/2"; RO=44 3/4"; RO/2=22 3/8"; RO2/2=22 3/8"; TRANSITION_TOP=94 3/16"; TYPE=12"; Type Comments=Vari-Plume Laboratory Exhaust Mixed-Flow High Pressure Inline Belt Drive With 1X2 Mixing Box With Weather Hoods On Sides; UNIT_HEIGHT=54"; UNIT_HEIGHT*.75=40 1/2"; UNIT_OD=42 1/2"; UNIT_RAD+((A/2)+.25")=47 1/2"; UNIT_RAD+((A/2)+.25")+4"=51 1/2"; UNIT_RADIUS=21 1/4"; UNIT_RADIUS*.6=19 1/8"; UNIT_RADIUS+4"=25 1/4"
- 300_QMXHPVP-18L-1X2_Mixing_Box_Ends: (A/2)+.25"=26 1/4"; (A/2)+.5"=-26 1/2"; (A/2)-.5"=-25 1/2"; (A/2)-2"=24"; (NOZZLE_HEIGHT-(NOZZLE_HEIGHT/8*2))/2=18"; (NOZZLE_WB_OD-NOZZLE_TOP_OD)/2=3 7/8"; -A=-52"; A=52"; A+.5=52 1/2"; A/2=26"; B=148"; B/2=74"; C=67"; C/2=33 1/2"; DUAL_F=132"; DUAL_F+1"=133"; DUAL_G=131 1/8"; E=50 15/16"; GA=3/32"; LONG_RO=124 7/8"; LONG_RO/2=62 7/16"; MB_A=68"; MB_HT=50 7/16"; MB_HT+.25"=50 11/16"; MB_HT-2.75"=47 11/16"; MB_HT/2=25 7/32"; Model=QMXHPVP-1X2_Mixing Box_Sides; NOZZLE_BOTTOM_ID=25 5/8"; NOZZLE_BOTTOM_RAD=12 13/16"; NOZZLE_HEIGHT=48"; NOZZLE_HEIGHT/7*2=12"; NOZZLE_SIZE=216"; NOZZLE_TOP_OD=27 1/2"; NOZZLE_TOP_RAD=13 3/4"; NOZZLE_WB/4=8 19/32"; NOZZLE_WB_OD=43"; NOZZLE_WB_RAD=21 1/2"; NOZZLE_WB_RAD-2"=19 1/2"; RO=44 3/4"; RO/2=22 3/8"; RO2/2=22 3/8"; TRANSITION_TOP=94 3/16"; TYPE=12"; Type Comments=Vari-Plume Laboratory Exhaust Mixed-Flow High Pressure Inline Belt Drive With 1X2 Mixing Box With Weather Hoods On Sides; UNIT_HEIGHT=54"; UNIT_HEIGHT*.75=40 1/2"; UNIT_OD=42 1/2"; UNIT_RAD+((A/2)+.25")=47 1/2"; UNIT_RAD+((A/2)+.25")+4"=51 1/2"; UNIT_RADIUS=21 1/4"; UNIT_RADIUS*.6=19 1/8"; UNIT_RADIUS+4"=25 1/4"
- 300_QMXHPVP-24H-1X2_Mixing_Box_Ends: (A/2)+.25"=26 1/4"; (A/2)+.5"=-26 1/2"; (A/2)-.5"=-25 1/2"; (A/2)-2"=24"; (NOZZLE_HEIGHT-(NOZZLE_HEIGHT/8*2))/2=23 1/4"; (NOZZLE_WB_OD-NOZZLE_TOP_OD)/2=6 1/8"; -A=-52"; A=52"; A+.5=52 1/2"; A/2=26"; B=148"; B/2=74"; C=67"; C/2=33 1/2"; DUAL_F=132"; DUAL_F+1"=133"; DUAL_G=131 1/8"; E=50 15/16"; GA=3/32"; LONG_RO=124 7/8"; LONG_RO/2=62 7/16"; MB_A=68"; MB_HT=50 7/16"; MB_HT+.25"=50 11/16"; MB_HT-2.75"=47 11/16"; MB_HT/2=25 7/32"; Model=QMXHPVP-1X2_Mixing Box_Sides; NOZZLE_BOTTOM_ID=34 3/4"; NOZZLE_BOTTOM_RAD=17 3/8"; NOZZLE_HEIGHT=62"; NOZZLE_HEIGHT/7*2=15 1/2"; NOZZLE_SIZE=288"; NOZZLE_TOP_OD=36 1/2"; NOZZLE_TOP_RAD=18 1/4"; NOZZLE_WB/4=12 3/16"; NOZZLE_WB_OD=61"; NOZZLE_WB_RAD=30 1/2"; NOZZLE_WB_RAD-2"=28 1/2"; RO=44 3/4"; RO/2=22 3/8"; RO2/2=22 3/8"; TRANSITION_TOP=77 1/4"; TYPE=12"; Type Comments=Vari-Plume Laboratory Exhaust Mixed-Flow High Pressure Inline Belt Drive With 1X2 Mixing Box With Weather Hoods On Sides; UNIT_HEIGHT=54"; UNIT_HEIGHT*.75=40 1/2"; UNIT_OD=42 1/2"; UNIT_RAD+((A/2)+.25")=47 1/2"; UNIT_RAD+((A/2)+.25")+4"=51 1/2"; UNIT_RADIUS=21 1/4"; UNIT_RADIUS*.6=19 1/8"; UNIT_RADIUS+4"=25 1/4"
- 300_QMXHPVP-24L-1X2_Mixing_Box_Ends: (A/2)+.25"=26 1/4"; (A/2)+.5"=-26 1/2"; (A/2)-.5"=-25 1/2"; (A/2)-2"=24"; (NOZZLE_HEIGHT-(NOZZLE_HEIGHT/8*2))/2=23 1/4"; (NOZZLE_WB_OD-NOZZLE_TOP_OD)/2=6 1/8"; -A=-52"; A=52"; A+.5=52 1/2"; A/2=26"; B=148"; B/2=74"; C=67"; C/2=33 1/2"; DUAL_F=132"; DUAL_F+1"=133"; DUAL_G=131 1/8"; E=50 15/16"; GA=3/32"; LONG_RO=124 7/8"; LONG_RO/2=62 7/16"; MB_A=68"; MB_HT=50 7/16"; MB_HT+.25"=50 11/16"; MB_HT-2.75"=47 11/16"; MB_HT/2=25 7/32"; Model=QMXHPVP-1X2_Mixing Box_Sides; NOZZLE_BOTTOM_ID=34 3/4"; NOZZLE_BOTTOM_RAD=17 3/8"; NOZZLE_HEIGHT=62"; NOZZLE_HEIGHT/7*2=15 1/2"; NOZZLE_SIZE=288"; NOZZLE_TOP_OD=36 1/2"; NOZZLE_TOP_RAD=18 1/4"; NOZZLE_WB/4=12 3/16"; NOZZLE_WB_OD=61"; NOZZLE_WB_RAD=30 1/2"; NOZZLE_WB_RAD-2"=28 1/2"; RO=44 3/4"; RO/2=22 3/8"; RO2/2=22 3/8"; TRANSITION_TOP=77 1/4"; TYPE=12"; Type Comments=Vari-Plume Laboratory Exhaust Mixed-Flow High Pressure Inline Belt Drive With 1X2 Mixing Box With Weather Hoods On Sides; UNIT_HEIGHT=54"; UNIT_HEIGHT*.75=40 1/2"; UNIT_OD=42 1/2"; UNIT_RAD+((A/2)+.25")=47 1/2"; UNIT_RAD+((A/2)+.25")+4"=51 1/2"; UNIT_RADIUS=21 1/4"; UNIT_RADIUS*.6=19 1/8"; UNIT_RADIUS+4"=25 1/4"
- 300_QMXHPVP-30H-1X2_Mixing_Box_Ends: (A/2)+.25"=26 1/4"; (A/2)+.5"=-26 1/2"; (A/2)-.5"=-25 1/2"; (A/2)-2"=24"; (NOZZLE_HEIGHT-(NOZZLE_HEIGHT/8*2))/2=29 1/4"; (NOZZLE_WB_OD-NOZZLE_TOP_OD)/2=7 1/8"; -A=-52"; A=52"; A+.5=52 1/2"; A/2=26"; B=148"; B/2=74"; C=67"; C/2=33 1/2"; DUAL_F=132"; DUAL_F+1"=133"; DUAL_G=131 1/8"; E=50 15/16"; GA=3/32"; LONG_RO=124 7/8"; LONG_RO/2=62 7/16"; MB_A=68"; MB_HT=50 7/16"; MB_HT+.25"=50 11/16"; MB_HT-2.75"=47 11/16"; MB_HT/2=25 7/32"; Model=QMXHPVP-1X2_Mixing Box_Sides; NOZZLE_BOTTOM_ID=42 1/2"; NOZZLE_BOTTOM_RAD=21 1/4"; NOZZLE_HEIGHT=78"; NOZZLE_HEIGHT/7*2=19 1/2"; NOZZLE_SIZE=360"; NOZZLE_TOP_OD=45 1/2"; NOZZLE_TOP_RAD=22 3/4"; NOZZLE_WB/4=14 13/16"; NOZZLE_WB_OD=74"; NOZZLE_WB_RAD=37"; NOZZLE_WB_RAD-2"=35"; RO=44 3/4"; RO/2=22 3/8"; RO2/2=22 3/8"; TRANSITION_TOP=68 1/4"; TYPE=12"; Type Comments=Vari-Plume Laboratory Exhaust Mixed-Flow High Pressure Inline Belt Drive With 1X2 Mixing Box With Weather Hoods On Sides; UNIT_HEIGHT=54"; UNIT_HEIGHT*.75=40 1/2"; UNIT_OD=42 1/2"; UNIT_RAD+((A/2)+.25")=47 1/2"; UNIT_RAD+((A/2)+.25")+4"=51 1/2"; UNIT_RADIUS=21 1/4"; UNIT_RADIUS*.6=19 1/8"; UNIT_RADIUS+4"=25 1/4"
- 300_QMXHPVP-30L-1X2_Mixing_Box_Ends: (A/2)+.25"=26 1/4"; (A/2)+.5"=-26 1/2"; (A/2)-.5"=-25 1/2"; (A/2)-2"=24"; (NOZZLE_HEIGHT-(NOZZLE_HEIGHT/8*2))/2=29 1/4"; (NOZZLE_WB_OD-NOZZLE_TOP_OD)/2=7 1/8"; -A=-52"; A=52"; A+.5=52 1/2"; A/2=26"; B=148"; B/2=74"; C=67"; C/2=33 1/2"; DUAL_F=132"; DUAL_F+1"=133"; DUAL_G=131 1/8"; E=50 15/16"; GA=3/32"; LONG_RO=124 7/8"; LONG_RO/2=62 7/16"; MB_A=68"; MB_HT=50 7/16"; MB_HT+.25"=50 11/16"; MB_HT-2.75"=47 11/16"; MB_HT/2=25 7/32"; Model=QMXHPVP-1X2_Mixing Box_Sides; NOZZLE_BOTTOM_ID=42 1/2"; NOZZLE_BOTTOM_RAD=21 1/4"; NOZZLE_HEIGHT=78"; NOZZLE_HEIGHT/7*2=19 1/2"; NOZZLE_SIZE=360"; NOZZLE_TOP_OD=45 1/2"; NOZZLE_TOP_RAD=22 3/4"; NOZZLE_WB/4=14 13/16"; NOZZLE_WB_OD=74"; NOZZLE_WB_RAD=37"; NOZZLE_WB_RAD-2"=35"; RO=44 3/4"; RO/2=22 3/8"; RO2/2=22 3/8"; TRANSITION_TOP=68 1/4"; TYPE=12"; Type Comments=Vari-Plume Laboratory Exhaust Mixed-Flow High Pressure Inline Belt Drive With 1X2 Mixing Box With Weather Hoods On Sides; UNIT_HEIGHT=54"; UNIT_HEIGHT*.75=40 1/2"; UNIT_OD=42 1/2"; UNIT_RAD+((A/2)+.25")=47 1/2"; UNIT_RAD+((A/2)+.25")+4"=51 1/2"; UNIT_RADIUS=21 1/4"; UNIT_RADIUS*.6=19 1/8"; UNIT_RADIUS+4"=25 1/4"
- 330_QMXHPVP-24H-1X2_Mixing_Box_Ends: (A/2)+.25"=28 1/4"; (A/2)+.5"=-28 1/2"; (A/2)-.5"=-27 1/2"; (A/2)-2"=26"; (NOZZLE_HEIGHT-(NOZZLE_HEIGHT/8*2))/2=23 1/4"; (NOZZLE_WB_OD-NOZZLE_TOP_OD)/2=6 1/8"; -A=-56"; A=56"; A+.5=56 1/2"; A/2=28"; B=154"; B/2=77"; C=73"; C/2=36 1/2"; DUAL_F=136"; DUAL_F+1"=137"; DUAL_G=135 1/8"; E=54 13/16"; GA=3/32"; LONG_RO=128 7/8"; LONG_RO/2=64 7/16"; MB_A=73"; MB_HT=53 11/16"; MB_HT+.25"=53 15/16"; MB_HT-2.75"=50 15/16"; MB_HT/2=26 27/32"; Model=QMXHPVP-1X2_Mixing Box_Sides; NOZZLE_BOTTOM_ID=34 3/4"; NOZZLE_BOTTOM_RAD=17 3/8"; NOZZLE_HEIGHT=62"; NOZZLE_HEIGHT/7*2=15 1/2"; NOZZLE_SIZE=288"; NOZZLE_TOP_OD=36 1/2"; NOZZLE_TOP_RAD=18 1/4"; NOZZLE_WB/4=12 3/16"; NOZZLE_WB_OD=61"; NOZZLE_WB_RAD=30 1/2"; NOZZLE_WB_RAD-2"=28 1/2"; RO=48 5/8"; RO/2=24 5/16"; RO2/2=24 5/16"; TRANSITION_TOP=89 3/4"; TYPE=12"; Type Comments=Vari-Plume Laboratory Exhaust Mixed-Flow High Pressure Inline Belt Drive With 1X2 Mixing Box With Weather Hoods On Sides; UNIT_HEIGHT=58 1/2"; UNIT_HEIGHT*.75=43 7/8"; UNIT_OD=46 3/4"; UNIT_RAD+((A/2)+.25")=51 5/8"; UNIT_RAD+((A/2)+.25")+4"=55 5/8"; UNIT_RADIUS=23 3/8"; UNIT_RADIUS*.6=21 1/32"; UNIT_RADIUS+4"=27 3/8"
- 330_QMXHPVP-24L-1X2_Mixing_Box_Ends: (A/2)+.25"=28 1/4"; (A/2)+.5"=-28 1/2"; (A/2)-.5"=-27 1/2"; (A/2)-2"=26"; (NOZZLE_HEIGHT-(NOZZLE_HEIGHT/8*2))/2=23 1/4"; (NOZZLE_WB_OD-NOZZLE_TOP_OD)/2=6 1/8"; -A=-56"; A=56"; A+.5=56 1/2"; A/2=28"; B=154"; B/2=77"; C=73"; C/2=36 1/2"; DUAL_F=136"; DUAL_F+1"=137"; DUAL_G=135 1/8"; E=54 13/16"; GA=3/32"; LONG_RO=128 7/8"; LONG_RO/2=64 7/16"; MB_A=73"; MB_HT=53 11/16"; MB_HT+.25"=53 15/16"; MB_HT-2.75"=50 15/16"; MB_HT/2=26 27/32"; Model=QMXHPVP-1X2_Mixing Box_Sides; NOZZLE_BOTTOM_ID=34 3/4"; NOZZLE_BOTTOM_RAD=17 3/8"; NOZZLE_HEIGHT=62"; NOZZLE_HEIGHT/7*2=15 1/2"; NOZZLE_SIZE=288"; NOZZLE_TOP_OD=36 1/2"; NOZZLE_TOP_RAD=18 1/4"; NOZZLE_WB/4=12 3/16"; NOZZLE_WB_OD=61"; NOZZLE_WB_RAD=30 1/2"; NOZZLE_WB_RAD-2"=28 1/2"; RO=48 5/8"; RO/2=24 5/16"; RO2/2=24 5/16"; TRANSITION_TOP=89 3/4"; TYPE=12"; Type Comments=Vari-Plume Laboratory Exhaust Mixed-Flow High Pressure Inline Belt Drive With 1X2 Mixing Box With Weather Hoods On Sides; UNIT_HEIGHT=58 1/2"; UNIT_HEIGHT*.75=43 7/8"; UNIT_OD=46 3/4"; UNIT_RAD+((A/2)+.25")=51 5/8"; UNIT_RAD+((A/2)+.25")+4"=55 5/8"; UNIT_RADIUS=23 3/8"; UNIT_RADIUS*.6=21 1/32"; UNIT_RADIUS+4"=27 3/8"
- 330_QMXHPVP-30H-1X2_Mixing_Box_Ends: (A/2)+.25"=28 1/4"; (A/2)+.5"=-28 1/2"; (A/2)-.5"=-27 1/2"; (A/2)-2"=26"; (NOZZLE_HEIGHT-(NOZZLE_HEIGHT/8*2))/2=29 1/4"; (NOZZLE_WB_OD-NOZZLE_TOP_OD)/2=7 1/8"; -A=-56"; A=56"; A+.5=56 1/2"; A/2=28"; B=154"; B/2=77"; C=73"; C/2=36 1/2"; DUAL_F=136"; DUAL_F+1"=137"; DUAL_G=135 1/8"; E=54 13/16"; GA=3/32"; LONG_RO=128 7/8"; LONG_RO/2=64 7/16"; MB_A=73"; MB_HT=53 11/16"; MB_HT+.25"=53 15/16"; MB_HT-2.75"=50 15/16"; MB_HT/2=26 27/32"; Model=QMXHPVP-1X2_Mixing Box_Sides; NOZZLE_BOTTOM_ID=42 1/2"; NOZZLE_BOTTOM_RAD=21 1/4"; NOZZLE_HEIGHT=78"; NOZZLE_HEIGHT/7*2=19 1/2"; NOZZLE_SIZE=360"; NOZZLE_TOP_OD=45 1/2"; NOZZLE_TOP_RAD=22 3/4"; NOZZLE_WB/4=14 13/16"; NOZZLE_WB_OD=74"; NOZZLE_WB_RAD=37"; NOZZLE_WB_RAD-2"=35"; RO=48 5/8"; RO/2=24 5/16"; RO2/2=24 5/16"; TRANSITION_TOP=74 3/4"; TYPE=12"; Type Comments=Vari-Plume Laboratory Exhaust Mixed-Flow High Pressure Inline Belt Drive With 1X2 Mixing Box With Weather Hoods On Sides; UNIT_HEIGHT=58 1/2"; UNIT_HEIGHT*.75=43 7/8"; UNIT_OD=46 3/4"; UNIT_RAD+((A/2)+.25")=51 5/8"; UNIT_RAD+((A/2)+.25")+4"=55 5/8"; UNIT_RADIUS=23 3/8"; UNIT_RADIUS*.6=21 1/32"; UNIT_RADIUS+4"=27 3/8"
- 330_QMXHPVP-30L-1X2_Mixing_Box_Ends: (A/2)+.25"=28 1/4"; (A/2)+.5"=-28 1/2"; (A/2)-.5"=-27 1/2"; (A/2)-2"=26"; (NOZZLE_HEIGHT-(NOZZLE_HEIGHT/8*2))/2=29 1/4"; (NOZZLE_WB_OD-NOZZLE_TOP_OD)/2=7 1/8"; -A=-56"; A=56"; A+.5=56 1/2"; A/2=28"; B=154"; B/2=77"; C=73"; C/2=36 1/2"; DUAL_F=136"; DUAL_F+1"=137"; DUAL_G=135 1/8"; E=54 13/16"; GA=3/32"; LONG_RO=128 7/8"; LONG_RO/2=64 7/16"; MB_A=73"; MB_HT=53 11/16"; MB_HT+.25"=53 15/16"; MB_HT-2.75"=50 15/16"; MB_HT/2=26 27/32"; Model=QMXHPVP-1X2_Mixing Box_Sides; NOZZLE_BOTTOM_ID=42 1/2"; NOZZLE_BOTTOM_RAD=21 1/4"; NOZZLE_HEIGHT=78"; NOZZLE_HEIGHT/7*2=19 1/2"; NOZZLE_SIZE=360"; NOZZLE_TOP_OD=45 1/2"; NOZZLE_TOP_RAD=22 3/4"; NOZZLE_WB/4=14 13/16"; NOZZLE_WB_OD=74"; NOZZLE_WB_RAD=37"; NOZZLE_WB_RAD-2"=35"; RO=48 5/8"; RO/2=24 5/16"; RO2/2=24 5/16"; TRANSITION_TOP=74 3/4"; TYPE=12"; Type Comments=Vari-Plume Laboratory Exhaust Mixed-Flow High Pressure Inline Belt Drive With 1X2 Mixing Box With Weather Hoods On Sides; UNIT_HEIGHT=58 1/2"; UNIT_HEIGHT*.75=43 7/8"; UNIT_OD=46 3/4"; UNIT_RAD+((A/2)+.25")=51 5/8"; UNIT_RAD+((A/2)+.25")+4"=55 5/8"; UNIT_RADIUS=23 3/8"; UNIT_RADIUS*.6=21 1/32"; UNIT_RADIUS+4"=27 3/8"
- 365_QMXHPVP-24H-1X2_Mixing_Box_Ends: (A/2)+.25"=31 1/4"; (A/2)+.5"=-31 1/2"; (A/2)-.5"=-30 1/2"; (A/2)-2"=29"; (NOZZLE_HEIGHT-(NOZZLE_HEIGHT/8*2))/2=23 1/4"; (NOZZLE_WB_OD-NOZZLE_TOP_OD)/2=6 1/8"; -A=-62"; A=62"; A+.5=62 1/2"; A/2=31"; B=175"; B/2=87 1/2"; C=79"; C/2=39 1/2"; DUAL_F=159"; DUAL_F+1"=160"; DUAL_G=158"; E=60 3/4"; GA=3/32"; LONG_RO=151 3/4"; LONG_RO/2=75 7/8"; MB_A=82"; MB_HT=59 11/16"; MB_HT+.25"=59 15/16"; MB_HT-2.75"=56 15/16"; MB_HT/2=29 27/32"; Model=QMXHPVP-1X2_Mixing Box_Sides; NOZZLE_BOTTOM_ID=34 3/4"; NOZZLE_BOTTOM_RAD=17 3/8"; NOZZLE_HEIGHT=62"; NOZZLE_HEIGHT/7*2=15 1/2"; NOZZLE_SIZE=288"; NOZZLE_TOP_OD=36 1/2"; NOZZLE_TOP_RAD=18 1/4"; NOZZLE_WB/4=12 3/16"; NOZZLE_WB_OD=61"; NOZZLE_WB_RAD=30 1/2"; NOZZLE_WB_RAD-2"=28 1/2"; RO=54 1/2"; RO/2=27 1/4"; RO2/2=27 1/4"; TRANSITION_TOP=104 1/4"; TYPE=12"; Type Comments=Vari-Plume Laboratory Exhaust Mixed-Flow High Pressure Inline Belt Drive With 1X2 Mixing Box With Weather Hoods On Sides; UNIT_HEIGHT=64"; UNIT_HEIGHT*.75=48"; UNIT_OD=51 3/4"; UNIT_RAD+((A/2)+.25")=57 1/8"; UNIT_RAD+((A/2)+.25")+4"=61 1/8"; UNIT_RADIUS=25 7/8"; UNIT_RADIUS*.6=23 9/32"; UNIT_RADIUS+4"=29 7/8"
- 365_QMXHPVP-24L-1X2_Mixing_Box_Ends: (A/2)+.25"=31 1/4"; (A/2)+.5"=-31 1/2"; (A/2)-.5"=-30 1/2"; (A/2)-2"=29"; (NOZZLE_HEIGHT-(NOZZLE_HEIGHT/8*2))/2=23 1/4"; (NOZZLE_WB_OD-NOZZLE_TOP_OD)/2=6 1/8"; -A=-62"; A=62"; A+.5=62 1/2"; A/2=31"; B=175"; B/2=87 1/2"; C=79"; C/2=39 1/2"; DUAL_F=159"; DUAL_F+1"=160"; DUAL_G=158"; E=60 3/4"; GA=3/32"; LONG_RO=151 3/4"; LONG_RO/2=75 7/8"; MB_A=82"; MB_HT=59 11/16"; MB_HT+.25"=59 15/16"; MB_HT-2.75"=56 15/16"; MB_HT/2=29 27/32"; Model=QMXHPVP-1X2_Mixing Box_Sides; NOZZLE_BOTTOM_ID=34 3/4"; NOZZLE_BOTTOM_RAD=17 3/8"; NOZZLE_HEIGHT=62"; NOZZLE_HEIGHT/7*2=15 1/2"; NOZZLE_SIZE=288"; NOZZLE_TOP_OD=36 1/2"; NOZZLE_TOP_RAD=18 1/4"; NOZZLE_WB/4=12 3/16"; NOZZLE_WB_OD=61"; NOZZLE_WB_RAD=30 1/2"; NOZZLE_WB_RAD-2"=28 1/2"; RO=54 1/2"; RO/2=27 1/4"; RO2/2=27 1/4"; TRANSITION_TOP=104 1/4"; TYPE=12"; Type Comments=Vari-Plume Laboratory Exhaust Mixed-Flow High Pressure Inline Belt Drive With 1X2 Mixing Box With Weather Hoods On Sides; UNIT_HEIGHT=64"; UNIT_HEIGHT*.75=48"; UNIT_OD=51 3/4"; UNIT_RAD+((A/2)+.25")=57 1/8"; UNIT_RAD+((A/2)+.25")+4"=61 1/8"; UNIT_RADIUS=25 7/8"; UNIT_RADIUS*.6=23 9/32"; UNIT_RADIUS+4"=29 7/8"
- 365_QMXHPVP-30H-1X2_Mixing_Box_Ends: (A/2)+.25"=31 1/4"; (A/2)+.5"=-31 1/2"; (A/2)-.5"=-30 1/2"; (A/2)-2"=29"; (NOZZLE_HEIGHT-(NOZZLE_HEIGHT/8*2))/2=29 1/4"; (NOZZLE_WB_OD-NOZZLE_TOP_OD)/2=7 1/8"; -A=-62"; A=62"; A+.5=62 1/2"; A/2=31"; B=175"; B/2=87 1/2"; C=79"; C/2=39 1/2"; DUAL_F=159"; DUAL_F+1"=160"; DUAL_G=158"; E=60 3/4"; GA=3/32"; LONG_RO=151 3/4"; LONG_RO/2=75 7/8"; MB_A=82"; MB_HT=59 11/16"; MB_HT+.25"=59 15/16"; MB_HT-2.75"=56 15/16"; MB_HT/2=29 27/32"; Model=QMXHPVP-1X2_Mixing Box_Sides; NOZZLE_BOTTOM_ID=42 1/2"; NOZZLE_BOTTOM_RAD=21 1/4"; NOZZLE_HEIGHT=78"; NOZZLE_HEIGHT/7*2=19 1/2"; NOZZLE_SIZE=360"; NOZZLE_TOP_OD=45 1/2"; NOZZLE_TOP_RAD=22 3/4"; NOZZLE_WB/4=14 13/16"; NOZZLE_WB_OD=74"; NOZZLE_WB_RAD=37"; NOZZLE_WB_RAD-2"=35"; RO=54 1/2"; RO/2=27 1/4"; RO2/2=27 1/4"; TRANSITION_TOP=89 1/2"; TYPE=12"; Type Comments=Vari-Plume Laboratory Exhaust Mixed-Flow High Pressure Inline Belt Drive With 1X2 Mixing Box With Weather Hoods On Sides; UNIT_HEIGHT=64"; UNIT_HEIGHT*.75=48"; UNIT_OD=51 3/4"; UNIT_RAD+((A/2)+.25")=57 1/8"; UNIT_RAD+((A/2)+.25")+4"=61 1/8"; UNIT_RADIUS=25 7/8"; UNIT_RADIUS*.6=23 9/32"; UNIT_RADIUS+4"=29 7/8"
- 365_QMXHPVP-30L-1X2_Mixing_Box_Ends: (A/2)+.25"=31 1/4"; (A/2)+.5"=-31 1/2"; (A/2)-.5"=-30 1/2"; (A/2)-2"=29"; (NOZZLE_HEIGHT-(NOZZLE_HEIGHT/8*2))/2=29 1/4"; (NOZZLE_WB_OD-NOZZLE_TOP_OD)/2=7 1/8"; -A=-62"; A=62"; A+.5=62 1/2"; A/2=31"; B=175"; B/2=87 1/2"; C=79"; C/2=39 1/2"; DUAL_F=159"; DUAL_F+1"=160"; DUAL_G=158"; E=60 3/4"; GA=3/32"; LONG_RO=151 3/4"; LONG_RO/2=75 7/8"; MB_A=82"; MB_HT=59 11/16"; MB_HT+.25"=59 15/16"; MB_HT-2.75"=56 15/16"; MB_HT/2=29 27/32"; Model=QMXHPVP-1X2_Mixing Box_Sides; NOZZLE_BOTTOM_ID=42 1/2"; NOZZLE_BOTTOM_RAD=21 1/4"; NOZZLE_HEIGHT=78"; NOZZLE_HEIGHT/7*2=19 1/2"; NOZZLE_SIZE=360"; NOZZLE_TOP_OD=45 1/2"; NOZZLE_TOP_RAD=22 3/4"; NOZZLE_WB/4=14 13/16"; NOZZLE_WB_OD=74"; NOZZLE_WB_RAD=37"; NOZZLE_WB_RAD-2"=35"; RO=54 1/2"; RO/2=27 1/4"; RO2/2=27 1/4"; TRANSITION_TOP=89 1/2"; TYPE=12"; Type Comments=Vari-Plume Laboratory Exhaust Mixed-Flow High Pressure Inline Belt Drive With 1X2 Mixing Box With Weather Hoods On Sides; UNIT_HEIGHT=64"; UNIT_HEIGHT*.75=48"; UNIT_OD=51 3/4"; UNIT_RAD+((A/2)+.25")=57 1/8"; UNIT_RAD+((A/2)+.25")+4"=61 1/8"; UNIT_RADIUS=25 7/8"; UNIT_RADIUS*.6=23 9/32"; UNIT_RADIUS+4"=29 7/8"
- 365_QMXVP-36H-1X2_Mixing_Box_Ends: (A/2)+.25"=31 1/4"; (A/2)+.5"=-31 1/2"; (A/2)-.5"=-30 1/2"; (A/2)-2"=29"; (NOZZLE_HEIGHT-(NOZZLE_HEIGHT/8*2))/2=35 5/8"; (NOZZLE_WB_OD-NOZZLE_TOP_OD)/2=8"; -A=-62"; A=62"; A+.5=62 1/2"; A/2=31"; B=175"; B/2=87 1/2"; C=79"; C/2=39 1/2"; DUAL_F=159"; DUAL_F+1"=160"; DUAL_G=158"; E=60 3/4"; GA=3/32"; LONG_RO=151 3/4"; LONG_RO/2=75 7/8"; MB_A=82"; MB_HT=59 11/16"; MB_HT+.25"=59 15/16"; MB_HT-2.75"=56 15/16"; MB_HT/2=29 27/32"; Model=QMXVP-1X2_Mixing Box_Sides; NOZZLE_BOTTOM_ID=51 3/4"; NOZZLE_BOTTOM_RAD=25 7/8"; NOZZLE_HEIGHT=95"; NOZZLE_HEIGHT/7*2=23 3/4"; NOZZLE_SIZE=432"; NOZZLE_TOP_OD=58"; NOZZLE_TOP_RAD=29"; NOZZLE_WB/4=18"; NOZZLE_WB_OD=90"; NOZZLE_WB_RAD=45"; NOZZLE_WB_RAD-2"=43"; RO=54 1/2"; RO/2=27 1/4"; RO2/2=27 1/4"; TRANSITION_TOP=78 1/4"; TYPE=0"; Type Comments=Vari-Plume Laboratory Exhaust Mixed-Flow Inline Belt Drive With 1X2 Mixing Box With Weather Hoods On Sides; UNIT_HEIGHT=64"; UNIT_HEIGHT*.75=48"; UNIT_OD=51 3/4"; UNIT_RAD+((A/2)+.25")=57 1/8"; UNIT_RAD+((A/2)+.25")+4"=61 1/8"; UNIT_RADIUS=25 7/8"; UNIT_RADIUS*.6=23 9/32"; UNIT_RADIUS+4"=29 7/8"
- 365_QMXHPVP-36L-1X2_Mixing_Box_Ends: (A/2)+.25"=31 1/4"; (A/2)+.5"=-31 1/2"; (A/2)-.5"=-30 1/2"; (A/2)-2"=29"; (NOZZLE_HEIGHT-(NOZZLE_HEIGHT/8*2))/2=35 5/8"; (NOZZLE_WB_OD-NOZZLE_TOP_OD)/2=8"; -A=-62"; A=62"; A+.5=62 1/2"; A/2=31"; B=175"; B/2=87 1/2"; C=79"; C/2=39 1/2"; DUAL_F=159"; DUAL_F+1"=160"; DUAL_G=158"; E=60 3/4"; GA=3/32"; LONG_RO=151 3/4"; LONG_RO/2=75 7/8"; MB_A=82"; MB_HT=59 11/16"; MB_HT+.25"=59 15/16"; MB_HT-2.75"=56 15/16"; MB_HT/2=29 27/32"; Model=QMXHPVP-1X2_Mixing Box_Sides; NOZZLE_BOTTOM_ID=51 3/4"; NOZZLE_BOTTOM_RAD=25 7/8"; NOZZLE_HEIGHT=95"; NOZZLE_HEIGHT/7*2=23 3/4"; NOZZLE_SIZE=432"; NOZZLE_TOP_OD=58"; NOZZLE_TOP_RAD=29"; NOZZLE_WB/4=18"; NOZZLE_WB_OD=90"; NOZZLE_WB_RAD=45"; NOZZLE_WB_RAD-2"=43"; RO=54 1/2"; RO/2=27 1/4"; RO2/2=27 1/4"; TRANSITION_TOP=78 1/4"; TYPE=12"; Type Comments=Vari-Plume Laboratory Exhaust Mixed-Flow High Pressure Inline Belt Drive With 1X2 Mixing Box With Weather Hoods On Sides; UNIT_HEIGHT=64"; UNIT_HEIGHT*.75=48"; UNIT_OD=51 3/4"; UNIT_RAD+((A/2)+.25")=57 1/8"; UNIT_RAD+((A/2)+.25")+4"=61 1/8"; UNIT_RADIUS=25 7/8"; UNIT_RADIUS*.6=23 9/32"; UNIT_RADIUS+4"=29 7/8"
- 365_QMXHPVP-36H-1X2_Mixing_Box_Ends: (A/2)+.25"=31 1/4"; (A/2)+.5"=-31 1/2"; (A/2)-.5"=-30 1/2"; (A/2)-2"=29"; (NOZZLE_HEIGHT-(NOZZLE_HEIGHT/8*2))/2=35 5/8"; (NOZZLE_WB_OD-NOZZLE_TOP_OD)/2=8"; -A=-62"; A=62"; A+.5=62 1/2"; A/2=31"; B=175"; B/2=87 1/2"; C=79"; C/2=39 1/2"; DUAL_F=159"; DUAL_F+1"=160"; DUAL_G=158"; E=60 3/4"; GA=3/32"; LONG_RO=151 3/4"; LONG_RO/2=75 7/8"; MB_A=82"; MB_HT=59 11/16"; MB_HT+.25"=59 15/16"; MB_HT-2.75"=56 15/16"; MB_HT/2=29 27/32"; Model=QMXHPVP-1X2_Mixing Box_Sides; NOZZLE_BOTTOM_ID=51 3/4"; NOZZLE_BOTTOM_RAD=25 7/8"; NOZZLE_HEIGHT=95"; NOZZLE_HEIGHT/7*2=23 3/4"; NOZZLE_SIZE=432"; NOZZLE_TOP_OD=58"; NOZZLE_TOP_RAD=29"; NOZZLE_WB/4=18"; NOZZLE_WB_OD=90"; NOZZLE_WB_RAD=45"; NOZZLE_WB_RAD-2"=43"; RO=54 1/2"; RO/2=27 1/4"; RO2/2=27 1/4"; TRANSITION_TOP=78 1/4"; TYPE=12"; Type Comments=Vari-Plume Laboratory Exhaust Mixed-Flow High Pressure Inline Belt Drive With 1X2 Mixing Box With Weather Hoods On Sides; UNIT_HEIGHT=64"; UNIT_HEIGHT*.75=48"; UNIT_OD=51 3/4"; UNIT_RAD+((A/2)+.25")=57 1/8"; UNIT_RAD+((A/2)+.25")+4"=61 1/8"; UNIT_RADIUS=25 7/8"; UNIT_RADIUS*.6=23 9/32"; UNIT_RADIUS+4"=29 7/8"
- 402_QMXHPVP-24H-1X2_Mixing_Box_Ends: (A/2)+.25"=33 3/4"; (A/2)+.5"=-34"; (A/2)-.5"=-33"; (A/2)-2"=31 1/2"; (NOZZLE_HEIGHT-(NOZZLE_HEIGHT/8*2))/2=23 1/4"; (NOZZLE_WB_OD-NOZZLE_TOP_OD)/2=6 1/8"; -A=-67"; A=67"; A+.5=67 1/2"; A/2=33 1/2"; B=183"; B/2=91 1/2"; C=88"; C/2=44"; DUAL_F=164"; DUAL_F+1"=165"; DUAL_G=163"; E=65 3/4"; GA=3/32"; LONG_RO=156 3/4"; LONG_RO/2=78 3/8"; MB_A=90"; MB_HT=65 15/16"; MB_HT+.25"=66 3/16"; MB_HT-2.75"=63 3/16"; MB_HT/2=32 31/32"; Model=QMXHPVP-1X2_Mixing Box_Sides; NOZZLE_BOTTOM_ID=34 3/4"; NOZZLE_BOTTOM_RAD=17 3/8"; NOZZLE_HEIGHT=62"; NOZZLE_HEIGHT/7*2=15 1/2"; NOZZLE_SIZE=288"; NOZZLE_TOP_OD=36 1/2"; NOZZLE_TOP_RAD=18 1/4"; NOZZLE_WB/4=12 3/16"; NOZZLE_WB_OD=61"; NOZZLE_WB_RAD=30 1/2"; NOZZLE_WB_RAD-2"=28 1/2"; RO=59 7/16"; RO/2=29 23/32"; RO2/2=29 23/32"; TRANSITION_TOP=118 3/4"; TYPE=12"; Type Comments=Vari-Plume Laboratory Exhaust Mixed-Flow High Pressure Inline Belt Drive With 1X2 Mixing Box With Weather Hoods On Sides; UNIT_HEIGHT=68 1/2"; UNIT_HEIGHT*.75=51 3/8"; UNIT_OD=56 15/16"; UNIT_RAD+((A/2)+.25")=62 7/32"; UNIT_RAD+((A/2)+.25")+4"=66 7/32"; UNIT_RADIUS=28 15/32"; UNIT_RADIUS*.6=25 5/8"; UNIT_RADIUS+4"=32 15/32"
- 402_QMXHPVP-24L-1X2_Mixing_Box_Ends: (A/2)+.25"=33 3/4"; (A/2)+.5"=-34"; (A/2)-.5"=-33"; (A/2)-2"=31 1/2"; (NOZZLE_HEIGHT-(NOZZLE_HEIGHT/8*2))/2=23 1/4"; (NOZZLE_WB_OD-NOZZLE_TOP_OD)/2=6 1/8"; -A=-67"; A=67"; A+.5=67 1/2"; A/2=33 1/2"; B=183"; B/2=91 1/2"; C=88"; C/2=44"; DUAL_F=164"; DUAL_F+1"=165"; DUAL_G=163"; E=65 3/4"; GA=3/32"; LONG_RO=156 3/4"; LONG_RO/2=78 3/8"; MB_A=90"; MB_HT=65 15/16"; MB_HT+.25"=66 3/16"; MB_HT-2.75"=63 3/16"; MB_HT/2=32 31/32"; Model=QMXHPVP-1X2_Mixing Box_Sides; NOZZLE_BOTTOM_ID=34 3/4"; NOZZLE_BOTTOM_RAD=17 3/8"; NOZZLE_HEIGHT=62"; NOZZLE_HEIGHT/7*2=15 1/2"; NOZZLE_SIZE=288"; NOZZLE_TOP_OD=36 1/2"; NOZZLE_TOP_RAD=18 1/4"; NOZZLE_WB/4=12 3/16"; NOZZLE_WB_OD=61"; NOZZLE_WB_RAD=30 1/2"; NOZZLE_WB_RAD-2"=28 1/2"; RO=59 7/16"; RO/2=29 23/32"; RO2/2=29 23/32"; TRANSITION_TOP=118 3/4"; TYPE=12"; Type Comments=Vari-Plume Laboratory Exhaust Mixed-Flow High Pressure Inline Belt Drive With 1X2 Mixing Box With Weather Hoods On Sides; UNIT_HEIGHT=68 1/2"; UNIT_HEIGHT*.75=51 3/8"; UNIT_OD=56 15/16"; UNIT_RAD+((A/2)+.25")=62 7/32"; UNIT_RAD+((A/2)+.25")+4"=66 7/32"; UNIT_RADIUS=28 15/32"; UNIT_RADIUS*.6=25 5/8"; UNIT_RADIUS+4"=32 15/32"
- 402_QMXHPVP-30H-1X2_Mixing_Box_Ends: (A/2)+.25"=33 3/4"; (A/2)+.5"=-34"; (A/2)-.5"=-33"; (A/2)-2"=31 1/2"; (NOZZLE_HEIGHT-(NOZZLE_HEIGHT/8*2))/2=29 1/4"; (NOZZLE_WB_OD-NOZZLE_TOP_OD)/2=7 1/8"; -A=-67"; A=67"; A+.5=67 1/2"; A/2=33 1/2"; B=183"; B/2=91 1/2"; C=88"; C/2=44"; DUAL_F=164"; DUAL_F+1"=165"; DUAL_G=163"; E=65 3/4"; GA=3/32"; LONG_RO=156 3/4"; LONG_RO/2=78 3/8"; MB_A=90"; MB_HT=65 15/16"; MB_HT+.25"=66 3/16"; MB_HT-2.75"=63 3/16"; MB_HT/2=32 31/32"; Model=QMXHPVP-1X2_Mixing Box_Sides; NOZZLE_BOTTOM_ID=42 1/2"; NOZZLE_BOTTOM_RAD=21 1/4"; NOZZLE_HEIGHT=78"; NOZZLE_HEIGHT/7*2=19 1/2"; NOZZLE_SIZE=360"; NOZZLE_TOP_OD=45 1/2"; NOZZLE_TOP_RAD=22 3/4"; NOZZLE_WB/4=14 13/16"; NOZZLE_WB_OD=74"; NOZZLE_WB_RAD=37"; NOZZLE_WB_RAD-2"=35"; RO=59 7/16"; RO/2=29 23/32"; RO2/2=29 23/32"; TRANSITION_TOP=103 3/4"; TYPE=12"; Type Comments=Vari-Plume Laboratory Exhaust Mixed-Flow High Pressure Inline Belt Drive With 1X2 Mixing Box With Weather Hoods On Sides; UNIT_HEIGHT=68 1/2"; UNIT_HEIGHT*.75=51 3/8"; UNIT_OD=56 15/16"; UNIT_RAD+((A/2)+.25")=62 7/32"; UNIT_RAD+((A/2)+.25")+4"=66 7/32"; UNIT_RADIUS=28 15/32"; UNIT_RADIUS*.6=25 5/8"; UNIT_RADIUS+4"=32 15/32"
- 402_QMXHPVP-30L-1X2_Mixing_Box_Ends: (A/2)+.25"=33 3/4"; (A/2)+.5"=-34"; (A/2)-.5"=-33"; (A/2)-2"=31 1/2"; (NOZZLE_HEIGHT-(NOZZLE_HEIGHT/8*2))/2=29 1/4"; (NOZZLE_WB_OD-NOZZLE_TOP_OD)/2=7 1/8"; -A=-67"; A=67"; A+.5=67 1/2"; A/2=33 1/2"; B=183"; B/2=91 1/2"; C=88"; C/2=44"; DUAL_F=164"; DUAL_F+1"=165"; DUAL_G=163"; E=65 3/4"; GA=3/32"; LONG_RO=156 3/4"; LONG_RO/2=78 3/8"; MB_A=90"; MB_HT=65 15/16"; MB_HT+.25"=66 3/16"; MB_HT-2.75"=63 3/16"; MB_HT/2=32 31/32"; Model=QMXHPVP-1X2_Mixing Box_Sides; NOZZLE_BOTTOM_ID=42 1/2"; NOZZLE_BOTTOM_RAD=21 1/4"; NOZZLE_HEIGHT=78"; NOZZLE_HEIGHT/7*2=19 1/2"; NOZZLE_SIZE=360"; NOZZLE_TOP_OD=45 1/2"; NOZZLE_TOP_RAD=22 3/4"; NOZZLE_WB/4=14 13/16"; NOZZLE_WB_OD=74"; NOZZLE_WB_RAD=37"; NOZZLE_WB_RAD-2"=35"; RO=59 7/16"; RO/2=29 23/32"; RO2/2=29 23/32"; TRANSITION_TOP=103 3/4"; TYPE=12"; Type Comments=Vari-Plume Laboratory Exhaust Mixed-Flow High Pressure Inline Belt Drive With 1X2 Mixing Box With Weather Hoods On Sides; UNIT_HEIGHT=68 1/2"; UNIT_HEIGHT*.75=51 3/8"; UNIT_OD=56 15/16"; UNIT_RAD+((A/2)+.25")=62 7/32"; UNIT_RAD+((A/2)+.25")+4"=66 7/32"; UNIT_RADIUS=28 15/32"; UNIT_RADIUS*.6=25 5/8"; UNIT_RADIUS+4"=32 15/32"
- 402_QMXHPVP-36H-1X2_Mixing_Box_Ends: (A/2)+.25"=33 3/4"; (A/2)+.5"=-34"; (A/2)-.5"=-33"; (A/2)-2"=31 1/2"; (NOZZLE_HEIGHT-(NOZZLE_HEIGHT/8*2))/2=35 5/8"; (NOZZLE_WB_OD-NOZZLE_TOP_OD)/2=8"; -A=-67"; A=67"; A+.5=67 1/2"; A/2=33 1/2"; B=183"; B/2=91 1/2"; C=88"; C/2=44"; DUAL_F=164"; DUAL_F+1"=165"; DUAL_G=163"; E=65 3/4"; GA=3/32"; LONG_RO=156 3/4"; LONG_RO/2=78 3/8"; MB_A=90"; MB_HT=65 15/16"; MB_HT+.25"=66 3/16"; MB_HT-2.75"=63 3/16"; MB_HT/2=32 31/32"; Model=QMXHPVP-1X2_Mixing Box_Sides; NOZZLE_BOTTOM_ID=51 3/4"; NOZZLE_BOTTOM_RAD=25 7/8"; NOZZLE_HEIGHT=95"; NOZZLE_HEIGHT/7*2=23 3/4"; NOZZLE_SIZE=432"; NOZZLE_TOP_OD=58"; NOZZLE_TOP_RAD=29"; NOZZLE_WB/4=18"; NOZZLE_WB_OD=90"; NOZZLE_WB_RAD=45"; NOZZLE_WB_RAD-2"=43"; RO=59 7/16"; RO/2=29 23/32"; RO2/2=29 23/32"; TRANSITION_TOP=86 3/4"; TYPE=12"; Type Comments=Vari-Plume Laboratory Exhaust Mixed-Flow High Pressure Inline Belt Drive With 1X2 Mixing Box With Weather Hoods On Sides; UNIT_HEIGHT=68 1/2"; UNIT_HEIGHT*.75=51 3/8"; UNIT_OD=56 15/16"; UNIT_RAD+((A/2)+.25")=62 7/32"; UNIT_RAD+((A/2)+.25")+4"=66 7/32"; UNIT_RADIUS=28 15/32"; UNIT_RADIUS*.6=25 5/8"; UNIT_RADIUS+4"=32 15/32"
- 402_QMXHPVP-36L-1X2_Mixing_Box_Ends: (A/2)+.25"=33 3/4"; (A/2)+.5"=-34"; (A/2)-.5"=-33"; (A/2)-2"=31 1/2"; (NOZZLE_HEIGHT-(NOZZLE_HEIGHT/8*2))/2=35 5/8"; (NOZZLE_WB_OD-NOZZLE_TOP_OD)/2=8"; -A=-67"; A=67"; A+.5=67 1/2"; A/2=33 1/2"; B=183"; B/2=91 1/2"; C=88"; C/2=44"; DUAL_F=164"; DUAL_F+1"=165"; DUAL_G=163"; E=65 3/4"; GA=3/32"; LONG_RO=156 3/4"; LONG_RO/2=78 3/8"; MB_A=90"; MB_HT=65 15/16"; MB_HT+.25"=66 3/16"; MB_HT-2.75"=63 3/16"; MB_HT/2=32 31/32"; Model=QMXHPVP-1X2_Mixing Box_Sides; NOZZLE_BOTTOM_ID=51 3/4"; NOZZLE_BOTTOM_RAD=25 7/8"; NOZZLE_HEIGHT=95"; NOZZLE_HEIGHT/7*2=23 3/4"; NOZZLE_SIZE=432"; NOZZLE_TOP_OD=58"; NOZZLE_TOP_RAD=29"; NOZZLE_WB/4=18"; NOZZLE_WB_OD=90"; NOZZLE_WB_RAD=45"; NOZZLE_WB_RAD-2"=43"; RO=59 7/16"; RO/2=29 23/32"; RO2/2=29 23/32"; TRANSITION_TOP=86 3/4"; TYPE=12"; Type Comments=Vari-Plume Laboratory Exhaust Mixed-Flow High Pressure Inline Belt Drive With 1X2 Mixing Box With Weather Hoods On Sides; UNIT_HEIGHT=68 1/2"; UNIT_HEIGHT*.75=51 3/8"; UNIT_OD=56 15/16"; UNIT_RAD+((A/2)+.25")=62 7/32"; UNIT_RAD+((A/2)+.25")+4"=66 7/32"; UNIT_RADIUS=28 15/32"; UNIT_RADIUS*.6=25 5/8"; UNIT_RADIUS+4"=32 15/32"
- 445_QMXHPVP-30H-1X2_Mixing_Box_Ends: (A/2)+.25"=37 1/4"; (A/2)+.5"=-37 1/2"; (A/2)-.5"=-36 1/2"; (A/2)-2"=35"; (NOZZLE_HEIGHT-(NOZZLE_HEIGHT/8*2))/2=29 1/4"; (NOZZLE_WB_OD-NOZZLE_TOP_OD)/2=7 1/8"; -A=-74"; A=74"; A+.5=74 1/2"; A/2=37"; B=201"; B/2=100 1/2"; C=95"; C/2=47 1/2"; DUAL_F=171"; DUAL_F+1"=172"; DUAL_G=170"; E=72 5/8"; GA=3/32"; LONG_RO=163 3/4"; LONG_RO/2=81 7/8"; MB_A=102"; MB_HT=75 11/16"; MB_HT+.25"=75 15/16"; MB_HT-2.75"=72 15/16"; MB_HT/2=37 27/32"; Model=QMXHPVP-1X2_Mixing Box_Sides; NOZZLE_BOTTOM_ID=42 1/2"; NOZZLE_BOTTOM_RAD=21 1/4"; NOZZLE_HEIGHT=78"; NOZZLE_HEIGHT/7*2=19 1/2"; NOZZLE_SIZE=360"; NOZZLE_TOP_OD=45 1/2"; NOZZLE_TOP_RAD=22 3/4"; NOZZLE_WB/4=14 13/16"; NOZZLE_WB_OD=74"; NOZZLE_WB_RAD=37"; NOZZLE_WB_RAD-2"=35"; RO=66 7/16"; RO/2=33 7/32"; RO2/2=33 7/32"; TRANSITION_TOP=121 1/4"; TYPE=12"; Type Comments=Vari-Plume Laboratory Exhaust Mixed-Flow High Pressure Inline Belt Drive With 1X2 Mixing Box With Weather Hoods On Sides; UNIT_HEIGHT=74"; UNIT_HEIGHT*.75=55 1/2"; UNIT_OD=63 1/16"; UNIT_RAD+((A/2)+.25")=68 25/32"; UNIT_RAD+((A/2)+.25")+4"=72 25/32"; UNIT_RADIUS=31 17/32"; UNIT_RADIUS*.6=28 3/8"; UNIT_RADIUS+4"=35 17/32"
- 445_QMXHPVP-30L-1X2_Mixing_Box_Ends: (A/2)+.25"=37 1/4"; (A/2)+.5"=-37 1/2"; (A/2)-.5"=-36 1/2"; (A/2)-2"=35"; (NOZZLE_HEIGHT-(NOZZLE_HEIGHT/8*2))/2=29 1/4"; (NOZZLE_WB_OD-NOZZLE_TOP_OD)/2=7 1/8"; -A=-74"; A=74"; A+.5=74 1/2"; A/2=37"; B=201"; B/2=100 1/2"; C=95"; C/2=47 1/2"; DUAL_F=171"; DUAL_F+1"=172"; DUAL_G=170"; E=72 5/8"; GA=3/32"; LONG_RO=163 3/4"; LONG_RO/2=81 7/8"; MB_A=102"; MB_HT=75 11/16"; MB_HT+.25"=75 15/16"; MB_HT-2.75"=72 15/16"; MB_HT/2=37 27/32"; Model=QMXHPVP-1X2_Mixing Box_Sides; NOZZLE_BOTTOM_ID=42 1/2"; NOZZLE_BOTTOM_RAD=21 1/4"; NOZZLE_HEIGHT=78"; NOZZLE_HEIGHT/7*2=19 1/2"; NOZZLE_SIZE=360"; NOZZLE_TOP_OD=45 1/2"; NOZZLE_TOP_RAD=22 3/4"; NOZZLE_WB/4=14 13/16"; NOZZLE_WB_OD=74"; NOZZLE_WB_RAD=37"; NOZZLE_WB_RAD-2"=35"; RO=66 7/16"; RO/2=33 7/32"; RO2/2=33 7/32"; TRANSITION_TOP=121 1/4"; TYPE=12"; Type Comments=Vari-Plume Laboratory Exhaust Mixed-Flow High Pressure Inline Belt Drive With 1X2 Mixing Box With Weather Hoods On Sides; UNIT_HEIGHT=74"; UNIT_HEIGHT*.75=55 1/2"; UNIT_OD=63 1/16"; UNIT_RAD+((A/2)+.25")=68 25/32"; UNIT_RAD+((A/2)+.25")+4"=72 25/32"; UNIT_RADIUS=31 17/32"; UNIT_RADIUS*.6=28 3/8"; UNIT_RADIUS+4"=35 17/32"
- 445_QMXHPVP-36H-1X2_Mixing_Box_Ends: (A/2)+.25"=37 1/4"; (A/2)+.5"=-37 1/2"; (A/2)-.5"=-36 1/2"; (A/2)-2"=35"; (NOZZLE_HEIGHT-(NOZZLE_HEIGHT/8*2))/2=35 5/8"; (NOZZLE_WB_OD-NOZZLE_TOP_OD)/2=8"; -A=-74"; A=74"; A+.5=74 1/2"; A/2=37"; B=201"; B/2=100 1/2"; C=95"; C/2=47 1/2"; DUAL_F=171"; DUAL_F+1"=172"; DUAL_G=170"; E=72 5/8"; GA=3/32"; LONG_RO=163 3/4"; LONG_RO/2=81 7/8"; MB_A=102"; MB_HT=75 11/16"; MB_HT+.25"=75 15/16"; MB_HT-2.75"=72 15/16"; MB_HT/2=37 27/32"; Model=QMXHPVP-1X2_Mixing Box_Sides; NOZZLE_BOTTOM_ID=51 3/4"; NOZZLE_BOTTOM_RAD=25 7/8"; NOZZLE_HEIGHT=95"; NOZZLE_HEIGHT/7*2=23 3/4"; NOZZLE_SIZE=432"; NOZZLE_TOP_OD=58"; NOZZLE_TOP_RAD=29"; NOZZLE_WB/4=18"; NOZZLE_WB_OD=90"; NOZZLE_WB_RAD=45"; NOZZLE_WB_RAD-2"=43"; RO=66 7/16"; RO/2=33 7/32"; RO2/2=33 7/32"; TRANSITION_TOP=103 1/4"; TYPE=12"; Type Comments=Vari-Plume Laboratory Exhaust Mixed-Flow High Pressure Inline Belt Drive With 1X2 Mixing Box With Weather Hoods On Sides; UNIT_HEIGHT=74"; UNIT_HEIGHT*.75=55 1/2"; UNIT_OD=63 1/16"; UNIT_RAD+((A/2)+.25")=68 25/32"; UNIT_RAD+((A/2)+.25")+4"=72 25/32"; UNIT_RADIUS=31 17/32"; UNIT_RADIUS*.6=28 3/8"; UNIT_RADIUS+4"=35 17/32"
- 445_QMXHPVP-36L-1X2_Mixing_Box_Ends: (A/2)+.25"=37 1/4"; (A/2)+.5"=-37 1/2"; (A/2)-.5"=-36 1/2"; (A/2)-2"=35"; (NOZZLE_HEIGHT-(NOZZLE_HEIGHT/8*2))/2=35 5/8"; (NOZZLE_WB_OD-NOZZLE_TOP_OD)/2=8"; -A=-74"; A=74"; A+.5=74 1/2"; A/2=37"; B=201"; B/2=100 1/2"; C=95"; C/2=47 1/2"; DUAL_F=171"; DUAL_F+1"=172"; DUAL_G=170"; E=72 5/8"; GA=3/32"; LONG_RO=163 3/4"; LONG_RO/2=81 7/8"; MB_A=102"; MB_HT=75 11/16"; MB_HT+.25"=75 15/16"; MB_HT-2.75"=72 15/16"; MB_HT/2=37 27/32"; Model=QMXHPVP-1X2_Mixing Box_Sides; NOZZLE_BOTTOM_ID=51 3/4"; NOZZLE_BOTTOM_RAD=25 7/8"; NOZZLE_HEIGHT=95"; NOZZLE_HEIGHT/7*2=23 3/4"; NOZZLE_SIZE=432"; NOZZLE_TOP_OD=58"; NOZZLE_TOP_RAD=29"; NOZZLE_WB/4=18"; NOZZLE_WB_OD=90"; NOZZLE_WB_RAD=45"; NOZZLE_WB_RAD-2"=43"; RO=66 7/16"; RO/2=33 7/32"; RO2/2=33 7/32"; TRANSITION_TOP=103 1/4"; TYPE=12"; Type Comments=Vari-Plume Laboratory Exhaust Mixed-Flow High Pressure Inline Belt Drive With 1X2 Mixing Box With Weather Hoods On Sides; UNIT_HEIGHT=74"; UNIT_HEIGHT*.75=55 1/2"; UNIT_OD=63 1/16"; UNIT_RAD+((A/2)+.25")=68 25/32"; UNIT_RAD+((A/2)+.25")+4"=72 25/32"; UNIT_RADIUS=31 17/32"; UNIT_RADIUS*.6=28 3/8"; UNIT_RADIUS+4"=35 17/32"
- 490_QMXHPVP-30H-1X2_Mixing_Box_Ends: (A/2)+.25"=40 1/4"; (A/2)+.5"=-40 1/2"; (A/2)-.5"=-39 1/2"; (A/2)-2"=38"; (NOZZLE_HEIGHT-(NOZZLE_HEIGHT/8*2))/2=29 1/4"; (NOZZLE_WB_OD-NOZZLE_TOP_OD)/2=7 1/8"; -A=-80"; A=80"; A+.5=80 1/2"; A/2=40"; B=219"; B/2=109 1/2"; C=103"; C/2=51 1/2"; DUAL_F=192"; DUAL_F+1"=193"; DUAL_G=191"; E=78 1/2"; GA=1/8"; LONG_RO=184 3/4"; LONG_RO/2=92 3/8"; MB_A=113"; MB_HT=86 15/16"; MB_HT+.25"=87 3/16"; MB_HT-2.75"=84 3/16"; MB_HT/2=43 15/32"; Model=QMXHPVP-1X2_Mixing Box_Sides; NOZZLE_BOTTOM_ID=42 1/2"; NOZZLE_BOTTOM_RAD=21 1/4"; NOZZLE_HEIGHT=78"; NOZZLE_HEIGHT/7*2=19 1/2"; NOZZLE_SIZE=360"; NOZZLE_TOP_OD=45 1/2"; NOZZLE_TOP_RAD=22 3/4"; NOZZLE_WB/4=14 13/16"; NOZZLE_WB_OD=74"; NOZZLE_WB_RAD=37"; NOZZLE_WB_RAD-2"=35"; RO=72 1/4"; RO/2=36 1/8"; RO2/2=36 1/8"; TRANSITION_TOP=139 3/4"; TYPE=12"; Type Comments=Vari-Plume Laboratory Exhaust Mixed-Flow High Pressure Inline Belt Drive With 1X2 Mixing Box With Weather Hoods On Sides; UNIT_HEIGHT=80 1/2"; UNIT_HEIGHT*.75=60 3/8"; UNIT_OD=69 3/8"; UNIT_RAD+((A/2)+.25")=74 15/16"; UNIT_RAD+((A/2)+.25")+4"=78 15/16"; UNIT_RADIUS=34 11/16"; UNIT_RADIUS*.6=31 7/32"; UNIT_RADIUS+4"=38 11/16"
- 490_QMXHPVP-30L-1X2_Mixing_Box_Ends: (A/2)+.25"=40 1/4"; (A/2)+.5"=-40 1/2"; (A/2)-.5"=-39 1/2"; (A/2)-2"=38"; (NOZZLE_HEIGHT-(NOZZLE_HEIGHT/8*2))/2=29 1/4"; (NOZZLE_WB_OD-NOZZLE_TOP_OD)/2=7 1/8"; -A=-80"; A=80"; A+.5=80 1/2"; A/2=40"; B=219"; B/2=109 1/2"; C=103"; C/2=51 1/2"; DUAL_F=192"; DUAL_F+1"=193"; DUAL_G=191"; E=78 1/2"; GA=1/8"; LONG_RO=184 3/4"; LONG_RO/2=92 3/8"; MB_A=113"; MB_HT=86 15/16"; MB_HT+.25"=87 3/16"; MB_HT-2.75"=84 3/16"; MB_HT/2=43 15/32"; Model=QMXHPVP-1X2_Mixing Box_Sides; NOZZLE_BOTTOM_ID=42 1/2"; NOZZLE_BOTTOM_RAD=21 1/4"; NOZZLE_HEIGHT=78"; NOZZLE_HEIGHT/7*2=19 1/2"; NOZZLE_SIZE=360"; NOZZLE_TOP_OD=45 1/2"; NOZZLE_TOP_RAD=22 3/4"; NOZZLE_WB/4=14 13/16"; NOZZLE_WB_OD=74"; NOZZLE_WB_RAD=37"; NOZZLE_WB_RAD-2"=35"; RO=72 1/4"; RO/2=36 1/8"; RO2/2=36 1/8"; TRANSITION_TOP=139 3/4"; TYPE=12"; Type Comments=Vari-Plume Laboratory Exhaust Mixed-Flow High Pressure Inline Belt Drive With 1X2 Mixing Box With Weather Hoods On Sides; UNIT_HEIGHT=80 1/2"; UNIT_HEIGHT*.75=60 3/8"; UNIT_OD=69 3/8"; UNIT_RAD+((A/2)+.25")=74 15/16"; UNIT_RAD+((A/2)+.25")+4"=78 15/16"; UNIT_RADIUS=34 11/16"; UNIT_RADIUS*.6=31 7/32"; UNIT_RADIUS+4"=38 11/16"
- 490_QMXHPVP-36H-1X2_Mixing_Box_Ends: (A/2)+.25"=40 1/4"; (A/2)+.5"=-40 1/2"; (A/2)-.5"=-39 1/2"; (A/2)-2"=38"; (NOZZLE_HEIGHT-(NOZZLE_HEIGHT/8*2))/2=35 5/8"; (NOZZLE_WB_OD-NOZZLE_TOP_OD)/2=8"; -A=-80"; A=80"; A+.5=80 1/2"; A/2=40"; B=219"; B/2=109 1/2"; C=103"; C/2=51 1/2"; DUAL_F=192"; DUAL_F+1"=193"; DUAL_G=191"; E=78 1/2"; GA=1/8"; LONG_RO=184 3/4"; LONG_RO/2=92 3/8"; MB_A=113"; MB_HT=86 15/16"; MB_HT+.25"=87 3/16"; MB_HT-2.75"=84 3/16"; MB_HT/2=43 15/32"; Model=QMXHPVP-1X2_Mixing Box_Sides; NOZZLE_BOTTOM_ID=51 3/4"; NOZZLE_BOTTOM_RAD=25 7/8"; NOZZLE_HEIGHT=95"; NOZZLE_HEIGHT/7*2=23 3/4"; NOZZLE_SIZE=432"; NOZZLE_TOP_OD=58"; NOZZLE_TOP_RAD=29"; NOZZLE_WB/4=18"; NOZZLE_WB_OD=90"; NOZZLE_WB_RAD=45"; NOZZLE_WB_RAD-2"=43"; RO=72 1/4"; RO/2=36 1/8"; RO2/2=36 1/8"; TRANSITION_TOP=122 3/4"; TYPE=12"; Type Comments=Vari-Plume Laboratory Exhaust Mixed-Flow High Pressure Inline Belt Drive With 1X2 Mixing Box With Weather Hoods On Sides; UNIT_HEIGHT=80 1/2"; UNIT_HEIGHT*.75=60 3/8"; UNIT_OD=69 3/8"; UNIT_RAD+((A/2)+.25")=74 15/16"; UNIT_RAD+((A/2)+.25")+4"=78 15/16"; UNIT_RADIUS=34 11/16"; UNIT_RADIUS*.6=31 7/32"; UNIT_RADIUS+4"=38 11/16"
- 490_QMXHPVP-36L-1X2_Mixing_Box_Ends: (A/2)+.25"=40 1/4"; (A/2)+.5"=-40 1/2"; (A/2)-.5"=-39 1/2"; (A/2)-2"=38"; (NOZZLE_HEIGHT-(NOZZLE_HEIGHT/8*2))/2=35 5/8"; (NOZZLE_WB_OD-NOZZLE_TOP_OD)/2=8"; -A=-80"; A=80"; A+.5=80 1/2"; A/2=40"; B=219"; B/2=109 1/2"; C=103"; C/2=51 1/2"; DUAL_F=192"; DUAL_F+1"=193"; DUAL_G=191"; E=78 1/2"; GA=1/8"; LONG_RO=184 3/4"; LONG_RO/2=92 3/8"; MB_A=113"; MB_HT=86 15/16"; MB_HT+.25"=87 3/16"; MB_HT-2.75"=84 3/16"; MB_HT/2=43 15/32"; Model=QMXHPVP-1X2_Mixing Box_Sides; NOZZLE_BOTTOM_ID=51 3/4"; NOZZLE_BOTTOM_RAD=25 7/8"; NOZZLE_HEIGHT=95"; NOZZLE_HEIGHT/7*2=23 3/4"; NOZZLE_SIZE=432"; NOZZLE_TOP_OD=58"; NOZZLE_TOP_RAD=29"; NOZZLE_WB/4=18"; NOZZLE_WB_OD=90"; NOZZLE_WB_RAD=45"; NOZZLE_WB_RAD-2"=43"; RO=72 1/4"; RO/2=36 1/8"; RO2/2=36 1/8"; TRANSITION_TOP=122 3/4"; TYPE=12"; Type Comments=Vari-Plume Laboratory Exhaust Mixed-Flow High Pressure Inline Belt Drive With 1X2 Mixing Box With Weather Hoods On Sides; UNIT_HEIGHT=80 1/2"; UNIT_HEIGHT*.75=60 3/8"; UNIT_OD=69 3/8"; UNIT_RAD+((A/2)+.25")=74 15/16"; UNIT_RAD+((A/2)+.25")+4"=78 15/16"; UNIT_RADIUS=34 11/16"; UNIT_RADIUS*.6=31 7/32"; UNIT_RADIUS+4"=38 11/16"
- 540_QMXHPVP-36H-1X2_Mixing_Box_Ends: (A/2)+.25"=45 1/4"; (A/2)+.5"=-45 1/2"; (A/2)-.5"=-44 1/2"; (A/2)-2"=43"; (NOZZLE_HEIGHT-(NOZZLE_HEIGHT/8*2))/2=35 5/8"; (NOZZLE_WB_OD-NOZZLE_TOP_OD)/2=8"; -A=-90"; A=90"; A+.5=90 1/2"; A/2=45"; B=239"; B/2=119 1/2"; C=111"; C/2=55 1/2"; DUAL_F=202"; DUAL_F+1"=203"; DUAL_G=200 7/8"; E=85 3/8"; GA=1/8"; LONG_RO=194 5/8"; LONG_RO/2=97 5/16"; MB_A=126"; MB_HT=99 11/16"; MB_HT+.25"=99 15/16"; MB_HT-2.75"=96 15/16"; MB_HT/2=49 27/32"; Model=QMXHPVP-1X2_Mixing Box_Sides; NOZZLE_BOTTOM_ID=51 3/4"; NOZZLE_BOTTOM_RAD=25 7/8"; NOZZLE_HEIGHT=95"; NOZZLE_HEIGHT/7*2=23 3/4"; NOZZLE_SIZE=432"; NOZZLE_TOP_OD=58"; NOZZLE_TOP_RAD=29"; NOZZLE_WB/4=18"; NOZZLE_WB_OD=90"; NOZZLE_WB_RAD=45"; NOZZLE_WB_RAD-2"=43"; RO=79 1/8"; RO/2=39 9/16"; RO2/2=41"; TRANSITION_TOP=142 1/4"; TYPE=12"; Type Comments=Vari-Plume Laboratory Exhaust Mixed-Flow High Pressure Inline Belt Drive With 1X2 Mixing Box With Weather Hoods On Sides; UNIT_HEIGHT=87"; UNIT_HEIGHT*.75=65 1/4"; UNIT_OD=76 7/16"; UNIT_RAD+((A/2)+.25")=83 15/32"; UNIT_RAD+((A/2)+.25")+4"=87 15/32"; UNIT_RADIUS=38 7/32"; UNIT_RADIUS*.6=34 13/32"; UNIT_RADIUS+4"=42 7/32"
- 540_QMXHPVP-36L-1X2_Mixing_Box_Ends: (A/2)+.25"=45 1/4"; (A/2)+.5"=-45 1/2"; (A/2)-.5"=-44 1/2"; (A/2)-2"=43"; (NOZZLE_HEIGHT-(NOZZLE_HEIGHT/8*2))/2=35 5/8"; (NOZZLE_WB_OD-NOZZLE_TOP_OD)/2=8"; -A=-90"; A=90"; A+.5=90 1/2"; A/2=45"; B=239"; B/2=119 1/2"; C=111"; C/2=55 1/2"; DUAL_F=202"; DUAL_F+1"=203"; DUAL_G=200 7/8"; E=85 3/8"; GA=1/8"; LONG_RO=194 5/8"; LONG_RO/2=97 5/16"; MB_A=126"; MB_HT=99 11/16"; MB_HT+.25"=99 15/16"; MB_HT-2.75"=96 15/16"; MB_HT/2=49 27/32"; Model=QMXHPVP-1X2_Mixing Box_Sides; NOZZLE_BOTTOM_ID=51 3/4"; NOZZLE_BOTTOM_RAD=25 7/8"; NOZZLE_HEIGHT=95"; NOZZLE_HEIGHT/7*2=23 3/4"; NOZZLE_SIZE=432"; NOZZLE_TOP_OD=58"; NOZZLE_TOP_RAD=29"; NOZZLE_WB/4=18"; NOZZLE_WB_OD=90"; NOZZLE_WB_RAD=45"; NOZZLE_WB_RAD-2"=43"; RO=79 1/8"; RO/2=39 9/16"; RO2/2=41"; TRANSITION_TOP=142 1/4"; TYPE=12"; Type Comments=Vari-Plume Laboratory Exhaust Mixed-Flow High Pressure Inline Belt Drive With 1X2 Mixing Box With Weather Hoods On Sides; UNIT_HEIGHT=87"; UNIT_HEIGHT*.75=65 1/4"; UNIT_OD=76 7/16"; UNIT_RAD+((A/2)+.25")=83 15/32"; UNIT_RAD+((A/2)+.25")+4"=87 15/32"; UNIT_RADIUS=38 7/32"; UNIT_RADIUS*.6=34 13/32"; UNIT_RADIUS+4"=42 7/32"
- 540_QMXHPVP-49H-1X2_Mixing_Box_Ends: (A/2)+.25"=45 1/4"; (A/2)+.5"=-45 1/2"; (A/2)-.5"=-44 1/2"; (A/2)-2"=43"; (NOZZLE_HEIGHT-(NOZZLE_HEIGHT/8*2))/2=41 1/4"; (NOZZLE_WB_OD-NOZZLE_TOP_OD)/2=6 1/4"; -A=-90"; A=90"; A+.5=90 1/2"; A/2=45"; B=239"; B/2=119 1/2"; C=111"; C/2=55 1/2"; DUAL_F=202"; DUAL_F+1"=203"; DUAL_G=200 7/8"; E=85 3/8"; GA=1/8"; LONG_RO=194 5/8"; LONG_RO/2=97 5/16"; MB_A=126"; MB_HT=99 11/16"; MB_HT+.25"=99 15/16"; MB_HT-2.75"=96 15/16"; MB_HT/2=49 27/32"; Model=QMXHPVP-1X2_Mixing Box_Sides; NOZZLE_BOTTOM_ID=69 3/8"; NOZZLE_BOTTOM_RAD=34 11/16"; NOZZLE_HEIGHT=110"; NOZZLE_HEIGHT/7*2=27 1/2"; NOZZLE_SIZE=588"; NOZZLE_TOP_OD=76"; NOZZLE_TOP_RAD=38"; NOZZLE_WB/4=20 3/16"; NOZZLE_WB_OD=101"; NOZZLE_WB_RAD=50 1/2"; NOZZLE_WB_RAD-2"=48 1/2"; RO=79 1/8"; RO/2=39 9/16"; RO2/2=41"; TRANSITION_TOP=121 1/4"; TYPE=12"; Type Comments=Vari-Plume Laboratory Exhaust Mixed-Flow High Pressure Inline Belt Drive With 1X2 Mixing Box With Weather Hoods On Sides; UNIT_HEIGHT=87"; UNIT_HEIGHT*.75=65 1/4"; UNIT_OD=76 7/16"; UNIT_RAD+((A/2)+.25")=83 15/32"; UNIT_RAD+((A/2)+.25")+4"=87 15/32"; UNIT_RADIUS=38 7/32"; UNIT_RADIUS*.6=34 13/32"; UNIT_RADIUS+4"=42 7/32"
- 540_QMXHPVP-49L-1X2_Mixing_Box_Ends: (A/2)+.25"=45 1/4"; (A/2)+.5"=-45 1/2"; (A/2)-.5"=-44 1/2"; (A/2)-2"=43"; (NOZZLE_HEIGHT-(NOZZLE_HEIGHT/8*2))/2=41 1/4"; (NOZZLE_WB_OD-NOZZLE_TOP_OD)/2=6 1/4"; -A=-90"; A=90"; A+.5=90 1/2"; A/2=45"; B=239"; B/2=119 1/2"; C=111"; C/2=55 1/2"; DUAL_F=202"; DUAL_F+1"=203"; DUAL_G=200 7/8"; E=85 3/8"; GA=1/8"; LONG_RO=194 5/8"; LONG_RO/2=97 5/16"; MB_A=126"; MB_HT=99 11/16"; MB_HT+.25"=99 15/16"; MB_HT-2.75"=96 15/16"; MB_HT/2=49 27/32"; Model=QMXHPVP-1X2_Mixing Box_Sides; NOZZLE_BOTTOM_ID=69 3/8"; NOZZLE_BOTTOM_RAD=34 11/16"; NOZZLE_HEIGHT=110"; NOZZLE_HEIGHT/7*2=27 1/2"; NOZZLE_SIZE=588"; NOZZLE_TOP_OD=76"; NOZZLE_TOP_RAD=38"; NOZZLE_WB/4=20 3/16"; NOZZLE_WB_OD=101"; NOZZLE_WB_RAD=50 1/2"; NOZZLE_WB_RAD-2"=48 1/2"; RO=79 1/8"; RO/2=39 9/16"; RO2/2=41"; TRANSITION_TOP=121 1/4"; TYPE=12"; Type Comments=Vari-Plume Laboratory Exhaust Mixed-Flow High Pressure Inline Belt Drive With 1X2 Mixing Box With Weather Hoods On Sides; UNIT_HEIGHT=87"; UNIT_HEIGHT*.75=65 1/4"; UNIT_OD=76 7/16"; UNIT_RAD+((A/2)+.25")=83 15/32"; UNIT_RAD+((A/2)+.25")+4"=87 15/32"; UNIT_RADIUS=38 7/32"; UNIT_RADIUS*.6=34 13/32"; UNIT_RADIUS+4"=42 7/32"
- 600_QMXHPVP-36H-1X2_Mixing_Box_Ends: (A/2)+.25"=50 3/4"; (A/2)+.5"=-51"; (A/2)-.5"=-50"; (A/2)-2"=48 1/2"; (NOZZLE_HEIGHT-(NOZZLE_HEIGHT/8*2))/2=35 5/8"; (NOZZLE_WB_OD-NOZZLE_TOP_OD)/2=8"; -A=-101"; A=101"; A+.5=101 1/2"; A/2=50 1/2"; B=263"; B/2=131 1/2"; C=122"; C/2=61"; DUAL_F=213"; DUAL_F+1"=214"; DUAL_G=211 7/8"; E=94 3/8"; GA=3/16"; LONG_RO=205 5/8"; LONG_RO/2=102 13/16"; MB_A=144"; MB_HT=117 3/16"; MB_HT+.25"=117 7/16"; MB_HT-2.75"=114 7/16"; MB_HT/2=58 19/32"; Model=QMXHPVP-1X2_Mixing Box_Sides; NOZZLE_BOTTOM_ID=51 3/4"; NOZZLE_BOTTOM_RAD=25 7/8"; NOZZLE_HEIGHT=95"; NOZZLE_HEIGHT/7*2=23 3/4"; NOZZLE_SIZE=432"; NOZZLE_TOP_OD=58"; NOZZLE_TOP_RAD=29"; NOZZLE_WB/4=18"; NOZZLE_WB_OD=90"; NOZZLE_WB_RAD=45"; NOZZLE_WB_RAD-2"=43"; RO=88 1/16"; RO/2=44 1/32"; RO2/2=46 1/32"; TRANSITION_TOP=170 3/4"; TYPE=12"; Type Comments=Vari-Plume Laboratory Exhaust Mixed-Flow High Pressure Inline Belt Drive With 1X2 Mixing Box With Weather Hoods On Sides; UNIT_HEIGHT=95 1/2"; UNIT_HEIGHT*.75=71 5/8"; UNIT_OD=84 7/8"; UNIT_RAD+((A/2)+.25")=93 3/16"; UNIT_RAD+((A/2)+.25")+4"=97 3/16"; UNIT_RADIUS=42 7/16"; UNIT_RADIUS*.6=38 3/16"; UNIT_RADIUS+4"=46 7/16"
- 600_QMXHPVP-36L-1X2_Mixing_Box_Ends: (A/2)+.25"=50 3/4"; (A/2)+.5"=-51"; (A/2)-.5"=-50"; (A/2)-2"=48 1/2"; (NOZZLE_HEIGHT-(NOZZLE_HEIGHT/8*2))/2=35 5/8"; (NOZZLE_WB_OD-NOZZLE_TOP_OD)/2=8"; -A=-101"; A=101"; A+.5=101 1/2"; A/2=50 1/2"; B=263"; B/2=131 1/2"; C=122"; C/2=61"; DUAL_F=213"; DUAL_F+1"=214"; DUAL_G=211 7/8"; E=94 3/8"; GA=3/16"; LONG_RO=205 5/8"; LONG_RO/2=102 13/16"; MB_A=144"; MB_HT=117 3/16"; MB_HT+.25"=117 7/16"; MB_HT-2.75"=114 7/16"; MB_HT/2=58 19/32"; Model=QMXHPVP-1X2_Mixing Box_Sides; NOZZLE_BOTTOM_ID=51 3/4"; NOZZLE_BOTTOM_RAD=25 7/8"; NOZZLE_HEIGHT=95"; NOZZLE_HEIGHT/7*2=23 3/4"; NOZZLE_SIZE=432"; NOZZLE_TOP_OD=58"; NOZZLE_TOP_RAD=29"; NOZZLE_WB/4=18"; NOZZLE_WB_OD=90"; NOZZLE_WB_RAD=45"; NOZZLE_WB_RAD-2"=43"; RO=88 1/16"; RO/2=44 1/32"; RO2/2=46 1/32"; TRANSITION_TOP=170 3/4"; TYPE=12"; Type Comments=Vari-Plume Laboratory Exhaust Mixed-Flow High Pressure Inline Belt Drive With 1X2 Mixing Box With Weather Hoods On Sides; UNIT_HEIGHT=95 1/2"; UNIT_HEIGHT*.75=71 5/8"; UNIT_OD=84 7/8"; UNIT_RAD+((A/2)+.25")=93 3/16"; UNIT_RAD+((A/2)+.25")+4"=97 3/16"; UNIT_RADIUS=42 7/16"; UNIT_RADIUS*.6=38 3/16"; UNIT_RADIUS+4"=46 7/16"
- 600_QMXHPVP-49H-1X2_Mixing_Box_Ends: (A/2)+.25"=50 3/4"; (A/2)+.5"=-51"; (A/2)-.5"=-50"; (A/2)-2"=48 1/2"; (NOZZLE_HEIGHT-(NOZZLE_HEIGHT/8*2))/2=41 1/4"; (NOZZLE_WB_OD-NOZZLE_TOP_OD)/2=6 1/4"; -A=-101"; A=101"; A+.5=101 1/2"; A/2=50 1/2"; B=263"; B/2=131 1/2"; C=122"; C/2=61"; DUAL_F=213"; DUAL_F+1"=214"; DUAL_G=211 7/8"; E=94 3/8"; GA=3/16"; LONG_RO=205 5/8"; LONG_RO/2=102 13/16"; MB_A=144"; MB_HT=117 3/16"; MB_HT+.25"=117 7/16"; MB_HT-2.75"=114 7/16"; MB_HT/2=58 19/32"; Model=QMXHPVP-1X2_Mixing Box_Sides; NOZZLE_BOTTOM_ID=69 3/8"; NOZZLE_BOTTOM_RAD=34 11/16"; NOZZLE_HEIGHT=110"; NOZZLE_HEIGHT/7*2=27 1/2"; NOZZLE_SIZE=588"; NOZZLE_TOP_OD=76"; NOZZLE_TOP_RAD=38"; NOZZLE_WB/4=20 3/16"; NOZZLE_WB_OD=101"; NOZZLE_WB_RAD=50 1/2"; NOZZLE_WB_RAD-2"=48 1/2"; RO=88 1/16"; RO/2=44 1/32"; RO2/2=46 1/32"; TRANSITION_TOP=148 3/4"; TYPE=12"; Type Comments=Vari-Plume Laboratory Exhaust Mixed-Flow High Pressure Inline Belt Drive With 1X2 Mixing Box With Weather Hoods On Sides; UNIT_HEIGHT=95 1/2"; UNIT_HEIGHT*.75=71 5/8"; UNIT_OD=84 7/8"; UNIT_RAD+((A/2)+.25")=93 3/16"; UNIT_RAD+((A/2)+.25")+4"=97 3/16"; UNIT_RADIUS=42 7/16"; UNIT_RADIUS*.6=38 3/16"; UNIT_RADIUS+4"=46 7/16"
- 600_QMXHPVP-49L-1X2_Mixing_Box_Ends: (A/2)+.25"=50 3/4"; (A/2)+.5"=-51"; (A/2)-.5"=-50"; (A/2)-2"=48 1/2"; (NOZZLE_HEIGHT-(NOZZLE_HEIGHT/8*2))/2=41 1/4"; (NOZZLE_WB_OD-NOZZLE_TOP_OD)/2=6 1/4"; -A=-101"; A=101"; A+.5=101 1/2"; A/2=50 1/2"; B=263"; B/2=131 1/2"; C=122"; C/2=61"; DUAL_F=213"; DUAL_F+1"=214"; DUAL_G=211 7/8"; E=94 3/8"; GA=3/16"; LONG_RO=205 5/8"; LONG_RO/2=102 13/16"; MB_A=144"; MB_HT=117 3/16"; MB_HT+.25"=117 7/16"; MB_HT-2.75"=114 7/16"; MB_HT/2=58 19/32"; Model=QMXHPVP-1X2_Mixing Box_Sides; NOZZLE_BOTTOM_ID=69 3/8"; NOZZLE_BOTTOM_RAD=34 11/16"; NOZZLE_HEIGHT=110"; NOZZLE_HEIGHT/7*2=27 1/2"; NOZZLE_SIZE=588"; NOZZLE_TOP_OD=76"; NOZZLE_TOP_RAD=38"; NOZZLE_WB/4=20 3/16"; NOZZLE_WB_OD=101"; NOZZLE_WB_RAD=50 1/2"; NOZZLE_WB_RAD-2"=48 1/2"; RO=88 1/16"; RO/2=44 1/32"; RO2/2=46 1/32"; TRANSITION_TOP=148 3/4"; TYPE=12"; Type Comments=Vari-Plume Laboratory Exhaust Mixed-Flow High Pressure Inline Belt Drive With 1X2 Mixing Box With Weather Hoods On Sides; UNIT_HEIGHT=95 1/2"; UNIT_HEIGHT*.75=71 5/8"; UNIT_OD=84 7/8"; UNIT_RAD+((A/2)+.25")=93 3/16"; UNIT_RAD+((A/2)+.25")+4"=97 3/16"; UNIT_RADIUS=42 7/16"; UNIT_RADIUS*.6=38 3/16"; UNIT_RADIUS+4"=46 7/16"
- 90_QMXHPVP-9H-1X2_Mixing_Box_Ends: (A/2)+.25"=14 1/4"; (A/2)+.5"=-14 1/2"; (A/2)-.5"=-13 1/2"; (A/2)-2"=12"; (NOZZLE_HEIGHT-(NOZZLE_HEIGHT/8*2))/2=10 1/2"; (NOZZLE_WB_OD-NOZZLE_TOP_OD)/2=2 3/8"; -A=-28"; A=28"; A+.5=28 1/2"; A/2=14"; B=65"; B/2=32 1/2"; C=30"; C/2=15"; DUAL_F=64"; DUAL_F+1"=65"; DUAL_G=63 5/16"; E=27 3/16"; GA=3/32"; LONG_RO=57 1/16"; LONG_RO/2=28 17/32"; MB_A=34"; MB_HT=29 3/16"; MB_HT+.25"=29 7/16"; MB_HT-2.75"=26 7/16"; MB_HT/2=14 19/32"; Model=QMXHPVP-1X2_Mixing Box_Sides; NOZZLE_BOTTOM_ID=12 13/16"; NOZZLE_BOTTOM_RAD=6 13/32"; NOZZLE_HEIGHT=28"; NOZZLE_HEIGHT/7*2=7"; NOZZLE_SIZE=108"; NOZZLE_TOP_OD=13 1/2"; NOZZLE_TOP_RAD=6 3/4"; NOZZLE_WB/4=4 19/32"; NOZZLE_WB_OD=23"; NOZZLE_WB_RAD=11 1/2"; NOZZLE_WB_RAD-2"=9 1/2"; RO=21"; RO/2=10 1/2"; RO2/2=10 1/2"; TRANSITION_TOP=37 1/16"; TYPE=12"; Type Comments=Vari-Plume Laboratory Exhaust Mixed-Flow High Pressure Inline Belt Drive With 1X2 Mixing Box With Weather Hoods On Sides; UNIT_HEIGHT=19 7/8"; UNIT_HEIGHT*.75=14 29/32"; UNIT_OD=12 13/16"; UNIT_RAD+((A/2)+.25")=20 21/32"; UNIT_RAD+((A/2)+.25")+4"=24 21/32"; UNIT_RADIUS=6 13/32"; UNIT_RADIUS*.6=5 25/32"; UNIT_RADIUS+4"=10 13/32"
- 90_QMXHPVP-9L-1X2_Mixing_Box_Ends: (A/2)+.25"=14 1/4"; (A/2)+.5"=-14 1/2"; (A/2)-.5"=-13 1/2"; (A/2)-2"=12"; (NOZZLE_HEIGHT-(NOZZLE_HEIGHT/8*2))/2=10 1/2"; (NOZZLE_WB_OD-NOZZLE_TOP_OD)/2=2 3/8"; -A=-28"; A=28"; A+.5=28 1/2"; A/2=14"; B=65"; B/2=32 1/2"; C=30"; C/2=15"; DUAL_F=64"; DUAL_F+1"=65"; DUAL_G=63 5/16"; E=27 3/16"; GA=3/32"; LONG_RO=57 1/16"; LONG_RO/2=28 17/32"; MB_A=34"; MB_HT=29 3/16"; MB_HT+.25"=29 7/16"; MB_HT-2.75"=26 7/16"; MB_HT/2=14 19/32"; Model=QMXHPVP-1X2_Mixing Box_Sides; NOZZLE_BOTTOM_ID=12 13/16"; NOZZLE_BOTTOM_RAD=6 13/32"; NOZZLE_HEIGHT=28"; NOZZLE_HEIGHT/7*2=7"; NOZZLE_SIZE=108"; NOZZLE_TOP_OD=13 1/2"; NOZZLE_TOP_RAD=6 3/4"; NOZZLE_WB/4=4 19/32"; NOZZLE_WB_OD=23"; NOZZLE_WB_RAD=11 1/2"; NOZZLE_WB_RAD-2"=9 1/2"; RO=21"; RO/2=10 1/2"; RO2/2=10 1/2"; TRANSITION_TOP=37 1/16"; TYPE=12"; Type Comments=Vari-Plume Laboratory Exhaust Mixed-Flow High Pressure Inline Belt Drive With 1X2 Mixing Box With Weather Hoods On Sides; UNIT_HEIGHT=19 7/8"; UNIT_HEIGHT*.75=14 29/32"; UNIT_OD=12 13/16"; UNIT_RAD+((A/2)+.25")=20 21/32"; UNIT_RAD+((A/2)+.25")+4"=24 21/32"; UNIT_RADIUS=6 13/32"; UNIT_RADIUS*.6=5 25/32"; UNIT_RADIUS+4"=10 13/32"
- 490_QMXVP-49L-1X2_Mixing_Box_Ends: (A/2)+.25"=40 1/4"; (A/2)+.5"=-40 1/2"; (A/2)-.5"=-39 1/2"; (A/2)-2"=38"; (NOZZLE_HEIGHT-(NOZZLE_HEIGHT/8*2))/2=41 1/4"; (NOZZLE_WB_OD-NOZZLE_TOP_OD)/2=6 1/4"; -A=-80"; A=80"; A+.5=80 1/2"; A/2=40"; B=219"; B/2=109 1/2"; C=103"; C/2=51 1/2"; DUAL_F=192"; DUAL_F+1"=193"; DUAL_G=191"; E=78 1/2"; GA=1/8"; LONG_RO=184 3/4"; LONG_RO/2=92 3/8"; MB_A=113"; MB_HT=86 15/16"; MB_HT+.25"=87 3/16"; MB_HT-2.75"=84 3/16"; MB_HT/2=43 15/32"; Model=QMXVP-1X2_Mixing Box_Sides; NOZZLE_BOTTOM_ID=69 3/8"; NOZZLE_BOTTOM_RAD=34 11/16"; NOZZLE_HEIGHT=110"; NOZZLE_HEIGHT/7*2=27 1/2"; NOZZLE_SIZE=588"; NOZZLE_TOP_OD=76"; NOZZLE_TOP_RAD=38"; NOZZLE_WB/4=20 3/16"; NOZZLE_WB_OD=101"; NOZZLE_WB_RAD=50 1/2"; NOZZLE_WB_RAD-2"=48 1/2"; RO=72 1/4"; RO/2=36 1/8"; RO2/2=36 1/8"; TRANSITION_TOP=96 3/4"; TYPE=0"; Type Comments=Vari-Plume Laboratory Exhaust Mixed-Flow Inline Belt Drive With 1X2 Mixing Box With Weather Hoods On Sides; UNIT_HEIGHT=80 1/2"; UNIT_HEIGHT*.75=60 3/8"; UNIT_OD=69 3/8"; UNIT_RAD+((A/2)+.25")=74 15/16"; UNIT_RAD+((A/2)+.25")+4"=78 15/16"; UNIT_RADIUS=34 11/16"; UNIT_RADIUS*.6=31 7/32"; UNIT_RADIUS+4"=38 11/16"
- 490_QMXHPVP-49H-1X2_Mixing_Box_Ends: (A/2)+.25"=40 1/4"; (A/2)+.5"=-40 1/2"; (A/2)-.5"=-39 1/2"; (A/2)-2"=38"; (NOZZLE_HEIGHT-(NOZZLE_HEIGHT/8*2))/2=41 1/4"; (NOZZLE_WB_OD-NOZZLE_TOP_OD)/2=6 1/4"; -A=-80"; A=80"; A+.5=80 1/2"; A/2=40"; B=219"; B/2=109 1/2"; C=103"; C/2=51 1/2"; DUAL_F=192"; DUAL_F+1"=193"; DUAL_G=191"; E=78 1/2"; GA=1/8"; LONG_RO=184 3/4"; LONG_RO/2=92 3/8"; MB_A=113"; MB_HT=86 15/16"; MB_HT+.25"=87 3/16"; MB_HT-2.75"=84 3/16"; MB_HT/2=43 15/32"; Model=QMXHPVP-1X2_Mixing Box_Sides; NOZZLE_BOTTOM_ID=69 3/8"; NOZZLE_BOTTOM_RAD=34 11/16"; NOZZLE_HEIGHT=110"; NOZZLE_HEIGHT/7*2=27 1/2"; NOZZLE_SIZE=588"; NOZZLE_TOP_OD=76"; NOZZLE_TOP_RAD=38"; NOZZLE_WB/4=20 3/16"; NOZZLE_WB_OD=101"; NOZZLE_WB_RAD=50 1/2"; NOZZLE_WB_RAD-2"=48 1/2"; RO=72 1/4"; RO/2=36 1/8"; RO2/2=36 1/8"; TRANSITION_TOP=96 3/4"; TYPE=12"; Type Comments=Vari-Plume Laboratory Exhaust Mixed-Flow High Pressure Inline Belt Drive With 1X2 Mixing Box With Weather Hoods On Sides; UNIT_HEIGHT=80 1/2"; UNIT_HEIGHT*.75=60 3/8"; UNIT_OD=69 3/8"; UNIT_RAD+((A/2)+.25")=74 15/16"; UNIT_RAD+((A/2)+.25")+4"=78 15/16"; UNIT_RADIUS=34 11/16"; UNIT_RADIUS*.6=31 7/32"; UNIT_RADIUS+4"=38 11/16"
- 490_QMXHPVP-49L-1X2_Mixing_Box_Ends: (A/2)+.25"=40 1/4"; (A/2)+.5"=-40 1/2"; (A/2)-.5"=-39 1/2"; (A/2)-2"=38"; (NOZZLE_HEIGHT-(NOZZLE_HEIGHT/8*2))/2=41 1/4"; (NOZZLE_WB_OD-NOZZLE_TOP_OD)/2=6 1/4"; -A=-80"; A=80"; A+.5=80 1/2"; A/2=40"; B=219"; B/2=109 1/2"; C=103"; C/2=51 1/2"; DUAL_F=192"; DUAL_F+1"=193"; DUAL_G=191"; E=78 1/2"; GA=1/8"; LONG_RO=184 3/4"; LONG_RO/2=92 3/8"; MB_A=113"; MB_HT=86 15/16"; MB_HT+.25"=87 3/16"; MB_HT-2.75"=84 3/16"; MB_HT/2=43 15/32"; Model=QMXHPVP-1X2_Mixing Box_Sides; NOZZLE_BOTTOM_ID=69 3/8"; NOZZLE_BOTTOM_RAD=34 11/16"; NOZZLE_HEIGHT=110"; NOZZLE_HEIGHT/7*2=27 1/2"; NOZZLE_SIZE=588"; NOZZLE_TOP_OD=76"; NOZZLE_TOP_RAD=38"; NOZZLE_WB/4=20 3/16"; NOZZLE_WB_OD=101"; NOZZLE_WB_RAD=50 1/2"; NOZZLE_WB_RAD-2"=48 1/2"; RO=72 1/4"; RO/2=36 1/8"; RO2/2=36 1/8"; TRANSITION_TOP=96 3/4"; TYPE=12"; Type Comments=Vari-Plume Laboratory Exhaust Mixed-Flow High Pressure Inline Belt Drive With 1X2 Mixing Box With Weather Hoods On Sides; UNIT_HEIGHT=80 1/2"; UNIT_HEIGHT*.75=60 3/8"; UNIT_OD=69 3/8"; UNIT_RAD+((A/2)+.25")=74 15/16"; UNIT_RAD+((A/2)+.25")+4"=78 15/16"; UNIT_RADIUS=34 11/16"; UNIT_RADIUS*.6=31 7/32"; UNIT_RADIUS+4"=38 11/16"
- 202_QMXHPVP-21L-1X2_Mixing_Box_Ends: (A/2)+.25"=19 1/4"; (A/2)+.5"=-19 1/2"; (A/2)-.5"=-18 1/2"; (A/2)-2"=17"; (NOZZLE_HEIGHT-(NOZZLE_HEIGHT/8*2))/2=19 25/32"; (NOZZLE_WB_OD-NOZZLE_TOP_OD)/2=4 9/16"; -A=-38"; A=38"; A+.5=38 1/2"; A/2=19"; B=104"; B/2=52"; C=50"; C/2=25"; DUAL_F=90"; DUAL_F+1"=91"; DUAL_G=89 1/8"; E=36 15/16"; GA=3/32"; LONG_RO=82 7/8"; LONG_RO/2=41 7/16"; MB_A=49"; MB_HT=41 3/16"; MB_HT+.25"=41 7/16"; MB_HT-2.75"=38 7/16"; MB_HT/2=20 19/32"; Model=QMXHPVP-1X2_Mixing Box_Sides; NOZZLE_BOTTOM_ID=28 3/4"; NOZZLE_BOTTOM_RAD=14 3/8"; NOZZLE_HEIGHT=52 3/4"; NOZZLE_HEIGHT/7*2=13 3/16"; NOZZLE_SIZE=252"; NOZZLE_TOP_OD=30 3/4"; NOZZLE_TOP_RAD=15 3/8"; NOZZLE_WB/4=9 13/16"; NOZZLE_WB_OD=49"; NOZZLE_WB_RAD=24 1/2"; NOZZLE_WB_RAD-2"=22 1/2"; RO=30 3/4"; RO/2=15 3/8"; RO2/2=15 3/8"; TRANSITION_TOP=51 5/8"; TYPE=12"; Type Comments=Vari-Plume Laboratory Exhaust Mixed-Flow High Pressure Inline Belt Drive With 1X2 Mixing Box With Weather Hoods On Sides; UNIT_HEIGHT=37 1/2"; UNIT_HEIGHT*.75=28 1/8"; UNIT_OD=28 3/4"; UNIT_RAD+((A/2)+.25")=33 5/8"; UNIT_RAD+((A/2)+.25")+4"=37 5/8"; UNIT_RADIUS=14 3/8"; UNIT_RADIUS*.6=12 15/16"; UNIT_RADIUS+4"=18 3/8"
- 202_QMXHPVP-21H-1X2_Mixing_Box_Ends: (A/2)+.25"=19 1/4"; (A/2)+.5"=-19 1/2"; (A/2)-.5"=-18 1/2"; (A/2)-2"=17"; (NOZZLE_HEIGHT-(NOZZLE_HEIGHT/8*2))/2=19 25/32"; (NOZZLE_WB_OD-NOZZLE_TOP_OD)/2=4 9/16"; -A=-38"; A=38"; A+.5=38 1/2"; A/2=19"; B=104"; B/2=52"; C=50"; C/2=25"; DUAL_F=90"; DUAL_F+1"=91"; DUAL_G=89 1/8"; E=36 15/16"; GA=3/32"; LONG_RO=82 7/8"; LONG_RO/2=41 7/16"; MB_A=49"; MB_HT=41 3/16"; MB_HT+.25"=41 7/16"; MB_HT-2.75"=38 7/16"; MB_HT/2=20 19/32"; Model=QMXHPVP-1X2_Mixing Box_Sides; NOZZLE_BOTTOM_ID=28 3/4"; NOZZLE_BOTTOM_RAD=14 3/8"; NOZZLE_HEIGHT=52 3/4"; NOZZLE_HEIGHT/7*2=13 3/16"; NOZZLE_SIZE=252"; NOZZLE_TOP_OD=30 3/4"; NOZZLE_TOP_RAD=15 3/8"; NOZZLE_WB/4=9 13/16"; NOZZLE_WB_OD=49"; NOZZLE_WB_RAD=24 1/2"; NOZZLE_WB_RAD-2"=22 1/2"; RO=30 3/4"; RO/2=15 3/8"; RO2/2=15 3/8"; TRANSITION_TOP=51 5/8"; TYPE=12"; Type Comments=Vari-Plume Laboratory Exhaust Mixed-Flow High Pressure Inline Belt Drive With 1X2 Mixing Box With Weather Hoods On Sides; UNIT_HEIGHT=37 1/2"; UNIT_HEIGHT*.75=28 1/8"; UNIT_OD=28 3/4"; UNIT_RAD+((A/2)+.25")=33 5/8"; UNIT_RAD+((A/2)+.25")+4"=37 5/8"; UNIT_RADIUS=14 3/8"; UNIT_RADIUS*.6=12 15/16"; UNIT_RADIUS+4"=18 3/8"
- 202_QMXVP-21H-1X2_Mixing_Box_Ends: (A/2)+.25"=19 1/4"; (A/2)+.5"=-19 1/2"; (A/2)-.5"=-18 1/2"; (A/2)-2"=17"; (NOZZLE_HEIGHT-(NOZZLE_HEIGHT/8*2))/2=19 25/32"; (NOZZLE_WB_OD-NOZZLE_TOP_OD)/2=4 9/16"; -A=-38"; A=38"; A+.5=38 1/2"; A/2=19"; B=104"; B/2=52"; C=50"; C/2=25"; DUAL_F=90"; DUAL_F+1"=91"; DUAL_G=89 1/8"; E=36 15/16"; GA=3/32"; LONG_RO=82 7/8"; LONG_RO/2=41 7/16"; MB_A=49"; MB_HT=41 3/16"; MB_HT+.25"=41 7/16"; MB_HT-2.75"=38 7/16"; MB_HT/2=20 19/32"; Model=QMXVP-1X2_Mixing Box_Sides; NOZZLE_BOTTOM_ID=28 3/4"; NOZZLE_BOTTOM_RAD=14 3/8"; NOZZLE_HEIGHT=52 3/4"; NOZZLE_HEIGHT/7*2=13 3/16"; NOZZLE_SIZE=252"; NOZZLE_TOP_OD=30 3/4"; NOZZLE_TOP_RAD=15 3/8"; NOZZLE_WB/4=9 13/16"; NOZZLE_WB_OD=49"; NOZZLE_WB_RAD=24 1/2"; NOZZLE_WB_RAD-2"=22 1/2"; RO=30 3/4"; RO/2=15 3/8"; RO2/2=15 3/8"; TRANSITION_TOP=51 5/8"; TYPE=0"; Type Comments=Vari-Plume Laboratory Exhaust Mixed-Flow Inline Belt Drive With 1X2 Mixing Box With Weather Hoods On Sides; UNIT_HEIGHT=37 1/2"; UNIT_HEIGHT*.75=28 1/8"; UNIT_OD=28 3/4"; UNIT_RAD+((A/2)+.25")=33 5/8"; UNIT_RAD+((A/2)+.25")+4"=37 5/8"; UNIT_RADIUS=14 3/8"; UNIT_RADIUS*.6=12 15/16"; UNIT_RADIUS+4"=18 3/8"
- 202_QMXVP-21L-1X2_Mixing_Box_Ends: (A/2)+.25"=19 1/4"; (A/2)+.5"=-19 1/2"; (A/2)-.5"=-18 1/2"; (A/2)-2"=17"; (NOZZLE_HEIGHT-(NOZZLE_HEIGHT/8*2))/2=19 25/32"; (NOZZLE_WB_OD-NOZZLE_TOP_OD)/2=4 9/16"; -A=-38"; A=38"; A+.5=38 1/2"; A/2=19"; B=104"; B/2=52"; C=50"; C/2=25"; DUAL_F=90"; DUAL_F+1"=91"; DUAL_G=89 1/8"; E=36 15/16"; GA=3/32"; LONG_RO=82 7/8"; LONG_RO/2=41 7/16"; MB_A=49"; MB_HT=41 3/16"; MB_HT+.25"=41 7/16"; MB_HT-2.75"=38 7/16"; MB_HT/2=20 19/32"; Model=QMXVP-1X2_Mixing Box_Sides; NOZZLE_BOTTOM_ID=28 3/4"; NOZZLE_BOTTOM_RAD=14 3/8"; NOZZLE_HEIGHT=52 3/4"; NOZZLE_HEIGHT/7*2=13 3/16"; NOZZLE_SIZE=252"; NOZZLE_TOP_OD=30 3/4"; NOZZLE_TOP_RAD=15 3/8"; NOZZLE_WB/4=9 13/16"; NOZZLE_WB_OD=49"; NOZZLE_WB_RAD=24 1/2"; NOZZLE_WB_RAD-2"=22 1/2"; RO=30 3/4"; RO/2=15 3/8"; RO2/2=15 3/8"; TRANSITION_TOP=51 5/8"; TYPE=0"; Type Comments=Vari-Plume Laboratory Exhaust Mixed-Flow Inline Belt Drive With 1X2 Mixing Box With Weather Hoods On Sides; UNIT_HEIGHT=37 1/2"; UNIT_HEIGHT*.75=28 1/8"; UNIT_OD=28 3/4"; UNIT_RAD+((A/2)+.25")=33 5/8"; UNIT_RAD+((A/2)+.25")+4"=37 5/8"; UNIT_RADIUS=14 3/8"; UNIT_RADIUS*.6=12 15/16"; UNIT_RADIUS+4"=18 3/8"
- 225_QMXHPVP-21H-1X2_Mixing_Box_Ends: (A/2)+.25"=21 1/4"; (A/2)+.5"=-21 1/2"; (A/2)-.5"=-20 1/2"; (A/2)-2"=19"; (NOZZLE_HEIGHT-(NOZZLE_HEIGHT/8*2))/2=19 25/32"; (NOZZLE_WB_OD-NOZZLE_TOP_OD)/2=4 9/16"; -A=-42"; A=42"; A+.5=42 1/2"; A/2=21"; B=113"; B/2=56 1/2"; C=56"; C/2=28"; DUAL_F=93"; DUAL_F+1"=94"; DUAL_G=92 1/8"; E=40 15/16"; GA=3/32"; LONG_RO=85 7/8"; LONG_RO/2=42 15/16"; MB_A=54"; MB_HT=43 3/16"; MB_HT+.25"=43 7/16"; MB_HT-2.75"=40 7/16"; MB_HT/2=21 19/32"; Model=QMXHPVP-1X2_Mixing Box_Sides; NOZZLE_BOTTOM_ID=28 3/4"; NOZZLE_BOTTOM_RAD=14 3/8"; NOZZLE_HEIGHT=52 3/4"; NOZZLE_HEIGHT/7*2=13 3/16"; NOZZLE_SIZE=252"; NOZZLE_TOP_OD=30 3/4"; NOZZLE_TOP_RAD=15 3/8"; NOZZLE_WB/4=9 13/16"; NOZZLE_WB_OD=49"; NOZZLE_WB_RAD=24 1/2"; NOZZLE_WB_RAD-2"=22 1/2"; RO=34 3/4"; RO/2=17 3/8"; RO2/2=17 3/8"; TRANSITION_TOP=61 1/8"; TYPE=12"; Type Comments=Vari-Plume Laboratory Exhaust Mixed-Flow High Pressure Inline Belt Drive With 1X2 Mixing Box With Weather Hoods On Sides; UNIT_HEIGHT=41"; UNIT_HEIGHT*.75=30 3/4"; UNIT_OD=31 15/16"; UNIT_RAD+((A/2)+.25")=37 7/32"; UNIT_RAD+((A/2)+.25")+4"=41 7/32"; UNIT_RADIUS=15 31/32"; UNIT_RADIUS*.6=14 3/8"; UNIT_RADIUS+4"=19 31/32"
- 225_QMXHPVP-21L-1X2_Mixing_Box_Ends: (A/2)+.25"=21 1/4"; (A/2)+.5"=-21 1/2"; (A/2)-.5"=-20 1/2"; (A/2)-2"=19"; (NOZZLE_HEIGHT-(NOZZLE_HEIGHT/8*2))/2=19 25/32"; (NOZZLE_WB_OD-NOZZLE_TOP_OD)/2=4 9/16"; -A=-42"; A=42"; A+.5=42 1/2"; A/2=21"; B=113"; B/2=56 1/2"; C=56"; C/2=28"; DUAL_F=93"; DUAL_F+1"=94"; DUAL_G=92 1/8"; E=40 15/16"; GA=3/32"; LONG_RO=85 7/8"; LONG_RO/2=42 15/16"; MB_A=54"; MB_HT=43 3/16"; MB_HT+.25"=43 7/16"; MB_HT-2.75"=40 7/16"; MB_HT/2=21 19/32"; Model=QMXHPVP-1X2_Mixing Box_Sides; NOZZLE_BOTTOM_ID=28 3/4"; NOZZLE_BOTTOM_RAD=14 3/8"; NOZZLE_HEIGHT=52 3/4"; NOZZLE_HEIGHT/7*2=13 3/16"; NOZZLE_SIZE=252"; NOZZLE_TOP_OD=30 3/4"; NOZZLE_TOP_RAD=15 3/8"; NOZZLE_WB/4=9 13/16"; NOZZLE_WB_OD=49"; NOZZLE_WB_RAD=24 1/2"; NOZZLE_WB_RAD-2"=22 1/2"; RO=34 3/4"; RO/2=17 3/8"; RO2/2=17 3/8"; TRANSITION_TOP=61 1/8"; TYPE=12"; Type Comments=Vari-Plume Laboratory Exhaust Mixed-Flow High Pressure Inline Belt Drive With 1X2 Mixing Box With Weather Hoods On Sides; UNIT_HEIGHT=41"; UNIT_HEIGHT*.75=30 3/4"; UNIT_OD=31 15/16"; UNIT_RAD+((A/2)+.25")=37 7/32"; UNIT_RAD+((A/2)+.25")+4"=41 7/32"; UNIT_RADIUS=15 31/32"; UNIT_RADIUS*.6=14 3/8"; UNIT_RADIUS+4"=19 31/32"
- 225_QMXVP-21H-1X2_Mixing_Box_Ends: (A/2)+.25"=21 1/4"; (A/2)+.5"=-21 1/2"; (A/2)-.5"=-20 1/2"; (A/2)-2"=19"; (NOZZLE_HEIGHT-(NOZZLE_HEIGHT/8*2))/2=19 25/32"; (NOZZLE_WB_OD-NOZZLE_TOP_OD)/2=4 9/16"; -A=-42"; A=42"; A+.5=42 1/2"; A/2=21"; B=113"; B/2=56 1/2"; C=56"; C/2=28"; DUAL_F=93"; DUAL_F+1"=94"; DUAL_G=92 1/8"; E=40 15/16"; GA=3/32"; LONG_RO=85 7/8"; LONG_RO/2=42 15/16"; MB_A=54"; MB_HT=43 3/16"; MB_HT+.25"=43 7/16"; MB_HT-2.75"=40 7/16"; MB_HT/2=21 19/32"; Model=QMXVP-1X2_Mixing Box_Sides; NOZZLE_BOTTOM_ID=28 3/4"; NOZZLE_BOTTOM_RAD=14 3/8"; NOZZLE_HEIGHT=52 3/4"; NOZZLE_HEIGHT/7*2=13 3/16"; NOZZLE_SIZE=252"; NOZZLE_TOP_OD=30 3/4"; NOZZLE_TOP_RAD=15 3/8"; NOZZLE_WB/4=9 13/16"; NOZZLE_WB_OD=49"; NOZZLE_WB_RAD=24 1/2"; NOZZLE_WB_RAD-2"=22 1/2"; RO=34 3/4"; RO/2=17 3/8"; RO2/2=17 3/8"; TRANSITION_TOP=61 1/8"; TYPE=0"; Type Comments=Vari-Plume Laboratory Exhaust Mixed-Flow Inline Belt Drive With 1X2 Mixing Box With Weather Hoods On Sides; UNIT_HEIGHT=41"; UNIT_HEIGHT*.75=30 3/4"; UNIT_OD=31 15/16"; UNIT_RAD+((A/2)+.25")=37 7/32"; UNIT_RAD+((A/2)+.25")+4"=41 7/32"; UNIT_RADIUS=15 31/32"; UNIT_RADIUS*.6=14 3/8"; UNIT_RADIUS+4"=19 31/32"
- 225_QMXVP-21L-1X2_Mixing_Box_Ends: (A/2)+.25"=21 1/4"; (A/2)+.5"=-21 1/2"; (A/2)-.5"=-20 1/2"; (A/2)-2"=19"; (NOZZLE_HEIGHT-(NOZZLE_HEIGHT/8*2))/2=19 25/32"; (NOZZLE_WB_OD-NOZZLE_TOP_OD)/2=4 9/16"; -A=-42"; A=42"; A+.5=42 1/2"; A/2=21"; B=113"; B/2=56 1/2"; C=56"; C/2=28"; DUAL_F=93"; DUAL_F+1"=94"; DUAL_G=92 1/8"; E=40 15/16"; GA=3/32"; LONG_RO=85 7/8"; LONG_RO/2=42 15/16"; MB_A=54"; MB_HT=43 3/16"; MB_HT+.25"=43 7/16"; MB_HT-2.75"=40 7/16"; MB_HT/2=21 19/32"; Model=QMXVP-1X2_Mixing Box_Sides; NOZZLE_BOTTOM_ID=28 3/4"; NOZZLE_BOTTOM_RAD=14 3/8"; NOZZLE_HEIGHT=52 3/4"; NOZZLE_HEIGHT/7*2=13 3/16"; NOZZLE_SIZE=252"; NOZZLE_TOP_OD=30 3/4"; NOZZLE_TOP_RAD=15 3/8"; NOZZLE_WB/4=9 13/16"; NOZZLE_WB_OD=49"; NOZZLE_WB_RAD=24 1/2"; NOZZLE_WB_RAD-2"=22 1/2"; RO=34 3/4"; RO/2=17 3/8"; RO2/2=17 3/8"; TRANSITION_TOP=61 1/8"; TYPE=0"; Type Comments=Vari-Plume Laboratory Exhaust Mixed-Flow Inline Belt Drive With 1X2 Mixing Box With Weather Hoods On Sides; UNIT_HEIGHT=41"; UNIT_HEIGHT*.75=30 3/4"; UNIT_OD=31 15/16"; UNIT_RAD+((A/2)+.25")=37 7/32"; UNIT_RAD+((A/2)+.25")+4"=41 7/32"; UNIT_RADIUS=15 31/32"; UNIT_RADIUS*.6=14 3/8"; UNIT_RADIUS+4"=19 31/32"
- 245_QMXHPVP-21H-1X2_Mixing_Box_Ends: (A/2)+.25"=22 1/4"; (A/2)+.5"=-22 1/2"; (A/2)-.5"=-21 1/2"; (A/2)-2"=20"; (NOZZLE_HEIGHT-(NOZZLE_HEIGHT/8*2))/2=19 25/32"; (NOZZLE_WB_OD-NOZZLE_TOP_OD)/2=4 9/16"; -A=-44"; A=44"; A+.5=44 1/2"; A/2=22"; B=121"; B/2=60 1/2"; C=59"; C/2=29 1/2"; DUAL_F=108"; DUAL_F+1"=109"; DUAL_G=107 1/8"; E=42 15/16"; GA=3/32"; LONG_RO=100 7/8"; LONG_RO/2=50 7/16"; MB_A=57"; MB_HT=45 7/16"; MB_HT+.25"=45 11/16"; MB_HT-2.75"=42 11/16"; MB_HT/2=22 23/32"; Model=QMXHPVP-1X2_Mixing Box_Sides; NOZZLE_BOTTOM_ID=28 3/4"; NOZZLE_BOTTOM_RAD=14 3/8"; NOZZLE_HEIGHT=52 3/4"; NOZZLE_HEIGHT/7*2=13 3/16"; NOZZLE_SIZE=252"; NOZZLE_TOP_OD=30 3/4"; NOZZLE_TOP_RAD=15 3/8"; NOZZLE_WB/4=9 13/16"; NOZZLE_WB_OD=49"; NOZZLE_WB_RAD=24 1/2"; NOZZLE_WB_RAD-2"=22 1/2"; RO=36 3/4"; RO/2=18 3/8"; RO2/2=18 3/8"; TRANSITION_TOP=69 11/16"; TYPE=12"; Type Comments=Vari-Plume Laboratory Exhaust Mixed-Flow High Pressure Inline Belt Drive With 1X2 Mixing Box With Weather Hoods On Sides; UNIT_HEIGHT=44 1/2"; UNIT_HEIGHT*.75=33 3/8"; UNIT_OD=34 3/4"; UNIT_RAD+((A/2)+.25")=39 5/8"; UNIT_RAD+((A/2)+.25")+4"=43 5/8"; UNIT_RADIUS=17 3/8"; UNIT_RADIUS*.6=15 5/8"; UNIT_RADIUS+4"=21 3/8"
- 245_QMXHPVP-21L-1X2_Mixing_Box_Ends: (A/2)+.25"=22 1/4"; (A/2)+.5"=-22 1/2"; (A/2)-.5"=-21 1/2"; (A/2)-2"=20"; (NOZZLE_HEIGHT-(NOZZLE_HEIGHT/8*2))/2=19 25/32"; (NOZZLE_WB_OD-NOZZLE_TOP_OD)/2=4 9/16"; -A=-44"; A=44"; A+.5=44 1/2"; A/2=22"; B=121"; B/2=60 1/2"; C=59"; C/2=29 1/2"; DUAL_F=108"; DUAL_F+1"=109"; DUAL_G=107 1/8"; E=42 15/16"; GA=3/32"; LONG_RO=100 7/8"; LONG_RO/2=50 7/16"; MB_A=57"; MB_HT=45 7/16"; MB_HT+.25"=45 11/16"; MB_HT-2.75"=42 11/16"; MB_HT/2=22 23/32"; Model=QMXHPVP-1X2_Mixing Box_Sides; NOZZLE_BOTTOM_ID=28 3/4"; NOZZLE_BOTTOM_RAD=14 3/8"; NOZZLE_HEIGHT=52 3/4"; NOZZLE_HEIGHT/7*2=13 3/16"; NOZZLE_SIZE=252"; NOZZLE_TOP_OD=30 3/4"; NOZZLE_TOP_RAD=15 3/8"; NOZZLE_WB/4=9 13/16"; NOZZLE_WB_OD=49"; NOZZLE_WB_RAD=24 1/2"; NOZZLE_WB_RAD-2"=22 1/2"; RO=36 3/4"; RO/2=18 3/8"; RO2/2=18 3/8"; TRANSITION_TOP=69 11/16"; TYPE=12"; Type Comments=Vari-Plume Laboratory Exhaust Mixed-Flow High Pressure Inline Belt Drive With 1X2 Mixing Box With Weather Hoods On Sides; UNIT_HEIGHT=44 1/2"; UNIT_HEIGHT*.75=33 3/8"; UNIT_OD=34 3/4"; UNIT_RAD+((A/2)+.25")=39 5/8"; UNIT_RAD+((A/2)+.25")+4"=43 5/8"; UNIT_RADIUS=17 3/8"; UNIT_RADIUS*.6=15 5/8"; UNIT_RADIUS+4"=21 3/8"
- 245_QMXVP-21H-1X2_Mixing_Box_Ends: (A/2)+.25"=22 1/4"; (A/2)+.5"=-22 1/2"; (A/2)-.5"=-21 1/2"; (A/2)-2"=20"; (NOZZLE_HEIGHT-(NOZZLE_HEIGHT/8*2))/2=19 25/32"; (NOZZLE_WB_OD-NOZZLE_TOP_OD)/2=4 9/16"; -A=-44"; A=44"; A+.5=44 1/2"; A/2=22"; B=121"; B/2=60 1/2"; C=59"; C/2=29 1/2"; DUAL_F=108"; DUAL_F+1"=109"; DUAL_G=107 1/8"; E=42 15/16"; GA=3/32"; LONG_RO=100 7/8"; LONG_RO/2=50 7/16"; MB_A=57"; MB_HT=45 7/16"; MB_HT+.25"=45 11/16"; MB_HT-2.75"=42 11/16"; MB_HT/2=22 23/32"; Model=QMXVP-1X2_Mixing Box_Sides; NOZZLE_BOTTOM_ID=28 3/4"; NOZZLE_BOTTOM_RAD=14 3/8"; NOZZLE_HEIGHT=52 3/4"; NOZZLE_HEIGHT/7*2=13 3/16"; NOZZLE_SIZE=252"; NOZZLE_TOP_OD=30 3/4"; NOZZLE_TOP_RAD=15 3/8"; NOZZLE_WB/4=9 13/16"; NOZZLE_WB_OD=49"; NOZZLE_WB_RAD=24 1/2"; NOZZLE_WB_RAD-2"=22 1/2"; RO=36 3/4"; RO/2=18 3/8"; RO2/2=18 3/8"; TRANSITION_TOP=69 11/16"; TYPE=0"; Type Comments=Vari-Plume Laboratory Exhaust Mixed-Flow Inline Belt Drive With 1X2 Mixing Box With Weather Hoods On Sides; UNIT_HEIGHT=44 1/2"; UNIT_HEIGHT*.75=33 3/8"; UNIT_OD=34 3/4"; UNIT_RAD+((A/2)+.25")=39 5/8"; UNIT_RAD+((A/2)+.25")+4"=43 5/8"; UNIT_RADIUS=17 3/8"; UNIT_RADIUS*.6=15 5/8"; UNIT_RADIUS+4"=21 3/8"
- 245_QMXVP-21L-1X2_Mixing_Box_Ends: (A/2)+.25"=22 1/4"; (A/2)+.5"=-22 1/2"; (A/2)-.5"=-21 1/2"; (A/2)-2"=20"; (NOZZLE_HEIGHT-(NOZZLE_HEIGHT/8*2))/2=19 25/32"; (NOZZLE_WB_OD-NOZZLE_TOP_OD)/2=4 9/16"; -A=-44"; A=44"; A+.5=44 1/2"; A/2=22"; B=121"; B/2=60 1/2"; C=59"; C/2=29 1/2"; DUAL_F=108"; DUAL_F+1"=109"; DUAL_G=107 1/8"; E=42 15/16"; GA=3/32"; LONG_RO=100 7/8"; LONG_RO/2=50 7/16"; MB_A=57"; MB_HT=45 7/16"; MB_HT+.25"=45 11/16"; MB_HT-2.75"=42 11/16"; MB_HT/2=22 23/32"; Model=QMXVP-1X2_Mixing Box_Sides; NOZZLE_BOTTOM_ID=28 3/4"; NOZZLE_BOTTOM_RAD=14 3/8"; NOZZLE_HEIGHT=52 3/4"; NOZZLE_HEIGHT/7*2=13 3/16"; NOZZLE_SIZE=252"; NOZZLE_TOP_OD=30 3/4"; NOZZLE_TOP_RAD=15 3/8"; NOZZLE_WB/4=9 13/16"; NOZZLE_WB_OD=49"; NOZZLE_WB_RAD=24 1/2"; NOZZLE_WB_RAD-2"=22 1/2"; RO=36 3/4"; RO/2=18 3/8"; RO2/2=18 3/8"; TRANSITION_TOP=69 11/16"; TYPE=0"; Type Comments=Vari-Plume Laboratory Exhaust Mixed-Flow Inline Belt Drive With 1X2 Mixing Box With Weather Hoods On Sides; UNIT_HEIGHT=44 1/2"; UNIT_HEIGHT*.75=33 3/8"; UNIT_OD=34 3/4"; UNIT_RAD+((A/2)+.25")=39 5/8"; UNIT_RAD+((A/2)+.25")+4"=43 5/8"; UNIT_RADIUS=17 3/8"; UNIT_RADIUS*.6=15 5/8"; UNIT_RADIUS+4"=21 3/8"
- 270_QMXHPVP-21H-1X2_Mixing_Box_Ends: (A/2)+.25"=24 1/4"; (A/2)+.5"=-24 1/2"; (A/2)-.5"=-23 1/2"; (A/2)-2"=22"; (NOZZLE_HEIGHT-(NOZZLE_HEIGHT/8*2))/2=19 25/32"; (NOZZLE_WB_OD-NOZZLE_TOP_OD)/2=4 9/16"; -A=-48"; A=48"; A+.5=48 1/2"; A/2=24"; B=128"; B/2=64"; C=63"; C/2=31 1/2"; DUAL_F=112"; DUAL_F+1"=113"; DUAL_G=111 1/8"; E=46 15/16"; GA=3/32"; LONG_RO=104 7/8"; LONG_RO/2=52 7/16"; MB_A=62"; MB_HT=47 3/16"; MB_HT+.25"=47 7/16"; MB_HT-2.75"=44 7/16"; MB_HT/2=23 19/32"; Model=QMXHPVP-1X2_Mixing Box_Sides; NOZZLE_BOTTOM_ID=28 3/4"; NOZZLE_BOTTOM_RAD=14 3/8"; NOZZLE_HEIGHT=52 3/4"; NOZZLE_HEIGHT/7*2=13 3/16"; NOZZLE_SIZE=252"; NOZZLE_TOP_OD=30 3/4"; NOZZLE_TOP_RAD=15 3/8"; NOZZLE_WB/4=9 13/16"; NOZZLE_WB_OD=49"; NOZZLE_WB_RAD=24 1/2"; NOZZLE_WB_RAD-2"=22 1/2"; RO=40 3/4"; RO/2=20 3/8"; RO2/2=20 3/8"; TRANSITION_TOP=79 3/16"; TYPE=12"; Type Comments=Vari-Plume Laboratory Exhaust Mixed-Flow High Pressure Inline Belt Drive With 1X2 Mixing Box With Weather Hoods On Sides; UNIT_HEIGHT=47"; UNIT_HEIGHT*.75=35 1/4"; UNIT_OD=38 5/16"; UNIT_RAD+((A/2)+.25")=43 13/32"; UNIT_RAD+((A/2)+.25")+4"=47 13/32"; UNIT_RADIUS=19 5/32"; UNIT_RADIUS*.6=17 1/4"; UNIT_RADIUS+4"=23 5/32"
- 270_QMXHPVP-21L-1X2_Mixing_Box_Ends: (A/2)+.25"=24 1/4"; (A/2)+.5"=-24 1/2"; (A/2)-.5"=-23 1/2"; (A/2)-2"=22"; (NOZZLE_HEIGHT-(NOZZLE_HEIGHT/8*2))/2=19 25/32"; (NOZZLE_WB_OD-NOZZLE_TOP_OD)/2=4 9/16"; -A=-48"; A=48"; A+.5=48 1/2"; A/2=24"; B=128"; B/2=64"; C=63"; C/2=31 1/2"; DUAL_F=112"; DUAL_F+1"=113"; DUAL_G=111 1/8"; E=46 15/16"; GA=3/32"; LONG_RO=104 7/8"; LONG_RO/2=52 7/16"; MB_A=62"; MB_HT=47 3/16"; MB_HT+.25"=47 7/16"; MB_HT-2.75"=44 7/16"; MB_HT/2=23 19/32"; Model=QMXHPVP-1X2_Mixing Box_Sides; NOZZLE_BOTTOM_ID=28 3/4"; NOZZLE_BOTTOM_RAD=14 3/8"; NOZZLE_HEIGHT=52 3/4"; NOZZLE_HEIGHT/7*2=13 3/16"; NOZZLE_SIZE=252"; NOZZLE_TOP_OD=30 3/4"; NOZZLE_TOP_RAD=15 3/8"; NOZZLE_WB/4=9 13/16"; NOZZLE_WB_OD=49"; NOZZLE_WB_RAD=24 1/2"; NOZZLE_WB_RAD-2"=22 1/2"; RO=40 3/4"; RO/2=20 3/8"; RO2/2=20 3/8"; TRANSITION_TOP=79 3/16"; TYPE=12"; Type Comments=Vari-Plume Laboratory Exhaust Mixed-Flow High Pressure Inline Belt Drive With 1X2 Mixing Box With Weather Hoods On Sides; UNIT_HEIGHT=47"; UNIT_HEIGHT*.75=35 1/4"; UNIT_OD=38 5/16"; UNIT_RAD+((A/2)+.25")=43 13/32"; UNIT_RAD+((A/2)+.25")+4"=47 13/32"; UNIT_RADIUS=19 5/32"; UNIT_RADIUS*.6=17 1/4"; UNIT_RADIUS+4"=23 5/32"
- 270_QMXVP-21H-1X2_Mixing_Box_Ends: (A/2)+.25"=24 1/4"; (A/2)+.5"=-24 1/2"; (A/2)-.5"=-23 1/2"; (A/2)-2"=22"; (NOZZLE_HEIGHT-(NOZZLE_HEIGHT/8*2))/2=19 25/32"; (NOZZLE_WB_OD-NOZZLE_TOP_OD)/2=4 9/16"; -A=-48"; A=48"; A+.5=48 1/2"; A/2=24"; B=128"; B/2=64"; C=63"; C/2=31 1/2"; DUAL_F=112"; DUAL_F+1"=113"; DUAL_G=111 1/8"; E=46 15/16"; GA=3/32"; LONG_RO=104 7/8"; LONG_RO/2=52 7/16"; MB_A=62"; MB_HT=47 3/16"; MB_HT+.25"=47 7/16"; MB_HT-2.75"=44 7/16"; MB_HT/2=23 19/32"; Model=QMXVP-1X2_Mixing Box_Sides; NOZZLE_BOTTOM_ID=28 3/4"; NOZZLE_BOTTOM_RAD=14 3/8"; NOZZLE_HEIGHT=52 3/4"; NOZZLE_HEIGHT/7*2=13 3/16"; NOZZLE_SIZE=252"; NOZZLE_TOP_OD=30 3/4"; NOZZLE_TOP_RAD=15 3/8"; NOZZLE_WB/4=9 13/16"; NOZZLE_WB_OD=49"; NOZZLE_WB_RAD=24 1/2"; NOZZLE_WB_RAD-2"=22 1/2"; RO=40 3/4"; RO/2=20 3/8"; RO2/2=20 3/8"; TRANSITION_TOP=79 3/16"; TYPE=0"; Type Comments=Vari-Plume Laboratory Exhaust Mixed-Flow Inline Belt Drive With 1X2 Mixing Box With Weather Hoods On Sides; UNIT_HEIGHT=47"; UNIT_HEIGHT*.75=35 1/4"; UNIT_OD=38 5/16"; UNIT_RAD+((A/2)+.25")=43 13/32"; UNIT_RAD+((A/2)+.25")+4"=47 13/32"; UNIT_RADIUS=19 5/32"; UNIT_RADIUS*.6=17 1/4"; UNIT_RADIUS+4"=23 5/32"
- 270_QMXVP-21L-1X2_Mixing_Box_Ends: (A/2)+.25"=24 1/4"; (A/2)+.5"=-24 1/2"; (A/2)-.5"=-23 1/2"; (A/2)-2"=22"; (NOZZLE_HEIGHT-(NOZZLE_HEIGHT/8*2))/2=19 25/32"; (NOZZLE_WB_OD-NOZZLE_TOP_OD)/2=4 9/16"; -A=-48"; A=48"; A+.5=48 1/2"; A/2=24"; B=128"; B/2=64"; C=63"; C/2=31 1/2"; DUAL_F=112"; DUAL_F+1"=113"; DUAL_G=111 1/8"; E=46 15/16"; GA=3/32"; LONG_RO=104 7/8"; LONG_RO/2=52 7/16"; MB_A=62"; MB_HT=47 3/16"; MB_HT+.25"=47 7/16"; MB_HT-2.75"=44 7/16"; MB_HT/2=23 19/32"; Model=QMXVP-1X2_Mixing Box_Sides; NOZZLE_BOTTOM_ID=28 3/4"; NOZZLE_BOTTOM_RAD=14 3/8"; NOZZLE_HEIGHT=52 3/4"; NOZZLE_HEIGHT/7*2=13 3/16"; NOZZLE_SIZE=252"; NOZZLE_TOP_OD=30 3/4"; NOZZLE_TOP_RAD=15 3/8"; NOZZLE_WB/4=9 13/16"; NOZZLE_WB_OD=49"; NOZZLE_WB_RAD=24 1/2"; NOZZLE_WB_RAD-2"=22 1/2"; RO=40 3/4"; RO/2=20 3/8"; RO2/2=20 3/8"; TRANSITION_TOP=79 3/16"; TYPE=0"; Type Comments=Vari-Plume Laboratory Exhaust Mixed-Flow Inline Belt Drive With 1X2 Mixing Box With Weather Hoods On Sides; UNIT_HEIGHT=47"; UNIT_HEIGHT*.75=35 1/4"; UNIT_OD=38 5/16"; UNIT_RAD+((A/2)+.25")=43 13/32"; UNIT_RAD+((A/2)+.25")+4"=47 13/32"; UNIT_RADIUS=19 5/32"; UNIT_RADIUS*.6=17 1/4"; UNIT_RADIUS+4"=23 5/32"
- 300_QMXHPVP-21H-1X2_Mixing_Box_Ends: (A/2)+.25"=26 1/4"; (A/2)+.5"=-26 1/2"; (A/2)-.5"=-25 1/2"; (A/2)-2"=24"; (NOZZLE_HEIGHT-(NOZZLE_HEIGHT/8*2))/2=19 25/32"; (NOZZLE_WB_OD-NOZZLE_TOP_OD)/2=4 9/16"; -A=-52"; A=52"; A+.5=52 1/2"; A/2=26"; B=148"; B/2=74"; C=67"; C/2=33 1/2"; DUAL_F=132"; DUAL_F+1"=133"; DUAL_G=131 1/8"; E=50 15/16"; GA=3/32"; LONG_RO=124 7/8"; LONG_RO/2=62 7/16"; MB_A=68"; MB_HT=50 7/16"; MB_HT+.25"=50 11/16"; MB_HT-2.75"=47 11/16"; MB_HT/2=25 7/32"; Model=QMXHPVP-1X2_Mixing Box_Sides; NOZZLE_BOTTOM_ID=28 3/4"; NOZZLE_BOTTOM_RAD=14 3/8"; NOZZLE_HEIGHT=52 3/4"; NOZZLE_HEIGHT/7*2=13 3/16"; NOZZLE_SIZE=252"; NOZZLE_TOP_OD=30 3/4"; NOZZLE_TOP_RAD=15 3/8"; NOZZLE_WB/4=9 13/16"; NOZZLE_WB_OD=49"; NOZZLE_WB_RAD=24 1/2"; NOZZLE_WB_RAD-2"=22 1/2"; RO=44 3/4"; RO/2=22 3/8"; RO2/2=22 3/8"; TRANSITION_TOP=94 3/16"; TYPE=12"; Type Comments=Vari-Plume Laboratory Exhaust Mixed-Flow High Pressure Inline Belt Drive With 1X2 Mixing Box With Weather Hoods On Sides; UNIT_HEIGHT=54"; UNIT_HEIGHT*.75=40 1/2"; UNIT_OD=42 1/2"; UNIT_RAD+((A/2)+.25")=47 1/2"; UNIT_RAD+((A/2)+.25")+4"=51 1/2"; UNIT_RADIUS=21 1/4"; UNIT_RADIUS*.6=19 1/8"; UNIT_RADIUS+4"=25 1/4"
- 300_QMXHPVP-21L-1X2_Mixing_Box_Ends: (A/2)+.25"=26 1/4"; (A/2)+.5"=-26 1/2"; (A/2)-.5"=-25 1/2"; (A/2)-2"=24"; (NOZZLE_HEIGHT-(NOZZLE_HEIGHT/8*2))/2=19 25/32"; (NOZZLE_WB_OD-NOZZLE_TOP_OD)/2=4 9/16"; -A=-52"; A=52"; A+.5=52 1/2"; A/2=26"; B=148"; B/2=74"; C=67"; C/2=33 1/2"; DUAL_F=132"; DUAL_F+1"=133"; DUAL_G=131 1/8"; E=50 15/16"; GA=3/32"; LONG_RO=124 7/8"; LONG_RO/2=62 7/16"; MB_A=68"; MB_HT=50 7/16"; MB_HT+.25"=50 11/16"; MB_HT-2.75"=47 11/16"; MB_HT/2=25 7/32"; Model=QMXHPVP-1X2_Mixing Box_Sides; NOZZLE_BOTTOM_ID=28 3/4"; NOZZLE_BOTTOM_RAD=14 3/8"; NOZZLE_HEIGHT=52 3/4"; NOZZLE_HEIGHT/7*2=13 3/16"; NOZZLE_SIZE=252"; NOZZLE_TOP_OD=30 3/4"; NOZZLE_TOP_RAD=15 3/8"; NOZZLE_WB/4=9 13/16"; NOZZLE_WB_OD=49"; NOZZLE_WB_RAD=24 1/2"; NOZZLE_WB_RAD-2"=22 1/2"; RO=44 3/4"; RO/2=22 3/8"; RO2/2=22 3/8"; TRANSITION_TOP=94 3/16"; TYPE=12"; Type Comments=Vari-Plume Laboratory Exhaust Mixed-Flow High Pressure Inline Belt Drive With 1X2 Mixing Box With Weather Hoods On Sides; UNIT_HEIGHT=54"; UNIT_HEIGHT*.75=40 1/2"; UNIT_OD=42 1/2"; UNIT_RAD+((A/2)+.25")=47 1/2"; UNIT_RAD+((A/2)+.25")+4"=51 1/2"; UNIT_RADIUS=21 1/4"; UNIT_RADIUS*.6=19 1/8"; UNIT_RADIUS+4"=25 1/4"
- 300_QMXVP-21H-1X2_Mixing_Box_Ends: (A/2)+.25"=26 1/4"; (A/2)+.5"=-26 1/2"; (A/2)-.5"=-25 1/2"; (A/2)-2"=24"; (NOZZLE_HEIGHT-(NOZZLE_HEIGHT/8*2))/2=19 25/32"; (NOZZLE_WB_OD-NOZZLE_TOP_OD)/2=4 9/16"; -A=-52"; A=52"; A+.5=52 1/2"; A/2=26"; B=148"; B/2=74"; C=67"; C/2=33 1/2"; DUAL_F=132"; DUAL_F+1"=133"; DUAL_G=131 1/8"; E=50 15/16"; GA=3/32"; LONG_RO=124 7/8"; LONG_RO/2=62 7/16"; MB_A=68"; MB_HT=50 7/16"; MB_HT+.25"=50 11/16"; MB_HT-2.75"=47 11/16"; MB_HT/2=25 7/32"; Model=QMXVP-1X2_Mixing Box_Sides; NOZZLE_BOTTOM_ID=28 3/4"; NOZZLE_BOTTOM_RAD=14 3/8"; NOZZLE_HEIGHT=52 3/4"; NOZZLE_HEIGHT/7*2=13 3/16"; NOZZLE_SIZE=252"; NOZZLE_TOP_OD=30 3/4"; NOZZLE_TOP_RAD=15 3/8"; NOZZLE_WB/4=9 13/16"; NOZZLE_WB_OD=49"; NOZZLE_WB_RAD=24 1/2"; NOZZLE_WB_RAD-2"=22 1/2"; RO=44 3/4"; RO/2=22 3/8"; RO2/2=22 3/8"; TRANSITION_TOP=94 3/16"; TYPE=0"; Type Comments=Vari-Plume Laboratory Exhaust Mixed-Flow Inline Belt Drive With 1X2 Mixing Box With Weather Hoods On Sides; UNIT_HEIGHT=54"; UNIT_HEIGHT*.75=40 1/2"; UNIT_OD=42 1/2"; UNIT_RAD+((A/2)+.25")=47 1/2"; UNIT_RAD+((A/2)+.25")+4"=51 1/2"; UNIT_RADIUS=21 1/4"; UNIT_RADIUS*.6=19 1/8"; UNIT_RADIUS+4"=25 1/4"
- 300_QMXVP-21L-1X2_Mixing_Box_Ends: (A/2)+.25"=26 1/4"; (A/2)+.5"=-26 1/2"; (A/2)-.5"=-25 1/2"; (A/2)-2"=24"; (NOZZLE_HEIGHT-(NOZZLE_HEIGHT/8*2))/2=19 25/32"; (NOZZLE_WB_OD-NOZZLE_TOP_OD)/2=4 9/16"; -A=-52"; A=52"; A+.5=52 1/2"; A/2=26"; B=148"; B/2=74"; C=67"; C/2=33 1/2"; DUAL_F=132"; DUAL_F+1"=133"; DUAL_G=131 1/8"; E=50 15/16"; GA=3/32"; LONG_RO=124 7/8"; LONG_RO/2=62 7/16"; MB_A=68"; MB_HT=50 7/16"; MB_HT+.25"=50 11/16"; MB_HT-2.75"=47 11/16"; MB_HT/2=25 7/32"; Model=QMXVP-1X2_Mixing Box_Sides; NOZZLE_BOTTOM_ID=28 3/4"; NOZZLE_BOTTOM_RAD=14 3/8"; NOZZLE_HEIGHT=52 3/4"; NOZZLE_HEIGHT/7*2=13 3/16"; NOZZLE_SIZE=252"; NOZZLE_TOP_OD=30 3/4"; NOZZLE_TOP_RAD=15 3/8"; NOZZLE_WB/4=9 13/16"; NOZZLE_WB_OD=49"; NOZZLE_WB_RAD=24 1/2"; NOZZLE_WB_RAD-2"=22 1/2"; RO=44 3/4"; RO/2=22 3/8"; RO2/2=22 3/8"; TRANSITION_TOP=94 3/16"; TYPE=0"; Type Comments=Vari-Plume Laboratory Exhaust Mixed-Flow Inline Belt Drive With 1X2 Mixing Box With Weather Hoods On Sides; UNIT_HEIGHT=54"; UNIT_HEIGHT*.75=40 1/2"; UNIT_OD=42 1/2"; UNIT_RAD+((A/2)+.25")=47 1/2"; UNIT_RAD+((A/2)+.25")+4"=51 1/2"; UNIT_RADIUS=21 1/4"; UNIT_RADIUS*.6=19 1/8"; UNIT_RADIUS+4"=25 1/4"
- 270_QMXHPVP-27H-1X2_Mixing_Box_Ends: (A/2)+.25"=24 1/4"; (A/2)+.5"=-24 1/2"; (A/2)-.5"=-23 1/2"; (A/2)-2"=22"; (NOZZLE_HEIGHT-(NOZZLE_HEIGHT/8*2))/2=22 3/4"; (NOZZLE_WB_OD-NOZZLE_TOP_OD)/2=5 11/32"; -A=-48"; A=48"; A+.5=48 1/2"; A/2=24"; B=128"; B/2=64"; C=63"; C/2=31 1/2"; DUAL_F=112"; DUAL_F+1"=113"; DUAL_G=111 1/8"; E=46 15/16"; GA=3/32"; LONG_RO=104 7/8"; LONG_RO/2=52 7/16"; MB_A=62"; MB_HT=47 3/16"; MB_HT+.25"=47 7/16"; MB_HT-2.75"=44 7/16"; MB_HT/2=23 19/32"; Model=QMXHPVP-1X2_Mixing Box_Sides; NOZZLE_BOTTOM_ID=38 5/16"; NOZZLE_BOTTOM_RAD=19 5/32"; NOZZLE_HEIGHT=60 5/8"; NOZZLE_HEIGHT/7*2=15 5/32"; NOZZLE_SIZE=324"; NOZZLE_TOP_OD=39 11/16"; NOZZLE_TOP_RAD=19 27/32"; NOZZLE_WB/4=12 3/16"; NOZZLE_WB_OD=61"; NOZZLE_WB_RAD=30 1/2"; NOZZLE_WB_RAD-2"=28 1/2"; RO=40 3/4"; RO/2=20 3/8"; RO2/2=20 3/8"; TRANSITION_TOP=62 1/4"; TYPE=12"; Type Comments=Vari-Plume Laboratory Exhaust Mixed-Flow High Pressure Inline Belt Drive With 1X2 Mixing Box With Weather Hoods On Sides; UNIT_HEIGHT=47"; UNIT_HEIGHT*.75=35 1/4"; UNIT_OD=38 5/16"; UNIT_RAD+((A/2)+.25")=43 13/32"; UNIT_RAD+((A/2)+.25")+4"=47 13/32"; UNIT_RADIUS=19 5/32"; UNIT_RADIUS*.6=17 1/4"; UNIT_RADIUS+4"=23 5/32"
- 270_QMXHPVP-27L-1X2_Mixing_Box_Ends: (A/2)+.25"=24 1/4"; (A/2)+.5"=-24 1/2"; (A/2)-.5"=-23 1/2"; (A/2)-2"=22"; (NOZZLE_HEIGHT-(NOZZLE_HEIGHT/8*2))/2=22 3/4"; (NOZZLE_WB_OD-NOZZLE_TOP_OD)/2=5 11/32"; -A=-48"; A=48"; A+.5=48 1/2"; A/2=24"; B=128"; B/2=64"; C=63"; C/2=31 1/2"; DUAL_F=112"; DUAL_F+1"=113"; DUAL_G=111 1/8"; E=46 15/16"; GA=3/32"; LONG_RO=104 7/8"; LONG_RO/2=52 7/16"; MB_A=62"; MB_HT=47 3/16"; MB_HT+.25"=47 7/16"; MB_HT-2.75"=44 7/16"; MB_HT/2=23 19/32"; Model=QMXHPVP-1X2_Mixing Box_Sides; NOZZLE_BOTTOM_ID=38 5/16"; NOZZLE_BOTTOM_RAD=19 5/32"; NOZZLE_HEIGHT=60 5/8"; NOZZLE_HEIGHT/7*2=15 5/32"; NOZZLE_SIZE=324"; NOZZLE_TOP_OD=39 11/16"; NOZZLE_TOP_RAD=19 27/32"; NOZZLE_WB/4=12 3/16"; NOZZLE_WB_OD=61"; NOZZLE_WB_RAD=30 1/2"; NOZZLE_WB_RAD-2"=28 1/2"; RO=40 3/4"; RO/2=20 3/8"; RO2/2=20 3/8"; TRANSITION_TOP=62 1/4"; TYPE=12"; Type Comments=Vari-Plume Laboratory Exhaust Mixed-Flow High Pressure Inline Belt Drive With 1X2 Mixing Box With Weather Hoods On Sides; UNIT_HEIGHT=47"; UNIT_HEIGHT*.75=35 1/4"; UNIT_OD=38 5/16"; UNIT_RAD+((A/2)+.25")=43 13/32"; UNIT_RAD+((A/2)+.25")+4"=47 13/32"; UNIT_RADIUS=19 5/32"; UNIT_RADIUS*.6=17 1/4"; UNIT_RADIUS+4"=23 5/32"
- 270_QMXVP-27H-1X2_Mixing_Box_Ends: (A/2)+.25"=24 1/4"; (A/2)+.5"=-24 1/2"; (A/2)-.5"=-23 1/2"; (A/2)-2"=22"; (NOZZLE_HEIGHT-(NOZZLE_HEIGHT/8*2))/2=22 3/4"; (NOZZLE_WB_OD-NOZZLE_TOP_OD)/2=5 11/32"; -A=-48"; A=48"; A+.5=48 1/2"; A/2=24"; B=128"; B/2=64"; C=63"; C/2=31 1/2"; DUAL_F=112"; DUAL_F+1"=113"; DUAL_G=111 1/8"; E=46 15/16"; GA=3/32"; LONG_RO=104 7/8"; LONG_RO/2=52 7/16"; MB_A=62"; MB_HT=47 3/16"; MB_HT+.25"=47 7/16"; MB_HT-2.75"=44 7/16"; MB_HT/2=23 19/32"; Model=QMXVP-1X2_Mixing Box_Sides; NOZZLE_BOTTOM_ID=38 5/16"; NOZZLE_BOTTOM_RAD=19 5/32"; NOZZLE_HEIGHT=60 5/8"; NOZZLE_HEIGHT/7*2=15 5/32"; NOZZLE_SIZE=324"; NOZZLE_TOP_OD=39 11/16"; NOZZLE_TOP_RAD=19 27/32"; NOZZLE_WB/4=12 3/16"; NOZZLE_WB_OD=61"; NOZZLE_WB_RAD=30 1/2"; NOZZLE_WB_RAD-2"=28 1/2"; RO=40 3/4"; RO/2=20 3/8"; RO2/2=20 3/8"; TRANSITION_TOP=62 1/4"; TYPE=0"; Type Comments=Vari-Plume Laboratory Exhaust Mixed-Flow Inline Belt Drive With 1X2 Mixing Box With Weather Hoods On Sides; UNIT_HEIGHT=47"; UNIT_HEIGHT*.75=35 1/4"; UNIT_OD=38 5/16"; UNIT_RAD+((A/2)+.25")=43 13/32"; UNIT_RAD+((A/2)+.25")+4"=47 13/32"; UNIT_RADIUS=19 5/32"; UNIT_RADIUS*.6=17 1/4"; UNIT_RADIUS+4"=23 5/32"
- 270_QMXVP-27L-1X2_Mixing_Box_Ends: (A/2)+.25"=24 1/4"; (A/2)+.5"=-24 1/2"; (A/2)-.5"=-23 1/2"; (A/2)-2"=22"; (NOZZLE_HEIGHT-(NOZZLE_HEIGHT/8*2))/2=22 3/4"; (NOZZLE_WB_OD-NOZZLE_TOP_OD)/2=5 11/32"; -A=-48"; A=48"; A+.5=48 1/2"; A/2=24"; B=128"; B/2=64"; C=63"; C/2=31 1/2"; DUAL_F=112"; DUAL_F+1"=113"; DUAL_G=111 1/8"; E=46 15/16"; GA=3/32"; LONG_RO=104 7/8"; LONG_RO/2=52 7/16"; MB_A=62"; MB_HT=47 3/16"; MB_HT+.25"=47 7/16"; MB_HT-2.75"=44 7/16"; MB_HT/2=23 19/32"; Model=QMXVP-1X2_Mixing Box_Sides; NOZZLE_BOTTOM_ID=38 5/16"; NOZZLE_BOTTOM_RAD=19 5/32"; NOZZLE_HEIGHT=60 5/8"; NOZZLE_HEIGHT/7*2=15 5/32"; NOZZLE_SIZE=324"; NOZZLE_TOP_OD=39 11/16"; NOZZLE_TOP_RAD=19 27/32"; NOZZLE_WB/4=12 3/16"; NOZZLE_WB_OD=61"; NOZZLE_WB_RAD=30 1/2"; NOZZLE_WB_RAD-2"=28 1/2"; RO=40 3/4"; RO/2=20 3/8"; RO2/2=20 3/8"; TRANSITION_TOP=62 1/4"; TYPE=0"; Type Comments=Vari-Plume Laboratory Exhaust Mixed-Flow Inline Belt Drive With 1X2 Mixing Box With Weather Hoods On Sides; UNIT_HEIGHT=47"; UNIT_HEIGHT*.75=35 1/4"; UNIT_OD=38 5/16"; UNIT_RAD+((A/2)+.25")=43 13/32"; UNIT_RAD+((A/2)+.25")+4"=47 13/32"; UNIT_RADIUS=19 5/32"; UNIT_RADIUS*.6=17 1/4"; UNIT_RADIUS+4"=23 5/32"
- 300_QMXHPVP-27H-1X2_Mixing_Box_Ends: (A/2)+.25"=26 1/4"; (A/2)+.5"=-26 1/2"; (A/2)-.5"=-25 1/2"; (A/2)-2"=24"; (NOZZLE_HEIGHT-(NOZZLE_HEIGHT/8*2))/2=22 3/4"; (NOZZLE_WB_OD-NOZZLE_TOP_OD)/2=5 11/32"; -A=-52"; A=52"; A+.5=52 1/2"; A/2=26"; B=148"; B/2=74"; C=67"; C/2=33 1/2"; DUAL_F=132"; DUAL_F+1"=133"; DUAL_G=131 1/8"; E=50 15/16"; GA=3/32"; LONG_RO=124 7/8"; LONG_RO/2=62 7/16"; MB_A=68"; MB_HT=50 7/16"; MB_HT+.25"=50 11/16"; MB_HT-2.75"=47 11/16"; MB_HT/2=25 7/32"; Model=QMXHPVP-1X2_Mixing Box_Sides; NOZZLE_BOTTOM_ID=38 5/16"; NOZZLE_BOTTOM_RAD=19 5/32"; NOZZLE_HEIGHT=60 5/8"; NOZZLE_HEIGHT/7*2=15 5/32"; NOZZLE_SIZE=324"; NOZZLE_TOP_OD=39 11/16"; NOZZLE_TOP_RAD=19 27/32"; NOZZLE_WB/4=12 3/16"; NOZZLE_WB_OD=61"; NOZZLE_WB_RAD=30 1/2"; NOZZLE_WB_RAD-2"=28 1/2"; RO=44 3/4"; RO/2=22 3/8"; RO2/2=22 3/8"; TRANSITION_TOP=77 1/4"; TYPE=12"; Type Comments=Vari-Plume Laboratory Exhaust Mixed-Flow High Pressure Inline Belt Drive With 1X2 Mixing Box With Weather Hoods On Sides; UNIT_HEIGHT=54"; UNIT_HEIGHT*.75=40 1/2"; UNIT_OD=42 1/2"; UNIT_RAD+((A/2)+.25")=47 1/2"; UNIT_RAD+((A/2)+.25")+4"=51 1/2"; UNIT_RADIUS=21 1/4"; UNIT_RADIUS*.6=19 1/8"; UNIT_RADIUS+4"=25 1/4"
- 300_QMXHPVP-27L-1X2_Mixing_Box_Ends: (A/2)+.25"=26 1/4"; (A/2)+.5"=-26 1/2"; (A/2)-.5"=-25 1/2"; (A/2)-2"=24"; (NOZZLE_HEIGHT-(NOZZLE_HEIGHT/8*2))/2=22 3/4"; (NOZZLE_WB_OD-NOZZLE_TOP_OD)/2=5 11/32"; -A=-52"; A=52"; A+.5=52 1/2"; A/2=26"; B=148"; B/2=74"; C=67"; C/2=33 1/2"; DUAL_F=132"; DUAL_F+1"=133"; DUAL_G=131 1/8"; E=50 15/16"; GA=3/32"; LONG_RO=124 7/8"; LONG_RO/2=62 7/16"; MB_A=68"; MB_HT=50 7/16"; MB_HT+.25"=50 11/16"; MB_HT-2.75"=47 11/16"; MB_HT/2=25 7/32"; Model=QMXHPVP-1X2_Mixing Box_Sides; NOZZLE_BOTTOM_ID=38 5/16"; NOZZLE_BOTTOM_RAD=19 5/32"; NOZZLE_HEIGHT=60 5/8"; NOZZLE_HEIGHT/7*2=15 5/32"; NOZZLE_SIZE=324"; NOZZLE_TOP_OD=39 11/16"; NOZZLE_TOP_RAD=19 27/32"; NOZZLE_WB/4=12 3/16"; NOZZLE_WB_OD=61"; NOZZLE_WB_RAD=30 1/2"; NOZZLE_WB_RAD-2"=28 1/2"; RO=44 3/4"; RO/2=22 3/8"; RO2/2=22 3/8"; TRANSITION_TOP=77 1/4"; TYPE=12"; Type Comments=Vari-Plume Laboratory Exhaust Mixed-Flow High Pressure Inline Belt Drive With 1X2 Mixing Box With Weather Hoods On Sides; UNIT_HEIGHT=54"; UNIT_HEIGHT*.75=40 1/2"; UNIT_OD=42 1/2"; UNIT_RAD+((A/2)+.25")=47 1/2"; UNIT_RAD+((A/2)+.25")+4"=51 1/2"; UNIT_RADIUS=21 1/4"; UNIT_RADIUS*.6=19 1/8"; UNIT_RADIUS+4"=25 1/4"
- 300_QMXVP-27H-1X2_Mixing_Box_Ends: (A/2)+.25"=26 1/4"; (A/2)+.5"=-26 1/2"; (A/2)-.5"=-25 1/2"; (A/2)-2"=24"; (NOZZLE_HEIGHT-(NOZZLE_HEIGHT/8*2))/2=22 3/4"; (NOZZLE_WB_OD-NOZZLE_TOP_OD)/2=5 11/32"; -A=-52"; A=52"; A+.5=52 1/2"; A/2=26"; B=148"; B/2=74"; C=67"; C/2=33 1/2"; DUAL_F=132"; DUAL_F+1"=133"; DUAL_G=131 1/8"; E=50 15/16"; GA=3/32"; LONG_RO=124 7/8"; LONG_RO/2=62 7/16"; MB_A=68"; MB_HT=50 7/16"; MB_HT+.25"=50 11/16"; MB_HT-2.75"=47 11/16"; MB_HT/2=25 7/32"; Model=QMXVP-1X2_Mixing Box_Sides; NOZZLE_BOTTOM_ID=38 5/16"; NOZZLE_BOTTOM_RAD=19 5/32"; NOZZLE_HEIGHT=60 5/8"; NOZZLE_HEIGHT/7*2=15 5/32"; NOZZLE_SIZE=324"; NOZZLE_TOP_OD=39 11/16"; NOZZLE_TOP_RAD=19 27/32"; NOZZLE_WB/4=12 3/16"; NOZZLE_WB_OD=61"; NOZZLE_WB_RAD=30 1/2"; NOZZLE_WB_RAD-2"=28 1/2"; RO=44 3/4"; RO/2=22 3/8"; RO2/2=22 3/8"; TRANSITION_TOP=77 1/4"; TYPE=0"; Type Comments=Vari-Plume Laboratory Exhaust Mixed-Flow Inline Belt Drive With 1X2 Mixing Box With Weather Hoods On Sides; UNIT_HEIGHT=54"; UNIT_HEIGHT*.75=40 1/2"; UNIT_OD=42 1/2"; UNIT_RAD+((A/2)+.25")=47 1/2"; UNIT_RAD+((A/2)+.25")+4"=51 1/2"; UNIT_RADIUS=21 1/4"; UNIT_RADIUS*.6=19 1/8"; UNIT_RADIUS+4"=25 1/4"
- 300_QMXVP-27L-1X2_Mixing_Box_Ends: (A/2)+.25"=26 1/4"; (A/2)+.5"=-26 1/2"; (A/2)-.5"=-25 1/2"; (A/2)-2"=24"; (NOZZLE_HEIGHT-(NOZZLE_HEIGHT/8*2))/2=22 3/4"; (NOZZLE_WB_OD-NOZZLE_TOP_OD)/2=5 11/32"; -A=-52"; A=52"; A+.5=52 1/2"; A/2=26"; B=148"; B/2=74"; C=67"; C/2=33 1/2"; DUAL_F=132"; DUAL_F+1"=133"; DUAL_G=131 1/8"; E=50 15/16"; GA=3/32"; LONG_RO=124 7/8"; LONG_RO/2=62 7/16"; MB_A=68"; MB_HT=50 7/16"; MB_HT+.25"=50 11/16"; MB_HT-2.75"=47 11/16"; MB_HT/2=25 7/32"; Model=QMXVP-1X2_Mixing Box_Sides; NOZZLE_BOTTOM_ID=38 5/16"; NOZZLE_BOTTOM_RAD=19 5/32"; NOZZLE_HEIGHT=60 5/8"; NOZZLE_HEIGHT/7*2=15 5/32"; NOZZLE_SIZE=324"; NOZZLE_TOP_OD=39 11/16"; NOZZLE_TOP_RAD=19 27/32"; NOZZLE_WB/4=12 3/16"; NOZZLE_WB_OD=61"; NOZZLE_WB_RAD=30 1/2"; NOZZLE_WB_RAD-2"=28 1/2"; RO=44 3/4"; RO/2=22 3/8"; RO2/2=22 3/8"; TRANSITION_TOP=77 1/4"; TYPE=0"; Type Comments=Vari-Plume Laboratory Exhaust Mixed-Flow Inline Belt Drive With 1X2 Mixing Box With Weather Hoods On Sides; UNIT_HEIGHT=54"; UNIT_HEIGHT*.75=40 1/2"; UNIT_OD=42 1/2"; UNIT_RAD+((A/2)+.25")=47 1/2"; UNIT_RAD+((A/2)+.25")+4"=51 1/2"; UNIT_RADIUS=21 1/4"; UNIT_RADIUS*.6=19 1/8"; UNIT_RADIUS+4"=25 1/4"
- 330_QMXHPVP-27L-1X2_Mixing_Box_Ends: (A/2)+.25"=28 1/4"; (A/2)+.5"=-28 1/2"; (A/2)-.5"=-27 1/2"; (A/2)-2"=26"; (NOZZLE_HEIGHT-(NOZZLE_HEIGHT/8*2))/2=22 3/4"; (NOZZLE_WB_OD-NOZZLE_TOP_OD)/2=5 11/32"; -A=-56"; A=56"; A+.5=56 1/2"; A/2=28"; B=154"; B/2=77"; C=73"; C/2=36 1/2"; DUAL_F=136"; DUAL_F+1"=137"; DUAL_G=135 1/8"; E=54 13/16"; GA=3/32"; LONG_RO=128 7/8"; LONG_RO/2=64 7/16"; MB_A=73"; MB_HT=53 11/16"; MB_HT+.25"=53 15/16"; MB_HT-2.75"=50 15/16"; MB_HT/2=26 27/32"; Model=QMXHPVP-1X2_Mixing Box_Sides; NOZZLE_BOTTOM_ID=38 5/16"; NOZZLE_BOTTOM_RAD=19 5/32"; NOZZLE_HEIGHT=60 5/8"; NOZZLE_HEIGHT/7*2=15 5/32"; NOZZLE_SIZE=324"; NOZZLE_TOP_OD=39 11/16"; NOZZLE_TOP_RAD=19 27/32"; NOZZLE_WB/4=12 3/16"; NOZZLE_WB_OD=61"; NOZZLE_WB_RAD=30 1/2"; NOZZLE_WB_RAD-2"=28 1/2"; RO=48 5/8"; RO/2=24 5/16"; RO2/2=24 5/16"; TRANSITION_TOP=89 3/4"; TYPE=12"; Type Comments=Vari-Plume Laboratory Exhaust Mixed-Flow High Pressure Inline Belt Drive With 1X2 Mixing Box With Weather Hoods On Sides; UNIT_HEIGHT=58 1/2"; UNIT_HEIGHT*.75=43 7/8"; UNIT_OD=46 3/4"; UNIT_RAD+((A/2)+.25")=51 5/8"; UNIT_RAD+((A/2)+.25")+4"=55 5/8"; UNIT_RADIUS=23 3/8"; UNIT_RADIUS*.6=21 1/32"; UNIT_RADIUS+4"=27 3/8"
- 330_QMXHPVP-27H-1X2_Mixing_Box_Ends: (A/2)+.25"=28 1/4"; (A/2)+.5"=-28 1/2"; (A/2)-.5"=-27 1/2"; (A/2)-2"=26"; (NOZZLE_HEIGHT-(NOZZLE_HEIGHT/8*2))/2=22 3/4"; (NOZZLE_WB_OD-NOZZLE_TOP_OD)/2=5 11/32"; -A=-56"; A=56"; A+.5=56 1/2"; A/2=28"; B=154"; B/2=77"; C=73"; C/2=36 1/2"; DUAL_F=136"; DUAL_F+1"=137"; DUAL_G=135 1/8"; E=54 13/16"; GA=3/32"; LONG_RO=128 7/8"; LONG_RO/2=64 7/16"; MB_A=73"; MB_HT=53 11/16"; MB_HT+.25"=53 15/16"; MB_HT-2.75"=50 15/16"; MB_HT/2=26 27/32"; Model=QMXHPVP-1X2_Mixing Box_Sides; NOZZLE_BOTTOM_ID=38 5/16"; NOZZLE_BOTTOM_RAD=19 5/32"; NOZZLE_HEIGHT=60 5/8"; NOZZLE_HEIGHT/7*2=15 5/32"; NOZZLE_SIZE=324"; NOZZLE_TOP_OD=39 11/16"; NOZZLE_TOP_RAD=19 27/32"; NOZZLE_WB/4=12 3/16"; NOZZLE_WB_OD=61"; NOZZLE_WB_RAD=30 1/2"; NOZZLE_WB_RAD-2"=28 1/2"; RO=48 5/8"; RO/2=24 5/16"; RO2/2=24 5/16"; TRANSITION_TOP=89 3/4"; TYPE=12"; Type Comments=Vari-Plume Laboratory Exhaust Mixed-Flow High Pressure Inline Belt Drive With 1X2 Mixing Box With Weather Hoods On Sides; UNIT_HEIGHT=58 1/2"; UNIT_HEIGHT*.75=43 7/8"; UNIT_OD=46 3/4"; UNIT_RAD+((A/2)+.25")=51 5/8"; UNIT_RAD+((A/2)+.25")+4"=55 5/8"; UNIT_RADIUS=23 3/8"; UNIT_RADIUS*.6=21 1/32"; UNIT_RADIUS+4"=27 3/8"
- 330_QMXVP-27H-1X2_Mixing_Box_Ends: (A/2)+.25"=28 1/4"; (A/2)+.5"=-28 1/2"; (A/2)-.5"=-27 1/2"; (A/2)-2"=26"; (NOZZLE_HEIGHT-(NOZZLE_HEIGHT/8*2))/2=22 3/4"; (NOZZLE_WB_OD-NOZZLE_TOP_OD)/2=5 11/32"; -A=-56"; A=56"; A+.5=56 1/2"; A/2=28"; B=154"; B/2=77"; C=73"; C/2=36 1/2"; DUAL_F=136"; DUAL_F+1"=137"; DUAL_G=135 1/8"; E=54 13/16"; GA=3/32"; LONG_RO=128 7/8"; LONG_RO/2=64 7/16"; MB_A=73"; MB_HT=53 11/16"; MB_HT+.25"=53 15/16"; MB_HT-2.75"=50 15/16"; MB_HT/2=26 27/32"; Model=QMXVP-1X2_Mixing Box_Sides; NOZZLE_BOTTOM_ID=38 5/16"; NOZZLE_BOTTOM_RAD=19 5/32"; NOZZLE_HEIGHT=60 5/8"; NOZZLE_HEIGHT/7*2=15 5/32"; NOZZLE_SIZE=324"; NOZZLE_TOP_OD=39 11/16"; NOZZLE_TOP_RAD=19 27/32"; NOZZLE_WB/4=12 3/16"; NOZZLE_WB_OD=61"; NOZZLE_WB_RAD=30 1/2"; NOZZLE_WB_RAD-2"=28 1/2"; RO=48 5/8"; RO/2=24 5/16"; RO2/2=24 5/16"; TRANSITION_TOP=89 3/4"; TYPE=0"; Type Comments=Vari-Plume Laboratory Exhaust Mixed-Flow Inline Belt Drive With 1X2 Mixing Box With Weather Hoods On Sides; UNIT_HEIGHT=58 1/2"; UNIT_HEIGHT*.75=43 7/8"; UNIT_OD=46 3/4"; UNIT_RAD+((A/2)+.25")=51 5/8"; UNIT_RAD+((A/2)+.25")+4"=55 5/8"; UNIT_RADIUS=23 3/8"; UNIT_RADIUS*.6=21 1/32"; UNIT_RADIUS+4"=27 3/8"
- 330_QMXVP-27L-1X2_Mixing_Box_Ends: (A/2)+.25"=28 1/4"; (A/2)+.5"=-28 1/2"; (A/2)-.5"=-27 1/2"; (A/2)-2"=26"; (NOZZLE_HEIGHT-(NOZZLE_HEIGHT/8*2))/2=22 3/4"; (NOZZLE_WB_OD-NOZZLE_TOP_OD)/2=5 11/32"; -A=-56"; A=56"; A+.5=56 1/2"; A/2=28"; B=154"; B/2=77"; C=73"; C/2=36 1/2"; DUAL_F=136"; DUAL_F+1"=137"; DUAL_G=135 1/8"; E=54 13/16"; GA=3/32"; LONG_RO=128 7/8"; LONG_RO/2=64 7/16"; MB_A=73"; MB_HT=53 11/16"; MB_HT+.25"=53 15/16"; MB_HT-2.75"=50 15/16"; MB_HT/2=26 27/32"; Model=QMXVP-1X2_Mixing Box_Sides; NOZZLE_BOTTOM_ID=38 5/16"; NOZZLE_BOTTOM_RAD=19 5/32"; NOZZLE_HEIGHT=60 5/8"; NOZZLE_HEIGHT/7*2=15 5/32"; NOZZLE_SIZE=324"; NOZZLE_TOP_OD=39 11/16"; NOZZLE_TOP_RAD=19 27/32"; NOZZLE_WB/4=12 3/16"; NOZZLE_WB_OD=61"; NOZZLE_WB_RAD=30 1/2"; NOZZLE_WB_RAD-2"=28 1/2"; RO=48 5/8"; RO/2=24 5/16"; RO2/2=24 5/16"; TRANSITION_TOP=89 3/4"; TYPE=0"; Type Comments=Vari-Plume Laboratory Exhaust Mixed-Flow Inline Belt Drive With 1X2 Mixing Box With Weather Hoods On Sides; UNIT_HEIGHT=58 1/2"; UNIT_HEIGHT*.75=43 7/8"; UNIT_OD=46 3/4"; UNIT_RAD+((A/2)+.25")=51 5/8"; UNIT_RAD+((A/2)+.25")+4"=55 5/8"; UNIT_RADIUS=23 3/8"; UNIT_RADIUS*.6=21 1/32"; UNIT_RADIUS+4"=27 3/8"
- 365_QMXHPVP-27H-1X2_Mixing_Box_Ends: (A/2)+.25"=31 1/4"; (A/2)+.5"=-31 1/2"; (A/2)-.5"=-30 1/2"; (A/2)-2"=29"; (NOZZLE_HEIGHT-(NOZZLE_HEIGHT/8*2))/2=22 3/4"; (NOZZLE_WB_OD-NOZZLE_TOP_OD)/2=5 11/32"; -A=-62"; A=62"; A+.5=62 1/2"; A/2=31"; B=175"; B/2=87 1/2"; C=79"; C/2=39 1/2"; DUAL_F=159"; DUAL_F+1"=160"; DUAL_G=158"; E=60 3/4"; GA=3/32"; LONG_RO=151 3/4"; LONG_RO/2=75 7/8"; MB_A=82"; MB_HT=59 11/16"; MB_HT+.25"=59 15/16"; MB_HT-2.75"=56 15/16"; MB_HT/2=29 27/32"; Model=QMXHPVP-1X2_Mixing Box_Sides; NOZZLE_BOTTOM_ID=38 5/16"; NOZZLE_BOTTOM_RAD=19 5/32"; NOZZLE_HEIGHT=60 5/8"; NOZZLE_HEIGHT/7*2=15 5/32"; NOZZLE_SIZE=324"; NOZZLE_TOP_OD=39 11/16"; NOZZLE_TOP_RAD=19 27/32"; NOZZLE_WB/4=12 3/16"; NOZZLE_WB_OD=61"; NOZZLE_WB_RAD=30 1/2"; NOZZLE_WB_RAD-2"=28 1/2"; RO=54 1/2"; RO/2=27 1/4"; RO2/2=27 1/4"; TRANSITION_TOP=104 1/4"; TYPE=12"; Type Comments=Vari-Plume Laboratory Exhaust Mixed-Flow High Pressure Inline Belt Drive With 1X2 Mixing Box With Weather Hoods On Sides; UNIT_HEIGHT=64"; UNIT_HEIGHT*.75=48"; UNIT_OD=51 3/4"; UNIT_RAD+((A/2)+.25")=57 1/8"; UNIT_RAD+((A/2)+.25")+4"=61 1/8"; UNIT_RADIUS=25 7/8"; UNIT_RADIUS*.6=23 9/32"; UNIT_RADIUS+4"=29 7/8"
- 365_QMXHPVP-27L-1X2_Mixing_Box_Ends: (A/2)+.25"=31 1/4"; (A/2)+.5"=-31 1/2"; (A/2)-.5"=-30 1/2"; (A/2)-2"=29"; (NOZZLE_HEIGHT-(NOZZLE_HEIGHT/8*2))/2=22 3/4"; (NOZZLE_WB_OD-NOZZLE_TOP_OD)/2=5 11/32"; -A=-62"; A=62"; A+.5=62 1/2"; A/2=31"; B=175"; B/2=87 1/2"; C=79"; C/2=39 1/2"; DUAL_F=159"; DUAL_F+1"=160"; DUAL_G=158"; E=60 3/4"; GA=3/32"; LONG_RO=151 3/4"; LONG_RO/2=75 7/8"; MB_A=82"; MB_HT=59 11/16"; MB_HT+.25"=59 15/16"; MB_HT-2.75"=56 15/16"; MB_HT/2=29 27/32"; Model=QMXHPVP-1X2_Mixing Box_Sides; NOZZLE_BOTTOM_ID=38 5/16"; NOZZLE_BOTTOM_RAD=19 5/32"; NOZZLE_HEIGHT=60 5/8"; NOZZLE_HEIGHT/7*2=15 5/32"; NOZZLE_SIZE=324"; NOZZLE_TOP_OD=39 11/16"; NOZZLE_TOP_RAD=19 27/32"; NOZZLE_WB/4=12 3/16"; NOZZLE_WB_OD=61"; NOZZLE_WB_RAD=30 1/2"; NOZZLE_WB_RAD-2"=28 1/2"; RO=54 1/2"; RO/2=27 1/4"; RO2/2=27 1/4"; TRANSITION_TOP=104 1/4"; TYPE=12"; Type Comments=Vari-Plume Laboratory Exhaust Mixed-Flow High Pressure Inline Belt Drive With 1X2 Mixing Box With Weather Hoods On Sides; UNIT_HEIGHT=64"; UNIT_HEIGHT*.75=48"; UNIT_OD=51 3/4"; UNIT_RAD+((A/2)+.25")=57 1/8"; UNIT_RAD+((A/2)+.25")+4"=61 1/8"; UNIT_RADIUS=25 7/8"; UNIT_RADIUS*.6=23 9/32"; UNIT_RADIUS+4"=29 7/8"
- 365_QMXVP-27H-1X2_Mixing_Box_Ends: (A/2)+.25"=31 1/4"; (A/2)+.5"=-31 1/2"; (A/2)-.5"=-30 1/2"; (A/2)-2"=29"; (NOZZLE_HEIGHT-(NOZZLE_HEIGHT/8*2))/2=22 3/4"; (NOZZLE_WB_OD-NOZZLE_TOP_OD)/2=5 11/32"; -A=-62"; A=62"; A+.5=62 1/2"; A/2=31"; B=175"; B/2=87 1/2"; C=79"; C/2=39 1/2"; DUAL_F=159"; DUAL_F+1"=160"; DUAL_G=158"; E=60 3/4"; GA=3/32"; LONG_RO=151 3/4"; LONG_RO/2=75 7/8"; MB_A=82"; MB_HT=59 11/16"; MB_HT+.25"=59 15/16"; MB_HT-2.75"=56 15/16"; MB_HT/2=29 27/32"; Model=QMXVP-1X2_Mixing Box_Sides; NOZZLE_BOTTOM_ID=38 5/16"; NOZZLE_BOTTOM_RAD=19 5/32"; NOZZLE_HEIGHT=60 5/8"; NOZZLE_HEIGHT/7*2=15 5/32"; NOZZLE_SIZE=324"; NOZZLE_TOP_OD=39 11/16"; NOZZLE_TOP_RAD=19 27/32"; NOZZLE_WB/4=12 3/16"; NOZZLE_WB_OD=61"; NOZZLE_WB_RAD=30 1/2"; NOZZLE_WB_RAD-2"=28 1/2"; RO=54 1/2"; RO/2=27 1/4"; RO2/2=27 1/4"; TRANSITION_TOP=104 1/4"; TYPE=0"; Type Comments=Vari-Plume Laboratory Exhaust Mixed-Flow Inline Belt Drive With 1X2 Mixing Box With Weather Hoods On Sides; UNIT_HEIGHT=64"; UNIT_HEIGHT*.75=48"; UNIT_OD=51 3/4"; UNIT_RAD+((A/2)+.25")=57 1/8"; UNIT_RAD+((A/2)+.25")+4"=61 1/8"; UNIT_RADIUS=25 7/8"; UNIT_RADIUS*.6=23 9/32"; UNIT_RADIUS+4"=29 7/8"
- 365_QMXVP-27L-1X2_Mixing_Box_Ends: (A/2)+.25"=31 1/4"; (A/2)+.5"=-31 1/2"; (A/2)-.5"=-30 1/2"; (A/2)-2"=29"; (NOZZLE_HEIGHT-(NOZZLE_HEIGHT/8*2))/2=22 3/4"; (NOZZLE_WB_OD-NOZZLE_TOP_OD)/2=5 11/32"; -A=-62"; A=62"; A+.5=62 1/2"; A/2=31"; B=175"; B/2=87 1/2"; C=79"; C/2=39 1/2"; DUAL_F=159"; DUAL_F+1"=160"; DUAL_G=158"; E=60 3/4"; GA=3/32"; LONG_RO=151 3/4"; LONG_RO/2=75 7/8"; MB_A=82"; MB_HT=59 11/16"; MB_HT+.25"=59 15/16"; MB_HT-2.75"=56 15/16"; MB_HT/2=29 27/32"; Model=QMXVP-1X2_Mixing Box_Sides; NOZZLE_BOTTOM_ID=38 5/16"; NOZZLE_BOTTOM_RAD=19 5/32"; NOZZLE_HEIGHT=60 5/8"; NOZZLE_HEIGHT/7*2=15 5/32"; NOZZLE_SIZE=324"; NOZZLE_TOP_OD=39 11/16"; NOZZLE_TOP_RAD=19 27/32"; NOZZLE_WB/4=12 3/16"; NOZZLE_WB_OD=61"; NOZZLE_WB_RAD=30 1/2"; NOZZLE_WB_RAD-2"=28 1/2"; RO=54 1/2"; RO/2=27 1/4"; RO2/2=27 1/4"; TRANSITION_TOP=104 1/4"; TYPE=0"; Type Comments=Vari-Plume Laboratory Exhaust Mixed-Flow Inline Belt Drive With 1X2 Mixing Box With Weather Hoods On Sides; UNIT_HEIGHT=64"; UNIT_HEIGHT*.75=48"; UNIT_OD=51 3/4"; UNIT_RAD+((A/2)+.25")=57 1/8"; UNIT_RAD+((A/2)+.25")+4"=61 1/8"; UNIT_RADIUS=25 7/8"; UNIT_RADIUS*.6=23 9/32"; UNIT_RADIUS+4"=29 7/8"
- 402_QMXHPVP-27H-1X2_Mixing_Box_Ends: (A/2)+.25"=33 3/4"; (A/2)+.5"=-34"; (A/2)-.5"=-33"; (A/2)-2"=31 1/2"; (NOZZLE_HEIGHT-(NOZZLE_HEIGHT/8*2))/2=22 3/4"; (NOZZLE_WB_OD-NOZZLE_TOP_OD)/2=5 11/32"; -A=-67"; A=67"; A+.5=67 1/2"; A/2=33 1/2"; B=183"; B/2=91 1/2"; C=88"; C/2=44"; DUAL_F=164"; DUAL_F+1"=165"; DUAL_G=163"; E=65 3/4"; GA=3/32"; LONG_RO=156 3/4"; LONG_RO/2=78 3/8"; MB_A=90"; MB_HT=65 15/16"; MB_HT+.25"=66 3/16"; MB_HT-2.75"=63 3/16"; MB_HT/2=32 31/32"; Model=QMXHPVP-1X2_Mixing Box_Sides; NOZZLE_BOTTOM_ID=38 5/16"; NOZZLE_BOTTOM_RAD=19 5/32"; NOZZLE_HEIGHT=60 5/8"; NOZZLE_HEIGHT/7*2=15 5/32"; NOZZLE_SIZE=324"; NOZZLE_TOP_OD=39 11/16"; NOZZLE_TOP_RAD=19 27/32"; NOZZLE_WB/4=12 3/16"; NOZZLE_WB_OD=61"; NOZZLE_WB_RAD=30 1/2"; NOZZLE_WB_RAD-2"=28 1/2"; RO=59 7/16"; RO/2=29 23/32"; RO2/2=29 23/32"; TRANSITION_TOP=118 3/4"; TYPE=12"; Type Comments=Vari-Plume Laboratory Exhaust Mixed-Flow High Pressure Inline Belt Drive With 1X2 Mixing Box With Weather Hoods On Sides; UNIT_HEIGHT=68 1/2"; UNIT_HEIGHT*.75=51 3/8"; UNIT_OD=56 15/16"; UNIT_RAD+((A/2)+.25")=62 7/32"; UNIT_RAD+((A/2)+.25")+4"=66 7/32"; UNIT_RADIUS=28 15/32"; UNIT_RADIUS*.6=25 5/8"; UNIT_RADIUS+4"=32 15/32"
- 402_QMXHPVP-27L-1X2_Mixing_Box_Ends: (A/2)+.25"=33 3/4"; (A/2)+.5"=-34"; (A/2)-.5"=-33"; (A/2)-2"=31 1/2"; (NOZZLE_HEIGHT-(NOZZLE_HEIGHT/8*2))/2=22 3/4"; (NOZZLE_WB_OD-NOZZLE_TOP_OD)/2=5 11/32"; -A=-67"; A=67"; A+.5=67 1/2"; A/2=33 1/2"; B=183"; B/2=91 1/2"; C=88"; C/2=44"; DUAL_F=164"; DUAL_F+1"=165"; DUAL_G=163"; E=65 3/4"; GA=3/32"; LONG_RO=156 3/4"; LONG_RO/2=78 3/8"; MB_A=90"; MB_HT=65 15/16"; MB_HT+.25"=66 3/16"; MB_HT-2.75"=63 3/16"; MB_HT/2=32 31/32"; Model=QMXHPVP-1X2_Mixing Box_Sides; NOZZLE_BOTTOM_ID=38 5/16"; NOZZLE_BOTTOM_RAD=19 5/32"; NOZZLE_HEIGHT=60 5/8"; NOZZLE_HEIGHT/7*2=15 5/32"; NOZZLE_SIZE=324"; NOZZLE_TOP_OD=39 11/16"; NOZZLE_TOP_RAD=19 27/32"; NOZZLE_WB/4=12 3/16"; NOZZLE_WB_OD=61"; NOZZLE_WB_RAD=30 1/2"; NOZZLE_WB_RAD-2"=28 1/2"; RO=59 7/16"; RO/2=29 23/32"; RO2/2=29 23/32"; TRANSITION_TOP=118 3/4"; TYPE=12"; Type Comments=Vari-Plume Laboratory Exhaust Mixed-Flow High Pressure Inline Belt Drive With 1X2 Mixing Box With Weather Hoods On Sides; UNIT_HEIGHT=68 1/2"; UNIT_HEIGHT*.75=51 3/8"; UNIT_OD=56 15/16"; UNIT_RAD+((A/2)+.25")=62 7/32"; UNIT_RAD+((A/2)+.25")+4"=66 7/32"; UNIT_RADIUS=28 15/32"; UNIT_RADIUS*.6=25 5/8"; UNIT_RADIUS+4"=32 15/32"
- 402_QMXVP-27H-1X2_Mixing_Box_Ends: (A/2)+.25"=33 3/4"; (A/2)+.5"=-34"; (A/2)-.5"=-33"; (A/2)-2"=31 1/2"; (NOZZLE_HEIGHT-(NOZZLE_HEIGHT/8*2))/2=22 3/4"; (NOZZLE_WB_OD-NOZZLE_TOP_OD)/2=5 11/32"; -A=-67"; A=67"; A+.5=67 1/2"; A/2=33 1/2"; B=183"; B/2=91 1/2"; C=88"; C/2=44"; DUAL_F=164"; DUAL_F+1"=165"; DUAL_G=163"; E=65 3/4"; GA=3/32"; LONG_RO=156 3/4"; LONG_RO/2=78 3/8"; MB_A=90"; MB_HT=65 15/16"; MB_HT+.25"=66 3/16"; MB_HT-2.75"=63 3/16"; MB_HT/2=32 31/32"; Model=QMXVP-1X2_Mixing Box_Sides; NOZZLE_BOTTOM_ID=38 5/16"; NOZZLE_BOTTOM_RAD=19 5/32"; NOZZLE_HEIGHT=60 5/8"; NOZZLE_HEIGHT/7*2=15 5/32"; NOZZLE_SIZE=324"; NOZZLE_TOP_OD=39 11/16"; NOZZLE_TOP_RAD=19 27/32"; NOZZLE_WB/4=12 3/16"; NOZZLE_WB_OD=61"; NOZZLE_WB_RAD=30 1/2"; NOZZLE_WB_RAD-2"=28 1/2"; RO=59 7/16"; RO/2=29 23/32"; RO2/2=29 23/32"; TRANSITION_TOP=118 3/4"; TYPE=0"; Type Comments=Vari-Plume Laboratory Exhaust Mixed-Flow Inline Belt Drive With 1X2 Mixing Box With Weather Hoods On Sides; UNIT_HEIGHT=68 1/2"; UNIT_HEIGHT*.75=51 3/8"; UNIT_OD=56 15/16"; UNIT_RAD+((A/2)+.25")=62 7/32"; UNIT_RAD+((A/2)+.25")+4"=66 7/32"; UNIT_RADIUS=28 15/32"; UNIT_RADIUS*.6=25 5/8"; UNIT_RADIUS+4"=32 15/32"
- 402_QMXVP-27L-1X2_Mixing_Box_Ends: (A/2)+.25"=33 3/4"; (A/2)+.5"=-34"; (A/2)-.5"=-33"; (A/2)-2"=31 1/2"; (NOZZLE_HEIGHT-(NOZZLE_HEIGHT/8*2))/2=22 3/4"; (NOZZLE_WB_OD-NOZZLE_TOP_OD)/2=5 11/32"; -A=-67"; A=67"; A+.5=67 1/2"; A/2=33 1/2"; B=183"; B/2=91 1/2"; C=88"; C/2=44"; DUAL_F=164"; DUAL_F+1"=165"; DUAL_G=163"; E=65 3/4"; GA=3/32"; LONG_RO=156 3/4"; LONG_RO/2=78 3/8"; MB_A=90"; MB_HT=65 15/16"; MB_HT+.25"=66 3/16"; MB_HT-2.75"=63 3/16"; MB_HT/2=32 31/32"; Model=QMXVP-1X2_Mixing Box_Sides; NOZZLE_BOTTOM_ID=38 5/16"; NOZZLE_BOTTOM_RAD=19 5/32"; NOZZLE_HEIGHT=60 5/8"; NOZZLE_HEIGHT/7*2=15 5/32"; NOZZLE_SIZE=324"; NOZZLE_TOP_OD=39 11/16"; NOZZLE_TOP_RAD=19 27/32"; NOZZLE_WB/4=12 3/16"; NOZZLE_WB_OD=61"; NOZZLE_WB_RAD=30 1/2"; NOZZLE_WB_RAD-2"=28 1/2"; RO=59 7/16"; RO/2=29 23/32"; RO2/2=29 23/32"; TRANSITION_TOP=118 3/4"; TYPE=0"; Type Comments=Vari-Plume Laboratory Exhaust Mixed-Flow Inline Belt Drive With 1X2 Mixing Box With Weather Hoods On Sides; UNIT_HEIGHT=68 1/2"; UNIT_HEIGHT*.75=51 3/8"; UNIT_OD=56 15/16"; UNIT_RAD+((A/2)+.25")=62 7/32"; UNIT_RAD+((A/2)+.25")+4"=66 7/32"; UNIT_RADIUS=28 15/32"; UNIT_RADIUS*.6=25 5/8"; UNIT_RADIUS+4"=32 15/32"

## geometry (parser evidence)
native form markers: Sweep x2
no freeform markers — native parametric forms only
